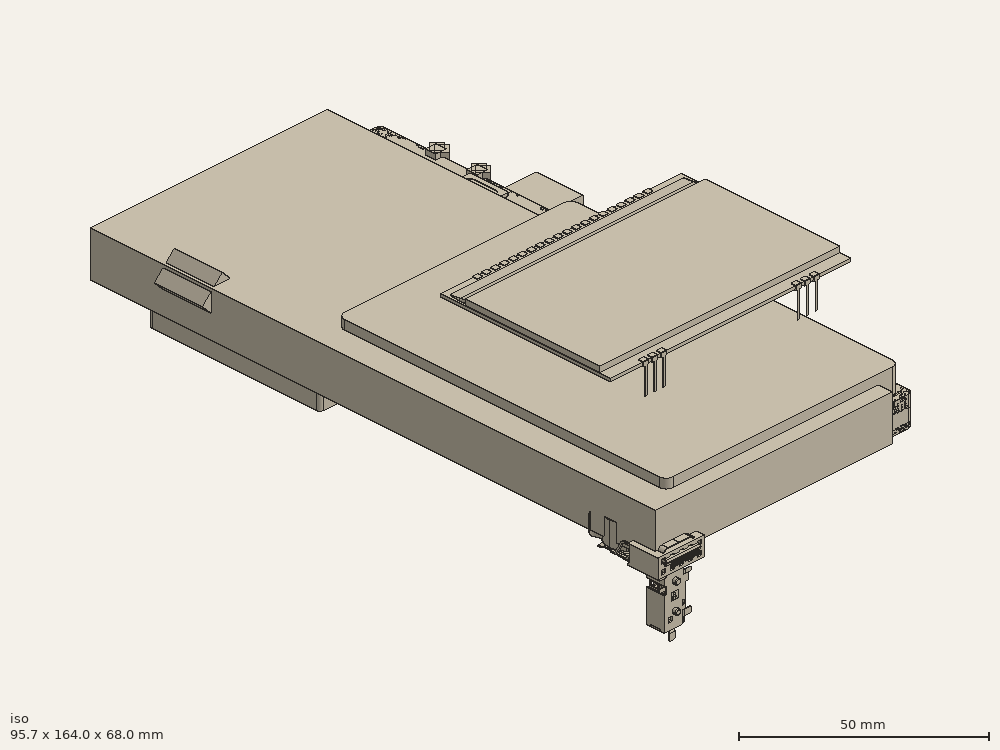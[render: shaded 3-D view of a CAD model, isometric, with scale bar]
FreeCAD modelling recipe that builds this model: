
FCSTD DOCUMENT  (FreeCAD 1.0R39109 (Git))
Label: case
License: All rights reserved
LicenseURL: https://en.wikipedia.org/wiki/All_rights_reserved
objects: Part::Feature×411, PartDesign::FeatureBase×405, PartDesign::Body×405, Part::Box×160, Part::MultiFuse×109, Part::Cylinder×108, Part::Cut×98, App::Part×86, Part::Extrusion×21, Part::Fillet×19, Sketcher::SketchObject×14, Part::Chamfer×13, Part::Compound×7, App::DocumentObjectGroup×3, Part::FeaturePython×1, Part::Sphere×1, Part::Face×1
note: 2192 computed .brp shape members not serialized (recipe doc carries the construction recipe); baked Part::Feature solids carry a one-line shape summary decoded from their .brp

FEATURE [Sketcher::SketchObject] Sketch
  ArcFitTolerance = 0
  FullyConstrained = false
  MakeInternals = false
  sketch-geometry (21):
    g0: ArcOfCircle CenterX=1.5 CenterY=149.5 CenterZ=0 NormalX=0 NormalY=0 NormalZ=1 AngleXU=0 Radius=1.5 StartAngle=1.5708 EndAngle=3.14159
    g1: LineSegment StartX=1.5 StartY=151 StartZ=0 EndX=68.5 EndY=151 EndZ=0
    g2: ArcOfCircle CenterX=68.5 CenterY=149.5 CenterZ=0 NormalX=0 NormalY=0 NormalZ=1 AngleXU=0 Radius=1.5 StartAngle=-8.9e-15 EndAngle=1.5708
    g3: LineSegment StartX=70 StartY=149.5 StartZ=0 EndX=70 EndY=1.5 EndZ=0
    g4: ArcOfCircle CenterX=68.5 CenterY=1.5 CenterZ=0 NormalX=0 NormalY=0 NormalZ=1 AngleXU=0 Radius=1.5 StartAngle=4.71239 EndAngle=6.28319
    g5: LineSegment StartX=68.5 StartY=0 StartZ=0 EndX=1.5 EndY=0 EndZ=0
    g6: ArcOfCircle CenterX=1.5 CenterY=1.5 CenterZ=0 NormalX=0 NormalY=0 NormalZ=1 AngleXU=0 Radius=1.5 StartAngle=3.14159 EndAngle=4.71239
    g7: LineSegment StartX=0 StartY=1.5 StartZ=0 EndX=0 EndY=149.5 EndZ=0
    g8: GeomPoint [constr] X=0 Y=151 Z=0
    g9: GeomPoint [constr] X=70 Y=0 Z=0
    g10: ArcOfCircle CenterX=4 CenterY=139.95 CenterZ=0 NormalX=0 NormalY=0 NormalZ=1 AngleXU=0 Radius=1 StartAngle=1.5708 EndAngle=3.14159
    g11: LineSegment StartX=4 StartY=140.95 StartZ=0 EndX=66 EndY=140.95 EndZ=0
    g12: ArcOfCircle CenterX=66 CenterY=139.95 CenterZ=0 NormalX=0 NormalY=0 NormalZ=1 AngleXU=0 Radius=1 StartAngle=-1.33e-14 EndAngle=1.5708
    g13: LineSegment StartX=67 StartY=139.95 StartZ=0 EndX=67 EndY=105.33 EndZ=0
    g14: ArcOfCircle CenterX=66 CenterY=105.33 CenterZ=0 NormalX=0 NormalY=0 NormalZ=1 AngleXU=0 Radius=1 StartAngle=4.71239 EndAngle=6.28319
    g15: LineSegment StartX=66 StartY=104.33 StartZ=0 EndX=4 EndY=104.33 EndZ=0
    g16: ArcOfCircle CenterX=4 CenterY=105.33 CenterZ=0 NormalX=0 NormalY=0 NormalZ=1 AngleXU=0 Radius=1 StartAngle=3.14159 EndAngle=4.71239
    g17: LineSegment StartX=3 StartY=105.33 StartZ=0 EndX=3 EndY=139.95 EndZ=0
    g18: GeomPoint [constr] X=3 Y=140.95 Z=0
    g19: GeomPoint [constr] X=67 Y=104.33 Z=0
    g20: LineSegment [constr] StartX=35 StartY=150.477 StartZ=0 EndX=35 EndY=137.578 EndZ=0
  constraints (50):
    c: Tangent(g0,g1) = 1.5708
    c: Tangent(g1,g2) = 1.5708
    c: Tangent(g2,g3) = 1.5708
    c: Tangent(g3,g4) = 1.5708
    c: Tangent(g4,g5) = 1.5708
    c: Tangent(g5,g6) = 1.5708
    c: Tangent(g6,g7) = 1.5708
    c: Tangent(g7,g0) = 1.5708
    c: Horizontal(g1)
    c: Horizontal(g5)
    c: Vertical(g3)
    c: Vertical(g7)
    c: Equal(g0,g2)
    c: Equal(g2,g4)
    c: Equal(g4,g6)
    c: PointOnObject(g8,g1)
    c: PointOnObject(g8,g7)
    c: PointOnObject(g9,g3)
    c: PointOnObject(g9,g5)
    c: PointOnObject(g9,g-1)
    c: Radius(g6) = 1.5
    c: DistanceY(g5,g0) = 151
    c: Vertical(g6,g-1)
    c: DistanceX(g0,g2) = 70
    c: Tangent(g10,g11) = 1.5708
    c: Tangent(g11,g12) = 1.5708
    c: Tangent(g12,g13) = 1.5708
    c: Tangent(g13,g14) = 1.5708
    c: Tangent(g14,g15) = 1.5708
    c: Tangent(g15,g16) = 1.5708
    c: Tangent(g16,g17) = 1.5708
    c: Tangent(g17,g10) = 1.5708
    c: Horizontal(g11)
    c: Horizontal(g15)
    c: Vertical(g13)
    c: Vertical(g17)
    c: Equal(g10,g12)
    c: Equal(g12,g14)
    c: Equal(g14,g16)
    c: PointOnObject(g18,g11)
    c: PointOnObject(g18,g17)
    c: PointOnObject(g19,g13)
    c: PointOnObject(g19,g15)
    c: Radius(g10) = 1
    c: DistanceY(g5,g15) = 104.33
    c: DistanceX(g10,g12) = 64
    c: DistanceY(g11,g1) = 10.05
    c: Vertical(g20)
    c: Symmetric(g2,g0,g20)
    c: Symmetric(g10,g11,g20)
FEATURE [Part::Extrusion] Extrude
  Base = -> Sketch
  Dir = (0,0,1)
  DirMode = 2
  FaceMakerClass = Part::FaceMakerBullseye
  FaceMakerMode = 3
  LengthFwd = 8
  LengthRev = 0
  Placement = pos=(0,0,8) rot=(0,0,1;0rad)
  Reversed = true
  Solid = true
  Symmetric = false
FEATURE [Sketcher::SketchObject] Sketch001
  ArcFitTolerance = 0
  AttachmentSupport = -> [Sketch]
  FullyConstrained = false
  MakeInternals = false
  MapMode = 2
  sketch-geometry (8):
    g0: ArcOfCircle CenterX=2 CenterY=149 CenterZ=0 NormalX=0 NormalY=0 NormalZ=1 AngleXU=0 Radius=1 StartAngle=1.5708 EndAngle=3.14159
    g1: LineSegment StartX=2 StartY=150 StartZ=0 EndX=68 EndY=150 EndZ=0
    g2: ArcOfCircle CenterX=68 CenterY=149 CenterZ=0 NormalX=0 NormalY=0 NormalZ=1 AngleXU=0 Radius=1 StartAngle=-9.8e-15 EndAngle=1.5708
    g3: LineSegment StartX=69 StartY=149 StartZ=0 EndX=69 EndY=99 EndZ=0
    g4: LineSegment StartX=69 StartY=99 StartZ=0 EndX=1 EndY=99 EndZ=0
    g5: LineSegment StartX=1 StartY=99 StartZ=0 EndX=1 EndY=149 EndZ=0
    g6: GeomPoint [constr] X=1 Y=150 Z=0
    g7: GeomPoint [constr] X=69 Y=99 Z=0
  constraints (16):
    c: Tangent(g0,g1) = 1.5708
    c: Tangent(g1,g2) = 1.5708
    c: Tangent(g2,g3) = 1.5708
    c: Tangent(g5,g0) = 1.5708
    c: Horizontal(g1)
    c: Horizontal(g4)
    c: Vertical(g3)
    c: Vertical(g5)
    c: Equal(g0,g2)
    c: PointOnObject(g6,g1)
    c: PointOnObject(g6,g5)
    c: PointOnObject(g7,g3)
    c: PointOnObject(g7,g4)
    c: Radius(g0) = 1
    c: Coincident(g5,g4)
    c: Coincident(g3,g4)
FEATURE [Part::Extrusion] Extrude001
  Base = -> Sketch001
  Dir = (0,0,1)
  DirMode = 2
  FaceMakerClass = Part::FaceMakerBullseye
  FaceMakerMode = 3
  LengthFwd = 11
  LengthRev = 0
  Placement = pos=(0,0,0.5) rot=(0,0,1;0rad)
  Solid = true
  Symmetric = false
FEATURE [Sketcher::SketchObject] Sketch002
  ArcFitTolerance = 0
  FullyConstrained = false
  MakeInternals = false
  sketch-geometry (20):
    g0: ArcOfCircle CenterX=3 CenterY=148 CenterZ=0 NormalX=0 NormalY=0 NormalZ=1 AngleXU=0 Radius=1 StartAngle=1.5708 EndAngle=3.14159
    g1: LineSegment StartX=3 StartY=149 StartZ=0 EndX=67 EndY=149 EndZ=0
    g2: ArcOfCircle CenterX=67 CenterY=148 CenterZ=0 NormalX=0 NormalY=0 NormalZ=1 AngleXU=0 Radius=1 StartAngle=5e-16 EndAngle=1.5708
    g3: LineSegment StartX=68 StartY=148 StartZ=0 EndX=68 EndY=101 EndZ=0
    g4: ArcOfCircle CenterX=67 CenterY=101 CenterZ=0 NormalX=0 NormalY=0 NormalZ=1 AngleXU=0 Radius=1 StartAngle=4.71239 EndAngle=6.28319
    g5: LineSegment StartX=67 StartY=100 StartZ=0 EndX=3 EndY=100 EndZ=0
    g6: ArcOfCircle CenterX=3 CenterY=101 CenterZ=0 NormalX=0 NormalY=0 NormalZ=1 AngleXU=0 Radius=1 StartAngle=3.14159 EndAngle=4.71239
    g7: LineSegment StartX=2 StartY=101 StartZ=0 EndX=2 EndY=148 EndZ=0
    g8: GeomPoint [constr] X=2 Y=149 Z=0
    g9: GeomPoint [constr] X=68 Y=100 Z=0
    g10: ArcOfCircle CenterX=3 CenterY=148 CenterZ=0 NormalX=0 NormalY=0 NormalZ=1 AngleXU=0 Radius=0.5 StartAngle=1.5708 EndAngle=3.14159
    g11: LineSegment StartX=3 StartY=148.5 StartZ=0 EndX=67 EndY=148.5 EndZ=0
    g12: ArcOfCircle CenterX=67 CenterY=148 CenterZ=0 NormalX=0 NormalY=0 NormalZ=1 AngleXU=0 Radius=0.5 StartAngle=-2.13e-14 EndAngle=1.5708
    g13: LineSegment StartX=67.5 StartY=148 StartZ=0 EndX=67.5 EndY=101 EndZ=0
    g14: ArcOfCircle CenterX=67 CenterY=101 CenterZ=0 NormalX=0 NormalY=0 NormalZ=1 AngleXU=0 Radius=0.5 StartAngle=4.71239 EndAngle=6.28319
    g15: LineSegment StartX=67 StartY=100.5 StartZ=0 EndX=3 EndY=100.5 EndZ=0
    g16: ArcOfCircle CenterX=3 CenterY=101 CenterZ=0 NormalX=0 NormalY=0 NormalZ=1 AngleXU=0 Radius=0.5 StartAngle=3.14159 EndAngle=4.71239
    g17: LineSegment StartX=2.5 StartY=101 StartZ=0 EndX=2.5 EndY=148 EndZ=0
    g18: GeomPoint [constr] X=2.5 Y=148.5 Z=0
    g19: GeomPoint [constr] X=67.5 Y=100.5 Z=0
  constraints (40):
    c: Tangent(g0,g1) = 1.5708
    c: Tangent(g1,g2) = 1.5708
    c: Tangent(g2,g3) = 1.5708
    c: Tangent(g3,g4) = 1.5708
    c: Tangent(g4,g5) = 1.5708
    c: Tangent(g5,g6) = 1.5708
    c: Tangent(g6,g7) = 1.5708
    c: Tangent(g7,g0) = 1.5708
    c: Horizontal(g1)
    c: Horizontal(g5)
    c: Vertical(g3)
    c: Vertical(g7)
    c: Equal(g0,g2)
    c: Equal(g2,g4)
    c: Equal(g4,g6)
    c: PointOnObject(g8,g1)
    c: PointOnObject(g8,g7)
    c: PointOnObject(g9,g3)
    c: PointOnObject(g9,g5)
    c: Radius(g2) = 1
    c: Tangent(g10,g11) = 1.5708
    c: Tangent(g11,g12) = 1.5708
    c: Tangent(g12,g13) = 1.5708
    c: Tangent(g13,g14) = 1.5708
    c: Tangent(g14,g15) = 1.5708
    c: Tangent(g15,g16) = 1.5708
    c: Tangent(g16,g17) = 1.5708
    c: Tangent(g17,g10) = 1.5708
    c: Horizontal(g11)
    c: Horizontal(g15)
    c: Vertical(g13)
    c: Vertical(g17)
    c: Equal(g10,g12)
    c: Equal(g12,g14)
    c: Equal(g14,g16)
    c: PointOnObject(g18,g11)
    c: PointOnObject(g18,g17)
    c: PointOnObject(g19,g13)
    c: PointOnObject(g19,g15)
    c: Radius(g10) = 0.5
FEATURE [Part::Extrusion] Extrude002
  Base = -> Sketch002
  Dir = (0,0,1)
  DirMode = 2
  FaceMakerClass = Part::FaceMakerBullseye
  FaceMakerMode = 3
  LengthFwd = 3
  LengthRev = 0
  Placement = pos=(0,0,0.2) rot=(0,0,1;0rad)
  Reversed = true
  Solid = true
  Symmetric = false
FEATURE [Sketcher::SketchObject] Sketch003
  ArcFitTolerance = 0
  FullyConstrained = false
  MakeInternals = false
  MapMode = 2
  sketch-geometry (10):
    g0: ArcOfCircle CenterX=3 CenterY=97 CenterZ=0 NormalX=0 NormalY=0 NormalZ=1 AngleXU=0 Radius=1 StartAngle=1.5708 EndAngle=3.14159
    g1: LineSegment StartX=3 StartY=98 StartZ=0 EndX=67 EndY=98 EndZ=0
    g2: ArcOfCircle CenterX=67 CenterY=97 CenterZ=0 NormalX=0 NormalY=0 NormalZ=1 AngleXU=0 Radius=1 StartAngle=-6.2e-15 EndAngle=1.5708
    g3: LineSegment StartX=68 StartY=97 StartZ=0 EndX=68 EndY=3 EndZ=0
    g4: ArcOfCircle CenterX=67 CenterY=3 CenterZ=0 NormalX=0 NormalY=0 NormalZ=1 AngleXU=0 Radius=1 StartAngle=4.71239 EndAngle=6.28319
    g5: LineSegment StartX=67 StartY=2 StartZ=0 EndX=3 EndY=2 EndZ=0
    g6: ArcOfCircle CenterX=3 CenterY=3 CenterZ=0 NormalX=0 NormalY=0 NormalZ=1 AngleXU=0 Radius=1 StartAngle=3.14159 EndAngle=4.71239
    g7: LineSegment StartX=2 StartY=3 StartZ=0 EndX=2 EndY=97 EndZ=0
    g8: GeomPoint [constr] X=2 Y=98 Z=0
    g9: GeomPoint [constr] X=68 Y=2 Z=0
  constraints (20):
    c: Tangent(g0,g1) = 1.5708
    c: Tangent(g1,g2) = 1.5708
    c: Tangent(g2,g3) = 1.5708
    c: Tangent(g3,g4) = 1.5708
    c: Tangent(g4,g5) = 1.5708
    c: Tangent(g5,g6) = 1.5708
    c: Tangent(g6,g7) = 1.5708
    c: Tangent(g7,g0) = 1.5708
    c: Horizontal(g1)
    c: Horizontal(g5)
    c: Vertical(g3)
    c: Vertical(g7)
    c: Equal(g0,g2)
    c: Equal(g2,g4)
    c: Equal(g4,g6)
    c: PointOnObject(g8,g1)
    c: PointOnObject(g8,g7)
    c: PointOnObject(g9,g3)
    c: PointOnObject(g9,g5)
    c: Radius(g2) = 1
FEATURE [Part::Extrusion] Extrude003
  Base = -> Sketch003
  Dir = (0,0,1)
  DirMode = 2
  FaceMakerClass = Part::FaceMakerBullseye
  FaceMakerMode = 3
  LengthFwd = 20
  LengthRev = 0
  Placement = pos=(0,0,15) rot=(0,0,1;0rad)
  Reversed = true
  Solid = true
  Symmetric = false
FEATURE [Sketcher::SketchObject] Sketch005
  ArcFitTolerance = 0
  FullyConstrained = true
  MakeInternals = false
  MapMode = 2
  sketch-geometry (10):
    g0: ArcOfCircle CenterX=-3 CenterY=2 CenterZ=0 NormalX=0 NormalY=0 NormalZ=1 AngleXU=0 Radius=1 StartAngle=1.5708 EndAngle=3.14159
    g1: LineSegment StartX=-3 StartY=3 StartZ=0 EndX=3 EndY=3 EndZ=0
    g2: ArcOfCircle CenterX=3 CenterY=2 CenterZ=0 NormalX=0 NormalY=0 NormalZ=1 AngleXU=0 Radius=1 StartAngle=2e-16 EndAngle=1.5708
    g3: LineSegment StartX=4 StartY=2 StartZ=0 EndX=4 EndY=-2 EndZ=0
    g4: ArcOfCircle CenterX=3 CenterY=-2 CenterZ=0 NormalX=0 NormalY=0 NormalZ=1 AngleXU=0 Radius=1 StartAngle=4.71239 EndAngle=6.28319
    g5: LineSegment StartX=3 StartY=-3 StartZ=0 EndX=-3 EndY=-3 EndZ=0
    g6: ArcOfCircle CenterX=-3 CenterY=-2 CenterZ=0 NormalX=0 NormalY=0 NormalZ=1 AngleXU=0 Radius=1 StartAngle=3.14159 EndAngle=4.71239
    g7: LineSegment StartX=-4 StartY=-2 StartZ=0 EndX=-4 EndY=2 EndZ=0
    g8: GeomPoint [constr] X=-4 Y=3 Z=0
    g9: GeomPoint [constr] X=4 Y=-3 Z=0
  constraints (22):
    c: Tangent(g0,g1) = 1.5708
    c: Tangent(g1,g2) = 1.5708
    c: Tangent(g2,g3) = 1.5708
    c: Tangent(g3,g4) = 1.5708
    c: Tangent(g4,g5) = 1.5708
    c: Tangent(g5,g6) = 1.5708
    c: Tangent(g6,g7) = 1.5708
    c: Tangent(g7,g0) = 1.5708
    c: Horizontal(g1)
    c: Horizontal(g5)
    c: Vertical(g3)
    c: Vertical(g7)
    c: Equal(g2,g4)
    c: PointOnObject(g8,g1)
    c: PointOnObject(g8,g7)
    c: PointOnObject(g9,g3)
    c: PointOnObject(g9,g5)
    c: Radius(g0) = 1
    c: DistanceX(g0,g2) = 8
    c: DistanceY(g5,g0) = 6
    c: Symmetric(g0,g2,g-2)
    c: Symmetric(g0,g5,g-1)
FEATURE [Part::Extrusion] Extrude006
  Base = -> Sketch005
  Dir = (0,0,1)
  DirMode = 2
  FaceMakerClass = Part::FaceMakerBullseye
  FaceMakerMode = 3
  LengthFwd = 2.5
  LengthRev = 1
  Solid = true
  Symmetric = false
FEATURE [Sketcher::SketchObject] Sketch007
  ArcFitTolerance = 0
  FullyConstrained = false
  MakeInternals = false
  Placement = pos=(0,0,0) rot=(0.57735,-0.57735,-0.57735;2.0944rad)
  sketch-geometry (6):
    g0: LineSegment StartX=-132.585 StartY=10 StartZ=0 EndX=-122.925 EndY=10 EndZ=0
    g1: LineSegment StartX=-132.585 StartY=10 StartZ=0 EndX=-132.585 EndY=5.74127 EndZ=0
    g2: LineSegment StartX=-122.925 StartY=10 StartZ=0 EndX=-122.925 EndY=5.74127 EndZ=0
    g3: LineSegment StartX=-131.085 StartY=4.24127 StartZ=0 EndX=-124.425 EndY=4.24127 EndZ=0
    g4: ArcOfCircle CenterX=-131.085 CenterY=5.74127 CenterZ=0 NormalX=0 NormalY=0 NormalZ=1 AngleXU=0 Radius=1.5 StartAngle=3.14159 EndAngle=4.71239
    g5: ArcOfCircle CenterX=-124.425 CenterY=5.74127 CenterZ=0 NormalX=0 NormalY=0 NormalZ=1 AngleXU=0 Radius=1.5 StartAngle=4.71239 EndAngle=6.28319
  constraints (12):
    c: Horizontal(g0)
    c: Coincident(g1,g0)
    c: Vertical(g1)
    c: Vertical(g2)
    c: Horizontal(g3)
    c: Radius(g4) = 1.5
    c: Tangent(g4,g1) = -1.5708
    c: Tangent(g4,g3) = -1.5708
    c: Tangent(g5,g2) = 1.5708
    c: Tangent(g5,g3) = -1.5708
    c: Radius(g5) = 1.5
    c: Coincident(g0,g2)
FEATURE [Part::Extrusion] Extrude008  label="USB"
  Base = -> Sketch007
  Dir = (-1,0,0)
  DirMode = 2
  FaceMakerClass = Part::FaceMakerBullseye
  FaceMakerMode = 3
  LengthFwd = 10
  LengthRev = 0
  Solid = true
  Symmetric = true
FEATURE [Part::Box] Box  label="LCD"
  AttacherType = Attacher::AttachEngine3D
  Height = 2.8
  Length = 67.8
  Placement = pos=(1,101,1.5) rot=(0,0,1;0rad)
  Width = 48
FEATURE [Sketcher::SketchObject] Sketch008
  ArcFitTolerance = 0
  FullyConstrained = false
  MakeInternals = false
  sketch-geometry (10):
    g0: ArcOfCircle CenterX=4 CenterY=93 CenterZ=0 NormalX=0 NormalY=0 NormalZ=1 AngleXU=0 Radius=2 StartAngle=1.5708 EndAngle=3.14159
    g1: LineSegment StartX=4 StartY=95 StartZ=0 EndX=66 EndY=95 EndZ=0
    g2: ArcOfCircle CenterX=66 CenterY=93 CenterZ=0 NormalX=0 NormalY=0 NormalZ=1 AngleXU=0 Radius=2 StartAngle=2.6e-15 EndAngle=1.5708
    g3: LineSegment StartX=68 StartY=93 StartZ=0 EndX=68 EndY=4 EndZ=0
    g4: ArcOfCircle CenterX=66 CenterY=4 CenterZ=0 NormalX=0 NormalY=0 NormalZ=1 AngleXU=0 Radius=2 StartAngle=4.71239 EndAngle=6.28319
    g5: LineSegment StartX=66 StartY=2 StartZ=0 EndX=4 EndY=2 EndZ=0
    g6: ArcOfCircle CenterX=4 CenterY=4 CenterZ=0 NormalX=0 NormalY=0 NormalZ=1 AngleXU=0 Radius=2 StartAngle=3.14159 EndAngle=4.71239
    g7: LineSegment StartX=2 StartY=4 StartZ=0 EndX=2 EndY=93 EndZ=0
    g8: GeomPoint [constr] X=2 Y=95 Z=0
    g9: GeomPoint [constr] X=68 Y=2 Z=0
  constraints (20):
    c: Tangent(g0,g1) = 1.5708
    c: Tangent(g1,g2) = 1.5708
    c: Tangent(g2,g3) = 1.5708
    c: Tangent(g3,g4) = 1.5708
    c: Tangent(g4,g5) = 1.5708
    c: Tangent(g5,g6) = 1.5708
    c: Tangent(g6,g7) = 1.5708
    c: Tangent(g7,g0) = 1.5708
    c: Horizontal(g1)
    c: Horizontal(g5)
    c: Vertical(g3)
    c: Vertical(g7)
    c: Equal(g0,g2)
    c: Equal(g2,g4)
    c: Equal(g4,g6)
    c: PointOnObject(g8,g1)
    c: PointOnObject(g8,g7)
    c: PointOnObject(g9,g3)
    c: PointOnObject(g9,g5)
    c: Radius(g0) = 2
FEATURE [Part::Extrusion] Extrude009
  Base = -> Sketch008
  Dir = (0,0,1)
  DirMode = 2
  FaceMakerClass = Part::FaceMakerBullseye
  FaceMakerMode = 3
  LengthFwd = 11
  LengthRev = 0
  Placement = pos=(0,0,3.5) rot=(0,0,1;0rad)
  Solid = true
  Symmetric = false
FEATURE [Sketcher::SketchObject] Sketch010
  ArcFitTolerance = 0
  FullyConstrained = false
  MakeInternals = false
  MapMode = 4
  Placement = pos=(0,0,0) rot=(0.707107,0,0.707107;3.14159rad)
  sketch-geometry (4):
    g0: LineSegment StartX=-2 StartY=3.98958 StartZ=0 EndX=-0.388491 EndY=3.98958 EndZ=0
    g1: LineSegment StartX=-0.388491 StartY=3.98958 StartZ=0 EndX=-1 EndY=-3 EndZ=0
    g2: LineSegment StartX=-1 StartY=-3 StartZ=0 EndX=-2 EndY=-3 EndZ=0
    g3: LineSegment StartX=-2 StartY=-3 StartZ=0 EndX=-2 EndY=3.98958 EndZ=0
  constraints (10):
    c: Horizontal(g0)
    c: Coincident(g0,g1)
    c: Coincident(g1,g2)
    c: Horizontal(g2)
    c: Coincident(g2,g3)
    c: Coincident(g3,g0)
    c: Vertical(g3)
    c: Angle(g1,g3) = 0.0872665
    c: DistanceX(g1,g-1) = 1
    c: DistanceY(g1,g-1) = 3
FEATURE [Part::Extrusion] Extrude011
  Base = -> Sketch010
  Dir = (1,0,-2e-16)
  DirMode = 2
  FaceMakerClass = Part::FaceMakerBullseye
  FaceMakerMode = 3
  LengthFwd = 10
  LengthRev = 0
  Solid = true
  Symmetric = true
FEATURE [Part::Cut] Cut004
  Base = -> Extrude006
  Tool = -> Extrude011
FEATURE [Part::Fillet] Fillet
  Base = -> Cut004
  EdgeLinks = -> Cut004 [Edge5,Edge7,Edge9,Edge11]
  Edges = 4 edges r=1: [Edge5,Edge7,Edge9,Edge11]
  Placement = pos=(0,0,1) rot=(0,0,1;0rad)
FEATURE [Part::Cylinder] Cylinder
  Angle = 360
  AttacherType = Attacher::AttachEngine3D
  FirstAngle = 0
  Height = 5
  Placement = pos=(0,0,2) rot=(0,0,1;0rad)
  Radius = 1.5
  SecondAngle = 0
FEATURE [Part::Fillet] Fillet002
  Base = -> Cylinder
  EdgeLinks = -> Cylinder [Edge3]
  Edges = 1 edges r=1: [Edge3]
  Placement = pos=(0,0,0.5) rot=(0,0,1;0rad)
FEATURE [Part::Box] Box001  label="Cube"
  AttacherType = Attacher::AttachEngine3D
  Height = 12
  Length = 67
  Placement = pos=(-5,-2,0) rot=(0,0,1;0rad)
  Width = 160
FEATURE [Sketcher::SketchObject] Sketch011
  ArcFitTolerance = 0
  AttachmentSupport = -> [Sketch]
  FullyConstrained = false
  MakeInternals = false
  MapMode = 2
  sketch-geometry (28):
    g0: ArcOfCircle CenterX=-3 CenterY=2 CenterZ=0 NormalX=0 NormalY=0 NormalZ=1 AngleXU=0 Radius=1.5 StartAngle=1.5708 EndAngle=3.14159
    g1: ArcOfCircle CenterX=3 CenterY=2 CenterZ=0 NormalX=0 NormalY=0 NormalZ=1 AngleXU=0 Radius=1.5 StartAngle=1e-16 EndAngle=1.5708
    g2: LineSegment StartX=4.5 StartY=2 StartZ=0 EndX=4.5 EndY=-2 EndZ=0
    g3: ArcOfCircle CenterX=3 CenterY=-2 CenterZ=0 NormalX=0 NormalY=0 NormalZ=1 AngleXU=0 Radius=1.5 StartAngle=4.71239 EndAngle=6.28319
    g4: ArcOfCircle CenterX=-3 CenterY=-2 CenterZ=0 NormalX=0 NormalY=0 NormalZ=1 AngleXU=0 Radius=1.5 StartAngle=3.14159 EndAngle=4.71239
    g5: LineSegment StartX=-4.5 StartY=-2 StartZ=0 EndX=-4.5 EndY=2 EndZ=0
    g6: GeomPoint [constr] X=-4.5 Y=3.5 Z=0
    g7: GeomPoint [constr] X=4.5 Y=-4 Z=0
    g8: LineSegment StartX=-2.8 StartY=-5 StartZ=0 EndX=-2.5 EndY=-5 EndZ=0
    g9: LineSegment StartX=-2.5 StartY=-5 StartZ=0 EndX=-2.5 EndY=-2 EndZ=0
    g10: LineSegment StartX=-2.5 StartY=-2 StartZ=0 EndX=-2.2 EndY=-2 EndZ=0
    g11: LineSegment StartX=-2.2 StartY=-2 StartZ=0 EndX=-2.2 EndY=-5 EndZ=0
    g12: LineSegment StartX=2.2 StartY=-5 StartZ=0 EndX=2.2 EndY=-2 EndZ=0
    g13: LineSegment StartX=2.2 StartY=-2 StartZ=0 EndX=2.5 EndY=-2 EndZ=0
    g14: LineSegment StartX=2.5 StartY=-2 StartZ=0 EndX=2.5 EndY=-5 EndZ=0
    g15: LineSegment StartX=2.5 StartY=-5 StartZ=0 EndX=2.8 EndY=-5 EndZ=0
    g16: LineSegment StartX=-2.2 StartY=-5 StartZ=0 EndX=-1.9 EndY=-5 EndZ=0
    g17: LineSegment StartX=-1.9 StartY=-5 StartZ=0 EndX=-1.9 EndY=-3.5 EndZ=0
    g18: LineSegment StartX=-1.9 StartY=-3.5 StartZ=0 EndX=1.9 EndY=-3.5 EndZ=0
    g19: LineSegment StartX=1.9 StartY=-3.5 StartZ=0 EndX=1.9 EndY=-5 EndZ=0
    g20: LineSegment StartX=1.9 StartY=-5 StartZ=0 EndX=2.2 EndY=-5 EndZ=0
    g21: LineSegment StartX=-2.8 StartY=-3.5 StartZ=0 EndX=-3 EndY=-3.5 EndZ=0
    g22: LineSegment StartX=-2.8 StartY=-3.5 StartZ=0 EndX=-2.8 EndY=-5 EndZ=0
    g23: LineSegment StartX=2.8 StartY=-3.5 StartZ=0 EndX=3 EndY=-3.5 EndZ=0
    g24: LineSegment StartX=2.8 StartY=-3.5 StartZ=0 EndX=2.8 EndY=-5 EndZ=0
    g25: ArcOfCircle CenterX=0 CenterY=2.95502 CenterZ=0 NormalX=0 NormalY=0 NormalZ=1 AngleXU=0 Radius=2.00619 StartAngle=0.275105 EndAngle=2.86649
    g26: LineSegment StartX=-3 StartY=3.5 StartZ=0 EndX=-1.93075 EndY=3.5 EndZ=0
    g27: LineSegment StartX=1.93075 StartY=3.5 StartZ=0 EndX=3 EndY=3.5 EndZ=0
  constraints (68):
    c: Tangent(g1,g2) = 1.5708
    c: Tangent(g2,g3) = 1.5708
    c: Tangent(g4,g5) = 1.5708
    c: Tangent(g5,g0) = 1.5708
    c: Vertical(g2)
    c: Horizontal(g8)
    c: Coincident(g8,g9)
    c: Vertical(g9)
    c: Coincident(g9,g10)
    c: Horizontal(g10)
    c: Coincident(g10,g11)
    c: Vertical(g11)
    c: Vertical(g12)
    c: Coincident(g12,g13)
    c: Horizontal(g13)
    c: Coincident(g13,g14)
    c: Vertical(g14)
    c: Coincident(g14,g15)
    c: Horizontal(g8,g11)
    c: Horizontal(g10,g12)
    c: Symmetric(g11,g12,g-2)
    c: DistanceX(g10,g10) = 0.3
    c: Coincident(g11,g16)
    c: Coincident(g16,g17)
    c: Vertical(g17)
    c: Coincident(g17,g18)
    c: Coincident(g18,g19)
    c: Vertical(g19)
    c: Coincident(g19,g20)
    c: Coincident(g20,g12)
    c: Horizontal(g20)
    c: Coincident(g21,g22)
    c: Coincident(g22,g8)
    c: Vertical(g22)
    c: Coincident(g23,g24)
    c: Coincident(g24,g15)
    c: Vertical(g24)
    c: Tangent(g3,g23) = -1.5708
    c: Tangent(g21,g4) = 1.5708
    c: Radius(g0) = 1.5
    c: Vertical(g5)
    c: Radius(g1) = 1.5
    c: Radius(g4) = 1.5
    c: Horizontal(g3,g23)
    c: Horizontal(g23,g18)
    c: Horizontal(g17,g21)
    c: Horizontal(g21,g4)
    c: Radius(g3) = 1.5
    c: Symmetric(g17,g18,g-2)
    c: Symmetric(g15,g8,g-2)
    c: Symmetric(g14,g8,g-2)
    c: Horizontal(g21)
    c: Horizontal(g18)
    c: Horizontal(g23)
    c: DistanceY(g4,g0) = 7
    c: DistanceX(g0,g1) = 9
    c: Symmetric(g0,g4,g-1)
    c: PointOnObject(g25,g-2)
    c: Horizontal(g0,g25)
    c: Horizontal(g25,g1)
    c: Horizontal(g1,g25)
    c: Coincident(g26,g0)
    c: Coincident(g26,g25)
    c: Horizontal(g26)
    c: Coincident(g27,g25)
    c: Coincident(g27,g1)
    c: Horizontal(g27)
    c: Tangent(g27,g1)
FEATURE [Part::Extrusion] Extrude012  label="CUT (type 01)"
  Base = -> Sketch011
  Dir = (0,0,1)
  DirMode = 2
  FaceMakerClass = Part::FaceMakerBullseye
  FaceMakerMode = 3
  LengthFwd = 10
  LengthRev = 0
  Solid = true
  Symmetric = false
FEATURE [PartDesign::FeatureBase] Clone
  BaseFeature = -> Extrude012
  Suppressed = false
FEATURE [PartDesign::Body] Body  label="C1-1"
  AllowCompound = false
  Group = -> [Clone]
  Origin = -> Origin046
  Placement = pos=(62.8,7,0) rot=(0,0,1;0rad)
  Tip = -> Clone
FEATURE [PartDesign::FeatureBase] Clone001
  BaseFeature = -> Extrude012
  Suppressed = false
FEATURE [PartDesign::Body] Body001  label="C2-1"
  AllowCompound = false
  Group = -> [Clone001]
  Origin = -> Origin047
  Placement = pos=(62.8,17,0) rot=(0,0,1;0rad)
  Tip = -> Clone001
FEATURE [PartDesign::FeatureBase] Clone002
  BaseFeature = -> Extrude012
  Suppressed = false
FEATURE [PartDesign::Body] Body002  label="C3-1"
  AllowCompound = false
  Group = -> [Clone002]
  Origin = -> Origin048
  Placement = pos=(62.8,27,0) rot=(0,0,1;0rad)
  Tip = -> Clone002
FEATURE [PartDesign::FeatureBase] Clone006
  BaseFeature = -> Extrude012
  Suppressed = false
FEATURE [PartDesign::Body] Body006  label="C4-1"
  AllowCompound = false
  Group = -> [Clone006]
  Origin = -> Origin052
  Placement = pos=(62.8,37,0) rot=(0,0,1;0rad)
  Tip = -> Clone006
FEATURE [PartDesign::FeatureBase] Clone007
  BaseFeature = -> Extrude012
  Suppressed = false
FEATURE [PartDesign::Body] Body007  label="C5-1"
  AllowCompound = false
  Group = -> [Clone007]
  Origin = -> Origin053
  Placement = pos=(62.8,49.98,0) rot=(0,0,1;0rad)
  Tip = -> Clone007
FEATURE [PartDesign::FeatureBase] Clone008
  BaseFeature = -> Extrude012
  Suppressed = false
FEATURE [PartDesign::Body] Body008  label="C6-1"
  AllowCompound = false
  Group = -> [Clone008]
  Origin = -> Origin054
  Placement = pos=(62.8,59.98,0) rot=(0,0,1;0rad)
  Tip = -> Clone008
FEATURE [PartDesign::FeatureBase] Clone009
  BaseFeature = -> Extrude012
  Suppressed = false
FEATURE [PartDesign::Body] Body009  label="C7-1"
  AllowCompound = false
  Group = -> [Clone009]
  Origin = -> Origin055
  Placement = pos=(62.8,69.98,0) rot=(0,0,1;0rad)
  Tip = -> Clone009
FEATURE [PartDesign::FeatureBase] Clone010
  BaseFeature = -> Extrude012
  Suppressed = false
FEATURE [PartDesign::Body] Body010  label="C8-1"
  AllowCompound = false
  Group = -> [Clone010]
  Origin = -> Origin056
  Placement = pos=(62.8,79.98,0) rot=(0,0,1;0rad)
  Tip = -> Clone010
FEATURE [PartDesign::FeatureBase] Clone011
  BaseFeature = -> Extrude012
  Suppressed = false
FEATURE [PartDesign::Body] Body011  label="C9-1"
  AllowCompound = false
  Group = -> [Clone011]
  Origin = -> Origin057
  Placement = pos=(62.8,89.98,0) rot=(0,0,1;0rad)
  Tip = -> Clone011
FEATURE [PartDesign::FeatureBase] Clone018
  BaseFeature = -> Extrude012
  Suppressed = false
FEATURE [PartDesign::Body] Body018  label="C5-2"
  AllowCompound = false
  Group = -> [Clone018]
  Origin = -> Origin064
  Placement = pos=(51.8,49.98,0) rot=(0,0,1;0rad)
  Tip = -> Clone018
FEATURE [PartDesign::FeatureBase] Clone020
  BaseFeature = -> Extrude012
  Suppressed = false
FEATURE [PartDesign::Body] Body020  label="C5-3"
  AllowCompound = false
  Group = -> [Clone020]
  Origin = -> Origin066
  Placement = pos=(40.8,49.98,0) rot=(0,0,1;0rad)
  Tip = -> Clone020
FEATURE [PartDesign::FeatureBase] Clone021
  BaseFeature = -> Extrude012
  Suppressed = false
FEATURE [PartDesign::Body] Body021  label="C5-4"
  AllowCompound = false
  Group = -> [Clone021]
  Origin = -> Origin067
  Placement = pos=(29.8,49.98,0) rot=(0,0,1;0rad)
  Tip = -> Clone021
FEATURE [PartDesign::FeatureBase] Clone022
  BaseFeature = -> Extrude012
  Suppressed = false
FEATURE [PartDesign::Body] Body022  label="C5-5"
  AllowCompound = false
  Group = -> [Clone022]
  Origin = -> Origin068
  Placement = pos=(18.8,49.98,0) rot=(0,0,1;0rad)
  Tip = -> Clone022
FEATURE [PartDesign::FeatureBase] Clone023
  BaseFeature = -> Extrude012
  Suppressed = false
FEATURE [PartDesign::Body] Body023  label="C5-6"
  AllowCompound = false
  Group = -> [Clone023]
  Origin = -> Origin069
  Placement = pos=(7.8,49.98,0) rot=(0,0,1;0rad)
  Tip = -> Clone023
FEATURE [PartDesign::FeatureBase] Clone028
  BaseFeature = -> Extrude012
  Suppressed = false
FEATURE [PartDesign::Body] Body028  label="C6-2"
  AllowCompound = false
  Group = -> [Clone028]
  Origin = -> Origin074
  Placement = pos=(51.8,59.98,0) rot=(0,0,1;0rad)
  Tip = -> Clone028
FEATURE [PartDesign::FeatureBase] Clone029
  BaseFeature = -> Extrude012
  Suppressed = false
FEATURE [PartDesign::Body] Body029  label="C6-3"
  AllowCompound = false
  Group = -> [Clone029]
  Origin = -> Origin075
  Placement = pos=(40.8,59.98,0) rot=(0,0,1;0rad)
  Tip = -> Clone029
FEATURE [PartDesign::FeatureBase] Clone030
  BaseFeature = -> Extrude012
  Suppressed = false
FEATURE [PartDesign::Body] Body030  label="C6-4"
  AllowCompound = false
  Group = -> [Clone030]
  Origin = -> Origin076
  Placement = pos=(29.8,59.98,0) rot=(0,0,1;0rad)
  Tip = -> Clone030
FEATURE [PartDesign::FeatureBase] Clone031
  BaseFeature = -> Extrude012
  Suppressed = false
FEATURE [PartDesign::Body] Body031  label="C6-5"
  AllowCompound = false
  Group = -> [Clone031]
  Origin = -> Origin077
  Placement = pos=(18.8,59.98,0) rot=(0,0,1;0rad)
  Tip = -> Clone031
FEATURE [PartDesign::FeatureBase] Clone032
  BaseFeature = -> Extrude012
  Suppressed = false
FEATURE [PartDesign::Body] Body032  label="C6-6"
  AllowCompound = false
  Group = -> [Clone032]
  Origin = -> Origin078
  Placement = pos=(7.8,59.98,0) rot=(0,0,1;0rad)
  Tip = -> Clone032
FEATURE [PartDesign::FeatureBase] Clone033
  BaseFeature = -> Extrude012
  Suppressed = false
FEATURE [PartDesign::Body] Body033  label="C7-2"
  AllowCompound = false
  Group = -> [Clone033]
  Origin = -> Origin079
  Placement = pos=(51.8,69.98,0) rot=(0,0,1;0rad)
  Tip = -> Clone033
FEATURE [PartDesign::FeatureBase] Clone034
  BaseFeature = -> Extrude012
  Suppressed = false
FEATURE [PartDesign::Body] Body034  label="C7-3"
  AllowCompound = false
  Group = -> [Clone034]
  Origin = -> Origin080
  Placement = pos=(40.8,69.98,0) rot=(0,0,1;0rad)
  Tip = -> Clone034
FEATURE [PartDesign::FeatureBase] Clone035
  BaseFeature = -> Extrude012
  Suppressed = false
FEATURE [PartDesign::Body] Body035  label="C7-4"
  AllowCompound = false
  Group = -> [Clone035]
  Origin = -> Origin081
  Placement = pos=(29.8,69.98,0) rot=(0,0,1;0rad)
  Tip = -> Clone035
FEATURE [PartDesign::FeatureBase] Clone036
  BaseFeature = -> Extrude012
  Suppressed = false
FEATURE [PartDesign::Body] Body036  label="C7-5"
  AllowCompound = false
  Group = -> [Clone036]
  Origin = -> Origin082
  Placement = pos=(18.8,69.98,0) rot=(0,0,1;0rad)
  Tip = -> Clone036
FEATURE [PartDesign::FeatureBase] Clone037
  BaseFeature = -> Extrude012
  Suppressed = false
FEATURE [PartDesign::Body] Body037  label="C7-6"
  AllowCompound = false
  Group = -> [Clone037]
  Origin = -> Origin083
  Placement = pos=(7.8,69.98,0) rot=(0,0,1;0rad)
  Tip = -> Clone037
FEATURE [PartDesign::FeatureBase] Clone038
  BaseFeature = -> Extrude012
  Suppressed = false
FEATURE [PartDesign::Body] Body038  label="C8-2"
  AllowCompound = false
  Group = -> [Clone038]
  Origin = -> Origin084
  Placement = pos=(51.8,79.98,0) rot=(0,0,1;0rad)
  Tip = -> Clone038
FEATURE [PartDesign::FeatureBase] Clone039
  BaseFeature = -> Extrude012
  Suppressed = false
FEATURE [PartDesign::Body] Body039  label="C8-3"
  AllowCompound = false
  Group = -> [Clone039]
  Origin = -> Origin085
  Placement = pos=(40.8,79.98,0) rot=(0,0,1;0rad)
  Tip = -> Clone039
FEATURE [PartDesign::FeatureBase] Clone040
  BaseFeature = -> Extrude012
  Suppressed = false
FEATURE [PartDesign::Body] Body040  label="C8-4"
  AllowCompound = false
  Group = -> [Clone040]
  Origin = -> Origin086
  Placement = pos=(29.8,79.98,0) rot=(0,0,1;0rad)
  Tip = -> Clone040
FEATURE [PartDesign::FeatureBase] Clone041
  BaseFeature = -> Extrude012
  Suppressed = false
FEATURE [PartDesign::Body] Body041  label="C8-5"
  AllowCompound = false
  Group = -> [Clone041]
  Origin = -> Origin087
  Placement = pos=(18.8,79.98,0) rot=(0,0,1;0rad)
  Tip = -> Clone041
FEATURE [PartDesign::FeatureBase] Clone042
  BaseFeature = -> Extrude012
  Suppressed = false
FEATURE [PartDesign::Body] Body042  label="C8-6"
  AllowCompound = false
  Group = -> [Clone042]
  Origin = -> Origin088
  Placement = pos=(7.8,79.98,0) rot=(0,0,1;0rad)
  Tip = -> Clone042
FEATURE [PartDesign::FeatureBase] Clone043
  BaseFeature = -> Extrude012
  Suppressed = false
FEATURE [PartDesign::Body] Body043  label="C9-2"
  AllowCompound = false
  Group = -> [Clone043]
  Origin = -> Origin089
  Placement = pos=(51.8,89.98,0) rot=(0,0,1;0rad)
  Tip = -> Clone043
FEATURE [PartDesign::FeatureBase] Clone044
  BaseFeature = -> Extrude012
  Suppressed = false
FEATURE [PartDesign::Body] Body044  label="C9-3"
  AllowCompound = false
  Group = -> [Clone044]
  Origin = -> Origin090
  Placement = pos=(40.8,89.98,0) rot=(0,0,1;0rad)
  Tip = -> Clone044
FEATURE [PartDesign::FeatureBase] Clone045
  BaseFeature = -> Extrude012
  Suppressed = false
FEATURE [PartDesign::Body] Body045  label="C9-4"
  AllowCompound = false
  Group = -> [Clone045]
  Origin = -> Origin091
  Placement = pos=(29.8,89.98,0) rot=(0,0,1;0rad)
  Tip = -> Clone045
FEATURE [PartDesign::FeatureBase] Clone046
  BaseFeature = -> Extrude012
  Suppressed = false
FEATURE [PartDesign::Body] Body046  label="C9-5"
  AllowCompound = false
  Group = -> [Clone046]
  Origin = -> Origin092
  Placement = pos=(18.8,89.98,0) rot=(0,0,1;0rad)
  Tip = -> Clone046
FEATURE [PartDesign::FeatureBase] Clone047
  BaseFeature = -> Extrude012
  Suppressed = false
FEATURE [PartDesign::Body] Body047  label="C9-6"
  AllowCompound = false
  Group = -> [Clone047]
  Origin = -> Origin093
  Placement = pos=(7.8,89.98,0) rot=(0,0,1;0rad)
  Tip = -> Clone047
FEATURE [Part::Cylinder] Cylinder001  label="LED01"
  Angle = 360
  AttacherType = Attacher::AttachEngine3D
  FirstAngle = 0
  Height = 10
  Placement = pos=(18.5,95.75,0) rot=(0,0,1;0rad)
  Radius = 0.5
  SecondAngle = 0
FEATURE [Part::Cylinder] Cylinder002
  Angle = 360
  AttacherType = Attacher::AttachEngine3D
  FirstAngle = 0
  Height = 5
  Placement = pos=(0,0,2) rot=(0,0,1;0rad)
  Radius = 1.5
  SecondAngle = 0
FEATURE [Part::Fillet] Fillet005
  Base = -> Cylinder002
  EdgeLinks = -> Cylinder002 [Edge3]
  Edges = 1 edges r=1: [Edge3]
  Placement = pos=(0,0,0.5) rot=(0,0,1;0rad)
FEATURE [Sketcher::SketchObject] Sketch012
  ArcFitTolerance = 0
  FullyConstrained = true
  MakeInternals = false
  MapMode = 2
  sketch-geometry (10):
    g0: ArcOfCircle CenterX=-4 CenterY=2 CenterZ=0 NormalX=0 NormalY=0 NormalZ=1 AngleXU=0 Radius=1 StartAngle=1.5708 EndAngle=3.14159
    g1: LineSegment StartX=-4 StartY=3 StartZ=0 EndX=4 EndY=3 EndZ=0
    g2: ArcOfCircle CenterX=4 CenterY=2 CenterZ=0 NormalX=0 NormalY=0 NormalZ=1 AngleXU=0 Radius=1 StartAngle=-5.071e-13 EndAngle=1.5708
    g3: LineSegment StartX=5 StartY=2 StartZ=0 EndX=5 EndY=-2 EndZ=0
    g4: ArcOfCircle CenterX=4 CenterY=-2 CenterZ=0 NormalX=0 NormalY=0 NormalZ=1 AngleXU=0 Radius=1 StartAngle=4.71239 EndAngle=6.28319
    g5: LineSegment StartX=4 StartY=-3 StartZ=0 EndX=-4 EndY=-3 EndZ=0
    g6: ArcOfCircle CenterX=-4 CenterY=-2 CenterZ=0 NormalX=0 NormalY=0 NormalZ=1 AngleXU=0 Radius=1 StartAngle=3.14159 EndAngle=4.71239
    g7: LineSegment StartX=-5 StartY=-2 StartZ=0 EndX=-5 EndY=2 EndZ=0
    g8: GeomPoint [constr] X=-5 Y=3 Z=0
    g9: GeomPoint [constr] X=5 Y=-3 Z=0
  constraints (22):
    c: Tangent(g0,g1) = 1.5708
    c: Tangent(g1,g2) = 1.5708
    c: Tangent(g2,g3) = 1.5708
    c: Tangent(g3,g4) = 1.5708
    c: Tangent(g4,g5) = 1.5708
    c: Tangent(g5,g6) = 1.5708
    c: Tangent(g6,g7) = 1.5708
    c: Tangent(g7,g0) = 1.5708
    c: Horizontal(g1)
    c: Horizontal(g5)
    c: Vertical(g3)
    c: Vertical(g7)
    c: Equal(g2,g4)
    c: PointOnObject(g8,g1)
    c: PointOnObject(g8,g7)
    c: PointOnObject(g9,g3)
    c: PointOnObject(g9,g5)
    c: Radius(g0) = 1
    c: DistanceX(g0,g2) = 10
    c: DistanceY(g5,g0) = 6
    c: Symmetric(g0,g2,g-2)
    c: Symmetric(g0,g5,g-1)
FEATURE [Part::Extrusion] Extrude013
  Base = -> Sketch012
  Dir = (0,0,1)
  DirMode = 2
  FaceMakerClass = Part::FaceMakerBullseye
  FaceMakerMode = 3
  LengthFwd = 2.5
  LengthRev = 1
  Solid = true
  Symmetric = false
FEATURE [Sketcher::SketchObject] Sketch013
  ArcFitTolerance = 0
  FullyConstrained = false
  MakeInternals = false
  MapMode = 4
  Placement = pos=(0,0,0) rot=(0.707107,0,0.707107;3.14159rad)
  sketch-geometry (4):
    g0: LineSegment StartX=-2 StartY=4.00488 StartZ=0 EndX=-0.387153 EndY=4.00488 EndZ=0
    g1: LineSegment StartX=-0.387153 StartY=4.00488 StartZ=0 EndX=-1 EndY=-3 EndZ=0
    g2: LineSegment StartX=-1 StartY=-3 StartZ=0 EndX=-2 EndY=-3 EndZ=0
    g3: LineSegment StartX=-2 StartY=-3 StartZ=0 EndX=-2 EndY=4.00488 EndZ=0
  constraints (10):
    c: Horizontal(g0)
    c: Coincident(g0,g1)
    c: Coincident(g1,g2)
    c: Horizontal(g2)
    c: Coincident(g2,g3)
    c: Coincident(g3,g0)
    c: Vertical(g3)
    c: Angle(g1,g3) = 0.0872665
    c: DistanceX(g1,g-1) = 1
    c: DistanceY(g1,g-1) = 3
FEATURE [Part::Extrusion] Extrude014
  Base = -> Sketch013
  Dir = (1,0,-2e-16)
  DirMode = 2
  FaceMakerClass = Part::FaceMakerBullseye
  FaceMakerMode = 3
  LengthFwd = 10
  LengthRev = 0
  Solid = true
  Symmetric = true
FEATURE [Part::Cut] Cut006
  Base = -> Extrude013
  Tool = -> Extrude014
FEATURE [Part::Fillet] Fillet004
  Base = -> Cut006
  EdgeLinks = -> Cut006 [Edge5,Edge7,Edge9,Edge11]
  Edges = 4 edges r=1: [Edge5,Edge7,Edge9,Edge11]
  Placement = pos=(0,0,1) rot=(0,0,1;0rad)
FEATURE [Sketcher::SketchObject] Sketch015
  ArcFitTolerance = 0
  FullyConstrained = false
  MakeInternals = false
  MapMode = 2
  sketch-geometry (28):
    g0: ArcOfCircle CenterX=-4 CenterY=2 CenterZ=0 NormalX=0 NormalY=0 NormalZ=1 AngleXU=0 Radius=1.5 StartAngle=1.5708 EndAngle=3.14159
    g1: ArcOfCircle CenterX=4 CenterY=2 CenterZ=0 NormalX=0 NormalY=0 NormalZ=1 AngleXU=0 Radius=1.5 StartAngle=1e-16 EndAngle=1.5708
    g2: LineSegment StartX=5.5 StartY=2 StartZ=0 EndX=5.5 EndY=-2.00004 EndZ=0
    g3: ArcOfCircle CenterX=4 CenterY=-2.00004 CenterZ=0 NormalX=0 NormalY=0 NormalZ=1 AngleXU=0 Radius=1.5 StartAngle=4.72004 EndAngle=6.28319
    g4: ArcOfCircle CenterX=-4 CenterY=-2 CenterZ=0 NormalX=0 NormalY=0 NormalZ=1 AngleXU=0 Radius=1.5 StartAngle=3.14159 EndAngle=4.71239
    g5: LineSegment StartX=-5.5 StartY=-2 StartZ=0 EndX=-5.5 EndY=2 EndZ=0
    g6: GeomPoint [constr] X=-5.5 Y=3.5 Z=0
    g7: GeomPoint [constr] X=5.5 Y=-4 Z=0
    g8: LineSegment StartX=-3.4 StartY=-5 StartZ=0 EndX=-3.4 EndY=-2.0211 EndZ=0
    g9: LineSegment StartX=-3.4 StartY=-2.0211 StartZ=0 EndX=-3.1 EndY=-2.0211 EndZ=0
    g10: LineSegment StartX=-3.1 StartY=-2.0211 StartZ=0 EndX=-3.1 EndY=-5 EndZ=0
    g11: LineSegment StartX=3.1 StartY=-5 StartZ=0 EndX=3.1 EndY=-2.0211 EndZ=0
    g12: LineSegment StartX=3.1 StartY=-2.0211 StartZ=0 EndX=3.4 EndY=-2.0211 EndZ=0
    g13: LineSegment StartX=3.4 StartY=-2.0211 StartZ=0 EndX=3.4 EndY=-5 EndZ=0
    g14: LineSegment StartX=-3.1 StartY=-5 StartZ=0 EndX=-2.8 EndY=-5 EndZ=0
    g15: LineSegment StartX=-2.8 StartY=-5 StartZ=0 EndX=-2.8 EndY=-3.5 EndZ=0
    g16: LineSegment StartX=-2.8 StartY=-3.5 StartZ=0 EndX=2.8 EndY=-3.5 EndZ=0
    g17: LineSegment StartX=2.8 StartY=-5 StartZ=0 EndX=3.1 EndY=-5 EndZ=0
    g18: LineSegment StartX=-4 StartY=-3.5 StartZ=0 EndX=-3.7 EndY=-3.5 EndZ=0
    g19: LineSegment StartX=-3.7 StartY=-3.5 StartZ=0 EndX=-3.7 EndY=-5 EndZ=0
    g20: LineSegment StartX=-3.7 StartY=-5 StartZ=0 EndX=-3.4 EndY=-5 EndZ=0
    g21: LineSegment StartX=3.4 StartY=-5 StartZ=0 EndX=3.7 EndY=-5 EndZ=0
    g22: LineSegment StartX=3.7 StartY=-5 StartZ=0 EndX=3.7 EndY=-3.5 EndZ=0
    g23: LineSegment StartX=3.7 StartY=-3.5 StartZ=0 EndX=4.01147 EndY=-3.5 EndZ=0
    g24: LineSegment StartX=2.8 StartY=-3.5 StartZ=0 EndX=2.8 EndY=-5 EndZ=0
    g25: ArcOfCircle CenterX=0 CenterY=2.98618 CenterZ=0 NormalX=0 NormalY=0 NormalZ=1 AngleXU=0 Radius=2 StartAngle=0.259822 EndAngle=2.88177
    g26: LineSegment StartX=-4 StartY=3.5 StartZ=0 EndX=-1.93287 EndY=3.5 EndZ=0
    g27: LineSegment StartX=1.93287 StartY=3.5 StartZ=0 EndX=4 EndY=3.5 EndZ=0
  constraints (67):
    c: Tangent(g1,g2) = 1.5708
    c: Tangent(g2,g3) = 1.5708
    c: Tangent(g4,g5) = 1.5708
    c: Tangent(g5,g0) = 1.5708
    c: Vertical(g2)
    c: Vertical(g5)
    c: Equal(g1,g3)
    c: PointOnObject(g6,g5)
    c: PointOnObject(g7,g2)
    c: Symmetric(g0,g1,g-2)
    c: Vertical(g8)
    c: Coincident(g8,g9)
    c: Horizontal(g9)
    c: Coincident(g9,g10)
    c: Vertical(g10)
    c: Vertical(g11)
    c: Coincident(g11,g12)
    c: Horizontal(g12)
    c: Coincident(g12,g13)
    c: Vertical(g13)
    c: Horizontal(g11,g13)
    c: Horizontal(g9,g11)
    c: Symmetric(g10,g11,g-2)
    c: DistanceX(g9,g9) = 0.3
    c: Coincident(g10,g14)
    c: Coincident(g14,g15)
    c: Vertical(g15)
    c: Coincident(g15,g16)
    c: Coincident(g17,g11)
    c: Symmetric(g15,g16,g-2)
    c: Radius(g0) = 1.5
    c: Tangent(g4,g18) = -1.5708
    c: Coincident(g18,g19)
    c: Vertical(g19)
    c: Coincident(g19,g20)
    c: Coincident(g20,g8)
    c: Coincident(g13,g21)
    c: Coincident(g21,g22)
    c: Vertical(g22)
    c: Coincident(g22,g23)
    c: Horizontal(g23)
    c: Coincident(g23,g3)
    c: Symmetric(g0,g4,g-1)
    c: Horizontal(g19,g8)
    c: Horizontal(g10,g14)
    c: Horizontal(g14,g17)
    c: Horizontal(g13,g21)
    c: Symmetric(g8,g13,g-2)
    c: Horizontal(g4,g18)
    c: Horizontal(g18,g15)
    c: Symmetric(g18,g22,g-2)
    c: Coincident(g24,g16)
    c: Coincident(g24,g17)
    c: Vertical(g24)
    c: PointOnObject(g25,g-2)
    c: Radius(g25) = 2
    c: DistanceY(g22,g1) = 7
    c: DistanceY(g4,g0) = 7
    c: DistanceX(g4,g2) = 11
    c: Horizontal(g0,g25)
    c: Horizontal(g25,g1)
    c: Coincident(g26,g0)
    c: Coincident(g26,g25)
    c: Horizontal(g26)
    c: Coincident(g27,g25)
    c: Coincident(g27,g1)
    c: Horizontal(g27)
FEATURE [Part::Extrusion] Extrude015  label="CUT (type 02)"
  Base = -> Sketch015
  Dir = (0,0,1)
  DirMode = 2
  FaceMakerClass = Part::FaceMakerBullseye
  FaceMakerMode = 3
  LengthFwd = 10
  LengthRev = 0
  Solid = true
  Symmetric = false
FEATURE [PartDesign::FeatureBase] Clone068
  BaseFeature = -> Extrude015
  Suppressed = false
FEATURE [PartDesign::Body] Body068  label="C1-2"
  AllowCompound = false
  Group = -> [Clone068]
  Origin = -> Origin114
  Placement = pos=(47.8,7,0) rot=(0,0,1;0rad)
  Tip = -> Clone068
FEATURE [PartDesign::FeatureBase] Clone070
  BaseFeature = -> Extrude015
  Suppressed = false
FEATURE [PartDesign::Body] Body070  label="C1-3"
  AllowCompound = false
  Group = -> [Clone070]
  Origin = -> Origin116
  Placement = pos=(34.8,7,0) rot=(0,0,1;0rad)
  Tip = -> Clone070
FEATURE [PartDesign::FeatureBase] Clone071
  BaseFeature = -> Extrude015
  Suppressed = false
FEATURE [PartDesign::Body] Body071  label="C1-4"
  AllowCompound = false
  Group = -> [Clone071]
  Origin = -> Origin117
  Placement = pos=(21.8,7,0) rot=(0,0,1;0rad)
  Tip = -> Clone071
FEATURE [PartDesign::FeatureBase] Clone072
  BaseFeature = -> Extrude015
  Suppressed = false
FEATURE [PartDesign::Body] Body072  label="C1-5"
  AllowCompound = false
  Group = -> [Clone072]
  Origin = -> Origin118
  Placement = pos=(8.8,7,0) rot=(0,0,1;0rad)
  Tip = -> Clone072
FEATURE [PartDesign::FeatureBase] Clone076
  BaseFeature = -> Extrude015
  Suppressed = false
FEATURE [PartDesign::Body] Body076  label="C2-2"
  AllowCompound = false
  Group = -> [Clone076]
  Origin = -> Origin122
  Placement = pos=(47.8,17,0) rot=(0,0,1;0rad)
  Tip = -> Clone076
FEATURE [PartDesign::FeatureBase] Clone077
  BaseFeature = -> Extrude015
  Suppressed = false
FEATURE [PartDesign::Body] Body077  label="C2-3"
  AllowCompound = false
  Group = -> [Clone077]
  Origin = -> Origin123
  Placement = pos=(34.8,17,0) rot=(0,0,1;0rad)
  Tip = -> Clone077
FEATURE [PartDesign::FeatureBase] Clone078
  BaseFeature = -> Extrude015
  Suppressed = false
FEATURE [PartDesign::Body] Body078  label="C2-4"
  AllowCompound = false
  Group = -> [Clone078]
  Origin = -> Origin124
  Placement = pos=(21.8,17,0) rot=(0,0,1;0rad)
  Tip = -> Clone078
FEATURE [PartDesign::FeatureBase] Clone079
  BaseFeature = -> Extrude015
  Suppressed = false
FEATURE [PartDesign::Body] Body079  label="C2-5"
  AllowCompound = false
  Group = -> [Clone079]
  Origin = -> Origin125
  Placement = pos=(8.8,17,0) rot=(0,0,1;0rad)
  Tip = -> Clone079
FEATURE [PartDesign::FeatureBase] Clone084
  BaseFeature = -> Extrude015
  Suppressed = false
FEATURE [PartDesign::Body] Body084  label="C3-2"
  AllowCompound = false
  Group = -> [Clone084]
  Origin = -> Origin130
  Placement = pos=(47.8,27,0) rot=(0,0,1;0rad)
  Tip = -> Clone084
FEATURE [PartDesign::FeatureBase] Clone085
  BaseFeature = -> Extrude015
  Suppressed = false
FEATURE [PartDesign::Body] Body085  label="C3-3"
  AllowCompound = false
  Group = -> [Clone085]
  Origin = -> Origin131
  Placement = pos=(34.8,27,0) rot=(0,0,1;0rad)
  Tip = -> Clone085
FEATURE [PartDesign::FeatureBase] Clone086
  BaseFeature = -> Extrude015
  Suppressed = false
FEATURE [PartDesign::Body] Body086  label="C3-4"
  AllowCompound = false
  Group = -> [Clone086]
  Origin = -> Origin132
  Placement = pos=(21.8,27,0) rot=(0,0,1;0rad)
  Tip = -> Clone086
FEATURE [PartDesign::FeatureBase] Clone087
  BaseFeature = -> Extrude015
  Suppressed = false
FEATURE [PartDesign::Body] Body087  label="C3-5"
  AllowCompound = false
  Group = -> [Clone087]
  Origin = -> Origin133
  Placement = pos=(8.8,27,0) rot=(0,0,1;0rad)
  Tip = -> Clone087
FEATURE [PartDesign::FeatureBase] Clone092
  BaseFeature = -> Extrude015
  Suppressed = false
FEATURE [PartDesign::Body] Body092  label="C4-2"
  AllowCompound = false
  Group = -> [Clone092]
  Origin = -> Origin138
  Placement = pos=(47.8,37,0) rot=(0,0,1;0rad)
  Tip = -> Clone092
FEATURE [PartDesign::FeatureBase] Clone093
  BaseFeature = -> Extrude015
  Suppressed = false
FEATURE [PartDesign::Body] Body093  label="C4-3"
  AllowCompound = false
  Group = -> [Clone093]
  Origin = -> Origin139
  Placement = pos=(34.8,37,0) rot=(0,0,1;0rad)
  Tip = -> Clone093
FEATURE [PartDesign::FeatureBase] Clone094
  BaseFeature = -> Extrude015
  Suppressed = false
FEATURE [PartDesign::Body] Body094  label="C4-4"
  AllowCompound = false
  Group = -> [Clone094]
  Origin = -> Origin140
  Placement = pos=(21.8,37,0) rot=(0,0,1;0rad)
  Tip = -> Clone094
FEATURE [PartDesign::FeatureBase] Clone095
  BaseFeature = -> Extrude015
  Suppressed = false
FEATURE [PartDesign::Body] Body095  label="C4-5"
  AllowCompound = false
  Group = -> [Clone095]
  Origin = -> Origin141
  Placement = pos=(8.8,37,0) rot=(0,0,1;0rad)
  Tip = -> Clone095
FEATURE [Part::Compound] Compound001  label="KEYS CUT"
  Links = -> [Extrude008,Body,Body001,Body002,Body006,Body007,Body008,Body009,Body010,Body011,Body018,Body020,Body021,Body022,Body023,Body028,Body029,Body030,Body031,Body032,Body033,Body034,Body035,Body036,Body037,Body038,Body039,Body040,Body041,Body042,Body043,Body044,Body045,Body046,Body047,Body070,Body071,Body072,Body076,Body077,Body078,Body079,Body084,Body085,Body086,Body087,Body092,Body093,Body094,Body095,+1 more]
FEATURE [Part::Cylinder] Cylinder003
  Angle = 360
  AttacherType = Attacher::AttachEngine3D
  FirstAngle = 0
  Height = 0.4
  Placement = pos=(0,3,3.1) rot=(0,0,1;0rad)
  Radius = 1.5
  SecondAngle = 0
FEATURE [Part::MultiFuse] Fusion  label="KEY (type 01)"
  Refine = true
  Shapes = -> [Fillet,Fillet002,Cylinder003]
FEATURE [PartDesign::FeatureBase] Clone003
  BaseFeature = -> Fusion
  Suppressed = false
FEATURE [PartDesign::Body] Body003  label="K2-1"
  AllowCompound = false
  Group = -> [Clone003]
  Origin = -> Origin049
  Placement = pos=(62.8,17,0.88) rot=(0,0,1;0rad)
  Tip = -> Clone003
FEATURE [PartDesign::FeatureBase] Clone004
  BaseFeature = -> Fusion
  Suppressed = false
FEATURE [PartDesign::Body] Body004  label="K1-1"
  AllowCompound = false
  Group = -> [Clone004]
  Origin = -> Origin050
  Placement = pos=(62.8,7,1) rot=(0,0,1;0rad)
  Tip = -> Clone004
FEATURE [PartDesign::FeatureBase] Clone005
  BaseFeature = -> Fusion
  Suppressed = false
FEATURE [PartDesign::Body] Body005  label="K3-1"
  AllowCompound = false
  Group = -> [Clone005]
  Origin = -> Origin051
  Placement = pos=(62.8,27,0.75) rot=(0,0,1;0rad)
  Tip = -> Clone005
FEATURE [PartDesign::FeatureBase] Clone012
  BaseFeature = -> Fusion
  Suppressed = false
FEATURE [PartDesign::Body] Body012  label="K4-1"
  AllowCompound = false
  Group = -> [Clone012]
  Origin = -> Origin058
  Placement = pos=(62.8,37,0.63) rot=(0,0,1;0rad)
  Tip = -> Clone012
FEATURE [PartDesign::FeatureBase] Clone013
  BaseFeature = -> Fusion
  Suppressed = false
FEATURE [PartDesign::Body] Body013  label="K5-1"
  AllowCompound = false
  Group = -> [Clone013]
  Origin = -> Origin059
  Placement = pos=(62.8,49.98,0.5) rot=(0,0,1;0rad)
  Tip = -> Clone013
FEATURE [PartDesign::FeatureBase] Clone014
  BaseFeature = -> Fusion
  Suppressed = false
FEATURE [PartDesign::Body] Body014  label="K6-1"
  AllowCompound = false
  Group = -> [Clone014]
  Origin = -> Origin060
  Placement = pos=(62.8,59.98,0.38) rot=(0,0,1;0rad)
  Tip = -> Clone014
FEATURE [PartDesign::FeatureBase] Clone015
  BaseFeature = -> Fusion
  Suppressed = false
FEATURE [PartDesign::Body] Body015  label="K7-1"
  AllowCompound = false
  Group = -> [Clone015]
  Origin = -> Origin061
  Placement = pos=(62.8,69.98,0.25) rot=(0,0,1;0rad)
  Tip = -> Clone015
FEATURE [PartDesign::FeatureBase] Clone016
  BaseFeature = -> Fusion
  Suppressed = false
FEATURE [PartDesign::Body] Body016  label="K8-1"
  AllowCompound = false
  Group = -> [Clone016]
  Origin = -> Origin062
  Placement = pos=(62.8,79.98,0.13) rot=(0,0,1;0rad)
  Tip = -> Clone016
FEATURE [PartDesign::FeatureBase] Clone017
  BaseFeature = -> Fusion
  Suppressed = false
FEATURE [PartDesign::Body] Body017  label="K9-1"
  AllowCompound = false
  Group = -> [Clone017]
  Origin = -> Origin063
  Placement = pos=(62.8,89.98,0) rot=(0,0,1;0rad)
  Tip = -> Clone017
FEATURE [PartDesign::FeatureBase] Clone019
  BaseFeature = -> Fusion
  Suppressed = false
FEATURE [PartDesign::Body] Body019  label="K5-2"
  AllowCompound = false
  Group = -> [Clone019]
  Origin = -> Origin065
  Placement = pos=(51.8,49.98,0) rot=(0,0,1;0rad)
  Tip = -> Clone019
FEATURE [PartDesign::FeatureBase] Clone024
  BaseFeature = -> Fusion
  Suppressed = false
FEATURE [PartDesign::Body] Body024  label="K5-3"
  AllowCompound = false
  Group = -> [Clone024]
  Origin = -> Origin070
  Placement = pos=(40.8,49.98,0) rot=(0,0,1;0rad)
  Tip = -> Clone024
FEATURE [PartDesign::FeatureBase] Clone025
  BaseFeature = -> Fusion
  Suppressed = false
FEATURE [PartDesign::Body] Body025  label="K5-4"
  AllowCompound = false
  Group = -> [Clone025]
  Origin = -> Origin071
  Placement = pos=(29.8,49.98,0) rot=(0,0,1;0rad)
  Tip = -> Clone025
FEATURE [PartDesign::FeatureBase] Clone026
  BaseFeature = -> Fusion
  Suppressed = false
FEATURE [PartDesign::Body] Body026  label="K5-5"
  AllowCompound = false
  Group = -> [Clone026]
  Origin = -> Origin072
  Placement = pos=(18.8,49.98,0) rot=(0,0,1;0rad)
  Tip = -> Clone026
FEATURE [PartDesign::FeatureBase] Clone027
  BaseFeature = -> Fusion
  Suppressed = false
FEATURE [PartDesign::Body] Body027  label="K5-6"
  AllowCompound = false
  Group = -> [Clone027]
  Origin = -> Origin073
  Placement = pos=(7.8,49.98,0) rot=(0,0,1;0rad)
  Tip = -> Clone027
FEATURE [PartDesign::FeatureBase] Clone048
  BaseFeature = -> Fusion
  Suppressed = false
FEATURE [PartDesign::Body] Body048  label="K6-2"
  AllowCompound = false
  Group = -> [Clone048]
  Origin = -> Origin094
  Placement = pos=(51.8,59.98,0) rot=(0,0,1;0rad)
  Tip = -> Clone048
FEATURE [PartDesign::FeatureBase] Clone049
  BaseFeature = -> Fusion
  Suppressed = false
FEATURE [PartDesign::Body] Body049  label="K6-3"
  AllowCompound = false
  Group = -> [Clone049]
  Origin = -> Origin095
  Placement = pos=(40.8,59.98,0) rot=(0,0,1;0rad)
  Tip = -> Clone049
FEATURE [PartDesign::FeatureBase] Clone050
  BaseFeature = -> Fusion
  Suppressed = false
FEATURE [PartDesign::Body] Body050  label="K6-4"
  AllowCompound = false
  Group = -> [Clone050]
  Origin = -> Origin096
  Placement = pos=(29.8,59.98,0) rot=(0,0,1;0rad)
  Tip = -> Clone050
FEATURE [PartDesign::FeatureBase] Clone051
  BaseFeature = -> Fusion
  Suppressed = false
FEATURE [PartDesign::Body] Body051  label="K6-5"
  AllowCompound = false
  Group = -> [Clone051]
  Origin = -> Origin097
  Placement = pos=(18.8,59.98,0) rot=(0,0,1;0rad)
  Tip = -> Clone051
FEATURE [PartDesign::FeatureBase] Clone052
  BaseFeature = -> Fusion
  Suppressed = false
FEATURE [PartDesign::Body] Body052  label="K6-6"
  AllowCompound = false
  Group = -> [Clone052]
  Origin = -> Origin098
  Placement = pos=(7.8,59.98,0) rot=(0,0,1;0rad)
  Tip = -> Clone052
FEATURE [PartDesign::FeatureBase] Clone053
  BaseFeature = -> Fusion
  Suppressed = false
FEATURE [PartDesign::Body] Body053  label="K7-2"
  AllowCompound = false
  Group = -> [Clone053]
  Origin = -> Origin099
  Placement = pos=(51.8,69.98,0) rot=(0,0,1;0rad)
  Tip = -> Clone053
FEATURE [PartDesign::FeatureBase] Clone054
  BaseFeature = -> Fusion
  Suppressed = false
FEATURE [PartDesign::Body] Body054  label="K7-3"
  AllowCompound = false
  Group = -> [Clone054]
  Origin = -> Origin100
  Placement = pos=(40.8,69.98,0) rot=(0,0,1;0rad)
  Tip = -> Clone054
FEATURE [PartDesign::FeatureBase] Clone055
  BaseFeature = -> Fusion
  Suppressed = false
FEATURE [PartDesign::Body] Body055  label="K7-4"
  AllowCompound = false
  Group = -> [Clone055]
  Origin = -> Origin101
  Placement = pos=(29.8,69.98,0) rot=(0,0,1;0rad)
  Tip = -> Clone055
FEATURE [PartDesign::FeatureBase] Clone056
  BaseFeature = -> Fusion
  Suppressed = false
FEATURE [PartDesign::Body] Body056  label="K7-5"
  AllowCompound = false
  Group = -> [Clone056]
  Origin = -> Origin102
  Placement = pos=(18.8,69.98,0) rot=(0,0,1;0rad)
  Tip = -> Clone056
FEATURE [PartDesign::FeatureBase] Clone057
  BaseFeature = -> Fusion
  Suppressed = false
FEATURE [PartDesign::Body] Body057  label="K7-6"
  AllowCompound = false
  Group = -> [Clone057]
  Origin = -> Origin103
  Placement = pos=(7.8,69.98,0) rot=(0,0,1;0rad)
  Tip = -> Clone057
FEATURE [PartDesign::FeatureBase] Clone058
  BaseFeature = -> Fusion
  Suppressed = false
FEATURE [PartDesign::Body] Body058  label="K8-2"
  AllowCompound = false
  Group = -> [Clone058]
  Origin = -> Origin104
  Placement = pos=(51.8,79.98,0) rot=(0,0,1;0rad)
  Tip = -> Clone058
FEATURE [PartDesign::FeatureBase] Clone059
  BaseFeature = -> Fusion
  Suppressed = false
FEATURE [PartDesign::Body] Body059  label="K8-3"
  AllowCompound = false
  Group = -> [Clone059]
  Origin = -> Origin105
  Placement = pos=(40.8,79.98,0) rot=(0,0,1;0rad)
  Tip = -> Clone059
FEATURE [PartDesign::FeatureBase] Clone060
  BaseFeature = -> Fusion
  Suppressed = false
FEATURE [PartDesign::Body] Body060  label="K8-4"
  AllowCompound = false
  Group = -> [Clone060]
  Origin = -> Origin106
  Placement = pos=(29.8,79.98,0) rot=(0,0,1;0rad)
  Tip = -> Clone060
FEATURE [PartDesign::FeatureBase] Clone061
  BaseFeature = -> Fusion
  Suppressed = false
FEATURE [PartDesign::Body] Body061  label="K8-5"
  AllowCompound = false
  Group = -> [Clone061]
  Origin = -> Origin107
  Placement = pos=(18.8,79.98,0) rot=(0,0,1;0rad)
  Tip = -> Clone061
FEATURE [PartDesign::FeatureBase] Clone062
  BaseFeature = -> Fusion
  Suppressed = false
FEATURE [PartDesign::Body] Body062  label="K8-6"
  AllowCompound = false
  Group = -> [Clone062]
  Origin = -> Origin108
  Placement = pos=(7.8,79.98,0) rot=(0,0,1;0rad)
  Tip = -> Clone062
FEATURE [PartDesign::FeatureBase] Clone063
  BaseFeature = -> Fusion
  Suppressed = false
FEATURE [PartDesign::Body] Body063  label="K9-2"
  AllowCompound = false
  Group = -> [Clone063]
  Origin = -> Origin109
  Placement = pos=(51.8,89.98,0) rot=(0,0,1;0rad)
  Tip = -> Clone063
FEATURE [PartDesign::FeatureBase] Clone064
  BaseFeature = -> Fusion
  Suppressed = false
FEATURE [PartDesign::Body] Body064  label="K9-3"
  AllowCompound = false
  Group = -> [Clone064]
  Origin = -> Origin110
  Placement = pos=(40.8,89.98,0) rot=(0,0,1;0rad)
  Tip = -> Clone064
FEATURE [PartDesign::FeatureBase] Clone065
  BaseFeature = -> Fusion
  Suppressed = false
FEATURE [PartDesign::Body] Body065  label="K9-4"
  AllowCompound = false
  Group = -> [Clone065]
  Origin = -> Origin111
  Placement = pos=(29.8,89.98,0) rot=(0,0,1;0rad)
  Tip = -> Clone065
FEATURE [PartDesign::FeatureBase] Clone066
  BaseFeature = -> Fusion
  Suppressed = false
FEATURE [PartDesign::Body] Body066  label="K9-5"
  AllowCompound = false
  Group = -> [Clone066]
  Origin = -> Origin112
  Placement = pos=(18.8,89.98,0) rot=(0,0,1;0rad)
  Tip = -> Clone066
FEATURE [PartDesign::FeatureBase] Clone067
  BaseFeature = -> Fusion
  Suppressed = false
FEATURE [PartDesign::Body] Body067  label="K9-6"
  AllowCompound = false
  Group = -> [Clone067]
  Origin = -> Origin113
  Placement = pos=(7.8,89.98,0) rot=(0,0,1;0rad)
  Tip = -> Clone067
FEATURE [Part::Cylinder] Cylinder004
  Angle = 360
  AttacherType = Attacher::AttachEngine3D
  FirstAngle = 0
  Height = 0.4
  Placement = pos=(0,3,3.1) rot=(0,0,1;0rad)
  Radius = 1.5
  SecondAngle = 0
FEATURE [Part::MultiFuse] Fusion003  label="KEY (type 02)"
  Refine = true
  Shapes = -> [Fillet004,Fillet005,Cylinder004]
FEATURE [PartDesign::FeatureBase] Clone069
  BaseFeature = -> Fusion003
  Suppressed = false
FEATURE [PartDesign::Body] Body069  label="K1-2"
  AllowCompound = false
  Group = -> [Clone069]
  Origin = -> Origin115
  Placement = pos=(47.8,7,0) rot=(0,0,1;0rad)
  Tip = -> Clone069
FEATURE [PartDesign::FeatureBase] Clone073
  BaseFeature = -> Fusion003
  Suppressed = false
FEATURE [PartDesign::Body] Body073  label="K1-3"
  AllowCompound = false
  Group = -> [Clone073]
  Origin = -> Origin119
  Placement = pos=(34.8,7,0) rot=(0,0,1;0rad)
  Tip = -> Clone073
FEATURE [PartDesign::FeatureBase] Clone074
  BaseFeature = -> Fusion003
  Suppressed = false
FEATURE [PartDesign::Body] Body074  label="K1-4"
  AllowCompound = false
  Group = -> [Clone074]
  Origin = -> Origin120
  Placement = pos=(21.8,7,0) rot=(0,0,1;0rad)
  Tip = -> Clone074
FEATURE [PartDesign::FeatureBase] Clone075
  BaseFeature = -> Fusion003
  Suppressed = false
FEATURE [PartDesign::Body] Body075  label="K1-5"
  AllowCompound = false
  Group = -> [Clone075]
  Origin = -> Origin121
  Placement = pos=(8.8,7,0) rot=(0,0,1;0rad)
  Tip = -> Clone075
FEATURE [PartDesign::FeatureBase] Clone080
  BaseFeature = -> Fusion003
  Suppressed = false
FEATURE [PartDesign::Body] Body080  label="K2-2"
  AllowCompound = false
  Group = -> [Clone080]
  Origin = -> Origin126
  Placement = pos=(47.8,17,0) rot=(0,0,1;0rad)
  Tip = -> Clone080
FEATURE [PartDesign::FeatureBase] Clone081
  BaseFeature = -> Fusion003
  Suppressed = false
FEATURE [PartDesign::Body] Body081  label="K2-3"
  AllowCompound = false
  Group = -> [Clone081]
  Origin = -> Origin127
  Placement = pos=(34.8,17,0) rot=(0,0,1;0rad)
  Tip = -> Clone081
FEATURE [PartDesign::FeatureBase] Clone082
  BaseFeature = -> Fusion003
  Suppressed = false
FEATURE [PartDesign::Body] Body082  label="K2-4"
  AllowCompound = false
  Group = -> [Clone082]
  Origin = -> Origin128
  Placement = pos=(21.8,17,0) rot=(0,0,1;0rad)
  Tip = -> Clone082
FEATURE [PartDesign::FeatureBase] Clone083
  BaseFeature = -> Fusion003
  Suppressed = false
FEATURE [PartDesign::Body] Body083  label="K2-5"
  AllowCompound = false
  Group = -> [Clone083]
  Origin = -> Origin129
  Placement = pos=(8.8,17,0) rot=(0,0,1;0rad)
  Tip = -> Clone083
FEATURE [PartDesign::FeatureBase] Clone088
  BaseFeature = -> Fusion003
  Suppressed = false
FEATURE [PartDesign::Body] Body088  label="K3-2"
  AllowCompound = false
  Group = -> [Clone088]
  Origin = -> Origin134
  Placement = pos=(47.8,27,0) rot=(0,0,1;0rad)
  Tip = -> Clone088
FEATURE [PartDesign::FeatureBase] Clone089
  BaseFeature = -> Fusion003
  Suppressed = false
FEATURE [PartDesign::Body] Body089  label="K3-3"
  AllowCompound = false
  Group = -> [Clone089]
  Origin = -> Origin135
  Placement = pos=(34.8,27,0) rot=(0,0,1;0rad)
  Tip = -> Clone089
FEATURE [PartDesign::FeatureBase] Clone090
  BaseFeature = -> Fusion003
  Suppressed = false
FEATURE [PartDesign::Body] Body090  label="K3-4"
  AllowCompound = false
  Group = -> [Clone090]
  Origin = -> Origin136
  Placement = pos=(21.8,27,0) rot=(0,0,1;0rad)
  Tip = -> Clone090
FEATURE [PartDesign::FeatureBase] Clone091
  BaseFeature = -> Fusion003
  Suppressed = false
FEATURE [PartDesign::Body] Body091  label="K3-5"
  AllowCompound = false
  Group = -> [Clone091]
  Origin = -> Origin137
  Placement = pos=(8.8,27,0) rot=(0,0,1;0rad)
  Tip = -> Clone091
FEATURE [PartDesign::FeatureBase] Clone096
  BaseFeature = -> Fusion003
  Suppressed = false
FEATURE [PartDesign::Body] Body096  label="K4-2"
  AllowCompound = false
  Group = -> [Clone096]
  Origin = -> Origin142
  Placement = pos=(47.8,37,0) rot=(0,0,1;0rad)
  Tip = -> Clone096
FEATURE [PartDesign::FeatureBase] Clone097
  BaseFeature = -> Fusion003
  Suppressed = false
FEATURE [PartDesign::Body] Body097  label="K4-3"
  AllowCompound = false
  Group = -> [Clone097]
  Origin = -> Origin143
  Placement = pos=(34.8,37,0) rot=(0,0,1;0rad)
  Tip = -> Clone097
FEATURE [PartDesign::FeatureBase] Clone098
  BaseFeature = -> Fusion003
  Suppressed = false
FEATURE [PartDesign::Body] Body098  label="K4-4"
  AllowCompound = false
  Group = -> [Clone098]
  Origin = -> Origin144
  Placement = pos=(21.8,37,0) rot=(0,0,1;0rad)
  Tip = -> Clone098
FEATURE [PartDesign::FeatureBase] Clone099
  BaseFeature = -> Fusion003
  Suppressed = false
FEATURE [PartDesign::Body] Body099  label="K4-5"
  AllowCompound = false
  Group = -> [Clone099]
  Origin = -> Origin145
  Placement = pos=(8.8,37,0) rot=(0,0,1;0rad)
  Tip = -> Clone099
FEATURE [Part::Compound] Compound002  label="KEYS"
  Links = -> [Body069,Body073,Body074,Body075,Body080,Body081,Body082,Body083,Body088,Body089,Body090,Body091,Body096,Body097,Body098,Body099,Body003,Body004,Body005,Body012,Body013,Body014,Body015,Body016,Body017,Body019,Body024,Body025,Body026,Body027,Body048,Body049,Body050,Body051,Body052,Body053,Body054,Body055,Body056,Body057,Body058,Body059,Body060,Body061,Body062,Body063,Body064,Body065,Body066,Body067]
FEATURE [Sketcher::SketchObject] Sketch016  label="faceplate"
  ArcFitTolerance = 0
  FullyConstrained = false
  MakeInternals = false
  sketch-geometry (33):
    g0: ArcOfCircle CenterX=67 CenterY=97 CenterZ=0 NormalX=0 NormalY=0 NormalZ=1 AngleXU=0 Radius=0.5 StartAngle=-1.33e-14 EndAngle=1.5708
    g1: LineSegment StartX=67.5 StartY=97 StartZ=0 EndX=67.5 EndY=3 EndZ=0
    g2: ArcOfCircle CenterX=67 CenterY=3 CenterZ=0 NormalX=0 NormalY=0 NormalZ=1 AngleXU=0 Radius=0.5 StartAngle=4.71239 EndAngle=6.28319
    g3: LineSegment StartX=67 StartY=2.5 StartZ=0 EndX=3 EndY=2.5 EndZ=0
    g4: ArcOfCircle CenterX=3 CenterY=3 CenterZ=0 NormalX=0 NormalY=0 NormalZ=1 AngleXU=0 Radius=0.5 StartAngle=3.14159 EndAngle=4.71239
    g5: LineSegment StartX=2.5 StartY=3 StartZ=0 EndX=2.5 EndY=97 EndZ=0
    g6: ArcOfCircle CenterX=3 CenterY=97 CenterZ=0 NormalX=0 NormalY=0 NormalZ=1 AngleXU=0 Radius=0.5 StartAngle=1.5708 EndAngle=3.14159
    g7: LineSegment StartX=3 StartY=97.5 StartZ=0 EndX=67 EndY=97.5 EndZ=0
    g8: GeomPoint [constr] X=67.5 Y=97.5 Z=0
    g9: GeomPoint [constr] X=2.5 Y=2.5 Z=0
    g10: ArcOfCircle CenterX=65.8448 CenterY=9.10476 CenterZ=0 NormalX=0 NormalY=0 NormalZ=1 AngleXU=0 Radius=1.2 StartAngle=-9e-16 EndAngle=1.5708
    g11: LineSegment StartX=67.0448 StartY=9.10476 StartZ=0 EndX=67.0448 EndY=5.00476 EndZ=0
    g12: ArcOfCircle CenterX=65.8448 CenterY=5.00476 CenterZ=0 NormalX=0 NormalY=0 NormalZ=1 AngleXU=0 Radius=1.2 StartAngle=4.71239 EndAngle=6.28319
    g13: LineSegment StartX=65.8448 StartY=3.80476 StartZ=0 EndX=59.7448 EndY=3.80476 EndZ=0
    g14: ArcOfCircle CenterX=59.7448 CenterY=5.00476 CenterZ=0 NormalX=0 NormalY=0 NormalZ=1 AngleXU=0 Radius=1.2 StartAngle=3.14159 EndAngle=4.71239
    g15: LineSegment StartX=58.5448 StartY=5.00476 StartZ=0 EndX=58.5448 EndY=9.10476 EndZ=0
    g16: ArcOfCircle CenterX=59.7448 CenterY=9.10476 CenterZ=0 NormalX=0 NormalY=0 NormalZ=1 AngleXU=0 Radius=1.2 StartAngle=1.5708 EndAngle=3.14159
    g17: LineSegment StartX=59.7448 StartY=10.3048 StartZ=0 EndX=65.8448 EndY=10.3048 EndZ=0
    g18: GeomPoint [constr] X=67.0448 Y=10.3048 Z=0
    g19: GeomPoint [constr] X=58.5448 Y=3.80476 Z=0
    g20: LineSegment [constr] StartX=67.1499 StartY=3.80476 StartZ=0 EndX=2.92486 EndY=3.80476 EndZ=0
    g21: LineSegment [constr] StartX=67.0448 StartY=3.37798 StartZ=0 EndX=67.0448 EndY=94.7537 EndZ=0
    g22: LineSegment [constr] StartX=53.0499 StartY=3.37766 StartZ=0 EndX=53.0499 EndY=11.7621 EndZ=0
    g23: ArcOfCircle CenterX=51.8499 CenterY=5.00476 CenterZ=0 NormalX=0 NormalY=0 NormalZ=1 AngleXU=0 Radius=1.2 StartAngle=4.71239 EndAngle=6.28319
    g24: LineSegment StartX=51.8499 StartY=3.80476 StartZ=0 EndX=43.7465 EndY=3.80476 EndZ=0
    g25: ArcOfCircle CenterX=43.7465 CenterY=5.00476 CenterZ=0 NormalX=0 NormalY=0 NormalZ=1 AngleXU=0 Radius=1.2 StartAngle=3.14159 EndAngle=4.71239
    g26: LineSegment StartX=42.5465 StartY=5.00476 StartZ=0 EndX=42.5465 EndY=9 EndZ=0
    g27: ArcOfCircle CenterX=43.7465 CenterY=9 CenterZ=0 NormalX=0 NormalY=0 NormalZ=1 AngleXU=0 Radius=1.2 StartAngle=1.5708 EndAngle=3.14159
    g28: LineSegment StartX=43.7465 StartY=10.2 StartZ=0 EndX=51.8499 EndY=10.2 EndZ=0
    g29: ArcOfCircle CenterX=51.8499 CenterY=9 CenterZ=0 NormalX=0 NormalY=0 NormalZ=1 AngleXU=0 Radius=1.2 StartAngle=-9e-16 EndAngle=1.5708
    g30: LineSegment StartX=53.0499 StartY=9 StartZ=0 EndX=53.0499 EndY=5.00476 EndZ=0
    g31: GeomPoint [constr] X=53.0499 Y=3.80476 Z=0
    g32: GeomPoint [constr] X=42.5465 Y=10.2 Z=0
  constraints (71):
    c: Tangent(g0,g1) = 1.5708
    c: Tangent(g1,g2) = 1.5708
    c: Tangent(g2,g3) = 1.5708
    c: Tangent(g3,g4) = 1.5708
    c: Tangent(g4,g5) = 1.5708
    c: Tangent(g5,g6) = 1.5708
    c: Tangent(g6,g7) = 1.5708
    c: Tangent(g7,g0) = 1.5708
    c: Horizontal(g3)
    c: Horizontal(g7)
    c: Vertical(g1)
    c: Vertical(g5)
    c: Equal(g0,g2)
    c: Equal(g2,g4)
    c: Equal(g4,g6)
    c: PointOnObject(g8,g1)
    c: PointOnObject(g8,g7)
    c: PointOnObject(g9,g3)
    c: PointOnObject(g9,g5)
    c: Radius(g0) = 0.5
    c: Tangent(g10,g11) = 1.5708
    c: Tangent(g11,g12) = 1.5708
    c: Tangent(g12,g13) = 1.5708
    c: Tangent(g13,g14) = 1.5708
    c: Tangent(g14,g15) = 1.5708
    c: Tangent(g15,g16) = 1.5708
    c: Tangent(g16,g17) = 1.5708
    c: Tangent(g17,g10) = 1.5708
    c: Horizontal(g13)
    c: Horizontal(g17)
    c: Vertical(g11)
    c: Vertical(g15)
    c: Equal(g10,g12)
    c: Equal(g12,g14)
    c: Equal(g14,g16)
    c: PointOnObject(g18,g11)
    c: PointOnObject(g18,g17)
    c: PointOnObject(g19,g13)
    c: PointOnObject(g19,g15)
    c: Horizontal(g20)
    c: Tangent(g20,g12)
    c: DistanceY(g12,g10) = 6.5
    c: Vertical(g21)
    c: Tangent(g21,g10)
    c: DistanceX(g15,g10) = 8.5
    c: Radius(g16) = 1.2
    c: Vertical(g22)
    c: Tangent(g23,g24) = 1.5708
    c: Tangent(g24,g25) = 1.5708
    c: Tangent(g25,g26) = 1.5708
    c: Tangent(g26,g27) = 1.5708
    c: Tangent(g27,g28) = 1.5708
    c: Tangent(g28,g29) = 1.5708
    c: Tangent(g29,g30) = 1.5708
    c: Tangent(g30,g23) = 1.5708
    c: Horizontal(g24)
    c: Horizontal(g28)
    c: Vertical(g26)
    c: Equal(g23,g25)
    c: Equal(g25,g27)
    c: Equal(g27,g29)
    c: PointOnObject(g31,g24)
    c: PointOnObject(g31,g30)
    c: PointOnObject(g32,g26)
    c: PointOnObject(g32,g28)
    c: PointOnObject(g23,g20)
    c: Tangent(g30,g22)
    c: Radius(g27) = 1.2
    c: Block(g22)
    c: Block(g21)
    c: Block(g20)
FEATURE [Part::Extrusion] Extrude016
  Base = -> Sketch016
  Dir = (0,0,1)
  DirMode = 2
  FaceMakerClass = Part::FaceMakerBullseye
  FaceMakerMode = 3
  LengthFwd = 0.5
  LengthRev = 0
  Placement = pos=(0,0,2.8) rot=(0,0,1;0rad)
  Solid = true
  Symmetric = false
FEATURE [Part::Cylinder] Cylinder005
  Angle = 360
  AttacherType = Attacher::AttachEngine3D
  FirstAngle = 0
  Height = 1
  Placement = pos=(15.25,2,9.6) rot=(0,0,1;0rad)
  Radius = 2
  SecondAngle = 0
FEATURE [Part::Cylinder] Cylinder006
  Angle = 360
  AttacherType = Attacher::AttachEngine3D
  FirstAngle = 0
  Height = 4
  Placement = pos=(15.25,2,5.6) rot=(0,0,1;0rad)
  Radius = 1
  SecondAngle = 0
FEATURE [Part::Cylinder] Cylinder007
  Angle = 360
  AttacherType = Attacher::AttachEngine3D
  FirstAngle = 0
  Height = 3.2
  Placement = pos=(15.25,2,4.5) rot=(0,0,1;0rad)
  Radius = 1.6
  SecondAngle = 0
FEATURE [Part::Cylinder] Cylinder008
  Angle = 360
  AttacherType = Attacher::AttachEngine3D
  FirstAngle = 0
  Height = 3
  Placement = pos=(15.25,2,4.5) rot=(0,0,1;0rad)
  Radius = 2.1
  SecondAngle = 0
FEATURE [Part::Cut] Cut007  label="NUT"
  Base = -> Cylinder008
  Tool = -> Cylinder007
FEATURE [Part::MultiFuse] Fusion004  label="NUT2_"
  Shapes = -> [Cylinder006,Cylinder005]
FEATURE [PartDesign::FeatureBase] Clone100
  BaseFeature = -> Cut007
  Suppressed = false
FEATURE [PartDesign::Body] Body100
  AllowCompound = false
  Group = -> [Clone100]
  Origin = -> Origin146
  Placement = pos=(0,1,0.5) rot=(0,0,1;0rad)
  Tip = -> Clone100
FEATURE [PartDesign::FeatureBase] Clone101
  BaseFeature = -> Cut007
  Suppressed = false
FEATURE [PartDesign::Body] Body101
  AllowCompound = false
  Group = -> [Clone101]
  Origin = -> Origin147
  Placement = pos=(39.5,1,0.5) rot=(0,0,1;0rad)
  Tip = -> Clone101
FEATURE [PartDesign::FeatureBase] Clone102
  BaseFeature = -> Cut007
  Suppressed = false
FEATURE [PartDesign::Body] Body102
  AllowCompound = false
  Group = -> [Clone102]
  Origin = -> Origin148
  Placement = pos=(40.1,30,0.5) rot=(0,0,1;0rad)
  Tip = -> Clone102
FEATURE [PartDesign::FeatureBase] Clone103
  BaseFeature = -> Cut007
  Suppressed = false
FEATURE [PartDesign::Body] Body103
  AllowCompound = false
  Group = -> [Clone103]
  Origin = -> Origin149
  Placement = pos=(-12.2,41.5,0.5) rot=(0,0,1;0rad)
  Tip = -> Clone103
FEATURE [PartDesign::FeatureBase] Clone104
  BaseFeature = -> Cut007
  Suppressed = false
FEATURE [PartDesign::Body] Body104
  AllowCompound = false
  Group = -> [Clone104]
  Origin = -> Origin150
  Placement = pos=(51.8,41.5,0.5) rot=(0,0,1;0rad)
  Tip = -> Clone104
FEATURE [PartDesign::FeatureBase] Clone105
  BaseFeature = -> Cut007
  Suppressed = false
FEATURE [PartDesign::Body] Body105
  AllowCompound = false
  Group = -> [Clone105]
  Origin = -> Origin151
  Placement = pos=(-12.2,94.5,0.5) rot=(0,0,1;0rad)
  Tip = -> Clone105
FEATURE [PartDesign::FeatureBase] Clone106
  BaseFeature = -> Cut007
  Suppressed = false
FEATURE [PartDesign::Body] Body106
  AllowCompound = false
  Group = -> [Clone106]
  Origin = -> Origin152
  Placement = pos=(9.15,73,0.5) rot=(0,0,1;0rad)
  Tip = -> Clone106
FEATURE [PartDesign::FeatureBase] Clone107
  BaseFeature = -> Cut007
  Suppressed = false
FEATURE [PartDesign::Body] Body107
  AllowCompound = false
  Group = -> [Clone107]
  Origin = -> Origin153
  Placement = pos=(51.8,94.5,0.5) rot=(0,0,1;0rad)
  Tip = -> Clone107
FEATURE [Part::Cylinder] Cylinder009
  Angle = 360
  AttacherType = Attacher::AttachEngine3D
  FirstAngle = 0
  Height = 2.5
  Placement = pos=(7.25,151,5.5) rot=(0,0,1;0rad)
  Radius = 2.1
  SecondAngle = 0
FEATURE [Part::Cylinder] Cylinder010
  Angle = 360
  AttacherType = Attacher::AttachEngine3D
  FirstAngle = 0
  Height = 2.5
  Placement = pos=(7.25,151,5.5) rot=(0,0,1;0rad)
  Radius = 1.7
  SecondAngle = 0
FEATURE [Part::Cut] Cut008
  Base = -> Cylinder009
  Placement = pos=(-3.25,-2,0) rot=(0,0,1;0rad)
  Tool = -> Cylinder010
FEATURE [Part::Box] Box004  label="Cube003"
  AttacherType = Attacher::AttachEngine3D
  Height = 0.5
  Length = 68
  Placement = pos=(1,0.5,4.5) rot=(-1,0,0;0.033161rad)
  Width = 98
FEATURE [Part::Cut] Cut009
  Base = -> Box004
  Tool = -> Compound001
FEATURE [Part::Box] Box005  label="Cube004"
  AttacherType = Attacher::AttachEngine3D
  Height = 10
  Length = 66
  Placement = pos=(2,-2,-6) rot=(0,0,1;0rad)
  Width = 5
FEATURE [Part::Box] Box006  label="Cube005"
  AttacherType = Attacher::AttachEngine3D
  Height = 10
  Length = 72
  Placement = pos=(-1,1,-6) rot=(1,0,0;0.785398rad)
  Width = 7
FEATURE [Part::Box] Box007  label="Cube006"
  AttacherType = Attacher::AttachEngine3D
  Height = 9
  Length = 2
  Width = 0.5
FEATURE [Part::Box] Box008  label="Cube007"
  AttacherType = Attacher::AttachEngine3D
  Height = 9
  Length = 2
  Placement = pos=(0,1,0) rot=(0,0,1;0rad)
  Width = 0.5
FEATURE [Part::Box] Box009  label="Cube008"
  AttacherType = Attacher::AttachEngine3D
  Height = 9
  Length = 2
  Placement = pos=(0,2,0) rot=(0,0,1;0rad)
  Width = 0.5
FEATURE [Part::Box] Box010  label="Cube009"
  AttacherType = Attacher::AttachEngine3D
  Height = 9
  Length = 2
  Placement = pos=(0,3,0) rot=(0,0,1;0rad)
  Width = 0.5
FEATURE [Part::Box] Box011  label="Cube010"
  AttacherType = Attacher::AttachEngine3D
  Height = 9
  Length = 2
  Placement = pos=(0,4,0) rot=(0,0,1;0rad)
  Width = 0.5
FEATURE [Part::Box] Box012  label="Cube011"
  AttacherType = Attacher::AttachEngine3D
  Height = 9
  Length = 2
  Placement = pos=(0,5,0) rot=(0,0,1;0rad)
  Width = 0.5
FEATURE [Part::Box] Box013  label="Cube012"
  AttacherType = Attacher::AttachEngine3D
  Height = 9
  Length = 2
  Placement = pos=(0,6,0) rot=(0,0,1;0rad)
  Width = 0.5
FEATURE [Part::Box] Box014  label="Cube013"
  AttacherType = Attacher::AttachEngine3D
  Height = 9
  Length = 2
  Placement = pos=(0,7,0) rot=(0,0,1;0rad)
  Width = 0.5
FEATURE [Part::Box] Box015  label="Cube014"
  AttacherType = Attacher::AttachEngine3D
  Height = 9
  Length = 2
  Placement = pos=(0,8,0) rot=(0,0,1;0rad)
  Width = 0.5
FEATURE [Part::Box] Box016  label="Cube015"
  AttacherType = Attacher::AttachEngine3D
  Height = 9
  Length = 2
  Placement = pos=(0,9,0) rot=(0,0,1;0rad)
  Width = 0.5
FEATURE [Part::Compound] Compound  label="grip"
  Links = -> [Box007,Box008,Box009,Box010,Box011,Box012,Box013,Box014,Box015,Box016]
FEATURE [PartDesign::FeatureBase] Clone111
  BaseFeature = -> Compound
  Suppressed = false
FEATURE [PartDesign::Body] Body111
  AllowCompound = false
  Group = -> [Clone111]
  Origin = -> Origin225
  Placement = pos=(-1.8,30,0) rot=(0,0,1;0rad)
  Tip = -> Clone111
FEATURE [PartDesign::FeatureBase] Clone112
  BaseFeature = -> Compound
  Suppressed = false
FEATURE [PartDesign::Body] Body112
  AllowCompound = false
  Group = -> [Clone112]
  Origin = -> Origin226
  Placement = pos=(-1.8,50,0) rot=(0,0,1;0rad)
  Tip = -> Clone112
FEATURE [PartDesign::FeatureBase] Clone113
  BaseFeature = -> Compound
  Suppressed = false
FEATURE [PartDesign::Body] Body113
  AllowCompound = false
  Group = -> [Clone113]
  Origin = -> Origin227
  Placement = pos=(-1.8,70,0) rot=(0,0,1;0rad)
  Tip = -> Clone113
FEATURE [PartDesign::FeatureBase] Clone114
  BaseFeature = -> Compound
  Suppressed = false
FEATURE [PartDesign::Body] Body114
  AllowCompound = false
  Group = -> [Clone114]
  Origin = -> Origin228
  Placement = pos=(-1.8,90,0) rot=(0,0,1;0rad)
  Tip = -> Clone114
FEATURE [PartDesign::FeatureBase] Clone117
  BaseFeature = -> Compound
  Suppressed = false
FEATURE [PartDesign::Body] Body117
  AllowCompound = false
  Group = -> [Clone117]
  Origin = -> Origin231
  Placement = pos=(69.8,30,0) rot=(0,0,1;0rad)
  Tip = -> Clone117
FEATURE [PartDesign::FeatureBase] Clone118
  BaseFeature = -> Compound
  Suppressed = false
FEATURE [PartDesign::Body] Body118
  AllowCompound = false
  Group = -> [Clone118]
  Origin = -> Origin232
  Placement = pos=(69.8,50,0) rot=(0,0,1;0rad)
  Tip = -> Clone118
FEATURE [PartDesign::FeatureBase] Clone119
  BaseFeature = -> Compound
  Suppressed = false
FEATURE [PartDesign::Body] Body119
  AllowCompound = false
  Group = -> [Clone119]
  Origin = -> Origin233
  Placement = pos=(69.8,70,0) rot=(0,0,1;0rad)
  Tip = -> Clone119
FEATURE [PartDesign::FeatureBase] Clone120
  BaseFeature = -> Compound
  Suppressed = false
FEATURE [PartDesign::Body] Body120
  AllowCompound = false
  Group = -> [Clone120]
  Origin = -> Origin234
  Placement = pos=(69.8,90,0) rot=(0,0,1;0rad)
  Tip = -> Clone120
FEATURE [Part::Compound] Compound004  label="GRIP01"
  Links = -> [Body111,Body112,Body113,Body114,Body117,Body118,Body119,Body120]
FEATURE [Part::Box] Box017  label="Cube016"
  AttacherType = Attacher::AttachEngine3D
  Height = 10
  Length = 10
  Placement = pos=(-10,-4,-3.5) rot=(0,1,0;0.785398rad)
  Width = 160
FEATURE [Part::Box] Box018  label="Cube017"
  AttacherType = Attacher::AttachEngine3D
  Height = 10
  Length = 10
  Placement = pos=(66,-4,-3.5) rot=(0,1,0;0.785398rad)
  Width = 160
FEATURE [Part::Box] Box019  label="Cube018"
  AttacherType = Attacher::AttachEngine3D
  Height = 10
  Length = 74
  Placement = pos=(-2,154,-10.5) rot=(1,0,0;0.785398rad)
  Width = 10
FEATURE [Part::Box] Box020  label="Cube019"
  AttacherType = Attacher::AttachEngine3D
  Height = 7
  Length = 68
  Placement = pos=(1,93,2) rot=(0,0,1;0rad)
  Width = 8
FEATURE [Part::Box] Box021  label="Cube020"
  AttacherType = Attacher::AttachEngine3D
  Height = 1.2
  Length = 0.5
  Placement = pos=(57,100,-1) rot=(0,0,1;0rad)
  Width = 5
FEATURE [Part::Box] Box022  label="Cube021"
  AttacherType = Attacher::AttachEngine3D
  Height = 1.2
  Length = 0.5
  Placement = pos=(46,100,-1) rot=(0,0,1;0rad)
  Width = 5
FEATURE [Part::Box] Box023  label="Cube022"
  AttacherType = Attacher::AttachEngine3D
  Height = 1.2
  Length = 0.5
  Placement = pos=(13,100,-1) rot=(0,0,1;0rad)
  Width = 5
FEATURE [Part::Box] Box024  label="Cube023"
  AttacherType = Attacher::AttachEngine3D
  Height = 1.2
  Length = 0.5
  Placement = pos=(35,100,-1) rot=(0,0,1;0rad)
  Width = 5
FEATURE [Part::Box] Box025  label="Cube024"
  AttacherType = Attacher::AttachEngine3D
  Height = 1.2
  Length = 0.5
  Placement = pos=(24,100,-1) rot=(0,0,1;0rad)
  Width = 5
FEATURE [Part::Compound] Compound005  label="LCDMARKS"
  Links = -> [Box021,Box022,Box023,Box024,Box025]
FEATURE [Part::Box] Box026  label="Cube025"
  AttacherType = Attacher::AttachEngine3D
  Height = 5
  Length = 10
  Placement = pos=(-3,105.7,4.4) rot=(0,0,1;0rad)
  Width = 9.4
FEATURE [Part::Fillet] Fillet006
  Base = -> Box026
  EdgeLinks = -> Box026 [Edge9,Edge11]
  Edges = 2 edges r=1.5: [Edge9,Edge11]
FEATURE [Part::Box] Box027  label="Cube026"
  AttacherType = Attacher::AttachEngine3D
  Height = 2.3
  Length = 8
  Placement = pos=(-4,-3,0) rot=(0,0,1;0rad)
  Width = 6
FEATURE [Part::Box] Box028  label="Cube027"
  AttacherType = Attacher::AttachEngine3D
  Height = 3
  Length = 8
  Placement = pos=(-4,-6,-0.6) rot=(-1,0,0;0.488692rad)
  Width = 6
FEATURE [Part::Cut] Cut010
  Base = -> Box027
  Tool = -> Box028
FEATURE [Part::Fillet] Fillet007
  Base = -> Cut010
  EdgeLinks = -> Cut010 [Edge1,Edge3,Edge4,Edge5,Edge6,Edge8,Edge11,Edge12,Edge13,Edge14,Edge15]
  Edges = 11 edges: [Edge1 r=0.3,Edge3 r=0.3,Edge4 r=0.3,Edge5 r=0.3,Edge6 r=0.3,Edge8 r=0.3,Edge11 r=0.3,Edge12 r=0.3,Edge13 r=0.3,Edge14 r=1,Edge15 r=0.3]
FEATURE [Part::Cylinder] Cylinder011
  Angle = 360
  AttacherType = Attacher::AttachEngine3D
  FirstAngle = 0
  Height = 0.4
  Placement = pos=(0,3,1.9) rot=(0,0,1;0rad)
  Radius = 1.5
  SecondAngle = 0
FEATURE [Part::MultiFuse] Fusion006  label="KEY A"
  Refine = true
  Shapes = -> [Cylinder011,Fillet007]
FEATURE [PartDesign::FeatureBase] Clone122
  BaseFeature = -> Fusion006
  Suppressed = false
FEATURE [PartDesign::Body] Body122  label="KA1-1"
  AllowCompound = false
  Group = -> [Clone122]
  Origin = -> Origin236
  Placement = pos=(62.5,7,2.58) rot=(0,0,1;0rad)
  Tip = -> Clone122
FEATURE [Part::Box] Box029  label="Cube028"
  AttacherType = Attacher::AttachEngine3D
  Height = 10
  Length = 9
  Placement = pos=(-4.5,-3.5,0) rot=(0,0,1;0rad)
  Width = 7
FEATURE [Part::Box] Box030  label="Cube029"
  AttacherType = Attacher::AttachEngine3D
  Height = 10
  Length = 2
  Placement = pos=(1,-4.9,0) rot=(0,0,1;0rad)
  Width = 3
FEATURE [Part::Box] Box031  label="Cube030"
  AttacherType = Attacher::AttachEngine3D
  Height = 10
  Length = 2
  Placement = pos=(-3,-4.9,0) rot=(0,0,1;0rad)
  Width = 3
FEATURE [Part::Box] Box032  label="Cube031"
  AttacherType = Attacher::AttachEngine3D
  Height = 10
  Length = 1
  Placement = pos=(1.5,-6,0) rot=(0,0,1;0rad)
  Width = 4
FEATURE [Part::Box] Box033  label="Cube032"
  AttacherType = Attacher::AttachEngine3D
  Height = 10
  Length = 1
  Placement = pos=(-2.5,-6,0) rot=(0,0,1;0rad)
  Width = 4
FEATURE [Part::MultiFuse] Fusion008
  Shapes = -> [Box032,Box033]
FEATURE [Part::Cylinder] Cylinder012
  Angle = 360
  AttacherType = Attacher::AttachEngine3D
  FirstAngle = 0
  Height = 10
  Placement = pos=(0,3,0) rot=(0,0,1;0rad)
  Radius = 1.8
  SecondAngle = 0
FEATURE [Part::MultiFuse] Fusion007
  Refine = true
  Shapes = -> [Box029,Box030,Box031,Cylinder012]
FEATURE [Part::Cut] Cut011  label="Cut A"
  Base = -> Fusion007
  Tool = -> Fusion008
FEATURE [Part::Fillet] Fillet008  label="CUT A"
  Base = -> Cut011
  EdgeLinks = -> Cut011 [Edge49,Edge50,Edge63,Edge64]
  Edges = 4 edges r=0.5: [Edge49,Edge50,Edge63,Edge64]
FEATURE [Part::Box] Box034  label="Cube033"
  AttacherType = Attacher::AttachEngine3D
  Height = 1.2
  Length = 68
  Placement = pos=(1,0.5,4.6) rot=(-1,0,0;0.033161rad)
  Width = 98
FEATURE [PartDesign::FeatureBase] Clone123
  BaseFeature = -> Fillet008
  Suppressed = false
FEATURE [PartDesign::Body] Body123  label="CA1-1"
  AllowCompound = false
  Group = -> [Clone123]
  Origin = -> Origin237
  Placement = pos=(62.5,7,0) rot=(0,0,1;0rad)
  Tip = -> Clone123
FEATURE [PartDesign::FeatureBase] Clone124
  BaseFeature = -> Fusion006
  Suppressed = false
FEATURE [PartDesign::Body] Body124  label="KA2-1"
  AllowCompound = false
  Group = -> [Clone124]
  Origin = -> Origin238
  Placement = pos=(62.5,17,2.25) rot=(0,0,1;0rad)
  Tip = -> Clone124
FEATURE [Part::Cylinder] Cylinder013
  Angle = 360
  AttacherType = Attacher::AttachEngine3D
  FirstAngle = 0
  Height = 2
  Placement = pos=(54.75,0.4,6.5) rot=(1,0,0;1.5708rad)
  Radius = 1
  SecondAngle = 0
FEATURE [Part::Cylinder] Cylinder014
  Angle = 360
  AttacherType = Attacher::AttachEngine3D
  FirstAngle = 0
  Height = 2
  Placement = pos=(15.4,0.4,6.5) rot=(1,0,0;1.5708rad)
  Radius = 1
  SecondAngle = 0
FEATURE [Part::Box] Box035  label="Cube034"
  AttacherType = Attacher::AttachEngine3D
  Height = 0.5
  Length = 1
  Placement = pos=(69.8,12,5) rot=(0,0,1;0rad)
  Width = 10
FEATURE [Part::Box] Box041  label="Cube040"
  AttacherType = Attacher::AttachEngine3D
  Height = 0.5
  Length = 1
  Placement = pos=(-0.8,12,5) rot=(0,0,1;0rad)
  Width = 10
FEATURE [Part::Compound] Compound006
  Links = -> [Box035,Box041]
FEATURE [Part::Box] Box043  label="Cube042"
  AttacherType = Attacher::AttachEngine3D
  Height = 0.5
  Length = 10
  Placement = pos=(30,-0.8,6) rot=(0,0,1;0rad)
  Width = 1
FEATURE [Part::Feature] path1334
  Placement = pos=(0,0,0) rot=(0.57735,0.57735,0.57735;2.0944rad)
  shape: bbox 2e-07 x 119.2 x 52.97 mm, 0 faces, 0 solids (baked)
FEATURE [Part::FeaturePython] Clone125  label="path1335"  # Draft clone (typed FeaturePython)
  AttacherType = Attacher::AttachEngine3D
  Fuse = false
  Objects = -> [path1334]
  Placement = pos=(-3.98221,108.2,3.59072) rot=(0.57735,0.57735,0.57735;2.0944rad)
  Scale = (0.03,0.03,0.03)
FEATURE [Part::Extrusion] Extrude017  label="USBC"
  Base = -> Clone125
  Dir = (1,0,0)
  DirMode = 2
  FaceMakerClass = Part::FaceMakerBullseye
  FaceMakerMode = 3
  LengthFwd = 2
  LengthRev = 0
  Placement = pos=(2.1,0,0) rot=(0,0,1;0rad)
  Solid = true
  Symmetric = false
FEATURE [PartDesign::FeatureBase] Clone126
  BaseFeature = -> Fillet008
  Suppressed = false
FEATURE [PartDesign::Body] Body125  label="CA2-1"
  AllowCompound = false
  Group = -> [Clone126]
  Origin = -> Origin239
  Placement = pos=(62.5,17,0) rot=(0,0,1;0rad)
  Tip = -> Clone126
FEATURE [Part::Box] Box046  label="Cube045"
  AttacherType = Attacher::AttachEngine3D
  Height = 0.5
  Length = 10
  Placement = pos=(30,150.8,4) rot=(0,0,1;0rad)
  Width = 1
FEATURE [PartDesign::FeatureBase] Clone127
  BaseFeature = -> Fillet008
  Suppressed = false
FEATURE [PartDesign::Body] Body126  label="CA3-1"
  AllowCompound = false
  Group = -> [Clone127]
  Origin = -> Origin240
  Placement = pos=(62.5,27,0) rot=(0,0,1;0rad)
  Tip = -> Clone127
FEATURE [PartDesign::FeatureBase] Clone128
  BaseFeature = -> Fillet008
  Suppressed = false
FEATURE [PartDesign::Body] Body127  label="CA4-1"
  AllowCompound = false
  Group = -> [Clone128]
  Origin = -> Origin241
  Placement = pos=(62.5,37,0) rot=(0,0,1;0rad)
  Tip = -> Clone128
FEATURE [PartDesign::FeatureBase] Clone129
  BaseFeature = -> Fusion006
  Suppressed = false
FEATURE [PartDesign::Body] Body128  label="KA3-1"
  AllowCompound = false
  Group = -> [Clone129]
  Origin = -> Origin242
  Placement = pos=(62.5,27,1.92) rot=(0,0,1;0rad)
  Tip = -> Clone129
FEATURE [PartDesign::FeatureBase] Clone130
  BaseFeature = -> Fusion006
  Suppressed = false
FEATURE [PartDesign::Body] Body129  label="KA4-1"
  AllowCompound = false
  Group = -> [Clone130]
  Origin = -> Origin243
  Placement = pos=(62.5,37,1.59) rot=(0,0,1;0rad)
  Tip = -> Clone130
FEATURE [PartDesign::FeatureBase] Clone131
  BaseFeature = -> Fusion006
  Suppressed = false
FEATURE [PartDesign::Body] Body130  label="KA5-1"
  AllowCompound = false
  Group = -> [Clone131]
  Origin = -> Origin244
  Placement = pos=(62.5,50,1.16) rot=(0,0,1;0rad)
  Tip = -> Clone131
FEATURE [PartDesign::FeatureBase] Clone132
  BaseFeature = -> Fusion006
  Suppressed = false
FEATURE [PartDesign::Body] Body131  label="KA6-1"
  AllowCompound = false
  Group = -> [Clone132]
  Origin = -> Origin245
  Placement = pos=(62.5,60,0.83) rot=(0,0,1;0rad)
  Tip = -> Clone132
FEATURE [PartDesign::FeatureBase] Clone133
  BaseFeature = -> Fusion006
  Suppressed = false
FEATURE [PartDesign::Body] Body132  label="KA7-1"
  AllowCompound = false
  Group = -> [Clone133]
  Origin = -> Origin246
  Placement = pos=(62.5,70,0.49) rot=(0,0,1;0rad)
  Tip = -> Clone133
FEATURE [PartDesign::FeatureBase] Clone134
  BaseFeature = -> Fusion006
  Suppressed = false
FEATURE [PartDesign::Body] Body133  label="KA8-1"
  AllowCompound = false
  Group = -> [Clone134]
  Origin = -> Origin247
  Placement = pos=(62.5,80,0.16) rot=(0,0,1;0rad)
  Tip = -> Clone134
FEATURE [PartDesign::FeatureBase] Clone135
  BaseFeature = -> Fusion006
  Suppressed = false
FEATURE [PartDesign::Body] Body134  label="KA9-1"
  AllowCompound = false
  Group = -> [Clone135]
  Origin = -> Origin248
  Placement = pos=(62.5,90,-0.17) rot=(0,0,1;0rad)
  Tip = -> Clone135
FEATURE [PartDesign::FeatureBase] Clone136
  BaseFeature = -> Fillet008
  Suppressed = false
FEATURE [PartDesign::Body] Body135  label="CA5-1"
  AllowCompound = false
  Group = -> [Clone136]
  Origin = -> Origin249
  Placement = pos=(62.5,50,0) rot=(0,0,1;0rad)
  Tip = -> Clone136
FEATURE [PartDesign::FeatureBase] Clone137
  BaseFeature = -> Fillet008
  Suppressed = false
FEATURE [PartDesign::Body] Body136  label="CA6-1"
  AllowCompound = false
  Group = -> [Clone137]
  Origin = -> Origin250
  Placement = pos=(62.5,60,0) rot=(0,0,1;0rad)
  Tip = -> Clone137
FEATURE [PartDesign::FeatureBase] Clone138
  BaseFeature = -> Fillet008
  Suppressed = false
FEATURE [PartDesign::Body] Body137  label="CA7-1"
  AllowCompound = false
  Group = -> [Clone138]
  Origin = -> Origin251
  Placement = pos=(62.5,70,0) rot=(0,0,1;0rad)
  Tip = -> Clone138
FEATURE [PartDesign::FeatureBase] Clone139
  BaseFeature = -> Fillet008
  Suppressed = false
FEATURE [PartDesign::Body] Body138  label="CA8-1"
  AllowCompound = false
  Group = -> [Clone139]
  Origin = -> Origin252
  Placement = pos=(62.5,80,0) rot=(0,0,1;0rad)
  Tip = -> Clone139
FEATURE [PartDesign::FeatureBase] Clone140
  BaseFeature = -> Fillet008
  Suppressed = false
FEATURE [PartDesign::Body] Body139  label="CA9-1"
  AllowCompound = false
  Group = -> [Clone140]
  Origin = -> Origin253
  Placement = pos=(62.5,90,0) rot=(0,0,1;0rad)
  Tip = -> Clone140
FEATURE [PartDesign::FeatureBase] Clone141
  BaseFeature = -> Fusion006
  Suppressed = false
FEATURE [PartDesign::Body] Body140  label="KA5-2"
  AllowCompound = false
  Group = -> [Clone141]
  Origin = -> Origin254
  Placement = pos=(51.5,50,1.16) rot=(0,0,1;0rad)
  Tip = -> Clone141
FEATURE [PartDesign::FeatureBase] Clone142
  BaseFeature = -> Fusion006
  Suppressed = false
FEATURE [PartDesign::Body] Body141  label="KA6-2"
  AllowCompound = false
  Group = -> [Clone142]
  Origin = -> Origin255
  Placement = pos=(51.5,60,0.83) rot=(0,0,1;0rad)
  Tip = -> Clone142
FEATURE [PartDesign::FeatureBase] Clone143
  BaseFeature = -> Fusion006
  Suppressed = false
FEATURE [PartDesign::Body] Body142  label="KA7-2"
  AllowCompound = false
  Group = -> [Clone143]
  Origin = -> Origin256
  Placement = pos=(51.5,70,0.49) rot=(0,0,1;0rad)
  Tip = -> Clone143
FEATURE [PartDesign::FeatureBase] Clone144
  BaseFeature = -> Fusion006
  Suppressed = false
FEATURE [PartDesign::Body] Body143  label="KA8-2"
  AllowCompound = false
  Group = -> [Clone144]
  Origin = -> Origin257
  Placement = pos=(51.5,80,0.16) rot=(0,0,1;0rad)
  Tip = -> Clone144
FEATURE [PartDesign::FeatureBase] Clone145
  BaseFeature = -> Fusion006
  Suppressed = false
FEATURE [PartDesign::Body] Body144  label="KA9-2"
  AllowCompound = false
  Group = -> [Clone145]
  Origin = -> Origin258
  Placement = pos=(51.5,90,-0.17) rot=(0,0,1;0rad)
  Tip = -> Clone145
FEATURE [PartDesign::FeatureBase] Clone146
  BaseFeature = -> Fillet008
  Suppressed = false
FEATURE [PartDesign::Body] Body145  label="CA5-2"
  AllowCompound = false
  Group = -> [Clone146]
  Origin = -> Origin259
  Placement = pos=(51.5,50,0) rot=(0,0,1;0rad)
  Tip = -> Clone146
FEATURE [PartDesign::FeatureBase] Clone147
  BaseFeature = -> Fillet008
  Suppressed = false
FEATURE [PartDesign::Body] Body146  label="CA6-2"
  AllowCompound = false
  Group = -> [Clone147]
  Origin = -> Origin260
  Placement = pos=(51.5,60,0) rot=(0,0,1;0rad)
  Tip = -> Clone147
FEATURE [PartDesign::FeatureBase] Clone148
  BaseFeature = -> Fillet008
  Suppressed = false
FEATURE [PartDesign::Body] Body147  label="CA7-2"
  AllowCompound = false
  Group = -> [Clone148]
  Origin = -> Origin261
  Placement = pos=(51.5,70,0) rot=(0,0,1;0rad)
  Tip = -> Clone148
FEATURE [PartDesign::FeatureBase] Clone149
  BaseFeature = -> Fillet008
  Suppressed = false
FEATURE [PartDesign::Body] Body148  label="CA8-2"
  AllowCompound = false
  Group = -> [Clone149]
  Origin = -> Origin262
  Placement = pos=(51.5,80,0) rot=(0,0,1;0rad)
  Tip = -> Clone149
FEATURE [PartDesign::FeatureBase] Clone150
  BaseFeature = -> Fillet008
  Suppressed = false
FEATURE [PartDesign::Body] Body149  label="CA9-2"
  AllowCompound = false
  Group = -> [Clone150]
  Origin = -> Origin263
  Placement = pos=(51.5,90,0) rot=(0,0,1;0rad)
  Tip = -> Clone150
FEATURE [PartDesign::FeatureBase] Clone151
  BaseFeature = -> Fusion006
  Suppressed = false
FEATURE [PartDesign::Body] Body150  label="KA5-3"
  AllowCompound = false
  Group = -> [Clone151]
  Origin = -> Origin264
  Placement = pos=(40.5,50,1.16) rot=(0,0,1;0rad)
  Tip = -> Clone151
FEATURE [PartDesign::FeatureBase] Clone152
  BaseFeature = -> Fusion006
  Suppressed = false
FEATURE [PartDesign::Body] Body151  label="KA6-3"
  AllowCompound = false
  Group = -> [Clone152]
  Origin = -> Origin265
  Placement = pos=(40.5,60,0.83) rot=(0,0,1;0rad)
  Tip = -> Clone152
FEATURE [PartDesign::FeatureBase] Clone153
  BaseFeature = -> Fusion006
  Suppressed = false
FEATURE [PartDesign::Body] Body152  label="KA7-3"
  AllowCompound = false
  Group = -> [Clone153]
  Origin = -> Origin266
  Placement = pos=(40.5,70,0.49) rot=(0,0,1;0rad)
  Tip = -> Clone153
FEATURE [PartDesign::FeatureBase] Clone154
  BaseFeature = -> Fusion006
  Suppressed = false
FEATURE [PartDesign::Body] Body153  label="KA8-3"
  AllowCompound = false
  Group = -> [Clone154]
  Origin = -> Origin267
  Placement = pos=(40.5,80,0.16) rot=(0,0,1;0rad)
  Tip = -> Clone154
FEATURE [PartDesign::FeatureBase] Clone155
  BaseFeature = -> Fusion006
  Suppressed = false
FEATURE [PartDesign::Body] Body154  label="KA9-3"
  AllowCompound = false
  Group = -> [Clone155]
  Origin = -> Origin268
  Placement = pos=(40.5,90,-0.17) rot=(0,0,1;0rad)
  Tip = -> Clone155
FEATURE [PartDesign::FeatureBase] Clone156
  BaseFeature = -> Fillet008
  Suppressed = false
FEATURE [PartDesign::Body] Body155  label="CA5-3"
  AllowCompound = false
  Group = -> [Clone156]
  Origin = -> Origin269
  Placement = pos=(40.5,50,0) rot=(0,0,1;0rad)
  Tip = -> Clone156
FEATURE [PartDesign::FeatureBase] Clone157
  BaseFeature = -> Fillet008
  Suppressed = false
FEATURE [PartDesign::Body] Body156  label="CA6-3"
  AllowCompound = false
  Group = -> [Clone157]
  Origin = -> Origin270
  Placement = pos=(40.5,60,0) rot=(0,0,1;0rad)
  Tip = -> Clone157
FEATURE [PartDesign::FeatureBase] Clone158
  BaseFeature = -> Fillet008
  Suppressed = false
FEATURE [PartDesign::Body] Body157  label="CA7-3"
  AllowCompound = false
  Group = -> [Clone158]
  Origin = -> Origin271
  Placement = pos=(40.5,70,0) rot=(0,0,1;0rad)
  Tip = -> Clone158
FEATURE [PartDesign::FeatureBase] Clone159
  BaseFeature = -> Fillet008
  Suppressed = false
FEATURE [PartDesign::Body] Body158  label="CA8-3"
  AllowCompound = false
  Group = -> [Clone159]
  Origin = -> Origin272
  Placement = pos=(40.5,80,0) rot=(0,0,1;0rad)
  Tip = -> Clone159
FEATURE [PartDesign::FeatureBase] Clone160
  BaseFeature = -> Fillet008
  Suppressed = false
FEATURE [PartDesign::Body] Body159  label="CA9-3"
  AllowCompound = false
  Group = -> [Clone160]
  Origin = -> Origin273
  Placement = pos=(40.5,90,0) rot=(0,0,1;0rad)
  Tip = -> Clone160
FEATURE [PartDesign::FeatureBase] Clone161
  BaseFeature = -> Fusion006
  Suppressed = false
FEATURE [PartDesign::Body] Body160  label="KA5-4"
  AllowCompound = false
  Group = -> [Clone161]
  Origin = -> Origin274
  Placement = pos=(29.5,50,1.16) rot=(0,0,1;0rad)
  Tip = -> Clone161
FEATURE [PartDesign::FeatureBase] Clone162
  BaseFeature = -> Fusion006
  Suppressed = false
FEATURE [PartDesign::Body] Body161  label="KA6-4"
  AllowCompound = false
  Group = -> [Clone162]
  Origin = -> Origin275
  Placement = pos=(29.5,60,0.83) rot=(0,0,1;0rad)
  Tip = -> Clone162
FEATURE [PartDesign::FeatureBase] Clone163
  BaseFeature = -> Fusion006
  Suppressed = false
FEATURE [PartDesign::Body] Body162  label="KA7-4"
  AllowCompound = false
  Group = -> [Clone163]
  Origin = -> Origin276
  Placement = pos=(29.5,70,0.49) rot=(0,0,1;0rad)
  Tip = -> Clone163
FEATURE [PartDesign::FeatureBase] Clone164
  BaseFeature = -> Fusion006
  Suppressed = false
FEATURE [PartDesign::Body] Body163  label="KA8-4"
  AllowCompound = false
  Group = -> [Clone164]
  Origin = -> Origin277
  Placement = pos=(29.5,80,0.16) rot=(0,0,1;0rad)
  Tip = -> Clone164
FEATURE [PartDesign::FeatureBase] Clone165
  BaseFeature = -> Fusion006
  Suppressed = false
FEATURE [PartDesign::Body] Body164  label="KA9-4"
  AllowCompound = false
  Group = -> [Clone165]
  Origin = -> Origin278
  Placement = pos=(29.5,90,-0.17) rot=(0,0,1;0rad)
  Tip = -> Clone165
FEATURE [PartDesign::FeatureBase] Clone166
  BaseFeature = -> Fillet008
  Suppressed = false
FEATURE [PartDesign::Body] Body165  label="CA5-4"
  AllowCompound = false
  Group = -> [Clone166]
  Origin = -> Origin279
  Placement = pos=(29.5,50,0) rot=(0,0,1;0rad)
  Tip = -> Clone166
FEATURE [PartDesign::FeatureBase] Clone167
  BaseFeature = -> Fillet008
  Suppressed = false
FEATURE [PartDesign::Body] Body166  label="CA6-4"
  AllowCompound = false
  Group = -> [Clone167]
  Origin = -> Origin280
  Placement = pos=(29.5,60,0) rot=(0,0,1;0rad)
  Tip = -> Clone167
FEATURE [PartDesign::FeatureBase] Clone168
  BaseFeature = -> Fillet008
  Suppressed = false
FEATURE [PartDesign::Body] Body167  label="CA7-4"
  AllowCompound = false
  Group = -> [Clone168]
  Origin = -> Origin281
  Placement = pos=(29.5,70,0) rot=(0,0,1;0rad)
  Tip = -> Clone168
FEATURE [PartDesign::FeatureBase] Clone169
  BaseFeature = -> Fillet008
  Suppressed = false
FEATURE [PartDesign::Body] Body168  label="CA8-4"
  AllowCompound = false
  Group = -> [Clone169]
  Origin = -> Origin282
  Placement = pos=(29.5,80,0) rot=(0,0,1;0rad)
  Tip = -> Clone169
FEATURE [PartDesign::FeatureBase] Clone170
  BaseFeature = -> Fillet008
  Suppressed = false
FEATURE [PartDesign::Body] Body169  label="CA9-4"
  AllowCompound = false
  Group = -> [Clone170]
  Origin = -> Origin283
  Placement = pos=(29.5,90,0) rot=(0,0,1;0rad)
  Tip = -> Clone170
FEATURE [PartDesign::FeatureBase] Clone171
  BaseFeature = -> Fusion006
  Suppressed = false
FEATURE [PartDesign::Body] Body170  label="KA5-5"
  AllowCompound = false
  Group = -> [Clone171]
  Origin = -> Origin284
  Placement = pos=(18.5,50,1.16) rot=(0,0,1;0rad)
  Tip = -> Clone171
FEATURE [PartDesign::FeatureBase] Clone172
  BaseFeature = -> Fusion006
  Suppressed = false
FEATURE [PartDesign::Body] Body171  label="KA6-5"
  AllowCompound = false
  Group = -> [Clone172]
  Origin = -> Origin285
  Placement = pos=(18.5,60,0.83) rot=(0,0,1;0rad)
  Tip = -> Clone172
FEATURE [PartDesign::FeatureBase] Clone173
  BaseFeature = -> Fusion006
  Suppressed = false
FEATURE [PartDesign::Body] Body172  label="KA7-5"
  AllowCompound = false
  Group = -> [Clone173]
  Origin = -> Origin286
  Placement = pos=(18.5,70,0.49) rot=(0,0,1;0rad)
  Tip = -> Clone173
FEATURE [PartDesign::FeatureBase] Clone174
  BaseFeature = -> Fusion006
  Suppressed = false
FEATURE [PartDesign::Body] Body173  label="KA8-5"
  AllowCompound = false
  Group = -> [Clone174]
  Origin = -> Origin287
  Placement = pos=(18.5,80,0.16) rot=(0,0,1;0rad)
  Tip = -> Clone174
FEATURE [PartDesign::FeatureBase] Clone175
  BaseFeature = -> Fusion006
  Suppressed = false
FEATURE [PartDesign::Body] Body174  label="KA9-5"
  AllowCompound = false
  Group = -> [Clone175]
  Origin = -> Origin288
  Placement = pos=(18.5,90,-0.17) rot=(0,0,1;0rad)
  Tip = -> Clone175
FEATURE [PartDesign::FeatureBase] Clone176
  BaseFeature = -> Fusion006
  Suppressed = false
FEATURE [PartDesign::Body] Body175  label="KA5-6"
  AllowCompound = false
  Group = -> [Clone176]
  Origin = -> Origin289
  Placement = pos=(7.5,50,1.16) rot=(0,0,1;0rad)
  Tip = -> Clone176
FEATURE [PartDesign::FeatureBase] Clone177
  BaseFeature = -> Fusion006
  Suppressed = false
FEATURE [PartDesign::Body] Body176  label="KA6-6"
  AllowCompound = false
  Group = -> [Clone177]
  Origin = -> Origin290
  Placement = pos=(7.5,60,0.83) rot=(0,0,1;0rad)
  Tip = -> Clone177
FEATURE [PartDesign::FeatureBase] Clone178
  BaseFeature = -> Fusion006
  Suppressed = false
FEATURE [PartDesign::Body] Body177  label="KA7-6"
  AllowCompound = false
  Group = -> [Clone178]
  Origin = -> Origin291
  Placement = pos=(7.5,70,0.49) rot=(0,0,1;0rad)
  Tip = -> Clone178
FEATURE [PartDesign::FeatureBase] Clone179
  BaseFeature = -> Fusion006
  Suppressed = false
FEATURE [PartDesign::Body] Body178  label="KA8-6"
  AllowCompound = false
  Group = -> [Clone179]
  Origin = -> Origin292
  Placement = pos=(7.5,80,0.16) rot=(0,0,1;0rad)
  Tip = -> Clone179
FEATURE [PartDesign::FeatureBase] Clone180
  BaseFeature = -> Fusion006
  Suppressed = false
FEATURE [PartDesign::Body] Body179  label="KA9-6"
  AllowCompound = false
  Group = -> [Clone180]
  Origin = -> Origin293
  Placement = pos=(7.5,90,-0.17) rot=(0,0,1;0rad)
  Tip = -> Clone180
FEATURE [Part::MultiFuse] Fusion010  label="KEYS A"
  Shapes = -> [Body122,Body124,Body128,Body129,Body130,Body131,Body132,Body133,Body134,Body140,Body141,Body142,Body143,Body144,Body150,Body151,Body152,Body153,Body154,Body160,Body161,Body162,Body163,Body164,Body170,Body171,Body172,Body173,Body174,Body175,Body176,Body177,Body178,Body179]
FEATURE [PartDesign::FeatureBase] Clone181
  BaseFeature = -> Fillet008
  Suppressed = false
FEATURE [PartDesign::Body] Body180  label="CA5-5"
  AllowCompound = false
  Group = -> [Clone181]
  Origin = -> Origin294
  Placement = pos=(18.5,50,0) rot=(0,0,1;0rad)
  Tip = -> Clone181
FEATURE [PartDesign::FeatureBase] Clone182
  BaseFeature = -> Fillet008
  Suppressed = false
FEATURE [PartDesign::Body] Body181  label="CA6-5"
  AllowCompound = false
  Group = -> [Clone182]
  Origin = -> Origin295
  Placement = pos=(18.5,60,0) rot=(0,0,1;0rad)
  Tip = -> Clone182
FEATURE [PartDesign::FeatureBase] Clone183
  BaseFeature = -> Fillet008
  Suppressed = false
FEATURE [PartDesign::Body] Body182  label="CA7-5"
  AllowCompound = false
  Group = -> [Clone183]
  Origin = -> Origin296
  Placement = pos=(18.5,70,0) rot=(0,0,1;0rad)
  Tip = -> Clone183
FEATURE [PartDesign::FeatureBase] Clone184
  BaseFeature = -> Fillet008
  Suppressed = false
FEATURE [PartDesign::Body] Body183  label="CA8-5"
  AllowCompound = false
  Group = -> [Clone184]
  Origin = -> Origin297
  Placement = pos=(18.5,80,0) rot=(0,0,1;0rad)
  Tip = -> Clone184
FEATURE [PartDesign::FeatureBase] Clone185
  BaseFeature = -> Fillet008
  Suppressed = false
FEATURE [PartDesign::Body] Body184  label="CA9-5"
  AllowCompound = false
  Group = -> [Clone185]
  Origin = -> Origin298
  Placement = pos=(18.5,90,0) rot=(0,0,1;0rad)
  Tip = -> Clone185
FEATURE [PartDesign::FeatureBase] Clone186
  BaseFeature = -> Fillet008
  Suppressed = false
FEATURE [PartDesign::Body] Body185  label="CA5-6"
  AllowCompound = false
  Group = -> [Clone186]
  Origin = -> Origin299
  Placement = pos=(7.5,50,0) rot=(0,0,1;0rad)
  Tip = -> Clone186
FEATURE [PartDesign::FeatureBase] Clone187
  BaseFeature = -> Fillet008
  Suppressed = false
FEATURE [PartDesign::Body] Body186  label="CA6-6"
  AllowCompound = false
  Group = -> [Clone187]
  Origin = -> Origin300
  Placement = pos=(7.5,60,0) rot=(0,0,1;0rad)
  Tip = -> Clone187
FEATURE [PartDesign::FeatureBase] Clone188
  BaseFeature = -> Fillet008
  Suppressed = false
FEATURE [PartDesign::Body] Body187  label="CA7-6"
  AllowCompound = false
  Group = -> [Clone188]
  Origin = -> Origin301
  Placement = pos=(7.5,70,0) rot=(0,0,1;0rad)
  Tip = -> Clone188
FEATURE [PartDesign::FeatureBase] Clone189
  BaseFeature = -> Fillet008
  Suppressed = false
FEATURE [PartDesign::Body] Body188  label="CA8-6"
  AllowCompound = false
  Group = -> [Clone189]
  Origin = -> Origin302
  Placement = pos=(7.5,80,0) rot=(0,0,1;0rad)
  Tip = -> Clone189
FEATURE [PartDesign::FeatureBase] Clone190
  BaseFeature = -> Fillet008
  Suppressed = false
FEATURE [PartDesign::Body] Body189  label="CA9-6"
  AllowCompound = false
  Group = -> [Clone190]
  Origin = -> Origin303
  Placement = pos=(7.5,90,0) rot=(0,0,1;0rad)
  Tip = -> Clone190
FEATURE [Part::Box] Box049  label="Cube048"
  AttacherType = Attacher::AttachEngine3D
  Height = 8
  Length = 3.3
  Placement = pos=(11.8,95.1,1) rot=(0,0,1;0rad)
  Width = 2.5
FEATURE [Part::Box] Box050  label="Cube049"
  AttacherType = Attacher::AttachEngine3D
  Height = 7
  Length = 4
  Placement = pos=(11.4,94.9,1) rot=(0,0,1;0rad)
  Width = 3
FEATURE [Part::Box] Box051  label="Cube050"
  AttacherType = Attacher::AttachEngine3D
  Height = 3
  Length = 9
  Placement = pos=(9.2,93.4,-1.3) rot=(-1,0,0;0.034907rad)
  Width = 6
FEATURE [Part::Cut] Cut015
  Base = -> Box050
  Tool = -> Box049
FEATURE [Part::Cut] Cut016  label="LED_02"
  Base = -> Cut015
  Placement = pos=(-5.7,0,0) rot=(0,0,1;0rad)
  Tool = -> Box051
FEATURE [Part::Cylinder] Cylinder015  label="LED02"
  Angle = 360
  AttacherType = Attacher::AttachEngine3D
  FirstAngle = 0
  Height = 10
  Placement = pos=(7.5,95.75,0) rot=(0,0,1;0rad)
  Radius = 0.5
  SecondAngle = 0
FEATURE [Part::Box] Box052  label="Cube051"
  AttacherType = Attacher::AttachEngine3D
  Height = 2.3
  Length = 10
  Placement = pos=(-5,-3,0) rot=(0,0,1;0rad)
  Width = 6
FEATURE [Part::Box] Box053  label="Cube052"
  AttacherType = Attacher::AttachEngine3D
  Height = 3
  Length = 10
  Placement = pos=(-5,-6,-0.6) rot=(-1,0,0;0.488692rad)
  Width = 6
FEATURE [Part::Cut] Cut017
  Base = -> Box052
  Tool = -> Box053
FEATURE [Part::Cylinder] Cylinder016
  Angle = 360
  AttacherType = Attacher::AttachEngine3D
  FirstAngle = 0
  Height = 0.4
  Placement = pos=(0,3,1.9) rot=(0,0,1;0rad)
  Radius = 1.5
  SecondAngle = 0
FEATURE [Part::Fillet] Fillet009
  Base = -> Cut017
  EdgeLinks = -> Cut017 [Edge1,Edge3,Edge4,Edge5,Edge6,Edge8,Edge11,Edge12,Edge13,Edge14,Edge15]
  Edges = 11 edges: [Edge1 r=0.3,Edge3 r=0.3,Edge4 r=0.3,Edge5 r=0.3,Edge6 r=0.3,Edge8 r=0.3,Edge11 r=0.3,Edge12 r=0.3,Edge13 r=0.3,Edge14 r=1,Edge15 r=0.3]
FEATURE [Part::MultiFuse] Fusion011  label="KEY B"
  Refine = true
  Shapes = -> [Cylinder016,Fillet009]
FEATURE [PartDesign::FeatureBase] Clone191
  BaseFeature = -> Fusion011
  Suppressed = false
FEATURE [PartDesign::Body] Body190  label="KB1-2"
  AllowCompound = false
  Group = -> [Clone191]
  Origin = -> Origin304
  Placement = pos=(47.5,7,2.58) rot=(0,0,1;0rad)
  Tip = -> Clone191
FEATURE [PartDesign::FeatureBase] Clone192
  BaseFeature = -> Fusion011
  Suppressed = false
FEATURE [PartDesign::Body] Body191  label="KB2-2"
  AllowCompound = false
  Group = -> [Clone192]
  Origin = -> Origin305
  Placement = pos=(47.5,17,2.25) rot=(0,0,1;0rad)
  Tip = -> Clone192
FEATURE [PartDesign::FeatureBase] Clone193
  BaseFeature = -> Fusion011
  Suppressed = false
FEATURE [PartDesign::Body] Body192  label="KB3-2"
  AllowCompound = false
  Group = -> [Clone193]
  Origin = -> Origin306
  Placement = pos=(47.5,27,1.92) rot=(0,0,1;0rad)
  Tip = -> Clone193
FEATURE [PartDesign::FeatureBase] Clone194
  BaseFeature = -> Fusion011
  Suppressed = false
FEATURE [PartDesign::Body] Body193  label="KB4-2"
  AllowCompound = false
  Group = -> [Clone194]
  Origin = -> Origin307
  Placement = pos=(47.5,37,1.59) rot=(0,0,1;0rad)
  Tip = -> Clone194
FEATURE [Part::Box] Box054  label="Cube053"
  AttacherType = Attacher::AttachEngine3D
  Height = 10
  Length = 11
  Placement = pos=(-5.5,-3.5,0) rot=(0,0,1;0rad)
  Width = 7
FEATURE [Part::Box] Box055  label="Cube054"
  AttacherType = Attacher::AttachEngine3D
  Height = 10
  Length = 2
  Placement = pos=(2,-4.9,0) rot=(0,0,1;0rad)
  Width = 3
FEATURE [Part::Box] Box056  label="Cube055"
  AttacherType = Attacher::AttachEngine3D
  Height = 10
  Length = 2
  Placement = pos=(-4,-4.9,0) rot=(0,0,1;0rad)
  Width = 3
FEATURE [Part::Box] Box057  label="Cube056"
  AttacherType = Attacher::AttachEngine3D
  Height = 10
  Length = 1
  Placement = pos=(2.5,-6,0) rot=(0,0,1;0rad)
  Width = 4
FEATURE [Part::Box] Box058  label="Cube057"
  AttacherType = Attacher::AttachEngine3D
  Height = 10
  Length = 1
  Placement = pos=(-3.5,-6,0) rot=(0,0,1;0rad)
  Width = 4
FEATURE [Part::Cylinder] Cylinder017
  Angle = 360
  AttacherType = Attacher::AttachEngine3D
  FirstAngle = 0
  Height = 10
  Placement = pos=(0,3,0) rot=(0,0,1;0rad)
  Radius = 1.8
  SecondAngle = 0
FEATURE [Part::MultiFuse] Fusion012
  Refine = true
  Shapes = -> [Box054,Box055,Box056,Cylinder017]
FEATURE [Part::MultiFuse] Fusion013
  Shapes = -> [Box057,Box058]
FEATURE [Part::Cut] Cut018  label="Cut A001"
  Base = -> Fusion012
  Tool = -> Fusion013
FEATURE [Part::Fillet] Fillet010  label="CUT B"
  Base = -> Cut018
  EdgeLinks = -> Cut018 [Edge49,Edge50,Edge63,Edge64]
  Edges = 4 edges r=0.5: [Edge49,Edge50,Edge63,Edge64]
FEATURE [PartDesign::FeatureBase] Clone195
  BaseFeature = -> Fillet010
  Suppressed = false
FEATURE [PartDesign::Body] Body194  label="CB1-2"
  AllowCompound = false
  Group = -> [Clone195]
  Origin = -> Origin308
  Placement = pos=(47.5,7,0) rot=(0,0,1;0rad)
  Tip = -> Clone195
FEATURE [PartDesign::FeatureBase] Clone196
  BaseFeature = -> Fillet010
  Suppressed = false
FEATURE [PartDesign::Body] Body195  label="CB2-2"
  AllowCompound = false
  Group = -> [Clone196]
  Origin = -> Origin309
  Placement = pos=(47.5,17,0) rot=(0,0,1;0rad)
  Tip = -> Clone196
FEATURE [PartDesign::FeatureBase] Clone197
  BaseFeature = -> Fillet010
  Suppressed = false
FEATURE [PartDesign::Body] Body196  label="CB3-2"
  AllowCompound = false
  Group = -> [Clone197]
  Origin = -> Origin310
  Placement = pos=(47.5,27,0) rot=(0,0,1;0rad)
  Tip = -> Clone197
FEATURE [PartDesign::FeatureBase] Clone198
  BaseFeature = -> Fillet010
  Suppressed = false
FEATURE [PartDesign::Body] Body197  label="CB4-2"
  AllowCompound = false
  Group = -> [Clone198]
  Origin = -> Origin311
  Placement = pos=(47.5,37,0) rot=(0,0,1;0rad)
  Tip = -> Clone198
FEATURE [PartDesign::FeatureBase] Clone199
  BaseFeature = -> Fillet010
  Suppressed = false
FEATURE [PartDesign::Body] Body198  label="CB1-3"
  AllowCompound = false
  Group = -> [Clone199]
  Origin = -> Origin312
  Placement = pos=(34.5,7,0) rot=(0,0,1;0rad)
  Tip = -> Clone199
FEATURE [PartDesign::FeatureBase] Clone200
  BaseFeature = -> Fusion011
  Suppressed = false
FEATURE [PartDesign::Body] Body199  label="KB1-3"
  AllowCompound = false
  Group = -> [Clone200]
  Origin = -> Origin313
  Placement = pos=(34.5,7,2.58) rot=(0,0,1;0rad)
  Tip = -> Clone200
FEATURE [PartDesign::FeatureBase] Clone201
  BaseFeature = -> Fusion011
  Suppressed = false
FEATURE [PartDesign::Body] Body200  label="KB2-3"
  AllowCompound = false
  Group = -> [Clone201]
  Origin = -> Origin314
  Placement = pos=(34.5,17,2.25) rot=(0,0,1;0rad)
  Tip = -> Clone201
FEATURE [PartDesign::FeatureBase] Clone202
  BaseFeature = -> Fusion011
  Suppressed = false
FEATURE [PartDesign::Body] Body201  label="KB3-3"
  AllowCompound = false
  Group = -> [Clone202]
  Origin = -> Origin315
  Placement = pos=(34.5,27,1.92) rot=(0,0,1;0rad)
  Tip = -> Clone202
FEATURE [PartDesign::FeatureBase] Clone203
  BaseFeature = -> Fusion011
  Suppressed = false
FEATURE [PartDesign::Body] Body202  label="KB4-3"
  AllowCompound = false
  Group = -> [Clone203]
  Origin = -> Origin316
  Placement = pos=(34.5,37,1.59) rot=(0,0,1;0rad)
  Tip = -> Clone203
FEATURE [PartDesign::FeatureBase] Clone204
  BaseFeature = -> Fusion011
  Suppressed = false
FEATURE [PartDesign::Body] Body203  label="KB1-4"
  AllowCompound = false
  Group = -> [Clone204]
  Origin = -> Origin317
  Placement = pos=(21.5,7,2.58) rot=(0,0,1;0rad)
  Tip = -> Clone204
FEATURE [PartDesign::FeatureBase] Clone205
  BaseFeature = -> Fusion011
  Suppressed = false
FEATURE [PartDesign::Body] Body204  label="KB2-4"
  AllowCompound = false
  Group = -> [Clone205]
  Origin = -> Origin318
  Placement = pos=(21.5,17,2.25) rot=(0,0,1;0rad)
  Tip = -> Clone205
FEATURE [PartDesign::FeatureBase] Clone206
  BaseFeature = -> Fusion011
  Suppressed = false
FEATURE [PartDesign::Body] Body205  label="KB3-4"
  AllowCompound = false
  Group = -> [Clone206]
  Origin = -> Origin319
  Placement = pos=(21.5,27,1.92) rot=(0,0,1;0rad)
  Tip = -> Clone206
FEATURE [PartDesign::FeatureBase] Clone207
  BaseFeature = -> Fusion011
  Suppressed = false
FEATURE [PartDesign::Body] Body206  label="KB4-4"
  AllowCompound = false
  Group = -> [Clone207]
  Origin = -> Origin320
  Placement = pos=(21.5,37,1.59) rot=(0,0,1;0rad)
  Tip = -> Clone207
FEATURE [PartDesign::FeatureBase] Clone208
  BaseFeature = -> Fusion011
  Suppressed = false
FEATURE [PartDesign::Body] Body207  label="KB1-5"
  AllowCompound = false
  Group = -> [Clone208]
  Origin = -> Origin321
  Placement = pos=(8.5,7,2.58) rot=(0,0,1;0rad)
  Tip = -> Clone208
FEATURE [PartDesign::FeatureBase] Clone209
  BaseFeature = -> Fusion011
  Suppressed = false
FEATURE [PartDesign::Body] Body208  label="KB2-5"
  AllowCompound = false
  Group = -> [Clone209]
  Origin = -> Origin322
  Placement = pos=(8.5,17,2.25) rot=(0,0,1;0rad)
  Tip = -> Clone209
FEATURE [PartDesign::FeatureBase] Clone210
  BaseFeature = -> Fusion011
  Suppressed = false
FEATURE [PartDesign::Body] Body209  label="KB3-5"
  AllowCompound = false
  Group = -> [Clone210]
  Origin = -> Origin323
  Placement = pos=(8.5,27,1.92) rot=(0,0,1;0rad)
  Tip = -> Clone210
FEATURE [PartDesign::FeatureBase] Clone211
  BaseFeature = -> Fusion011
  Suppressed = false
FEATURE [PartDesign::Body] Body210  label="KB4-5"
  AllowCompound = false
  Group = -> [Clone211]
  Origin = -> Origin324
  Placement = pos=(8.5,37,1.59) rot=(0,0,1;0rad)
  Tip = -> Clone211
FEATURE [Part::MultiFuse] Fusion014  label="KEYS B"
  Shapes = -> [Body190,Body191,Body192,Body193,Body199,Body200,Body201,Body202,Body203,Body204,Body205,Body206,Body207,Body208,Body209,Body210]
FEATURE [PartDesign::FeatureBase] Clone212
  BaseFeature = -> Fillet010
  Suppressed = false
FEATURE [PartDesign::Body] Body211  label="CB2-3"
  AllowCompound = false
  Group = -> [Clone212]
  Origin = -> Origin325
  Placement = pos=(34.5,17,0) rot=(0,0,1;0rad)
  Tip = -> Clone212
FEATURE [PartDesign::FeatureBase] Clone213
  BaseFeature = -> Fillet010
  Suppressed = false
FEATURE [PartDesign::Body] Body212  label="CB3-3"
  AllowCompound = false
  Group = -> [Clone213]
  Origin = -> Origin326
  Placement = pos=(34.5,27,0) rot=(0,0,1;0rad)
  Tip = -> Clone213
FEATURE [PartDesign::FeatureBase] Clone214
  BaseFeature = -> Fillet010
  Suppressed = false
FEATURE [PartDesign::Body] Body213  label="CB4-3"
  AllowCompound = false
  Group = -> [Clone214]
  Origin = -> Origin327
  Placement = pos=(34.5,37,0) rot=(0,0,1;0rad)
  Tip = -> Clone214
FEATURE [PartDesign::FeatureBase] Clone215
  BaseFeature = -> Fillet010
  Suppressed = false
FEATURE [PartDesign::Body] Body214  label="CB1-4"
  AllowCompound = false
  Group = -> [Clone215]
  Origin = -> Origin328
  Placement = pos=(21.5,7,0) rot=(0,0,1;0rad)
  Tip = -> Clone215
FEATURE [PartDesign::FeatureBase] Clone216
  BaseFeature = -> Fillet010
  Suppressed = false
FEATURE [PartDesign::Body] Body215  label="CB2-4"
  AllowCompound = false
  Group = -> [Clone216]
  Origin = -> Origin329
  Placement = pos=(21.5,17,0) rot=(0,0,1;0rad)
  Tip = -> Clone216
FEATURE [PartDesign::FeatureBase] Clone217
  BaseFeature = -> Fillet010
  Suppressed = false
FEATURE [PartDesign::Body] Body216  label="CB3-4"
  AllowCompound = false
  Group = -> [Clone217]
  Origin = -> Origin330
  Placement = pos=(21.5,27,0) rot=(0,0,1;0rad)
  Tip = -> Clone217
FEATURE [PartDesign::FeatureBase] Clone218
  BaseFeature = -> Fillet010
  Suppressed = false
FEATURE [PartDesign::Body] Body217  label="CB4-4"
  AllowCompound = false
  Group = -> [Clone218]
  Origin = -> Origin331
  Placement = pos=(21.5,37,0) rot=(0,0,1;0rad)
  Tip = -> Clone218
FEATURE [PartDesign::FeatureBase] Clone219
  BaseFeature = -> Fillet010
  Suppressed = false
FEATURE [PartDesign::Body] Body218  label="CB1-5"
  AllowCompound = false
  Group = -> [Clone219]
  Origin = -> Origin332
  Placement = pos=(8.5,7,0) rot=(0,0,1;0rad)
  Tip = -> Clone219
FEATURE [PartDesign::FeatureBase] Clone220
  BaseFeature = -> Fillet010
  Suppressed = false
FEATURE [PartDesign::Body] Body219  label="CB2-5"
  AllowCompound = false
  Group = -> [Clone220]
  Origin = -> Origin333
  Placement = pos=(8.5,17,0) rot=(0,0,1;0rad)
  Tip = -> Clone220
FEATURE [PartDesign::FeatureBase] Clone221
  BaseFeature = -> Fillet010
  Suppressed = false
FEATURE [PartDesign::Body] Body220  label="CB3-5"
  AllowCompound = false
  Group = -> [Clone221]
  Origin = -> Origin334
  Placement = pos=(8.5,27,0) rot=(0,0,1;0rad)
  Tip = -> Clone221
FEATURE [PartDesign::FeatureBase] Clone222
  BaseFeature = -> Fillet010
  Suppressed = false
FEATURE [PartDesign::Body] Body221  label="CB4-5"
  AllowCompound = false
  Group = -> [Clone222]
  Origin = -> Origin335
  Placement = pos=(8.5,37,0) rot=(0,0,1;0rad)
  Tip = -> Clone222
FEATURE [Part::Box] Box059  label="Cube058"
  AttacherType = Attacher::AttachEngine3D
  Height = 0.2
  Length = 66
  Placement = pos=(2,2,4.3) rot=(-1,0,0;0.033161rad)
  Width = 96
FEATURE [Part::Fillet] Fillet011
  Base = -> Box059
  EdgeLinks = -> Box059 [Edge1,Edge3,Edge5,Edge7]
  Edges = 4 edges r=1: [Edge1,Edge3,Edge5,Edge7]
FEATURE [Part::Box] Box060  label="Cube059"
  AttacherType = Attacher::AttachEngine3D
  Height = 10
  Length = 10.5
  Placement = pos=(-5.25,-3.25,0) rot=(0,0,1;0rad)
  Width = 6.5
FEATURE [Part::Fillet] Fillet012  label="C2B"
  Base = -> Box060
  EdgeLinks = -> Box060 [Edge1,Edge3,Edge5,Edge7]
  Edges = 4 edges r=0.2: [Edge1,Edge3,Edge5,Edge7]
FEATURE [PartDesign::FeatureBase] Clone223
  BaseFeature = -> Fillet012
  Suppressed = false
FEATURE [PartDesign::Body] Body222
  AllowCompound = false
  Group = -> [Clone223]
  Origin = -> Origin336
  Placement = pos=(47.5,7,0) rot=(0,0,1;0rad)
  Tip = -> Clone223
FEATURE [PartDesign::FeatureBase] Clone224
  BaseFeature = -> Fillet012
  Suppressed = false
FEATURE [PartDesign::Body] Body223
  AllowCompound = false
  Group = -> [Clone224]
  Origin = -> Origin337
  Placement = pos=(47.5,17,0) rot=(0,0,1;0rad)
  Tip = -> Clone224
FEATURE [PartDesign::FeatureBase] Clone225
  BaseFeature = -> Fillet012
  Suppressed = false
FEATURE [PartDesign::Body] Body224
  AllowCompound = false
  Group = -> [Clone225]
  Origin = -> Origin338
  Placement = pos=(47.5,27,0) rot=(0,0,1;0rad)
  Tip = -> Clone225
FEATURE [PartDesign::FeatureBase] Clone226
  BaseFeature = -> Fillet012
  Suppressed = false
FEATURE [PartDesign::Body] Body225
  AllowCompound = false
  Group = -> [Clone226]
  Origin = -> Origin339
  Placement = pos=(47.5,37,0) rot=(0,0,1;0rad)
  Tip = -> Clone226
FEATURE [PartDesign::FeatureBase] Clone227
  BaseFeature = -> Fillet012
  Suppressed = false
FEATURE [PartDesign::Body] Body226
  AllowCompound = false
  Group = -> [Clone227]
  Origin = -> Origin340
  Placement = pos=(34.5,7,0) rot=(0,0,1;0rad)
  Tip = -> Clone227
FEATURE [PartDesign::FeatureBase] Clone228
  BaseFeature = -> Fillet012
  Suppressed = false
FEATURE [PartDesign::Body] Body227
  AllowCompound = false
  Group = -> [Clone228]
  Origin = -> Origin341
  Placement = pos=(34.5,17,0) rot=(0,0,1;0rad)
  Tip = -> Clone228
FEATURE [PartDesign::FeatureBase] Clone229
  BaseFeature = -> Fillet012
  Suppressed = false
FEATURE [PartDesign::Body] Body228
  AllowCompound = false
  Group = -> [Clone229]
  Origin = -> Origin342
  Placement = pos=(34.5,27,0) rot=(0,0,1;0rad)
  Tip = -> Clone229
FEATURE [PartDesign::FeatureBase] Clone230
  BaseFeature = -> Fillet012
  Suppressed = false
FEATURE [PartDesign::Body] Body229
  AllowCompound = false
  Group = -> [Clone230]
  Origin = -> Origin343
  Placement = pos=(34.5,37,0) rot=(0,0,1;0rad)
  Tip = -> Clone230
FEATURE [PartDesign::FeatureBase] Clone231
  BaseFeature = -> Fillet012
  Suppressed = false
FEATURE [PartDesign::Body] Body230
  AllowCompound = false
  Group = -> [Clone231]
  Origin = -> Origin344
  Placement = pos=(21.5,7,0) rot=(0,0,1;0rad)
  Tip = -> Clone231
FEATURE [PartDesign::FeatureBase] Clone232
  BaseFeature = -> Fillet012
  Suppressed = false
FEATURE [PartDesign::Body] Body231
  AllowCompound = false
  Group = -> [Clone232]
  Origin = -> Origin345
  Placement = pos=(21.5,17,0) rot=(0,0,1;0rad)
  Tip = -> Clone232
FEATURE [PartDesign::FeatureBase] Clone233
  BaseFeature = -> Fillet012
  Suppressed = false
FEATURE [PartDesign::Body] Body232
  AllowCompound = false
  Group = -> [Clone233]
  Origin = -> Origin346
  Placement = pos=(21.5,27,0) rot=(0,0,1;0rad)
  Tip = -> Clone233
FEATURE [PartDesign::FeatureBase] Clone234
  BaseFeature = -> Fillet012
  Suppressed = false
FEATURE [PartDesign::Body] Body233
  AllowCompound = false
  Group = -> [Clone234]
  Origin = -> Origin347
  Placement = pos=(21.5,37,0) rot=(0,0,1;0rad)
  Tip = -> Clone234
FEATURE [PartDesign::FeatureBase] Clone235
  BaseFeature = -> Fillet012
  Suppressed = false
FEATURE [PartDesign::Body] Body234
  AllowCompound = false
  Group = -> [Clone235]
  Origin = -> Origin348
  Placement = pos=(8.5,7,0) rot=(0,0,1;0rad)
  Tip = -> Clone235
FEATURE [PartDesign::FeatureBase] Clone236
  BaseFeature = -> Fillet012
  Suppressed = false
FEATURE [PartDesign::Body] Body235
  AllowCompound = false
  Group = -> [Clone236]
  Origin = -> Origin349
  Placement = pos=(8.5,17,0) rot=(0,0,1;0rad)
  Tip = -> Clone236
FEATURE [PartDesign::FeatureBase] Clone237
  BaseFeature = -> Fillet012
  Suppressed = false
FEATURE [PartDesign::Body] Body236
  AllowCompound = false
  Group = -> [Clone237]
  Origin = -> Origin350
  Placement = pos=(8.5,27,0) rot=(0,0,1;0rad)
  Tip = -> Clone237
FEATURE [PartDesign::FeatureBase] Clone238
  BaseFeature = -> Fillet012
  Suppressed = false
FEATURE [PartDesign::Body] Body237
  AllowCompound = false
  Group = -> [Clone238]
  Origin = -> Origin351
  Placement = pos=(8.5,37,0) rot=(0,0,1;0rad)
  Tip = -> Clone238
FEATURE [Part::Box] Box061  label="Cube060"
  AttacherType = Attacher::AttachEngine3D
  Height = 3
  Length = 3
  Placement = pos=(68,133.2,6.3) rot=(0,0,1;0rad)
  Width = 3
FEATURE [Part::Box] Box062  label="Cube061"
  AttacherType = Attacher::AttachEngine3D
  Height = 3
  Length = 3
  Placement = pos=(70.5,133.2,6.3) rot=(0,0,1;0.785398rad)
  Width = 3
FEATURE [Part::Box] Box063  label="Cube062"
  AttacherType = Attacher::AttachEngine3D
  Height = 3
  Length = 3
  Placement = pos=(70.5,132,6.3) rot=(0,0,1;0.785398rad)
  Width = 3
FEATURE [Part::MultiFuse] Fusion017  label="SW01"
  Shapes = -> [Box061,Box062,Box063]
FEATURE [Part::Box] Box067  label="Cube066"
  AttacherType = Attacher::AttachEngine3D
  Height = 3
  Length = 3
  Placement = pos=(68,133.2,6.3) rot=(0,0,1;0rad)
  Width = 3
FEATURE [Part::Box] Box068  label="Cube067"
  AttacherType = Attacher::AttachEngine3D
  Height = 3
  Length = 3
  Placement = pos=(70.5,133.2,6.3) rot=(0,0,1;0.785398rad)
  Width = 3
FEATURE [Part::Box] Box069  label="Cube068"
  AttacherType = Attacher::AttachEngine3D
  Height = 3
  Length = 3
  Placement = pos=(70.5,132,6.3) rot=(0,0,1;0.785398rad)
  Width = 3
FEATURE [Part::MultiFuse] Fusion019  label="SW02"
  Placement = pos=(0,-11.75,0) rot=(0,0,1;0rad)
  Shapes = -> [Box067,Box068,Box069]
FEATURE [Part::Feature] text1_5
  shape: bbox 1.27 x 1.539 x 2e-07 mm, 1 faces, 0 solids (baked)
FEATURE [Part::Feature] text1_006
  shape: bbox 0.463 x 0.461 x 2e-07 mm, 1 faces, 0 solids (baked)
FEATURE [Part::Feature] text1_007
  shape: bbox 0.4682 x 0.4144 x 2e-07 mm, 1 faces, 0 solids (baked)
FEATURE [Part::Feature] text1_008
  shape: bbox 1.482 x 1.539 x 2e-07 mm, 1 faces, 0 solids (baked)
FEATURE [Part::Feature] text1_009
  shape: bbox 1.451 x 1.601 x 2e-07 mm, 1 faces, 0 solids (baked)
FEATURE [Part::Extrusion] Extrude019
  Base = -> text1_009
  Dir = (0,0,1)
  DirMode = 0
  FaceMakerClass = Part::FaceMakerBullseye
  FaceMakerMode = 3
  LengthFwd = 3
  LengthRev = 0
  Solid = true
  Symmetric = false
FEATURE [Part::Extrusion] Extrude020
  Base = -> text1_008
  Dir = (0,0,1)
  DirMode = 0
  FaceMakerClass = Part::FaceMakerBullseye
  FaceMakerMode = 3
  LengthFwd = 3
  LengthRev = 0
  Solid = true
  Symmetric = false
FEATURE [Part::Extrusion] Extrude021
  Base = -> text1_5
  Dir = (0,0,1)
  DirMode = 0
  FaceMakerClass = Part::FaceMakerBullseye
  FaceMakerMode = 3
  LengthFwd = 3
  LengthRev = 0
  Solid = true
  Symmetric = false
FEATURE [Part::Extrusion] Extrude022
  Base = -> text1_007
  Dir = (0,0,1)
  DirMode = 0
  FaceMakerClass = Part::FaceMakerBullseye
  FaceMakerMode = 3
  LengthFwd = 5
  LengthRev = 0
  Placement = pos=(0,0,-1) rot=(0,0,1;0rad)
  Solid = true
  Symmetric = false
FEATURE [Part::Extrusion] Extrude023
  Base = -> text1_006
  Dir = (0,0,1)
  DirMode = 0
  FaceMakerClass = Part::FaceMakerBullseye
  FaceMakerMode = 3
  LengthFwd = 5
  LengthRev = 0
  Placement = pos=(0,0,-1) rot=(0,0,1;0rad)
  Solid = true
  Symmetric = false
FEATURE [Part::Cut] Cut020
  Base = -> Extrude021
  Tool = -> Extrude023
FEATURE [Part::Cut] Cut021
  Base = -> Extrude020
  Tool = -> Extrude022
FEATURE [Part::MultiFuse] Fusion020  label="PRG"
  Placement = pos=(69.8,137,3.8) rot=(0.57735,-0.57735,0.57735;4.18879rad)
  Shapes = -> [Cut020,Cut021,Extrude019]
FEATURE [Part::Box] Box070  label="Cube069"
  AttacherType = Attacher::AttachEngine3D
  Height = 2.45
  Length = 9
  Placement = pos=(69.5,102.4,5.55) rot=(0,0,1;0rad)
  Width = 13.2
FEATURE [Part::Box] Box071  label="Cube070"
  AttacherType = Attacher::AttachEngine3D
  Height = 2.05
  Length = 10
  Placement = pos=(69.5,102.6,5.75) rot=(0,0,1;0rad)
  Width = 12.8
FEATURE [Part::Cut] Cut022  label="Cut024"
  Base = -> Box070
  Placement = pos=(0.4,0,0) rot=(0,0,1;0rad)
  Tool = -> Box071
FEATURE [Part::Box] Box072  label="Cube071"
  AttacherType = Attacher::AttachEngine3D
  Height = 0.85
  Length = 5
  Placement = pos=(67.5,113.42,6.05) rot=(0,0,1;0rad)
  Width = 0.85
FEATURE [Part::Box] Box073  label="Cube072"
  AttacherType = Attacher::AttachEngine3D
  Height = 2
  Length = 3
  Placement = pos=(69.5,112.84,5.48) rot=(0,0,1;0rad)
  Width = 2
FEATURE [Part::Chamfer] Chamfer
  Base = -> Box073
  EdgeLinks = -> Box073 [Edge1,Edge2,Edge3,Edge4]
  Edges = 4 edges r=0.8: [Edge1,Edge2,Edge3,Edge4]
FEATURE [Part::MultiFuse] Fusion021
  Placement = pos=(0,0.23,0.28) rot=(0,0,1;0rad)
  Shapes = -> [Chamfer,Box072]
FEATURE [Part::Box] Box074  label="Cube073"
  AttacherType = Attacher::AttachEngine3D
  Height = 0.85
  Length = 5
  Placement = pos=(67.5,113.42,6.05) rot=(0,0,1;0rad)
  Width = 0.85
FEATURE [Part::Box] Box075  label="Cube074"
  AttacherType = Attacher::AttachEngine3D
  Height = 2
  Length = 3
  Placement = pos=(69.5,112.84,5.48) rot=(0,0,1;0rad)
  Width = 2
FEATURE [Part::Chamfer] Chamfer001
  Base = -> Box075
  EdgeLinks = -> Box075 [Edge1,Edge2,Edge3,Edge4]
  Edges = 4 edges r=0.8: [Edge1,Edge2,Edge3,Edge4]
FEATURE [Part::MultiFuse] Fusion022
  Placement = pos=(0,-2.3,0.28) rot=(0,0,1;0rad)
  Shapes = -> [Chamfer001,Box074]
FEATURE [Part::Box] Box076  label="Cube075"
  AttacherType = Attacher::AttachEngine3D
  Height = 0.85
  Length = 5
  Placement = pos=(67.5,113.42,6.05) rot=(0,0,1;0rad)
  Width = 0.85
FEATURE [Part::Box] Box077  label="Cube076"
  AttacherType = Attacher::AttachEngine3D
  Height = 2
  Length = 3
  Placement = pos=(69.5,112.84,5.48) rot=(0,0,1;0rad)
  Width = 2
FEATURE [Part::Chamfer] Chamfer002
  Base = -> Box077
  EdgeLinks = -> Box077 [Edge1,Edge2,Edge3,Edge4]
  Edges = 4 edges r=0.8: [Edge1,Edge2,Edge3,Edge4]
FEATURE [Part::MultiFuse] Fusion023
  Placement = pos=(0,-4.85,0.28) rot=(0,0,1;0rad)
  Shapes = -> [Chamfer002,Box076]
FEATURE [Part::Box] Box078  label="Cube077"
  AttacherType = Attacher::AttachEngine3D
  Height = 0.85
  Length = 5
  Placement = pos=(67.5,113.42,6.05) rot=(0,0,1;0rad)
  Width = 0.85
FEATURE [Part::Box] Box079  label="Cube078"
  AttacherType = Attacher::AttachEngine3D
  Height = 2
  Length = 3
  Placement = pos=(69.5,112.84,5.48) rot=(0,0,1;0rad)
  Width = 2
FEATURE [Part::Chamfer] Chamfer003
  Base = -> Box079
  EdgeLinks = -> Box079 [Edge1,Edge2,Edge3,Edge4]
  Edges = 4 edges r=0.8: [Edge1,Edge2,Edge3,Edge4]
FEATURE [Part::MultiFuse] Fusion024
  Placement = pos=(0,-7.38,0.28) rot=(0,0,1;0rad)
  Shapes = -> [Chamfer003,Box078]
FEATURE [Part::Box] Box080  label="Cube079"
  AttacherType = Attacher::AttachEngine3D
  Height = 0.85
  Length = 5
  Placement = pos=(67.5,113.42,6.05) rot=(0,0,1;0rad)
  Width = 0.85
FEATURE [Part::Box] Box081  label="Cube080"
  AttacherType = Attacher::AttachEngine3D
  Height = 2
  Length = 3
  Placement = pos=(69.5,112.84,5.48) rot=(0,0,1;0rad)
  Width = 2
FEATURE [Part::Chamfer] Chamfer004
  Base = -> Box081
  EdgeLinks = -> Box081 [Edge1,Edge2,Edge3,Edge4]
  Edges = 4 edges r=0.8: [Edge1,Edge2,Edge3,Edge4]
FEATURE [Part::MultiFuse] Fusion025
  Placement = pos=(0,-9.925,0.28) rot=(0,0,1;0rad)
  Shapes = -> [Chamfer004,Box080]
FEATURE [Part::MultiFuse] Fusion026  label="JTAG"
  Shapes = -> [Fusion021,Fusion022,Fusion023,Fusion024,Fusion025]
FEATURE [Part::Box] Box082  label="Cube081"
  AttacherType = Attacher::AttachEngine3D
  Height = 10
  Length = 8.5
  Placement = pos=(-4.25,-3.25,0) rot=(0,0,1;0rad)
  Width = 6.5
FEATURE [Part::Fillet] Fillet013  label="C2A"
  Base = -> Box082
  EdgeLinks = -> Box082 [Edge1,Edge3,Edge5,Edge7]
  Edges = 4 edges r=0.2: [Edge1,Edge3,Edge5,Edge7]
FEATURE [PartDesign::FeatureBase] Clone239
  BaseFeature = -> Fillet013
  Suppressed = false
FEATURE [PartDesign::Body] Body238
  AllowCompound = false
  Group = -> [Clone239]
  Origin = -> Origin
  Placement = pos=(62.5,7,0) rot=(0,0,1;0rad)
  Tip = -> Clone239
FEATURE [PartDesign::FeatureBase] Clone240
  BaseFeature = -> Fillet013
  Suppressed = false
FEATURE [PartDesign::Body] Body239
  AllowCompound = false
  Group = -> [Clone240]
  Origin = -> Origin426
  Placement = pos=(62.5,17,0) rot=(0,0,1;0rad)
  Tip = -> Clone240
FEATURE [PartDesign::FeatureBase] Clone241
  BaseFeature = -> Fillet013
  Suppressed = false
FEATURE [PartDesign::Body] Body240
  AllowCompound = false
  Group = -> [Clone241]
  Origin = -> Origin427
  Placement = pos=(62.5,27,0) rot=(0,0,1;0rad)
  Tip = -> Clone241
FEATURE [PartDesign::FeatureBase] Clone242
  BaseFeature = -> Fillet013
  Suppressed = false
FEATURE [PartDesign::Body] Body241
  AllowCompound = false
  Group = -> [Clone242]
  Origin = -> Origin428
  Placement = pos=(62.5,37,0) rot=(0,0,1;0rad)
  Tip = -> Clone242
FEATURE [PartDesign::FeatureBase] Clone243
  BaseFeature = -> Fillet013
  Suppressed = false
FEATURE [PartDesign::Body] Body242
  AllowCompound = false
  Group = -> [Clone243]
  Origin = -> Origin429
  Placement = pos=(62.5,50,0) rot=(0,0,1;0rad)
  Tip = -> Clone243
FEATURE [PartDesign::FeatureBase] Clone244
  BaseFeature = -> Fillet013
  Suppressed = false
FEATURE [PartDesign::Body] Body243
  AllowCompound = false
  Group = -> [Clone244]
  Origin = -> Origin430
  Placement = pos=(62.5,60,0) rot=(0,0,1;0rad)
  Tip = -> Clone244
FEATURE [PartDesign::FeatureBase] Clone245
  BaseFeature = -> Fillet013
  Suppressed = false
FEATURE [PartDesign::Body] Body244
  AllowCompound = false
  Group = -> [Clone245]
  Origin = -> Origin431
  Placement = pos=(62.5,70,0) rot=(0,0,1;0rad)
  Tip = -> Clone245
FEATURE [PartDesign::FeatureBase] Clone246
  BaseFeature = -> Fillet013
  Suppressed = false
FEATURE [PartDesign::Body] Body245
  AllowCompound = false
  Group = -> [Clone246]
  Origin = -> Origin432
  Placement = pos=(62.5,80,0) rot=(0,0,1;0rad)
  Tip = -> Clone246
FEATURE [PartDesign::FeatureBase] Clone247
  BaseFeature = -> Fillet013
  Suppressed = false
FEATURE [PartDesign::Body] Body246
  AllowCompound = false
  Group = -> [Clone247]
  Origin = -> Origin433
  Placement = pos=(62.5,90,0) rot=(0,0,1;0rad)
  Tip = -> Clone247
FEATURE [PartDesign::FeatureBase] Clone248
  BaseFeature = -> Fillet013
  Suppressed = false
FEATURE [PartDesign::Body] Body247
  AllowCompound = false
  Group = -> [Clone248]
  Origin = -> Origin434
  Placement = pos=(51.5,50,0) rot=(0,0,1;0rad)
  Tip = -> Clone248
FEATURE [PartDesign::FeatureBase] Clone249
  BaseFeature = -> Fillet013
  Suppressed = false
FEATURE [PartDesign::Body] Body248
  AllowCompound = false
  Group = -> [Clone249]
  Origin = -> Origin435
  Placement = pos=(51.5,60,0) rot=(0,0,1;0rad)
  Tip = -> Clone249
FEATURE [PartDesign::FeatureBase] Clone250
  BaseFeature = -> Fillet013
  Suppressed = false
FEATURE [PartDesign::Body] Body249
  AllowCompound = false
  Group = -> [Clone250]
  Origin = -> Origin436
  Placement = pos=(51.5,70,0) rot=(0,0,1;0rad)
  Tip = -> Clone250
FEATURE [PartDesign::FeatureBase] Clone251
  BaseFeature = -> Fillet013
  Suppressed = false
FEATURE [PartDesign::Body] Body250
  AllowCompound = false
  Group = -> [Clone251]
  Origin = -> Origin437
  Placement = pos=(51.5,80,0) rot=(0,0,1;0rad)
  Tip = -> Clone251
FEATURE [PartDesign::FeatureBase] Clone252
  BaseFeature = -> Fillet013
  Suppressed = false
FEATURE [PartDesign::Body] Body251
  AllowCompound = false
  Group = -> [Clone252]
  Origin = -> Origin438
  Placement = pos=(51.5,90,0) rot=(0,0,1;0rad)
  Tip = -> Clone252
FEATURE [PartDesign::FeatureBase] Clone253
  BaseFeature = -> Fillet013
  Suppressed = false
FEATURE [PartDesign::Body] Body252
  AllowCompound = false
  Group = -> [Clone253]
  Origin = -> Origin439
  Placement = pos=(40.5,50,0) rot=(0,0,1;0rad)
  Tip = -> Clone253
FEATURE [PartDesign::FeatureBase] Clone254
  BaseFeature = -> Fillet013
  Suppressed = false
FEATURE [PartDesign::Body] Body253
  AllowCompound = false
  Group = -> [Clone254]
  Origin = -> Origin440
  Placement = pos=(40.5,60,0) rot=(0,0,1;0rad)
  Tip = -> Clone254
FEATURE [PartDesign::FeatureBase] Clone255
  BaseFeature = -> Fillet013
  Suppressed = false
FEATURE [PartDesign::Body] Body254
  AllowCompound = false
  Group = -> [Clone255]
  Origin = -> Origin441
  Placement = pos=(40.5,70,0) rot=(0,0,1;0rad)
  Tip = -> Clone255
FEATURE [PartDesign::FeatureBase] Clone256
  BaseFeature = -> Fillet013
  Suppressed = false
FEATURE [PartDesign::Body] Body255
  AllowCompound = false
  Group = -> [Clone256]
  Origin = -> Origin442
  Placement = pos=(40.5,80,0) rot=(0,0,1;0rad)
  Tip = -> Clone256
FEATURE [PartDesign::FeatureBase] Clone257
  BaseFeature = -> Fillet013
  Suppressed = false
FEATURE [PartDesign::Body] Body256
  AllowCompound = false
  Group = -> [Clone257]
  Origin = -> Origin443
  Placement = pos=(40.5,90,0) rot=(0,0,1;0rad)
  Tip = -> Clone257
FEATURE [PartDesign::FeatureBase] Clone258
  BaseFeature = -> Fillet013
  Suppressed = false
FEATURE [PartDesign::Body] Body257
  AllowCompound = false
  Group = -> [Clone258]
  Origin = -> Origin444
  Placement = pos=(29.5,50,0) rot=(0,0,1;0rad)
  Tip = -> Clone258
FEATURE [PartDesign::FeatureBase] Clone259
  BaseFeature = -> Fillet013
  Suppressed = false
FEATURE [PartDesign::Body] Body258
  AllowCompound = false
  Group = -> [Clone259]
  Origin = -> Origin445
  Placement = pos=(29.5,60,0) rot=(0,0,1;0rad)
  Tip = -> Clone259
FEATURE [PartDesign::FeatureBase] Clone260
  BaseFeature = -> Fillet013
  Suppressed = false
FEATURE [PartDesign::Body] Body259
  AllowCompound = false
  Group = -> [Clone260]
  Origin = -> Origin446
  Placement = pos=(29.5,70,0) rot=(0,0,1;0rad)
  Tip = -> Clone260
FEATURE [PartDesign::FeatureBase] Clone261
  BaseFeature = -> Fillet013
  Suppressed = false
FEATURE [PartDesign::Body] Body260
  AllowCompound = false
  Group = -> [Clone261]
  Origin = -> Origin447
  Placement = pos=(29.5,80,0) rot=(0,0,1;0rad)
  Tip = -> Clone261
FEATURE [PartDesign::FeatureBase] Clone262
  BaseFeature = -> Fillet013
  Suppressed = false
FEATURE [PartDesign::Body] Body261
  AllowCompound = false
  Group = -> [Clone262]
  Origin = -> Origin448
  Placement = pos=(29.5,90,0) rot=(0,0,1;0rad)
  Tip = -> Clone262
FEATURE [PartDesign::FeatureBase] Clone263
  BaseFeature = -> Fillet013
  Suppressed = false
FEATURE [PartDesign::Body] Body262
  AllowCompound = false
  Group = -> [Clone263]
  Origin = -> Origin449
  Placement = pos=(18.5,50,0) rot=(0,0,1;0rad)
  Tip = -> Clone263
FEATURE [PartDesign::FeatureBase] Clone264
  BaseFeature = -> Fillet013
  Suppressed = false
FEATURE [PartDesign::Body] Body263
  AllowCompound = false
  Group = -> [Clone264]
  Origin = -> Origin450
  Placement = pos=(18.5,60,0) rot=(0,0,1;0rad)
  Tip = -> Clone264
FEATURE [PartDesign::FeatureBase] Clone265
  BaseFeature = -> Fillet013
  Suppressed = false
FEATURE [PartDesign::Body] Body264
  AllowCompound = false
  Group = -> [Clone265]
  Origin = -> Origin451
  Placement = pos=(18.5,70,0) rot=(0,0,1;0rad)
  Tip = -> Clone265
FEATURE [PartDesign::FeatureBase] Clone266
  BaseFeature = -> Fillet013
  Suppressed = false
FEATURE [PartDesign::Body] Body265
  AllowCompound = false
  Group = -> [Clone266]
  Origin = -> Origin452
  Placement = pos=(18.5,80,0) rot=(0,0,1;0rad)
  Tip = -> Clone266
FEATURE [PartDesign::FeatureBase] Clone267
  BaseFeature = -> Fillet013
  Suppressed = false
FEATURE [PartDesign::Body] Body266
  AllowCompound = false
  Group = -> [Clone267]
  Origin = -> Origin453
  Placement = pos=(18.5,90,0) rot=(0,0,1;0rad)
  Tip = -> Clone267
FEATURE [PartDesign::FeatureBase] Clone268
  BaseFeature = -> Fillet013
  Suppressed = false
FEATURE [PartDesign::Body] Body267
  AllowCompound = false
  Group = -> [Clone268]
  Origin = -> Origin454
  Placement = pos=(7.5,50,0) rot=(0,0,1;0rad)
  Tip = -> Clone268
FEATURE [PartDesign::FeatureBase] Clone269
  BaseFeature = -> Fillet013
  Suppressed = false
FEATURE [PartDesign::Body] Body268
  AllowCompound = false
  Group = -> [Clone269]
  Origin = -> Origin455
  Placement = pos=(7.5,60,0) rot=(0,0,1;0rad)
  Tip = -> Clone269
FEATURE [PartDesign::FeatureBase] Clone270
  BaseFeature = -> Fillet013
  Suppressed = false
FEATURE [PartDesign::Body] Body269
  AllowCompound = false
  Group = -> [Clone270]
  Origin = -> Origin456
  Placement = pos=(7.5,70,0) rot=(0,0,1;0rad)
  Tip = -> Clone270
FEATURE [PartDesign::FeatureBase] Clone271
  BaseFeature = -> Fillet013
  Suppressed = false
FEATURE [PartDesign::Body] Body270
  AllowCompound = false
  Group = -> [Clone271]
  Origin = -> Origin457
  Placement = pos=(7.5,80,0) rot=(0,0,1;0rad)
  Tip = -> Clone271
FEATURE [PartDesign::FeatureBase] Clone272
  BaseFeature = -> Fillet013
  Suppressed = false
FEATURE [PartDesign::Body] Body271
  AllowCompound = false
  Group = -> [Clone272]
  Origin = -> Origin458
  Placement = pos=(7.5,90,0) rot=(0,0,1;0rad)
  Tip = -> Clone272
FEATURE [Part::MultiFuse] Fusion016
  Shapes = -> [Body222,Body223,Body224,Body225,Body226,Body227,Body228,Body229,Body230,Body231,Body232,Body233,Body234,Body235,Body236,Body237,Body238,Body239,Body240,Body241,Body242,Body243,Body244,Body245,Body246,Body247,Body248,Body249,Body250,Body251,Body252,Body253,Body254,Body255,Body256,Body257,Body258,Body259,Body260,Body261,Body262,Body263,Body264,Body265,Body266,Body267,Body268,Body269,Body270,Body271]
FEATURE [Part::Cut] Cut019  label="BEZEL"
  Base = -> Fillet011
  Placement = pos=(0,0,-0.1) rot=(0,0,1;0rad)
  Tool = -> Fusion016
FEATURE [Part::Cylinder] Cylinder018
  Angle = 360
  AttacherType = Attacher::AttachEngine3D
  FirstAngle = 0
  Height = 0.4
  Placement = pos=(54.75,3,4.7) rot=(0,0,1;0rad)
  Radius = 2.1
  SecondAngle = 0
FEATURE [Part::Cylinder] Cylinder019
  Angle = 360
  AttacherType = Attacher::AttachEngine3D
  FirstAngle = 0
  Height = 0.4
  Placement = pos=(15.25,3,4.7) rot=(0,0,1;0rad)
  Radius = 2.1
  SecondAngle = 0
FEATURE [Part::Cylinder] Cylinder020
  Angle = 360
  AttacherType = Attacher::AttachEngine3D
  FirstAngle = 0
  Height = 1.4
  Placement = pos=(55.35,32,3.7) rot=(0,0,1;0rad)
  Radius = 2.1
  SecondAngle = 0
FEATURE [Part::Cylinder] Cylinder021
  Angle = 360
  AttacherType = Attacher::AttachEngine3D
  FirstAngle = 0
  Height = 1.7
  Placement = pos=(67.05,43.5,3.4) rot=(0,0,1;0rad)
  Radius = 2.1
  SecondAngle = 0
FEATURE [Part::Cylinder] Cylinder022
  Angle = 360
  AttacherType = Attacher::AttachEngine3D
  FirstAngle = 0
  Height = 3.5
  Placement = pos=(3.05,96.5,1.6) rot=(0,0,1;0rad)
  Radius = 2.1
  SecondAngle = 0
FEATURE [Part::Cylinder] Cylinder023
  Angle = 360
  AttacherType = Attacher::AttachEngine3D
  FirstAngle = 0
  Height = 1.7
  Placement = pos=(3.05,43.5,3.4) rot=(0,0,1;0rad)
  Radius = 2.1
  SecondAngle = 0
FEATURE [Part::Cylinder] Cylinder024
  Angle = 360
  AttacherType = Attacher::AttachEngine3D
  FirstAngle = 0
  Height = 3.5
  Placement = pos=(67.05,96.5,1.6) rot=(0,0,1;0rad)
  Radius = 2.1
  SecondAngle = 0
FEATURE [Part::Box] Box083  label="Cube082"
  AttacherType = Attacher::AttachEngine3D
  Height = 4
  Length = 8
  Placement = pos=(0,146,4) rot=(0,0,1;0rad)
  Width = 5
FEATURE [Part::Cylinder] Cylinder025
  Angle = 360
  AttacherType = Attacher::AttachEngine3D
  FirstAngle = 0
  Height = 3.2
  Placement = pos=(5.25,148,4.8) rot=(0,0,1;0rad)
  Radius = 1.6
  SecondAngle = 0
FEATURE [Part::Cut] Cut023  label="Cut025"
  Base = -> Box083
  Tool = -> Cylinder025
FEATURE [Part::Fillet] Fillet014
  Base = -> Cut023
  EdgeLinks = -> Cut023 [Edge3]
  Edges = 1 edges r=1.5: [Edge3]
FEATURE [Part::Chamfer] Chamfer005
  Base = -> Fillet014
  EdgeLinks = -> Fillet014 [Edge12]
  Edges = 1 edges r=1: [Edge12]
FEATURE [Part::Box] Box084  label="Cube083"
  AttacherType = Attacher::AttachEngine3D
  Height = 4
  Length = 8
  Placement = pos=(62,146,4) rot=(0,0,1;0rad)
  Width = 5
FEATURE [Part::Cylinder] Cylinder026
  Angle = 360
  AttacherType = Attacher::AttachEngine3D
  FirstAngle = 0
  Height = 3.2
  Placement = pos=(64.8,148,4.8) rot=(0,0,1;0rad)
  Radius = 1.6
  SecondAngle = 0
FEATURE [Part::Cut] Cut024  label="Cut026"
  Base = -> Box084
  Tool = -> Cylinder026
FEATURE [Part::Fillet] Fillet015
  Base = -> Cut024
  EdgeLinks = -> Cut024 [Edge12]
  Edges = 1 edges r=1.5: [Edge12]
FEATURE [Part::Chamfer] Chamfer006
  Base = -> Fillet015
  EdgeLinks = -> Fillet015 [Edge16]
  Edges = 1 edges r=1: [Edge16]
FEATURE [Part::Cylinder] Cylinder027
  Angle = 360
  AttacherType = Attacher::AttachEngine3D
  FirstAngle = 0
  Height = 2.8
  Placement = pos=(24.4,75,2.3) rot=(0,0,1;0rad)
  Radius = 2.1
  SecondAngle = 0
FEATURE [Part::MultiFuse] Fusion027
  Placement = pos=(-0.3,-0.5,0) rot=(0,0,1;0rad)
  Refine = true
  Shapes = -> [Body100,Cylinder019]
FEATURE [Part::MultiFuse] Fusion028
  Placement = pos=(0.25,-0.5,0) rot=(0,0,1;0rad)
  Refine = true
  Shapes = -> [Cylinder018,Body101]
FEATURE [Part::MultiFuse] Fusion029
  Placement = pos=(-14.4,0,0) rot=(0,0,1;0rad)
  Refine = true
  Shapes = -> [Body102,Cylinder020]
FEATURE [Part::MultiFuse] Fusion030
  Placement = pos=(-0.05,0,0) rot=(0,0,1;0rad)
  Refine = true
  Shapes = -> [Cylinder021,Body104]
FEATURE [Part::MultiFuse] Fusion031
  Placement = pos=(-0.05,0,0) rot=(0,0,1;0rad)
  Refine = true
  Shapes = -> [Body103,Cylinder023]
FEATURE [Part::MultiFuse] Fusion032
  Placement = pos=(10.8,0,0) rot=(0,0,1;0rad)
  Refine = true
  Shapes = -> [Body106,Cylinder027]
FEATURE [Part::MultiFuse] Fusion033
  Refine = true
  Shapes = -> [Body105,Cylinder022]
FEATURE [Part::MultiFuse] Fusion034
  Refine = true
  Shapes = -> [Body107,Cylinder024]
FEATURE [Part::MultiFuse] Fusion035  label="SUPPORTS_01"
  Shapes = -> [Fusion027,Fusion028,Fusion029,Fusion030,Fusion031,Fusion032,Fusion033,Fusion034]
FEATURE [Part::Box] Box085  label="Cube084"
  AttacherType = Attacher::AttachEngine3D
  Height = 6.5
  Length = 2
  Placement = pos=(-1,-3,-1) rot=(0,0,1;0rad)
  Width = 6
FEATURE [Part::Box] Box086  label="Cube085"
  AttacherType = Attacher::AttachEngine3D
  Height = 6.5
  Length = 6
  Placement = pos=(-3,-1,-1) rot=(0,0,1;0rad)
  Width = 2
FEATURE [Part::MultiFuse] Fusion037
  Refine = true
  Shapes = -> [Box085,Box086]
FEATURE [Part::Chamfer] Chamfer007
  Base = -> Fusion037
  EdgeLinks = -> Fusion037 [Edge10,Edge14,Edge28,Edge35]
  Edges = 4 edges r=1: [Edge10,Edge14,Edge28,Edge35]
FEATURE [Part::Sphere] Sphere
  Angle1 = -90
  Angle2 = 90
  Angle3 = 360
  AttacherType = Attacher::AttachEngine3D
  Radius = 1.3
FEATURE [Part::Box] Box087  label="Cube086"
  AttacherType = Attacher::AttachEngine3D
  Height = 10
  Length = 10
  Placement = pos=(-5,-5,-10) rot=(0,0,1;0rad)
  Width = 10
FEATURE [Part::Cut] Cut025  label="SPHERE01"
  Base = -> Sphere
  Placement = pos=(0,0,5.5) rot=(0,0,1;0rad)
  Tool = -> Box087
FEATURE [Part::MultiFuse] Fusion038  label="PUSH01"
  Shapes = -> [Chamfer007,Cut025]
FEATURE [PartDesign::FeatureBase] Clone273
  BaseFeature = -> Fusion038
  Suppressed = false
FEATURE [PartDesign::Body] Body272  label="P1-1"
  AllowCompound = false
  Group = -> [Clone273]
  Origin = -> Origin459
  Placement = pos=(62.5,7,0.5) rot=(0,0,1;0rad)
  Tip = -> Clone273
FEATURE [PartDesign::FeatureBase] Clone274
  BaseFeature = -> Fusion038
  Suppressed = false
FEATURE [PartDesign::Body] Body273  label="P2-1"
  AllowCompound = false
  Group = -> [Clone274]
  Origin = -> Origin460
  Placement = pos=(62.5,17,0.5) rot=(0,0,1;0rad)
  Tip = -> Clone274
FEATURE [Part::Box] Box088  label="Cube087"
  AttacherType = Attacher::AttachEngine3D
  Height = 13.2
  Length = 66
  Placement = pos=(2,2,-8.8) rot=(-1,0,0;0.033161rad)
  Width = 96
FEATURE [Part::Cylinder] Cylinder028
  Angle = 360
  AttacherType = Attacher::AttachEngine3D
  FirstAngle = 0
  Height = 0.7
  Radius = 3.5
  SecondAngle = 0
FEATURE [Part::Fillet] Fillet016  label="DOME07"
  Base = -> Cylinder028
  EdgeLinks = -> Cylinder028 [Edge2]
  Edges = 1 edges r=0.6: [Edge2]
FEATURE [PartDesign::FeatureBase] Clone275
  BaseFeature = -> Fillet016
  Suppressed = false
FEATURE [PartDesign::Body] Body274  label="D4-1"
  AllowCompound = false
  Group = -> [Clone275]
  Origin = -> Origin461
  Placement = pos=(62.8,37,7.3) rot=(0,0,1;0rad)
  Tip = -> Clone275
FEATURE [PartDesign::FeatureBase] Clone276
  BaseFeature = -> Fillet016
  Suppressed = false
FEATURE [PartDesign::Body] Body275  label="D3-1"
  AllowCompound = false
  Group = -> [Clone276]
  Origin = -> Origin462
  Placement = pos=(62.8,27,7.3) rot=(0,0,1;0rad)
  Tip = -> Clone276
FEATURE [PartDesign::FeatureBase] Clone277
  BaseFeature = -> Fillet016
  Suppressed = false
FEATURE [PartDesign::Body] Body276  label="D5-1"
  AllowCompound = false
  Group = -> [Clone277]
  Origin = -> Origin463
  Placement = pos=(62.8,50,7.3) rot=(0,0,1;0rad)
  Tip = -> Clone277
FEATURE [PartDesign::FeatureBase] Clone278
  BaseFeature = -> Fillet016
  Suppressed = false
FEATURE [PartDesign::Body] Body277  label="D6-1"
  AllowCompound = false
  Group = -> [Clone278]
  Origin = -> Origin464
  Placement = pos=(62.8,60,7.3) rot=(0,0,1;0rad)
  Tip = -> Clone278
FEATURE [PartDesign::FeatureBase] Clone279
  BaseFeature = -> Fillet016
  Suppressed = false
FEATURE [PartDesign::Body] Body278  label="D7-1"
  AllowCompound = false
  Group = -> [Clone279]
  Origin = -> Origin465
  Placement = pos=(62.8,70,7.3) rot=(0,0,1;0rad)
  Tip = -> Clone279
FEATURE [PartDesign::FeatureBase] Clone280
  BaseFeature = -> Fillet016
  Suppressed = false
FEATURE [PartDesign::Body] Body279  label="D8-1"
  AllowCompound = false
  Group = -> [Clone280]
  Origin = -> Origin466
  Placement = pos=(62.8,80,7.3) rot=(0,0,1;0rad)
  Tip = -> Clone280
FEATURE [PartDesign::FeatureBase] Clone281
  BaseFeature = -> Fillet016
  Suppressed = false
FEATURE [PartDesign::Body] Body280  label="D9-1"
  AllowCompound = false
  Group = -> [Clone281]
  Origin = -> Origin467
  Placement = pos=(62.8,90,7.3) rot=(0,0,1;0rad)
  Tip = -> Clone281
FEATURE [PartDesign::FeatureBase] Clone282
  BaseFeature = -> Fillet016
  Suppressed = false
FEATURE [PartDesign::Body] Body281  label="D1-2"
  AllowCompound = false
  Group = -> [Clone282]
  Origin = -> Origin468
  Placement = pos=(47.8,7,7.3) rot=(0,0,1;0rad)
  Tip = -> Clone282
FEATURE [PartDesign::FeatureBase] Clone283
  BaseFeature = -> Fillet016
  Suppressed = false
FEATURE [PartDesign::Body] Body282  label="D2-2"
  AllowCompound = false
  Group = -> [Clone283]
  Origin = -> Origin469
  Placement = pos=(47.8,17,7.3) rot=(0,0,1;0rad)
  Tip = -> Clone283
FEATURE [PartDesign::FeatureBase] Clone284
  BaseFeature = -> Fillet016
  Suppressed = false
FEATURE [PartDesign::Body] Body283  label="D3-2"
  AllowCompound = false
  Group = -> [Clone284]
  Origin = -> Origin470
  Placement = pos=(47.8,27,7.3) rot=(0,0,1;0rad)
  Tip = -> Clone284
FEATURE [PartDesign::FeatureBase] Clone285
  BaseFeature = -> Fillet016
  Suppressed = false
FEATURE [PartDesign::Body] Body284  label="D4-2"
  AllowCompound = false
  Group = -> [Clone285]
  Origin = -> Origin471
  Placement = pos=(47.8,37,7.3) rot=(0,0,1;0rad)
  Tip = -> Clone285
FEATURE [PartDesign::FeatureBase] Clone286
  BaseFeature = -> Fillet016
  Suppressed = false
FEATURE [PartDesign::Body] Body285  label="D5-2"
  AllowCompound = false
  Group = -> [Clone286]
  Origin = -> Origin472
  Placement = pos=(51.8,50,7.3) rot=(0,0,1;0rad)
  Tip = -> Clone286
FEATURE [PartDesign::FeatureBase] Clone287
  BaseFeature = -> Fillet016
  Suppressed = false
FEATURE [PartDesign::Body] Body286  label="D6-2"
  AllowCompound = false
  Group = -> [Clone287]
  Origin = -> Origin473
  Placement = pos=(51.8,60,7.3) rot=(0,0,1;0rad)
  Tip = -> Clone287
FEATURE [PartDesign::FeatureBase] Clone288
  BaseFeature = -> Fillet016
  Suppressed = false
FEATURE [PartDesign::Body] Body287  label="D7-2"
  AllowCompound = false
  Group = -> [Clone288]
  Origin = -> Origin474
  Placement = pos=(51.8,70,7.3) rot=(0,0,1;0rad)
  Tip = -> Clone288
FEATURE [PartDesign::FeatureBase] Clone289
  BaseFeature = -> Fillet016
  Suppressed = false
FEATURE [PartDesign::Body] Body288  label="D8-2"
  AllowCompound = false
  Group = -> [Clone289]
  Origin = -> Origin475
  Placement = pos=(51.8,80,7.3) rot=(0,0,1;0rad)
  Tip = -> Clone289
FEATURE [PartDesign::FeatureBase] Clone290
  BaseFeature = -> Fillet016
  Suppressed = false
FEATURE [PartDesign::Body] Body289  label="D9-2"
  AllowCompound = false
  Group = -> [Clone290]
  Origin = -> Origin476
  Placement = pos=(51.8,90,7.3) rot=(0,0,1;0rad)
  Tip = -> Clone290
FEATURE [PartDesign::FeatureBase] Clone291
  BaseFeature = -> Fillet016
  Suppressed = false
FEATURE [PartDesign::Body] Body290  label="D5-3"
  AllowCompound = false
  Group = -> [Clone291]
  Origin = -> Origin477
  Placement = pos=(40.8,50,7.3) rot=(0,0,1;0rad)
  Tip = -> Clone291
FEATURE [PartDesign::FeatureBase] Clone292
  BaseFeature = -> Fillet016
  Suppressed = false
FEATURE [PartDesign::Body] Body291  label="D2-1"
  AllowCompound = false
  Group = -> [Clone292]
  Origin = -> Origin478
  Placement = pos=(62.8,17,7.3) rot=(0,0,1;0rad)
  Tip = -> Clone292
FEATURE [PartDesign::FeatureBase] Clone293
  BaseFeature = -> Fillet016
  Suppressed = false
FEATURE [PartDesign::Body] Body292  label="D1-1"
  AllowCompound = false
  Group = -> [Clone293]
  Origin = -> Origin479
  Placement = pos=(62.8,7,7.3) rot=(0,0,1;0rad)
  Tip = -> Clone293
FEATURE [PartDesign::FeatureBase] Clone294
  BaseFeature = -> Fillet016
  Suppressed = false
FEATURE [PartDesign::Body] Body293  label="D5-4"
  AllowCompound = false
  Group = -> [Clone294]
  Origin = -> Origin480
  Placement = pos=(29.8,50,7.3) rot=(0,0,1;0rad)
  Tip = -> Clone294
FEATURE [PartDesign::FeatureBase] Clone295
  BaseFeature = -> Fillet016
  Suppressed = false
FEATURE [PartDesign::Body] Body294  label="D6-4"
  AllowCompound = false
  Group = -> [Clone295]
  Origin = -> Origin481
  Placement = pos=(29.8,60,7.3) rot=(0,0,1;0rad)
  Tip = -> Clone295
FEATURE [PartDesign::FeatureBase] Clone296
  BaseFeature = -> Fillet016
  Suppressed = false
FEATURE [PartDesign::Body] Body295  label="D6-3"
  AllowCompound = false
  Group = -> [Clone296]
  Origin = -> Origin482
  Placement = pos=(40.8,60,7.3) rot=(0,0,1;0rad)
  Tip = -> Clone296
FEATURE [PartDesign::FeatureBase] Clone297
  BaseFeature = -> Fillet016
  Suppressed = false
FEATURE [PartDesign::Body] Body296  label="D7-3"
  AllowCompound = false
  Group = -> [Clone297]
  Origin = -> Origin483
  Placement = pos=(40.8,70,7.3) rot=(0,0,1;0rad)
  Tip = -> Clone297
FEATURE [PartDesign::FeatureBase] Clone298
  BaseFeature = -> Fillet016
  Suppressed = false
FEATURE [PartDesign::Body] Body297  label="D8-3"
  AllowCompound = false
  Group = -> [Clone298]
  Origin = -> Origin484
  Placement = pos=(40.8,80,7.3) rot=(0,0,1;0rad)
  Tip = -> Clone298
FEATURE [PartDesign::FeatureBase] Clone299
  BaseFeature = -> Fillet016
  Suppressed = false
FEATURE [PartDesign::Body] Body298  label="D9-3"
  AllowCompound = false
  Group = -> [Clone299]
  Origin = -> Origin485
  Placement = pos=(40.8,90,7.3) rot=(0,0,1;0rad)
  Tip = -> Clone299
FEATURE [PartDesign::FeatureBase] Clone300
  BaseFeature = -> Fillet016
  Suppressed = false
FEATURE [PartDesign::Body] Body299  label="D7-4"
  AllowCompound = false
  Group = -> [Clone300]
  Origin = -> Origin486
  Placement = pos=(29.8,70,7.3) rot=(0,0,1;0rad)
  Tip = -> Clone300
FEATURE [PartDesign::FeatureBase] Clone301
  BaseFeature = -> Fillet016
  Suppressed = false
FEATURE [PartDesign::Body] Body300  label="D8-4"
  AllowCompound = false
  Group = -> [Clone301]
  Origin = -> Origin487
  Placement = pos=(29.8,80,7.3) rot=(0,0,1;0rad)
  Tip = -> Clone301
FEATURE [PartDesign::FeatureBase] Clone302
  BaseFeature = -> Fillet016
  Suppressed = false
FEATURE [PartDesign::Body] Body301  label="D9-4"
  AllowCompound = false
  Group = -> [Clone302]
  Origin = -> Origin488
  Placement = pos=(29.8,90,7.3) rot=(0,0,1;0rad)
  Tip = -> Clone302
FEATURE [PartDesign::FeatureBase] Clone303
  BaseFeature = -> Fillet016
  Suppressed = false
FEATURE [PartDesign::Body] Body302  label="D5-5"
  AllowCompound = false
  Group = -> [Clone303]
  Origin = -> Origin489
  Placement = pos=(18.8,50,7.3) rot=(0,0,1;0rad)
  Tip = -> Clone303
FEATURE [PartDesign::FeatureBase] Clone304
  BaseFeature = -> Fillet016
  Suppressed = false
FEATURE [PartDesign::Body] Body303  label="D6-5"
  AllowCompound = false
  Group = -> [Clone304]
  Origin = -> Origin490
  Placement = pos=(18.8,60,7.3) rot=(0,0,1;0rad)
  Tip = -> Clone304
FEATURE [PartDesign::FeatureBase] Clone305
  BaseFeature = -> Fillet016
  Suppressed = false
FEATURE [PartDesign::Body] Body304  label="D7-5"
  AllowCompound = false
  Group = -> [Clone305]
  Origin = -> Origin491
  Placement = pos=(18.8,70,7.3) rot=(0,0,1;0rad)
  Tip = -> Clone305
FEATURE [PartDesign::FeatureBase] Clone306
  BaseFeature = -> Fillet016
  Suppressed = false
FEATURE [PartDesign::Body] Body305  label="D8-5"
  AllowCompound = false
  Group = -> [Clone306]
  Origin = -> Origin492
  Placement = pos=(18.8,80,7.3) rot=(0,0,1;0rad)
  Tip = -> Clone306
FEATURE [PartDesign::FeatureBase] Clone307
  BaseFeature = -> Fillet016
  Suppressed = false
FEATURE [PartDesign::Body] Body306  label="D9-5"
  AllowCompound = false
  Group = -> [Clone307]
  Origin = -> Origin493
  Placement = pos=(18.8,90,7.3) rot=(0,0,1;0rad)
  Tip = -> Clone307
FEATURE [PartDesign::FeatureBase] Clone308
  BaseFeature = -> Fillet016
  Suppressed = false
FEATURE [PartDesign::Body] Body307  label="D1-3"
  AllowCompound = false
  Group = -> [Clone308]
  Origin = -> Origin494
  Placement = pos=(34.8,7,7.3) rot=(0,0,1;0rad)
  Tip = -> Clone308
FEATURE [PartDesign::FeatureBase] Clone309
  BaseFeature = -> Fillet016
  Suppressed = false
FEATURE [PartDesign::Body] Body308  label="D5-6"
  AllowCompound = false
  Group = -> [Clone309]
  Origin = -> Origin495
  Placement = pos=(7.8,50,7.3) rot=(0,0,1;0rad)
  Tip = -> Clone309
FEATURE [PartDesign::FeatureBase] Clone310
  BaseFeature = -> Fillet016
  Suppressed = false
FEATURE [PartDesign::Body] Body309  label="D6-6"
  AllowCompound = false
  Group = -> [Clone310]
  Origin = -> Origin496
  Placement = pos=(7.8,60,7.3) rot=(0,0,1;0rad)
  Tip = -> Clone310
FEATURE [PartDesign::FeatureBase] Clone311
  BaseFeature = -> Fillet016
  Suppressed = false
FEATURE [PartDesign::Body] Body310  label="D7-6"
  AllowCompound = false
  Group = -> [Clone311]
  Origin = -> Origin497
  Placement = pos=(7.8,70,7.3) rot=(0,0,1;0rad)
  Tip = -> Clone311
FEATURE [PartDesign::FeatureBase] Clone312
  BaseFeature = -> Fillet016
  Suppressed = false
FEATURE [PartDesign::Body] Body311  label="D8-6"
  AllowCompound = false
  Group = -> [Clone312]
  Origin = -> Origin498
  Placement = pos=(7.8,80,7.3) rot=(0,0,1;0rad)
  Tip = -> Clone312
FEATURE [PartDesign::FeatureBase] Clone313
  BaseFeature = -> Fillet016
  Suppressed = false
FEATURE [PartDesign::Body] Body312  label="D9-6"
  AllowCompound = false
  Group = -> [Clone313]
  Origin = -> Origin499
  Placement = pos=(7.8,90,7.3) rot=(0,0,1;0rad)
  Tip = -> Clone313
FEATURE [PartDesign::FeatureBase] Clone314
  BaseFeature = -> Fillet016
  Suppressed = false
FEATURE [PartDesign::Body] Body313  label="D2-3"
  AllowCompound = false
  Group = -> [Clone314]
  Origin = -> Origin500
  Placement = pos=(34.8,17,7.3) rot=(0,0,1;0rad)
  Tip = -> Clone314
FEATURE [PartDesign::FeatureBase] Clone315
  BaseFeature = -> Fillet016
  Suppressed = false
FEATURE [PartDesign::Body] Body314  label="D3-3"
  AllowCompound = false
  Group = -> [Clone315]
  Origin = -> Origin501
  Placement = pos=(34.8,27,7.3) rot=(0,0,1;0rad)
  Tip = -> Clone315
FEATURE [PartDesign::FeatureBase] Clone316
  BaseFeature = -> Fillet016
  Suppressed = false
FEATURE [PartDesign::Body] Body315  label="D4-3"
  AllowCompound = false
  Group = -> [Clone316]
  Origin = -> Origin502
  Placement = pos=(34.8,37,7.3) rot=(0,0,1;0rad)
  Tip = -> Clone316
FEATURE [PartDesign::FeatureBase] Clone317
  BaseFeature = -> Fillet016
  Suppressed = false
FEATURE [PartDesign::Body] Body316  label="D1-4"
  AllowCompound = false
  Group = -> [Clone317]
  Origin = -> Origin503
  Placement = pos=(21.8,7,7.3) rot=(0,0,1;0rad)
  Tip = -> Clone317
FEATURE [PartDesign::FeatureBase] Clone318
  BaseFeature = -> Fillet016
  Suppressed = false
FEATURE [PartDesign::Body] Body317  label="D2-4"
  AllowCompound = false
  Group = -> [Clone318]
  Origin = -> Origin504
  Placement = pos=(21.8,17,7.3) rot=(0,0,1;0rad)
  Tip = -> Clone318
FEATURE [PartDesign::FeatureBase] Clone319
  BaseFeature = -> Fillet016
  Suppressed = false
FEATURE [PartDesign::Body] Body318  label="D3-4"
  AllowCompound = false
  Group = -> [Clone319]
  Origin = -> Origin505
  Placement = pos=(21.8,27,7.3) rot=(0,0,1;0rad)
  Tip = -> Clone319
FEATURE [PartDesign::FeatureBase] Clone320
  BaseFeature = -> Fillet016
  Suppressed = false
FEATURE [PartDesign::Body] Body319  label="D4-4"
  AllowCompound = false
  Group = -> [Clone320]
  Origin = -> Origin506
  Placement = pos=(21.8,37,7.3) rot=(0,0,1;0rad)
  Tip = -> Clone320
FEATURE [PartDesign::FeatureBase] Clone321
  BaseFeature = -> Fillet016
  Suppressed = false
FEATURE [PartDesign::Body] Body320  label="D1-5"
  AllowCompound = false
  Group = -> [Clone321]
  Origin = -> Origin507
  Placement = pos=(8.8,7,7.3) rot=(0,0,1;0rad)
  Tip = -> Clone321
FEATURE [PartDesign::FeatureBase] Clone322
  BaseFeature = -> Fillet016
  Suppressed = false
FEATURE [PartDesign::Body] Body321  label="D2-5"
  AllowCompound = false
  Group = -> [Clone322]
  Origin = -> Origin508
  Placement = pos=(8.8,17,7.3) rot=(0,0,1;0rad)
  Tip = -> Clone322
FEATURE [PartDesign::FeatureBase] Clone323
  BaseFeature = -> Fillet016
  Suppressed = false
FEATURE [PartDesign::Body] Body322  label="D3-5"
  AllowCompound = false
  Group = -> [Clone323]
  Origin = -> Origin509
  Placement = pos=(8.8,27,7.3) rot=(0,0,1;0rad)
  Tip = -> Clone323
FEATURE [PartDesign::FeatureBase] Clone324
  BaseFeature = -> Fillet016
  Suppressed = false
FEATURE [PartDesign::Body] Body323  label="D4-5"
  AllowCompound = false
  Group = -> [Clone324]
  Origin = -> Origin510
  Placement = pos=(8.8,37,7.3) rot=(0,0,1;0rad)
  Tip = -> Clone324
FEATURE [Part::Compound] Compound007  label="DOMES"
  Links = -> [Body274,Body275,Body276,Body277,Body278,Body279,Body280,Body281,Body282,Body283,Body284,Body285,Body286,Body287,Body288,Body289,Body290,Body291,Body292,Body293,Body294,Body295,Body296,Body297,Body298,Body299,Body300,Body301,Body302,Body303,Body304,Body305,Body306,Body307,Body308,Body309,Body310,Body311,Body312,Body313,Body314,Body315,Body316,Body317,Body318,Body319,Body320,Body321,Body322,Body323]
FEATURE [PartDesign::FeatureBase] Clone325
  BaseFeature = -> Fusion038
  Suppressed = false
FEATURE [PartDesign::Body] Body324  label="P3-1"
  AllowCompound = false
  Group = -> [Clone325]
  Origin = -> Origin511
  Placement = pos=(62.5,27,0.5) rot=(0,0,1;0rad)
  Tip = -> Clone325
FEATURE [PartDesign::FeatureBase] Clone326
  BaseFeature = -> Fusion038
  Suppressed = false
FEATURE [PartDesign::Body] Body325  label="P4-1"
  AllowCompound = false
  Group = -> [Clone326]
  Origin = -> Origin512
  Placement = pos=(62.5,37,0.5) rot=(0,0,1;0rad)
  Tip = -> Clone326
FEATURE [PartDesign::FeatureBase] Clone327
  BaseFeature = -> Fusion038
  Suppressed = false
FEATURE [PartDesign::Body] Body326  label="P1-2"
  AllowCompound = false
  Group = -> [Clone327]
  Origin = -> Origin513
  Placement = pos=(47.5,7,0.5) rot=(0,0,1;0rad)
  Tip = -> Clone327
FEATURE [PartDesign::FeatureBase] Clone328
  BaseFeature = -> Fusion038
  Suppressed = false
FEATURE [PartDesign::Body] Body327  label="P2-2"
  AllowCompound = false
  Group = -> [Clone328]
  Origin = -> Origin514
  Placement = pos=(47.5,17,0.5) rot=(0,0,1;0rad)
  Tip = -> Clone328
FEATURE [PartDesign::FeatureBase] Clone329
  BaseFeature = -> Fusion038
  Suppressed = false
FEATURE [PartDesign::Body] Body328  label="P5-1"
  AllowCompound = false
  Group = -> [Clone329]
  Origin = -> Origin515
  Placement = pos=(62.5,50,0.5) rot=(0,0,1;0rad)
  Tip = -> Clone329
FEATURE [PartDesign::FeatureBase] Clone330
  BaseFeature = -> Fusion038
  Suppressed = false
FEATURE [PartDesign::Body] Body329  label="P6-1"
  AllowCompound = false
  Group = -> [Clone330]
  Origin = -> Origin516
  Placement = pos=(62.5,60,0.5) rot=(0,0,1;0rad)
  Tip = -> Clone330
FEATURE [PartDesign::FeatureBase] Clone331
  BaseFeature = -> Fusion038
  Suppressed = false
FEATURE [PartDesign::Body] Body330  label="P7-1"
  AllowCompound = false
  Group = -> [Clone331]
  Origin = -> Origin517
  Placement = pos=(62.5,70,0.5) rot=(0,0,1;0rad)
  Tip = -> Clone331
FEATURE [PartDesign::FeatureBase] Clone332
  BaseFeature = -> Fusion038
  Suppressed = false
FEATURE [PartDesign::Body] Body331  label="P8-1"
  AllowCompound = false
  Group = -> [Clone332]
  Origin = -> Origin518
  Placement = pos=(62.5,80,0.5) rot=(0,0,1;0rad)
  Tip = -> Clone332
FEATURE [PartDesign::FeatureBase] Clone333
  BaseFeature = -> Fusion038
  Suppressed = false
FEATURE [PartDesign::Body] Body332  label="P9-1"
  AllowCompound = false
  Group = -> [Clone333]
  Origin = -> Origin519
  Placement = pos=(62.5,90,0.5) rot=(0,0,1;0rad)
  Tip = -> Clone333
FEATURE [PartDesign::FeatureBase] Clone334
  BaseFeature = -> Fusion038
  Suppressed = false
FEATURE [PartDesign::Body] Body333  label="P1-3"
  AllowCompound = false
  Group = -> [Clone334]
  Origin = -> Origin520
  Placement = pos=(34.5,7,0.5) rot=(0,0,1;0rad)
  Tip = -> Clone334
FEATURE [PartDesign::FeatureBase] Clone335
  BaseFeature = -> Fusion038
  Suppressed = false
FEATURE [PartDesign::Body] Body334  label="P3-2"
  AllowCompound = false
  Group = -> [Clone335]
  Origin = -> Origin521
  Placement = pos=(47.5,27,0.5) rot=(0,0,1;0rad)
  Tip = -> Clone335
FEATURE [PartDesign::FeatureBase] Clone336
  BaseFeature = -> Fusion038
  Suppressed = false
FEATURE [PartDesign::Body] Body335  label="P4-2"
  AllowCompound = false
  Group = -> [Clone336]
  Origin = -> Origin522
  Placement = pos=(47.5,37,0.5) rot=(0,0,1;0rad)
  Tip = -> Clone336
FEATURE [PartDesign::FeatureBase] Clone337
  BaseFeature = -> Fusion038
  Suppressed = false
FEATURE [PartDesign::Body] Body336  label="P2-3"
  AllowCompound = false
  Group = -> [Clone337]
  Origin = -> Origin523
  Placement = pos=(34.5,17,0.5) rot=(0,0,1;0rad)
  Tip = -> Clone337
FEATURE [PartDesign::FeatureBase] Clone338
  BaseFeature = -> Fusion038
  Suppressed = false
FEATURE [PartDesign::Body] Body337  label="P3-3"
  AllowCompound = false
  Group = -> [Clone338]
  Origin = -> Origin524
  Placement = pos=(34.5,27,0.5) rot=(0,0,1;0rad)
  Tip = -> Clone338
FEATURE [PartDesign::FeatureBase] Clone339
  BaseFeature = -> Fusion038
  Suppressed = false
FEATURE [PartDesign::Body] Body338  label="P4-3"
  AllowCompound = false
  Group = -> [Clone339]
  Origin = -> Origin525
  Placement = pos=(34.5,37,0.5) rot=(0,0,1;0rad)
  Tip = -> Clone339
FEATURE [PartDesign::FeatureBase] Clone340
  BaseFeature = -> Fusion038
  Suppressed = false
FEATURE [PartDesign::Body] Body339  label="P1-4"
  AllowCompound = false
  Group = -> [Clone340]
  Origin = -> Origin526
  Placement = pos=(21.5,7,0.5) rot=(0,0,1;0rad)
  Tip = -> Clone340
FEATURE [PartDesign::FeatureBase] Clone341
  BaseFeature = -> Fusion038
  Suppressed = false
FEATURE [PartDesign::Body] Body340  label="P2-4"
  AllowCompound = false
  Group = -> [Clone341]
  Origin = -> Origin527
  Placement = pos=(21.5,17,0.5) rot=(0,0,1;0rad)
  Tip = -> Clone341
FEATURE [PartDesign::FeatureBase] Clone342
  BaseFeature = -> Fusion038
  Suppressed = false
FEATURE [PartDesign::Body] Body341  label="P3-4"
  AllowCompound = false
  Group = -> [Clone342]
  Origin = -> Origin528
  Placement = pos=(21.5,27,0.5) rot=(0,0,1;0rad)
  Tip = -> Clone342
FEATURE [PartDesign::FeatureBase] Clone343
  BaseFeature = -> Fusion038
  Suppressed = false
FEATURE [PartDesign::Body] Body342  label="P4-4"
  AllowCompound = false
  Group = -> [Clone343]
  Origin = -> Origin529
  Placement = pos=(21.5,37,0.5) rot=(0,0,1;0rad)
  Tip = -> Clone343
FEATURE [PartDesign::FeatureBase] Clone344
  BaseFeature = -> Fusion038
  Suppressed = false
FEATURE [PartDesign::Body] Body343  label="P1-5"
  AllowCompound = false
  Group = -> [Clone344]
  Origin = -> Origin530
  Placement = pos=(8.5,7,0.5) rot=(0,0,1;0rad)
  Tip = -> Clone344
FEATURE [PartDesign::FeatureBase] Clone345
  BaseFeature = -> Fusion038
  Suppressed = false
FEATURE [PartDesign::Body] Body344  label="P2-5"
  AllowCompound = false
  Group = -> [Clone345]
  Origin = -> Origin531
  Placement = pos=(8.5,17,0.5) rot=(0,0,1;0rad)
  Tip = -> Clone345
FEATURE [PartDesign::FeatureBase] Clone346
  BaseFeature = -> Fusion038
  Suppressed = false
FEATURE [PartDesign::Body] Body345  label="P3-5"
  AllowCompound = false
  Group = -> [Clone346]
  Origin = -> Origin532
  Placement = pos=(8.5,27,0.5) rot=(0,0,1;0rad)
  Tip = -> Clone346
FEATURE [PartDesign::FeatureBase] Clone347
  BaseFeature = -> Fusion038
  Suppressed = false
FEATURE [PartDesign::Body] Body346  label="P4-5"
  AllowCompound = false
  Group = -> [Clone347]
  Origin = -> Origin533
  Placement = pos=(8.5,37,0.5) rot=(0,0,1;0rad)
  Tip = -> Clone347
FEATURE [PartDesign::FeatureBase] Clone348
  BaseFeature = -> Fusion038
  Suppressed = false
FEATURE [PartDesign::Body] Body347  label="P5-2"
  AllowCompound = false
  Group = -> [Clone348]
  Origin = -> Origin534
  Placement = pos=(51.5,50,0.5) rot=(0,0,1;0rad)
  Tip = -> Clone348
FEATURE [PartDesign::FeatureBase] Clone349
  BaseFeature = -> Fusion038
  Suppressed = false
FEATURE [PartDesign::Body] Body348  label="P6-2"
  AllowCompound = false
  Group = -> [Clone349]
  Origin = -> Origin535
  Placement = pos=(51.5,60,0.5) rot=(0,0,1;0rad)
  Tip = -> Clone349
FEATURE [PartDesign::FeatureBase] Clone350
  BaseFeature = -> Fusion038
  Suppressed = false
FEATURE [PartDesign::Body] Body349  label="P7-2"
  AllowCompound = false
  Group = -> [Clone350]
  Origin = -> Origin536
  Placement = pos=(51.5,70,0.5) rot=(0,0,1;0rad)
  Tip = -> Clone350
FEATURE [PartDesign::FeatureBase] Clone351
  BaseFeature = -> Fusion038
  Suppressed = false
FEATURE [PartDesign::Body] Body350  label="P8-2"
  AllowCompound = false
  Group = -> [Clone351]
  Origin = -> Origin537
  Placement = pos=(51.5,80,0.5) rot=(0,0,1;0rad)
  Tip = -> Clone351
FEATURE [PartDesign::FeatureBase] Clone352
  BaseFeature = -> Fusion038
  Suppressed = false
FEATURE [PartDesign::Body] Body351  label="P9-2"
  AllowCompound = false
  Group = -> [Clone352]
  Origin = -> Origin538
  Placement = pos=(51.5,90,0.5) rot=(0,0,1;0rad)
  Tip = -> Clone352
FEATURE [PartDesign::FeatureBase] Clone353
  BaseFeature = -> Fusion038
  Suppressed = false
FEATURE [PartDesign::Body] Body352  label="P5-3"
  AllowCompound = false
  Group = -> [Clone353]
  Origin = -> Origin539
  Placement = pos=(40.5,50,0.5) rot=(0,0,1;0rad)
  Tip = -> Clone353
FEATURE [PartDesign::FeatureBase] Clone354
  BaseFeature = -> Fusion038
  Suppressed = false
FEATURE [PartDesign::Body] Body353  label="P6-3"
  AllowCompound = false
  Group = -> [Clone354]
  Origin = -> Origin540
  Placement = pos=(40.5,60,0.5) rot=(0,0,1;0rad)
  Tip = -> Clone354
FEATURE [PartDesign::FeatureBase] Clone355
  BaseFeature = -> Fusion038
  Suppressed = false
FEATURE [PartDesign::Body] Body354  label="P7-3"
  AllowCompound = false
  Group = -> [Clone355]
  Origin = -> Origin541
  Placement = pos=(40.5,70,0.5) rot=(0,0,1;0rad)
  Tip = -> Clone355
FEATURE [PartDesign::FeatureBase] Clone356
  BaseFeature = -> Fusion038
  Suppressed = false
FEATURE [PartDesign::Body] Body355  label="P8-3"
  AllowCompound = false
  Group = -> [Clone356]
  Origin = -> Origin542
  Placement = pos=(40.5,80,0.5) rot=(0,0,1;0rad)
  Tip = -> Clone356
FEATURE [PartDesign::FeatureBase] Clone357
  BaseFeature = -> Fusion038
  Suppressed = false
FEATURE [PartDesign::Body] Body356  label="P9-3"
  AllowCompound = false
  Group = -> [Clone357]
  Origin = -> Origin543
  Placement = pos=(40.5,90,0.5) rot=(0,0,1;0rad)
  Tip = -> Clone357
FEATURE [PartDesign::FeatureBase] Clone358
  BaseFeature = -> Fusion038
  Suppressed = false
FEATURE [PartDesign::Body] Body357  label="P5-4"
  AllowCompound = false
  Group = -> [Clone358]
  Origin = -> Origin544
  Placement = pos=(29.5,50,0.5) rot=(0,0,1;0rad)
  Tip = -> Clone358
FEATURE [PartDesign::FeatureBase] Clone359
  BaseFeature = -> Fusion038
  Suppressed = false
FEATURE [PartDesign::Body] Body358  label="P6-4"
  AllowCompound = false
  Group = -> [Clone359]
  Origin = -> Origin545
  Placement = pos=(29.5,60,0.5) rot=(0,0,1;0rad)
  Tip = -> Clone359
FEATURE [PartDesign::FeatureBase] Clone360
  BaseFeature = -> Fusion038
  Suppressed = false
FEATURE [PartDesign::Body] Body359  label="P7-4"
  AllowCompound = false
  Group = -> [Clone360]
  Origin = -> Origin546
  Placement = pos=(29.5,70,0.5) rot=(0,0,1;0rad)
  Tip = -> Clone360
FEATURE [PartDesign::FeatureBase] Clone361
  BaseFeature = -> Fusion038
  Suppressed = false
FEATURE [PartDesign::Body] Body360  label="P8-4"
  AllowCompound = false
  Group = -> [Clone361]
  Origin = -> Origin547
  Placement = pos=(29.5,80,0.5) rot=(0,0,1;0rad)
  Tip = -> Clone361
FEATURE [PartDesign::FeatureBase] Clone362
  BaseFeature = -> Fusion038
  Suppressed = false
FEATURE [PartDesign::Body] Body361  label="P9-4"
  AllowCompound = false
  Group = -> [Clone362]
  Origin = -> Origin548
  Placement = pos=(29.5,90,0.5) rot=(0,0,1;0rad)
  Tip = -> Clone362
FEATURE [PartDesign::FeatureBase] Clone363
  BaseFeature = -> Fusion038
  Suppressed = false
FEATURE [PartDesign::Body] Body362  label="P5-5"
  AllowCompound = false
  Group = -> [Clone363]
  Origin = -> Origin549
  Placement = pos=(18.5,50,0.5) rot=(0,0,1;0rad)
  Tip = -> Clone363
FEATURE [PartDesign::FeatureBase] Clone364
  BaseFeature = -> Fusion038
  Suppressed = false
FEATURE [PartDesign::Body] Body363  label="P6-5"
  AllowCompound = false
  Group = -> [Clone364]
  Origin = -> Origin550
  Placement = pos=(18.5,60,0.5) rot=(0,0,1;0rad)
  Tip = -> Clone364
FEATURE [PartDesign::FeatureBase] Clone365
  BaseFeature = -> Fusion038
  Suppressed = false
FEATURE [PartDesign::Body] Body364  label="P7-5"
  AllowCompound = false
  Group = -> [Clone365]
  Origin = -> Origin551
  Placement = pos=(18.5,70,0.5) rot=(0,0,1;0rad)
  Tip = -> Clone365
FEATURE [PartDesign::FeatureBase] Clone366
  BaseFeature = -> Fusion038
  Suppressed = false
FEATURE [PartDesign::Body] Body365  label="P8-5"
  AllowCompound = false
  Group = -> [Clone366]
  Origin = -> Origin552
  Placement = pos=(18.5,80,0.5) rot=(0,0,1;0rad)
  Tip = -> Clone366
FEATURE [PartDesign::FeatureBase] Clone367
  BaseFeature = -> Fusion038
  Suppressed = false
FEATURE [PartDesign::Body] Body366  label="P9-5"
  AllowCompound = false
  Group = -> [Clone367]
  Origin = -> Origin553
  Placement = pos=(18.5,90,0.5) rot=(0,0,1;0rad)
  Tip = -> Clone367
FEATURE [PartDesign::FeatureBase] Clone368
  BaseFeature = -> Fusion038
  Suppressed = false
FEATURE [PartDesign::Body] Body367  label="P5-6"
  AllowCompound = false
  Group = -> [Clone368]
  Origin = -> Origin554
  Placement = pos=(7.5,50,0.5) rot=(0,0,1;0rad)
  Tip = -> Clone368
FEATURE [PartDesign::FeatureBase] Clone369
  BaseFeature = -> Fusion038
  Suppressed = false
FEATURE [PartDesign::Body] Body368  label="P6-6"
  AllowCompound = false
  Group = -> [Clone369]
  Origin = -> Origin555
  Placement = pos=(7.5,60,0.5) rot=(0,0,1;0rad)
  Tip = -> Clone369
FEATURE [PartDesign::FeatureBase] Clone370
  BaseFeature = -> Fusion038
  Suppressed = false
FEATURE [PartDesign::Body] Body369  label="P7-6"
  AllowCompound = false
  Group = -> [Clone370]
  Origin = -> Origin556
  Placement = pos=(7.5,70,0.5) rot=(0,0,1;0rad)
  Tip = -> Clone370
FEATURE [PartDesign::FeatureBase] Clone371
  BaseFeature = -> Fusion038
  Suppressed = false
FEATURE [PartDesign::Body] Body370  label="P8-6"
  AllowCompound = false
  Group = -> [Clone371]
  Origin = -> Origin557
  Placement = pos=(7.5,80,0.5) rot=(0,0,1;0rad)
  Tip = -> Clone371
FEATURE [PartDesign::FeatureBase] Clone372
  BaseFeature = -> Fusion038
  Suppressed = false
FEATURE [PartDesign::Body] Body371  label="P9-6"
  AllowCompound = false
  Group = -> [Clone372]
  Origin = -> Origin558
  Placement = pos=(7.5,90,0.5) rot=(0,0,1;0rad)
  Tip = -> Clone372
FEATURE [Part::MultiFuse] Fusion039
  Shapes = -> [Body371,Body324,Body325,Body326,Body327,Body328,Body329,Body330,Body331,Body332,Body333,Body334,Body335,Body336,Body337,Body338,Body339,Body340,Body341,Body342,Body343,Body344,Body345,Body346,Body347,Body348,Body349,Body350,Body351,Body352,Body353,Body354,Body355,Body356,Body357,Body358,Body359,Body360,Body361,Body362,Body363,Body364,Body365,Body366,Body367,Body368,Body369,Body370,Body273,Body272]
FEATURE [Part::Cut] Cut026  label="PUSHES"
  Base = -> Fusion039
  Refine = true
  Tool = -> Box088
FEATURE [Part::Cylinder] Cylinder029
  Angle = 360
  AttacherType = Attacher::AttachEngine3D
  FirstAngle = 0
  Height = 4.2
  Placement = pos=(14.95,2.5,4.8) rot=(0,0,1;0rad)
  Radius = 1.6
  SecondAngle = 0
FEATURE [Part::Cylinder] Cylinder030
  Angle = 360
  AttacherType = Attacher::AttachEngine3D
  FirstAngle = 0
  Height = 4.2
  Placement = pos=(55,2.5,4.8) rot=(0,0,1;0rad)
  Radius = 1.6
  SecondAngle = 0
FEATURE [Part::Cylinder] Cylinder031
  Angle = 360
  AttacherType = Attacher::AttachEngine3D
  FirstAngle = 0
  Height = 4.2
  Placement = pos=(67,43.5,4.8) rot=(0,0,1;0rad)
  Radius = 1.6
  SecondAngle = 0
FEATURE [Part::Cylinder] Cylinder032
  Angle = 360
  AttacherType = Attacher::AttachEngine3D
  FirstAngle = 0
  Height = 4.2
  Placement = pos=(3,43.5,4.8) rot=(0,0,1;0rad)
  Radius = 1.6
  SecondAngle = 0
FEATURE [Part::Box] Box089  label="Cube088"
  AttacherType = Attacher::AttachEngine3D
  Height = 2.3
  Length = 8
  Placement = pos=(-4,-3,0) rot=(0,0,1;0rad)
  Width = 6
FEATURE [Part::Box] Box090  label="Cube089"
  AttacherType = Attacher::AttachEngine3D
  Height = 3
  Length = 8
  Placement = pos=(-4,-6,-0.6) rot=(-1,0,0;0.488692rad)
  Width = 6
FEATURE [Part::Cut] Cut028
  Base = -> Box089
  Tool = -> Box090
FEATURE [Part::Fillet] Fillet017  label="ENTER_KEY"
  Base = -> Cut028
  EdgeLinks = -> Cut028 [Edge1,Edge3,Edge4,Edge5,Edge6,Edge8,Edge11,Edge12,Edge13,Edge14,Edge15]
  Edges = 11 edges: [Edge1 r=0.3,Edge3 r=0.3,Edge4 r=0.3,Edge5 r=0.3,Edge6 r=0.3,Edge8 r=0.3,Edge11 r=0.3,Edge12 r=0.3,Edge13 r=0.3,Edge14 r=1,Edge15 r=0.3]
  Placement = pos=(57.5,50,1.16) rot=(0,0,1;0rad)
FEATURE [Part::Box] Box091  label="ENTER_CUT"
  AttacherType = Attacher::AttachEngine3D
  Height = 9
  Length = 4.5
  Placement = pos=(55,46.5,2) rot=(0,0,1;0rad)
  Width = 7
FEATURE [Part::Box] Box092  label="Cube090"
  AttacherType = Attacher::AttachEngine3D
  Height = 8
  Length = 10
  Placement = pos=(-4,123.8,2.7) rot=(0,0,1;0rad)
  Width = 13.6
FEATURE [Part::Box] Box093  label="Cube091"
  AttacherType = Attacher::AttachEngine3D
  Height = 8
  Length = 10
  Placement = pos=(-7.5,123.8,8.7) rot=(0,1,0;0.785398rad)
  Width = 13.6
FEATURE [Part::MultiFuse] Fusion041
  Shapes = -> [Box092,Box093]
FEATURE [Part::Box] Box094  label="Cube092"
  AttacherType = Attacher::AttachEngine3D
  Height = 4
  Length = 3
  Placement = pos=(-2,139.75,5.5) rot=(0,0,1;0rad)
  Width = 4.4
FEATURE [Part::Chamfer] Chamfer008
  Base = -> Box094
  EdgeLinks = -> Box094 [Edge5,Edge6,Edge7,Edge8]
  Edges = 4 edges r=1: [Edge5,Edge6,Edge7,Edge8]
FEATURE [Part::Box] Box095  label="Cube093"
  AttacherType = Attacher::AttachEngine3D
  Height = 3
  Length = 3
  Placement = pos=(-2,140.6,6.4) rot=(0,0,1;0rad)
  Width = 2.7
FEATURE [Part::Box] Box096  label="Cube094"
  AttacherType = Attacher::AttachEngine3D
  Height = 6
  Length = 3
  Placement = pos=(-4,139,5) rot=(0,0,1;0rad)
  Width = 5.7
FEATURE [Part::MultiFuse] Fusion042
  Shapes = -> [Box095,Box096]
FEATURE [Part::Chamfer] Chamfer009
  Base = -> Fusion042
  EdgeLinks = -> Fusion042 [Edge4,Edge7,Edge11,Edge16]
  Edges = 4 edges r=1: [Edge4,Edge7,Edge11,Edge16]
  Placement = pos=(0.5,0,0) rot=(0,0,1;0rad)
FEATURE [Part::Box] Box097  label="Cube095"
  AttacherType = Attacher::AttachEngine3D
  Height = 0.8
  Length = 2.5
  Placement = pos=(-1.25,125.17,3.78) rot=(0,0,1;0rad)
  Width = 0.8
FEATURE [Part::Box] Box098  label="Cube096"
  AttacherType = Attacher::AttachEngine3D
  Height = 2.8
  Length = 1
  Placement = pos=(-1.25,124.17,2.78) rot=(0,0,1;0rad)
  Width = 2.8
FEATURE [Part::MultiFuse] Fusion043
  Shapes = -> [Box097,Box098]
FEATURE [Part::Chamfer] Chamfer010  label="PIN"
  Base = -> Fusion043
  EdgeLinks = -> Fusion043 [Edge17,Edge18,Edge19,Edge20]
  Edges = 4 edges r=0.5: [Edge17,Edge18,Edge19,Edge20]
FEATURE [PartDesign::FeatureBase] Clone373
  BaseFeature = -> Chamfer010
  Suppressed = false
FEATURE [PartDesign::Body] Body372
  AllowCompound = false
  Group = -> [Clone373]
  Origin = -> Origin714
  Placement = pos=(0,2.54,0) rot=(0,0,1;0rad)
  Tip = -> Clone373
FEATURE [PartDesign::FeatureBase] Clone374
  BaseFeature = -> Chamfer010
  Suppressed = false
FEATURE [PartDesign::Body] Body373
  AllowCompound = false
  Group = -> [Clone374]
  Origin = -> Origin715
  Tip = -> Clone374
FEATURE [PartDesign::FeatureBase] Clone375
  BaseFeature = -> Chamfer010
  Suppressed = false
FEATURE [PartDesign::Body] Body374
  AllowCompound = false
  Group = -> [Clone375]
  Origin = -> Origin716
  Placement = pos=(0,5.08,0) rot=(0,0,1;0rad)
  Tip = -> Clone375
FEATURE [PartDesign::FeatureBase] Clone376
  BaseFeature = -> Chamfer010
  Suppressed = false
FEATURE [PartDesign::Body] Body375
  AllowCompound = false
  Group = -> [Clone376]
  Origin = -> Origin717
  Placement = pos=(0,7.62,0) rot=(0,0,1;0rad)
  Tip = -> Clone376
FEATURE [PartDesign::FeatureBase] Clone377
  BaseFeature = -> Chamfer010
  Suppressed = false
FEATURE [PartDesign::Body] Body376
  AllowCompound = false
  Group = -> [Clone377]
  Origin = -> Origin718
  Placement = pos=(0,10.16,0) rot=(0,0,1;0rad)
  Tip = -> Clone377
FEATURE [PartDesign::FeatureBase] Clone378
  BaseFeature = -> Chamfer010
  Suppressed = false
FEATURE [PartDesign::Body] Body377
  AllowCompound = false
  Group = -> [Clone378]
  Origin = -> Origin719
  Placement = pos=(0,0,2.54) rot=(0,0,1;0rad)
  Tip = -> Clone378
FEATURE [PartDesign::FeatureBase] Clone379
  BaseFeature = -> Chamfer010
  Suppressed = false
FEATURE [PartDesign::Body] Body378
  AllowCompound = false
  Group = -> [Clone379]
  Origin = -> Origin720
  Placement = pos=(0,2.54,2.54) rot=(0,0,1;0rad)
  Tip = -> Clone379
FEATURE [PartDesign::FeatureBase] Clone380
  BaseFeature = -> Chamfer010
  Suppressed = false
FEATURE [PartDesign::Body] Body379
  AllowCompound = false
  Group = -> [Clone380]
  Origin = -> Origin721
  Placement = pos=(0,5.08,2.54) rot=(0,0,1;0rad)
  Tip = -> Clone380
FEATURE [PartDesign::FeatureBase] Clone381
  BaseFeature = -> Chamfer010
  Suppressed = false
FEATURE [PartDesign::Body] Body380
  AllowCompound = false
  Group = -> [Clone381]
  Origin = -> Origin722
  Placement = pos=(0,7.62,2.54) rot=(0,0,1;0rad)
  Tip = -> Clone381
FEATURE [PartDesign::FeatureBase] Clone382
  BaseFeature = -> Chamfer010
  Suppressed = false
FEATURE [PartDesign::Body] Body381
  AllowCompound = false
  Group = -> [Clone382]
  Origin = -> Origin723
  Placement = pos=(0,10.16,2.54) rot=(0,0,1;0rad)
  Tip = -> Clone382
FEATURE [Part::MultiFuse] Fusion044
  Refine = true
  Shapes = -> [Body372,Body373,Body374,Body375,Body376,Body377,Body378,Body379,Body380,Body381]
FEATURE [Part::Box] Box099  label="Cube097"
  AttacherType = Attacher::AttachEngine3D
  Height = 3
  Length = 3
  Placement = pos=(68,140.6,6.4) rot=(0,0,1;0rad)
  Width = 2.7
FEATURE [Part::Box] Box100  label="Cube098"
  AttacherType = Attacher::AttachEngine3D
  Height = 6
  Length = 3
  Placement = pos=(71,139,5) rot=(0,0,1;0rad)
  Width = 5.7
FEATURE [Part::MultiFuse] Fusion045
  Refine = true
  Shapes = -> [Box099,Box100]
FEATURE [Part::Chamfer] Chamfer011
  Base = -> Fusion045
  EdgeLinks = -> Fusion045 [Edge6,Edge9,Edge11,Edge12]
  Edges = 4 edges r=1: [Edge6,Edge9,Edge11,Edge12]
  Placement = pos=(-0.3,0,0) rot=(0,0,1;0rad)
FEATURE [Part::Box] Box101  label="Cube099"
  AttacherType = Attacher::AttachEngine3D
  Height = 3
  Length = 12
  Placement = pos=(61,125.685,6.2) rot=(0,0,1;0rad)
  Width = 11.13
FEATURE [Part::Box] Box102  label="Cube100"
  AttacherType = Attacher::AttachEngine3D
  Height = 7
  Length = 3
  Placement = pos=(71,123,4) rot=(0,0,1;0rad)
  Width = 16.7
FEATURE [Part::MultiFuse] Fusion046
  Shapes = -> [Box101,Box102]
FEATURE [Part::Chamfer] Chamfer012
  Base = -> Fusion046
  EdgeLinks = -> Fusion046 [Edge6,Edge9,Edge11,Edge12]
  Edges = 4 edges r=1: [Edge6,Edge9,Edge11,Edge12]
  Placement = pos=(-0.5,0,0) rot=(0,0,1;0rad)
FEATURE [Part::Cylinder] Cylinder033
  Angle = 360
  AttacherType = Attacher::AttachEngine3D
  FirstAngle = 0
  Height = 10
  Placement = pos=(64.5,107.5,5.45) rot=(0,1,0;1.5708rad)
  Radius = 2.7
  SecondAngle = 0
FEATURE [Part::Box] Box103  label="Cube101"
  AttacherType = Attacher::AttachEngine3D
  Height = 10
  Length = 10
  Placement = pos=(65.5,104.8,5.45) rot=(0,0,1;0rad)
  Width = 5.4
FEATURE [Part::MultiFuse] Fusion047
  Refine = true
  Shapes = -> [Cylinder033,Box103]
FEATURE [Part::Box] Box104  label="LCD001"
  AttacherType = Attacher::AttachEngine3D
  Height = 0.1
  Length = 65
  Placement = pos=(2,104,2) rot=(0,0,1;0rad)
  Width = 38
FEATURE [Part::Feature] Part__Feature7310  label="CUI_DEVICES_CMS-15113-078L100"
  shape: bbox 11 x 3.001 x 59.05 mm, 240 faces (baked)
FEATURE [Part::Box] Box105  label="Cube102"
  AttacherType = Attacher::AttachEngine3D
  Height = 47
  Length = 13
  Placement = pos=(-1,-12.4,-0.4) rot=(0,0,1;0rad)
  Width = 10
FEATURE [Part::Cut] Cut029  label="speaker"
  Base = -> Part__Feature7310
  Placement = pos=(53,123.5,9) rot=(-0.57735,0.57735,0.57735;4.18879rad)
  Tool = -> Box105
FEATURE [Part::Box] Box106  label="Cube103"
  AttacherType = Attacher::AttachEngine3D
  Height = 8.5
  Length = 3.6
  Placement = pos=(66,123.5,5.6) rot=(0,0,1;0rad)
  Width = 14.5
FEATURE [Part::Box] Box107  label="Cube104"
  AttacherType = Attacher::AttachEngine3D
  Height = 8.5
  Length = 3.35
  Placement = pos=(66,139.7,6.3) rot=(0,0,1;0rad)
  Width = 4.5
FEATURE [Part::Box] Box108  label="Cube105"
  AttacherType = Attacher::AttachEngine3D
  Height = 8.5
  Length = 3.35
  Placement = pos=(0.7,139.7,6.3) rot=(0,0,1;0rad)
  Width = 4.5
FEATURE [Part::Box] Box109  label="Cube106"
  AttacherType = Attacher::AttachEngine3D
  Height = 8.3
  Length = 3.35
  Placement = pos=(0.7,123.7,2.6) rot=(0,0,1;0rad)
  Width = 13.8
FEATURE [Part::Feature] path3
  shape: bbox 3.072 x 2.854 x 2e-07 mm, 1 faces, 0 solids (baked)
FEATURE [Part::Feature] path1335  label="path1336"
  shape: bbox 2.487 x 0.8031 x 2e-07 mm, 1 faces, 0 solids (baked)
FEATURE [Part::Feature] path1336  label="path1337"
  shape: bbox 2.492 x 2.492 x 2e-07 mm, 1 faces, 0 solids (baked)
FEATURE [Part::Feature] path1337  label="path1338"
  shape: bbox 0.4196 x 0.4217 x 2e-07 mm, 1 faces, 0 solids (baked)
FEATURE [Part::Feature] path1338  label="path1339"
  shape: bbox 2.751 x 2.359 x 2e-07 mm, 1 faces, 0 solids (baked)
FEATURE [Part::Feature] path1339  label="path1340"
  shape: bbox 2.738 x 2.221 x 2e-07 mm, 1 faces, 0 solids (baked)
FEATURE [Part::Feature] path1340  label="path1341"
  shape: bbox 1.179 x 0.2951 x 2e-07 mm, 1 faces, 0 solids (baked)
FEATURE [Part::Feature] path1341  label="path1342"
  shape: bbox 1.595 x 1.313 x 2e-07 mm, 1 faces, 0 solids (baked)
FEATURE [Part::Feature] path1342  label="path1343"
  shape: bbox 1.137 x 1.124 x 2e-07 mm, 1 faces, 0 solids (baked)
FEATURE [Part::Feature] path1343  label="path1344"
  shape: bbox 2.488 x 0.8031 x 2e-07 mm, 1 faces, 0 solids (baked)
FEATURE [Part::Feature] path1344  label="path1345"
  shape: bbox 2.358 x 0.3933 x 2e-07 mm, 1 faces, 0 solids (baked)
FEATURE [Part::Feature] path1345  label="path1346"
  shape: bbox 0.4201 x 0.4196 x 2e-07 mm, 1 faces, 0 solids (baked)
FEATURE [Part::Feature] path1346  label="path1347"
  shape: bbox 2.358 x 0.8842 x 2e-07 mm, 1 faces, 0 solids (baked)
FEATURE [Part::Feature] path1347  label="path1348"
  shape: bbox 0.3933 x 0.2946 x 2e-07 mm, 1 faces, 0 solids (baked)
FEATURE [Part::Feature] path1348  label="path1349"
  shape: bbox 2.487 x 0.803 x 2e-07 mm, 1 faces, 0 solids (baked)
FEATURE [Part::Feature] path1349  label="path1350"
  shape: bbox 0.4196 x 0.4196 x 2e-07 mm, 1 faces, 0 solids (baked)
FEATURE [Part::Feature] path1350  label="path1351"
  shape: bbox 0.7922 x 1.309 x 2e-07 mm, 1 faces, 0 solids (baked)
FEATURE [Part::Feature] path1351  label="path1352"
  shape: bbox 0.9436 x 1.3 x 2e-07 mm, 1 faces, 0 solids (baked)
FEATURE [Part::Feature] path1352  label="path1353"
  shape: bbox 0.8129 x 1.289 x 2e-07 mm, 1 faces, 0 solids (baked)
FEATURE [Part::Feature] path1353  label="path1354"
  shape: bbox 0.7922 x 1.3 x 2e-07 mm, 1 faces, 0 solids (baked)
FEATURE [Part::Feature] path1354  label="path1355"
  shape: bbox 0.9787 x 1.289 x 2e-07 mm, 1 faces, 0 solids (baked)
FEATURE [Part::Feature] path1355  label="path1356"
  shape: bbox 0.7726 x 1.289 x 2e-07 mm, 1 faces, 0 solids (baked)
FEATURE [Part::Feature] path1356  label="path1357"
  shape: bbox 0.8537 x 1.289 x 2e-07 mm, 1 faces, 0 solids (baked)
FEATURE [Part::Feature] path1357  label="path1358"
  shape: bbox 0.7922 x 1.3 x 2e-07 mm, 1 faces, 0 solids (baked)
FEATURE [Part::Feature] path1358  label="path1359"
  shape: bbox 0.7922 x 1.3 x 2e-07 mm, 1 faces, 0 solids (baked)
FEATURE [Part::Feature] path1359  label="path1360"
  shape: bbox 0.7023 x 1.289 x 2e-07 mm, 1 faces, 0 solids (baked)
FEATURE [Part::Feature] path1360  label="path1361"
  shape: bbox 0.7922 x 1.3 x 2e-07 mm, 1 faces, 0 solids (baked)
FEATURE [Part::Feature] path1361  label="path1362"
  shape: bbox 0.7922 x 1.3 x 2e-07 mm, 1 faces, 0 solids (baked)
FEATURE [Part::Feature] path1362  label="path1363"
  shape: bbox 0.8129 x 1.289 x 2e-07 mm, 1 faces, 0 solids (baked)
FEATURE [Part::Feature] path1363  label="path1364"
  shape: bbox 0.7622 x 1.289 x 2e-07 mm, 1 faces, 0 solids (baked)
FEATURE [Part::Feature] path1364  label="path1365"
  shape: bbox 0.1871 x 1.289 x 2e-07 mm, 1 faces, 0 solids (baked)
FEATURE [Part::Feature] path1365  label="path1366"
  shape: bbox 0.7917 x 1.3 x 2e-07 mm, 1 faces, 0 solids (baked)
FEATURE [Part::Feature] path1366  label="path1367"
  shape: bbox 0.7922 x 1.29 x 2e-07 mm, 1 faces, 0 solids (baked)
FEATURE [Part::Feature] path1367  label="path1368"
  shape: bbox 0.7726 x 1.29 x 2e-07 mm, 1 faces, 0 solids (baked)
FEATURE [Part::Feature] path1368  label="path1369"
  shape: bbox 0.7018 x 1.29 x 2e-07 mm, 1 faces, 0 solids (baked)
FEATURE [Part::Feature] path1369  label="path1370"
  shape: bbox 0.7726 x 1.29 x 2e-07 mm, 1 faces, 0 solids (baked)
FEATURE [Part::Feature] path1370  label="path1371"
  shape: bbox 0.8537 x 1.29 x 2e-07 mm, 1 faces, 0 solids (baked)
FEATURE [Part::Feature] path1371  label="path1372"
  shape: bbox 0.7726 x 1.29 x 2e-07 mm, 1 faces, 0 solids (baked)
FEATURE [Part::Feature] path1372  label="path1373"
  shape: bbox 0.7917 x 1.29 x 2e-07 mm, 1 faces, 0 solids (baked)
FEATURE [Part::Feature] path1373  label="path1374"
  shape: bbox 0.7922 x 1.3 x 2e-07 mm, 1 faces, 0 solids (baked)
FEATURE [Part::Feature] path1374  label="path1375"
  shape: bbox 0.8377 x 1.295 x 2e-07 mm, 1 faces, 0 solids (baked)
FEATURE [Part::Feature] path1375  label="path1376"
  shape: bbox 0.4196 x 0.9684 x 2e-07 mm, 1 faces, 0 solids (baked)
FEATURE [Part::Feature] path1376  label="path1377"
  shape: bbox 0.4196 x 0.9684 x 2e-07 mm, 1 faces, 0 solids (baked)
FEATURE [Part::Feature] path1377  label="path1378"
  shape: bbox 0.4196 x 0.9684 x 2e-07 mm, 1 faces, 0 solids (baked)
FEATURE [Part::Feature] path1378  label="path1379"
  shape: bbox 0.4196 x 0.9684 x 2e-07 mm, 1 faces, 0 solids (baked)
FEATURE [Part::Feature] path1379  label="path1380"
  shape: bbox 0.4181 x 0.9581 x 2e-07 mm, 1 faces, 0 solids (baked)
FEATURE [Part::Feature] path1380  label="path1381"
  shape: bbox 0.3881 x 0.3514 x 2e-07 mm, 1 faces, 0 solids (baked)
FEATURE [Part::Feature] path1381  label="path1382"
  shape: bbox 0.353 x 0.6051 x 2e-07 mm, 1 faces, 0 solids (baked)
FEATURE [Part::Feature] path1382  label="path1383"
  shape: bbox 0.4196 x 0.4589 x 2e-07 mm, 1 faces, 0 solids (baked)
FEATURE [Part::Feature] path1383  label="path1384"
  shape: bbox 1.732 x 2.6 x 2e-07 mm, 1 faces, 0 solids (baked)
FEATURE [Part::Feature] path1384  label="path1385"
  shape: bbox 1.824 x 2.6 x 2e-07 mm, 1 faces, 0 solids (baked)
FEATURE [Part::Feature] path1385  label="path1386"
  shape: bbox 0.9607 x 1.547 x 2e-07 mm, 1 faces, 0 solids (baked)
FEATURE [Part::Feature] path1386  label="path1387"
  shape: bbox 1.513 x 2.579 x 2e-07 mm, 1 faces, 0 solids (baked)
FEATURE [Part::Feature] path1387  label="path1388"
  shape: bbox 1.732 x 2.6 x 2e-07 mm, 1 faces, 0 solids (baked)
FEATURE [Part::Feature] path1388  label="path1389"
  shape: bbox 1.732 x 2.6 x 2e-07 mm, 1 faces, 0 solids (baked)
FEATURE [Part::Feature] path1389  label="path1390"
  shape: bbox 3.618 x 2.545 x 2e-07 mm, 1 faces, 0 solids (baked)
FEATURE [Part::Feature] path1390  label="path1391"
  shape: bbox 0.6315 x 1.641 x 2e-07 mm, 1 faces, 0 solids (baked)
FEATURE [Part::Feature] path1391  label="path1392"
  shape: bbox 1.313 x 1.594 x 2e-07 mm, 1 faces, 0 solids (baked)
FEATURE [Part::Feature] path1392  label="path1393"
  shape: bbox 0.6315 x 1.64 x 2e-07 mm, 1 faces, 0 solids (baked)
FEATURE [Part::Feature] path1393  label="path1394"
  shape: bbox 1.313 x 1.595 x 2e-07 mm, 1 faces, 0 solids (baked)
FEATURE [Part::Feature] path1394  label="path1395"
  shape: bbox 2.002 x 2.001 x 2e-07 mm, 1 faces, 0 solids (baked)
FEATURE [Part::Feature] path1395  label="path1396"
  shape: bbox 1.501 x 1.501 x 2e-07 mm, 1 faces, 0 solids (baked)
FEATURE [Part::Feature] path1396  label="path1397"
  shape: bbox 0.6346 x 0.6346 x 2e-07 mm, 1 faces, 0 solids (baked)
FEATURE [Part::Feature] path1397  label="path1398"
  shape: bbox 0.6739 x 0.6755 x 2e-07 mm, 1 faces, 0 solids (baked)
FEATURE [Part::Feature] path1398  label="path1399"
  shape: bbox 2.531 x 1.614 x 2e-07 mm, 1 faces, 0 solids (baked)
FEATURE [Part::Feature] path1399  label="path1400"
  shape: bbox 0.7023 x 1.289 x 2e-07 mm, 1 faces, 0 solids (baked)
FEATURE [Part::Feature] path1400  label="path1401"
  shape: bbox 0.8134 x 1.289 x 2e-07 mm, 1 faces, 0 solids (baked)
FEATURE [Part::Feature] path1401  label="path1402"
  shape: bbox 1.012 x 1.011 x 2e-07 mm, 1 faces, 0 solids (baked)
FEATURE [Part::Feature] path1402  label="path1403"
  shape: bbox 1.027 x 1.025 x 2e-07 mm, 1 faces, 0 solids (baked)
FEATURE [Part::Feature] path1403  label="path1404"
  shape: bbox 1.732 x 2.635 x 2e-07 mm, 1 faces, 0 solids (baked)
FEATURE [Part::Feature] path1404  label="path1405"
  shape: bbox 1.732 x 2.6 x 2e-07 mm, 1 faces, 0 solids (baked)
FEATURE [Part::Feature] path1405  label="path1406"
  shape: bbox 1.732 x 2.6 x 2e-07 mm, 1 faces, 0 solids (baked)
FEATURE [Part::Feature] path1406  label="path1407"
  shape: bbox 1.732 x 2.635 x 2e-07 mm, 1 faces, 0 solids (baked)
FEATURE [Part::Feature] path1407  label="path1408"
  shape: bbox 2.049 x 2.6 x 2e-07 mm, 1 faces, 0 solids (baked)
FEATURE [Part::Feature] path1408  label="path1409"
  shape: bbox 0.5504 x 2.579 x 2e-07 mm, 1 faces, 0 solids (baked)
FEATURE [Part::Feature] path1409  label="path1410"
  shape: bbox 1.802 x 2.579 x 2e-07 mm, 1 faces, 0 solids (baked)
FEATURE [Part::Feature] path1410  label="path1411"
  shape: bbox 1.856 x 2.579 x 2e-07 mm, 1 faces, 0 solids (baked)
FEATURE [Part::Feature] path1411  label="path1412"
  shape: bbox 1.802 x 2.579 x 2e-07 mm, 1 faces, 0 solids (baked)
FEATURE [Part::Feature] path1412  label="path1413"
  shape: bbox 2.132 x 0.6968 x 2e-07 mm, 1 faces, 0 solids (baked)
FEATURE [Part::Feature] path1413  label="path1414"
  shape: bbox 2.073 x 2.262 x 2e-07 mm, 1 faces, 0 solids (baked)
FEATURE [Part::Feature] path1414  label="path1415"
  shape: bbox 0.6315 x 1.641 x 2e-07 mm, 1 faces, 0 solids (baked)
FEATURE [Part::Feature] path1415  label="path1416"
  shape: bbox 1.595 x 1.313 x 2e-07 mm, 1 faces, 0 solids (baked)
FEATURE [Part::Feature] path1416  label="path1417"
  shape: bbox 2.114 x 1.384 x 2e-07 mm, 1 faces, 0 solids (baked)
FEATURE [Part::Feature] path1417  label="path1418"
  shape: bbox 0.5152 x 0.9452 x 2e-07 mm, 1 faces, 0 solids (baked)
FEATURE [Part::Feature] path1418  label="path1419"
  shape: bbox 3.238 x 0.4018 x 2e-07 mm, 1 faces, 0 solids (baked)
FEATURE [Part::Feature] path1419  label="path1420"
  shape: bbox 2.132 x 1.052 x 2e-07 mm, 1 faces, 0 solids (baked)
FEATURE [Part::Feature] path1420  label="path1421"
  shape: bbox 1.416 x 0.3359 x 2e-07 mm, 1 faces, 0 solids (baked)
FEATURE [Part::Feature] path1421  label="path1422"
  shape: bbox 1.504 x 1.64 x 2e-07 mm, 1 faces, 0 solids (baked)
FEATURE [Part::Feature] path1422  label="path1423"
  shape: bbox 0.9436 x 1.3 x 2e-07 mm, 1 faces, 0 solids (baked)
FEATURE [Part::Feature] path1423  label="path1424"
  shape: bbox 0.9436 x 1.3 x 2e-07 mm, 1 faces, 0 solids (baked)
FEATURE [Part::Feature] path1424  label="path1425"
  shape: bbox 0.7922 x 1.309 x 2e-07 mm, 1 faces, 0 solids (baked)
FEATURE [Part::Feature] path1425  label="path1426"
  shape: bbox 0.7922 x 1.309 x 2e-07 mm, 1 faces, 0 solids (baked)
FEATURE [Part::Feature] path1426  label="path1427"
  shape: bbox 0.9436 x 1.3 x 2e-07 mm, 1 faces, 0 solids (baked)
FEATURE [Part::Feature] path1427  label="path1428"
  shape: bbox 0.9436 x 1.3 x 2e-07 mm, 1 faces, 0 solids (baked)
FEATURE [Part::Feature] path1428  label="path1429"
  shape: bbox 0.1871 x 1.29 x 2e-07 mm, 1 faces, 0 solids (baked)
FEATURE [Part::Feature] path1429  label="path1430"
  shape: bbox 0.8134 x 1.29 x 2e-07 mm, 1 faces, 0 solids (baked)
FEATURE [Part::Feature] path1430  label="path1431"
  shape: bbox 0.7917 x 1.3 x 2e-07 mm, 1 faces, 0 solids (baked)
FEATURE [Part::Feature] path1431  label="path1432"
  shape: bbox 0.7922 x 1.3 x 2e-07 mm, 1 faces, 0 solids (baked)
FEATURE [Part::Feature] path1432  label="path1433"
  shape: bbox 0.8537 x 1.289 x 2e-07 mm, 1 faces, 0 solids (baked)
FEATURE [Part::Feature] path1433  label="path1434"
  shape: bbox 0.8134 x 1.289 x 2e-07 mm, 1 faces, 0 solids (baked)
FEATURE [Part::Feature] path1434  label="path1435"
  shape: bbox 0.4196 x 0.9684 x 2e-07 mm, 1 faces, 0 solids (baked)
FEATURE [Part::Feature] path1435  label="path1436"
  shape: bbox 1.533 x 1.013 x 2e-07 mm, 1 faces, 0 solids (baked)
FEATURE [Part::Feature] path1436  label="path1437"
  shape: bbox 0.353 x 0.6051 x 2e-07 mm, 1 faces, 0 solids (baked)
FEATURE [Part::Feature] path1437  label="path1438"
  shape: bbox 0.353 x 0.6051 x 2e-07 mm, 1 faces, 0 solids (baked)
FEATURE [Part::Feature] path1438  label="path1439"
  shape: bbox 0.3524 x 0.6046 x 2e-07 mm, 1 faces, 0 solids (baked)
FEATURE [Part::Feature] path1439  label="path1440"
  shape: bbox 0.353 x 0.6046 x 2e-07 mm, 1 faces, 0 solids (baked)
FEATURE [Part::Feature] path1440  label="path1441"
  shape: bbox 1.062 x 2.78 x 2e-07 mm, 1 faces, 0 solids (baked)
FEATURE [Part::Feature] path1441  label="path1442"
  shape: bbox 1.062 x 2.78 x 2e-07 mm, 1 faces, 0 solids (baked)
FEATURE [Part::Feature] path1442  label="path1443"
  shape: bbox 1.001 x 1.001 x 2e-07 mm, 1 faces, 0 solids (baked)
FEATURE [Part::Feature] path1443  label="path1444"
  shape: bbox 3.176 x 2.63 x 2e-07 mm, 1 faces, 0 solids (baked)
FEATURE [Part::Feature] path1444  label="path1445"
  shape: bbox 1.29 x 2.309 x 2e-07 mm, 1 faces, 0 solids (baked)
FEATURE [Part::Feature] path1445  label="path1446"
  shape: bbox 1.001 x 2.033 x 2e-07 mm, 1 faces, 0 solids (baked)
FEATURE [Part::Feature] path1446  label="path1447"
  shape: bbox 1.001 x 2.049 x 2e-07 mm, 1 faces, 0 solids (baked)
FEATURE [Part::Feature] path1447  label="path1448"
  shape: bbox 0.8222 x 2.328 x 2e-07 mm, 1 faces, 0 solids (baked)
FEATURE [Part::Feature] path1448  label="path1449"
  shape: bbox 1.559 x 2.34 x 2e-07 mm, 1 faces, 0 solids (baked)
FEATURE [Part::Feature] path1449  label="path1450"
  shape: bbox 2.226 x 1.768 x 2e-07 mm, 1 faces, 0 solids (baked)
FEATURE [Part::Feature] path1450  label="path1451"
  shape: bbox 1.464 x 1.464 x 2e-07 mm, 1 faces, 0 solids (baked)
FEATURE [Part::Feature] path1451  label="path1452"
  shape: bbox 1.281 x 1.809 x 2e-07 mm, 1 faces, 0 solids (baked)
FEATURE [Part::Feature] path1452  label="path1453"
  shape: bbox 1.241 x 1.806 x 2e-07 mm, 1 faces, 0 solids (baked)
FEATURE [Part::Feature] path1453  label="path1454"
  shape: bbox 0.5684 x 1.476 x 2e-07 mm, 1 faces, 0 solids (baked)
FEATURE [Part::Feature] path1454  label="path1455"
  shape: bbox 1.252 x 0.448 x 2e-07 mm, 1 faces, 0 solids (baked)
FEATURE [Part::Feature] path1455  label="path1456"
  shape: bbox 1.083 x 1.076 x 2e-07 mm, 1 faces, 0 solids (baked)
FEATURE [Part::Feature] path1456  label="path1457"
  shape: bbox 0.3209 x 0.3209 x 2e-07 mm, 1 faces, 0 solids (baked)
FEATURE [Part::Feature] path1457  label="path1458"
  shape: bbox 0.3116 x 1.006 x 2e-07 mm, 1 faces, 0 solids (baked)
FEATURE [Part::Feature] path1458  label="path1459"
  shape: bbox 0.9436 x 1.3 x 2e-07 mm, 1 faces, 0 solids (baked)
FEATURE [Part::Feature] path1459  label="path1460"
  shape: bbox 0.7018 x 1.289 x 2e-07 mm, 1 faces, 0 solids (baked)
FEATURE [Part::Feature] path1460  label="path1461"
  shape: bbox 0.1871 x 1.289 x 2e-07 mm, 1 faces, 0 solids (baked)
FEATURE [Part::Feature] path1461  label="path1462"
  shape: bbox 0.7922 x 1.289 x 2e-07 mm, 1 faces, 0 solids (baked)
FEATURE [Part::Feature] path1462  label="path1463"
  shape: bbox 0.8098 x 1.294 x 2e-07 mm, 1 faces, 0 solids (baked)
FEATURE [Part::Feature] path1463  label="path1464"
  shape: bbox 0.8098 x 1.294 x 2e-07 mm, 1 faces, 0 solids (baked)
FEATURE [Part::Feature] path1464  label="path1465"
  shape: bbox 0.9386 x 1.289 x 2e-07 mm, 1 faces, 0 solids (baked)
FEATURE [Part::Feature] path1465  label="path1466"
  shape: bbox 1.408 x 1.296 x 2e-07 mm, 1 faces, 0 solids (baked)
FEATURE [Part::Feature] path1466  label="path1467"
  shape: bbox 0.7452 x 0.4682 x 2e-07 mm, 1 faces, 0 solids (baked)
FEATURE [Part::Feature] path1467  label="path1468"
  shape: bbox 0.3881 x 0.3509 x 2e-07 mm, 1 faces, 0 solids (baked)
FEATURE [Part::Feature] path1468  label="path1469"
  shape: bbox 0.4284 x 0.4196 x 2e-07 mm, 1 faces, 0 solids (baked)
FEATURE [Part::Feature] path1469  label="path1470"
  shape: bbox 0.4289 x 0.4196 x 2e-07 mm, 1 faces, 0 solids (baked)
FEATURE [Part::Feature] path1470  label="path1471"
  shape: bbox 0.3524 x 0.6051 x 2e-07 mm, 1 faces, 0 solids (baked)
FEATURE [Part::Feature] path1471  label="path1472"
  shape: bbox 0.4692 x 0.1473 x 2e-07 mm, 1 faces, 0 solids (baked)
FEATURE [Part::Feature] path1472  label="path1473"
  shape: bbox 0.9731 x 0.9744 x 2e-07 mm, 1 faces, 0 solids (baked)
FEATURE [Part::Feature] path1473  label="path1474"
  shape: bbox 0.4196 x 0.4584 x 2e-07 mm, 1 faces, 0 solids (baked)
FEATURE [Part::Feature] path1476  label="path1477"
  shape: bbox 1.732 x 2.6 x 2e-07 mm, 1 faces, 0 solids (baked)
FEATURE [Part::Feature] path1477  label="path1478"
  shape: bbox 1.732 x 2.6 x 2e-07 mm, 1 faces, 0 solids (baked)
FEATURE [Part::Feature] path1478  label="path1479"
  shape: bbox 1.732 x 2.6 x 2e-07 mm, 1 faces, 0 solids (baked)
FEATURE [Part::Feature] path1479  label="path1480"
  shape: bbox 0.6568 x 0.6273 x 2e-07 mm, 1 faces, 0 solids (baked)
FEATURE [Part::Feature] path1480  label="path1481"
  shape: bbox 0.6315 x 0.7369 x 2e-07 mm, 1 faces, 0 solids (baked)
FEATURE [Part::Feature] path1481  label="path1482"
  shape: bbox 0.5007 x 0.5116 x 2e-07 mm, 1 faces, 0 solids (baked)
FEATURE [Part::Feature] path1482  label="path1483"
  shape: bbox 2.962 x 1.068 x 2e-07 mm, 1 faces, 0 solids (baked)
FEATURE [Part::Feature] path1483  label="path1484"
  shape: bbox 2.049 x 0.5876 x 2e-07 mm, 1 faces, 0 solids (baked)
FEATURE [Part::Feature] path1484  label="path1485"
  shape: bbox 0.6315 x 0.7658 x 2e-07 mm, 1 faces, 0 solids (baked)
FEATURE [Part::Feature] path1485  label="path1486"
  shape: bbox 0.6568 x 0.6273 x 2e-07 mm, 1 faces, 0 solids (baked)
FEATURE [Part::Feature] path1486  label="path1487"
  shape: bbox 0.9436 x 1.3 x 2e-07 mm, 1 faces, 0 solids (baked)
FEATURE [Part::Feature] path1487  label="path1488"
  shape: bbox 0.7917 x 1.3 x 2e-07 mm, 1 faces, 0 solids (baked)
FEATURE [Part::Feature] path1488  label="path1489"
  shape: bbox 0.7922 x 1.289 x 2e-07 mm, 1 faces, 0 solids (baked)
FEATURE [Part::Feature] path1489  label="path1490"
  shape: bbox 0.3881 x 0.3509 x 2e-07 mm, 1 faces, 0 solids (baked)
FEATURE [Part::Feature] path1490  label="path1491"
  shape: bbox 0.353 x 0.6051 x 2e-07 mm, 1 faces, 0 solids (baked)
FEATURE [Part::Feature] path1491  label="path1492"
  shape: bbox 0.4196 x 0.4584 x 2e-07 mm, 1 faces, 0 solids (baked)
FEATURE [Part::Feature] path1492  label="path1493"
  shape: bbox 1.881 x 2.579 x 2e-07 mm, 1 faces, 0 solids (baked)
FEATURE [Part::Feature] path1493  label="path1494"
  shape: bbox 1.729 x 2.6 x 2e-07 mm, 1 faces, 0 solids (baked)
FEATURE [Part::Feature] path1494  label="path1495"
  shape: bbox 1.732 x 2.6 x 2e-07 mm, 1 faces, 0 solids (baked)
FEATURE [Part::Feature] path1495  label="path1496"
  shape: bbox 1.684 x 1.674 x 2e-07 mm, 1 faces, 0 solids (baked)
FEATURE [Part::Feature] path1496  label="path1497"
  shape: bbox 2.963 x 1.066 x 2e-07 mm, 1 faces, 0 solids (baked)
FEATURE [Part::Feature] path1497  label="path1498"
  shape: bbox 0.6315 x 0.7374 x 2e-07 mm, 1 faces, 0 solids (baked)
FEATURE [Part::Feature] path1498  label="path1499"
  shape: bbox 4.955 x 1.4 x 2e-07 mm, 1 faces, 0 solids (baked)
FEATURE [Part::Feature] path1499  label="path1500"
  shape: bbox 0.7617 x 1.289 x 2e-07 mm, 1 faces, 0 solids (baked)
FEATURE [Part::Feature] path1500  label="path1501"
  shape: bbox 0.7922 x 1.289 x 2e-07 mm, 1 faces, 0 solids (baked)
FEATURE [Part::Feature] path1501  label="path1502"
  shape: bbox 0.7726 x 1.289 x 2e-07 mm, 1 faces, 0 solids (baked)
FEATURE [Part::Feature] path1502  label="path1503"
  shape: bbox 0.4181 x 0.9576 x 2e-07 mm, 1 faces, 0 solids (baked)
FEATURE [Part::Feature] path1503  label="path1504"
  shape: bbox 4.397 x 0.8439 x 2e-07 mm, 1 faces, 0 solids (baked)
FEATURE [Part::Feature] path1504  label="path1505"
  shape: bbox 1.732 x 2.6 x 2e-07 mm, 1 faces, 0 solids (baked)
FEATURE [Part::Feature] path1505  label="path1506"
  shape: bbox 0.9136 x 2.586 x 2e-07 mm, 1 faces, 0 solids (baked)
FEATURE [Part::Feature] path1506  label="path1507"
  shape: bbox 1.661 x 2.579 x 2e-07 mm, 1 faces, 0 solids (baked)
FEATURE [Part::Feature] path1507  label="path1508"
  shape: bbox 2.963 x 1.067 x 2e-07 mm, 1 faces, 0 solids (baked)
FEATURE [Part::Feature] path1508  label="path1509"
  shape: bbox 1.753 x 0.6273 x 2e-07 mm, 1 faces, 0 solids (baked)
FEATURE [Part::Feature] path1509  label="path1510"
  shape: bbox 1.664 x 1.4 x 2e-07 mm, 1 faces, 0 solids (baked)
FEATURE [Part::Feature] path1510  label="path1511"
  shape: bbox 0.7694 x 1.245 x 2e-07 mm, 1 faces, 0 solids (baked)
FEATURE [Part::Feature] path1511  label="path1512"
  shape: bbox 1.105 x 0.8439 x 2e-07 mm, 1 faces, 0 solids (baked)
FEATURE [Part::Feature] path1512  label="path1513"
  shape: bbox 0.7111 x 0.8621 x 2e-07 mm, 1 faces, 0 solids (baked)
FEATURE [Part::Feature] path1522  label="path1523"
  shape: bbox 2.049 x 2.6 x 2e-07 mm, 1 faces, 0 solids (baked)
FEATURE [Part::Feature] path1523  label="path1524"
  shape: bbox 1.732 x 2.6 x 2e-07 mm, 1 faces, 0 solids (baked)
FEATURE [Part::Feature] path1524  label="path1525"
  shape: bbox 1.732 x 2.6 x 2e-07 mm, 1 faces, 0 solids (baked)
FEATURE [Part::Feature] path1525  label="path1526"
  shape: bbox 2.049 x 2.049 x 2e-07 mm, 1 faces, 0 solids (baked)
FEATURE [Part::Feature] path1526  label="path1527"
  shape: bbox 0.6315 x 1.64 x 2e-07 mm, 1 faces, 0 solids (baked)
FEATURE [Part::Feature] path1527  label="path1528"
  shape: bbox 1.753 x 0.6268 x 2e-07 mm, 1 faces, 0 solids (baked)
FEATURE [Part::Feature] path1528  label="path1529"
  shape: bbox 0.5152 x 0.9462 x 2e-07 mm, 1 faces, 0 solids (baked)
FEATURE [Part::Feature] path1529  label="path1530"
  shape: bbox 0.356 x 0.3561 x 2e-07 mm, 1 faces, 0 solids (baked)
FEATURE [Part::Feature] path1530  label="path1531"
  shape: bbox 1.753 x 0.6279 x 2e-07 mm, 1 faces, 0 solids (baked)
FEATURE [Part::Feature] path1531  label="path1532"
  shape: bbox 0.648 x 0.6516 x 2e-07 mm, 1 faces, 0 solids (baked)
FEATURE [Part::Feature] path1532  label="path1533"
  shape: bbox 0.9442 x 1.3 x 2e-07 mm, 1 faces, 0 solids (baked)
FEATURE [Part::Feature] path1533  label="path1534"
  shape: bbox 0.9436 x 1.3 x 2e-07 mm, 1 faces, 0 solids (baked)
FEATURE [Part::Feature] path1534  label="path1535"
  shape: bbox 0.9436 x 1.3 x 2e-07 mm, 1 faces, 0 solids (baked)
FEATURE [Part::Feature] path1535  label="path1536"
  shape: bbox 0.7922 x 1.3 x 2e-07 mm, 1 faces, 0 solids (baked)
FEATURE [Part::Feature] path1536  label="path1537"
  shape: bbox 0.8134 x 1.29 x 2e-07 mm, 1 faces, 0 solids (baked)
FEATURE [Part::Feature] path1537  label="path1538"
  shape: bbox 0.7922 x 1.309 x 2e-07 mm, 1 faces, 0 solids (baked)
FEATURE [Part::Feature] path1538  label="path1539"
  shape: bbox 0.8537 x 1.29 x 2e-07 mm, 1 faces, 0 solids (baked)
FEATURE [Part::Feature] path1539  label="path1540"
  shape: bbox 0.7617 x 1.289 x 2e-07 mm, 1 faces, 0 solids (baked)
FEATURE [Part::Feature] path1540  label="path1541"
  shape: bbox 0.7922 x 1.3 x 2e-07 mm, 1 faces, 0 solids (baked)
FEATURE [Part::Feature] path1541  label="path1542"
  shape: bbox 0.8098 x 1.295 x 2e-07 mm, 1 faces, 0 solids (baked)
FEATURE [Part::Feature] path1542  label="path1543"
  shape: bbox 0.9793 x 1.289 x 2e-07 mm, 1 faces, 0 solids (baked)
FEATURE [Part::Feature] path1543  label="path1544"
  shape: bbox 0.8098 x 1.294 x 2e-07 mm, 1 faces, 0 solids (baked)
FEATURE [Part::Feature] path1544  label="path1545"
  shape: bbox 0.7922 x 1.29 x 2e-07 mm, 1 faces, 0 solids (baked)
FEATURE [Part::Feature] path1545  label="path1546"
  shape: bbox 0.7726 x 1.29 x 2e-07 mm, 1 faces, 0 solids (baked)
FEATURE [Part::Feature] path1546  label="path1547"
  shape: bbox 0.8134 x 1.289 x 2e-07 mm, 1 faces, 0 solids (baked)
FEATURE [Part::Feature] path1547  label="path1548"
  shape: bbox 0.7922 x 1.289 x 2e-07 mm, 1 faces, 0 solids (baked)
FEATURE [Part::Feature] path1548  label="path1549"
  shape: bbox 0.4196 x 0.9684 x 2e-07 mm, 1 faces, 0 solids (baked)
FEATURE [Part::Feature] path1549  label="path1550"
  shape: bbox 0.4201 x 0.9684 x 2e-07 mm, 1 faces, 0 solids (baked)
FEATURE [Part::Feature] path1550  label="path1551"
  shape: bbox 0.4284 x 0.4207 x 2e-07 mm, 1 faces, 0 solids (baked)
FEATURE [Part::Feature] path1551  label="path1552"
  shape: bbox 0.3876 x 0.3509 x 2e-07 mm, 1 faces, 0 solids (baked)
FEATURE [Part::Feature] path1552  label="path1553"
  shape: bbox 0.4289 x 0.4195 x 2e-07 mm, 1 faces, 0 solids (baked)
FEATURE [Part::Feature] path1553  label="path1554"
  shape: bbox 0.4181 x 0.9576 x 2e-07 mm, 1 faces, 0 solids (baked)
FEATURE [Part::Feature] path1554  label="path1555"
  shape: bbox 0.3524 x 0.6051 x 2e-07 mm, 1 faces, 0 solids (baked)
FEATURE [Part::Feature] path1555  label="path1556"
  shape: bbox 0.353 x 0.6051 x 2e-07 mm, 1 faces, 0 solids (baked)
FEATURE [Part::Feature] path1556  label="path1557"
  shape: bbox 0.3524 x 0.6051 x 2e-07 mm, 1 faces, 0 solids (baked)
FEATURE [Part::Feature] path1557  label="path1558"
  shape: bbox 0.4196 x 0.4589 x 2e-07 mm, 1 faces, 0 solids (baked)
FEATURE [Part::Cut] Cut030
  Base = -> path1540
  Refine = true
  Tool = -> path1549
FEATURE [Part::Cut] Cut031
  Base = -> path1541
  Refine = true
  Tool = -> path1550
FEATURE [Part::Cut] Cut033  label="Cut035"
  Base = -> path1448
  Refine = true
  Tool = -> path1453
FEATURE [Part::Cut] Cut034  label="Cut036"
  Base = -> path1465
  Refine = true
  Tool = -> path1466
FEATURE [Part::Cut] Cut035  label="Cut037"
  Base = -> path1524
  Refine = true
  Tool = -> path1526
FEATURE [Part::Cut] Cut036  label="Cut038"
  Base = -> path1544
  Tool = -> path1551
FEATURE [Part::Cut] Cut037  label="Cut039"
  Base = -> Cut036
  Refine = true
  Tool = -> path1557
FEATURE [Part::Cut] Cut038  label="Cut040"
  Base = -> path1534
  Refine = true
  Tool = -> path1556
FEATURE [Part::Cut] Cut039  label="Cut041"
  Base = -> path1543
  Refine = true
  Tool = -> path1552
FEATURE [Part::Cut] Cut040  label="Cut042"
  Base = -> path1533
  Refine = true
  Tool = -> path1555
FEATURE [Part::Cut] Cut041  label="Cut043"
  Base = -> path1547
  Refine = true
  Tool = -> path1553
FEATURE [Part::Cut] Cut042  label="Cut044"
  Base = -> path1532
  Refine = true
  Tool = -> path1554
FEATURE [Part::Cut] Cut044  label="Cut046"
  Base = -> path1494
  Refine = true
  Tool = -> path1497
FEATURE [Part::Cut] Cut045  label="Cut047"
  Base = -> path1443
  Tool = -> path1451
FEATURE [Part::Cut] Cut046  label="Cut048"
  Base = -> Cut045
  Tool = -> path1445
FEATURE [Part::Cut] Cut047  label="Cut049"
  Base = -> Cut046
  Tool = -> path1452
FEATURE [Part::Cut] Cut048  label="Cut050"
  Base = -> Cut047
  Refine = true
  Tool = -> path1446
FEATURE [Part::Cut] Cut049  label="Cut051"
  Base = -> path1509
  Refine = true
  Tool = -> path1511
FEATURE [Part::Cut] Cut051  label="Cut053"
  Base = -> path1522
  Refine = true
  Tool = -> path1528
FEATURE [Part::Cut] Cut052  label="Cut054"
  Base = -> path1535
  Refine = true
  Tool = -> path1548
FEATURE [Part::Cut] Cut053  label="Cut055"
  Base = -> path1498
  Refine = true
  Tool = -> path1503
FEATURE [Part::Cut] Cut054  label="Cut056"
  Base = -> path1422
  Refine = true
  Tool = -> path1436
FEATURE [Part::Cut] Cut055  label="Cut057"
  Base = -> path1405
  Refine = true
  Tool = -> path1414
FEATURE [Part::Cut] Cut056  label="Cut058"
  Base = -> path1423
  Refine = true
  Tool = -> path1437
FEATURE [Part::Cut] Cut057  label="Cut059"
  Base = -> path1431
  Refine = true
  Tool = -> path1434
FEATURE [Part::Cut] Cut058  label="Cut060"
  Base = -> path1387
  Refine = true
  Tool = -> path1392
FEATURE [Part::Cut] Cut059  label="Cut061"
  Base = -> path1419
  Refine = true
  Tool = -> path1420
FEATURE [Part::Cut] Cut060  label="Cut062"
  Base = -> path1407
  Refine = true
  Tool = -> path1417
FEATURE [Part::Cut] Cut061  label="Cut063"
  Base = -> path1426
  Refine = true
  Tool = -> path1438
FEATURE [Part::Cut] Cut062  label="Cut064"
  Base = -> path1427
  Refine = true
  Tool = -> path1439
FEATURE [Part::Cut] Cut063  label="Cut065"
  Base = -> path1478
  Tool = -> path1484
FEATURE [Part::Cut] Cut064  label="Cut066"
  Base = -> Cut063
  Refine = true
  Tool = -> path1481
FEATURE [Part::Cut] Cut065  label="Cut067"
  Base = -> path1488
  Tool = -> path1489
FEATURE [Part::Cut] Cut066  label="Cut068"
  Base = -> Cut065
  Refine = true
  Tool = -> path1491
FEATURE [Part::Cut] Cut067  label="Cut069"
  Base = -> path1500
  Refine = true
  Tool = -> path1502
FEATURE [Part::Cut] Cut068  label="Cut070"
  Base = -> path1486
  Refine = true
  Tool = -> path1490
FEATURE [Part::Cut] Cut069  label="Cut071"
  Base = -> path1339
  Refine = true
  Tool = -> path1342
FEATURE [Part::Cut] Cut070  label="Cut072"
  Base = -> path1366
  Refine = true
  Tool = -> path1379
FEATURE [Part::Cut] Cut071  label="Cut073"
  Base = -> path1338
  Tool = -> path1346
FEATURE [Part::Cut] Cut072  label="Cut074"
  Base = -> Cut071
  Tool = -> path1344
FEATURE [Part::Cut] Cut073  label="Cut075"
  Base = -> Cut072
  Tool = -> path1347
FEATURE [Part::Cut] Cut074  label="Cut076"
  Base = -> Cut073
  Refine = true
  Tool = -> path1340
FEATURE [Part::Cut] Cut075  label="Cut077"
  Base = -> path1357
  Refine = true
  Tool = -> path1376
FEATURE [Part::Cut] Cut076  label="Cut078"
  Base = -> path1358
  Refine = true
  Tool = -> path1377
FEATURE [Part::Cut] Cut077  label="Cut079"
  Base = -> path1353
  Refine = true
  Tool = -> path1375
FEATURE [Part::Cut] Cut078  label="Cut080"
  Base = -> path1361
  Refine = true
  Tool = -> path1378
FEATURE [Part::Cut] Cut079  label="Cut081"
  Base = -> path1348
  Refine = true
  Tool = -> path1349
FEATURE [Part::Cut] Cut080  label="Cut082"
  Base = -> path1343
  Refine = true
  Tool = -> path1345
FEATURE [Part::Cut] Cut081  label="Cut083"
  Base = -> path1335
  Refine = true
  Tool = -> path1337
FEATURE [Part::Cut] Cut082  label="Cut084"
  Base = -> path1383
  Refine = true
  Tool = -> path1390
FEATURE [Part::Cut] Cut083  label="Cut085"
  Base = -> path1372
  Tool = -> path1382
FEATURE [Part::Cut] Cut084  label="Cut086"
  Base = -> Cut083
  Refine = true
  Tool = -> path1380
FEATURE [Part::Cut] Cut085  label="Cut087"
  Base = -> path1351
  Refine = true
  Tool = -> path1381
FEATURE [Part::Cut] Cut086  label="Cut088"
  Base = -> path1461
  Tool = -> path1473
FEATURE [Part::Cut] Cut087  label="Cut089"
  Base = -> Cut086
  Refine = true
  Tool = -> path1467
FEATURE [Part::Cut] Cut088  label="Cut090"
  Base = -> path1462
  Refine = true
  Tool = -> path1468
FEATURE [Part::Cut] Cut089  label="Cut091"
  Base = -> path1458
  Refine = true
  Tool = -> path1470
FEATURE [Part::Cut] Cut090  label="Cut092"
  Base = -> path1463
  Refine = true
  Tool = -> path1469
FEATURE [Part::Cut] Cut091  label="Cut093"
  Base = -> path1476
  Refine = true
  Tool = -> path1480
FEATURE [Part::Box] Box110  label="Cube107"
  AttacherType = Attacher::AttachEngine3D
  Height = 10
  Length = 10
  Placement = pos=(58.5,0,7.5) rot=(0,0,1;0rad)
  Width = 10
FEATURE [Part::Box] Box111  label="Cube108"
  AttacherType = Attacher::AttachEngine3D
  Height = 10
  Length = 10
  Placement = pos=(57,0,10.5) rot=(0,0,1;0rad)
  Width = 10
FEATURE [Part::MultiFuse] Fusion049
  Shapes = -> [Box110,Box111]
FEATURE [Part::Box] Box112  label="Cube109"
  AttacherType = Attacher::AttachEngine3D
  Height = 6
  Length = 70
  Placement = pos=(0,6.3,2.8) rot=(0,0,1;0rad)
  Width = 4
FEATURE [Part::Box] Box113  label="Cube110"
  AttacherType = Attacher::AttachEngine3D
  Height = 5
  Length = 70
  Placement = pos=(0,3.9,4.1) rot=(-1,0,0;0.488692rad)
  Width = 2.8
FEATURE [Part::MultiFuse] Fusion050
  Placement = pos=(0,-0.08,-0.15) rot=(0,0,1;0rad)
  Shapes = -> [Box112,Box113]
FEATURE [Part::Box] Box114  label="Cube111"
  AttacherType = Attacher::AttachEngine3D
  Height = 6
  Length = 70
  Placement = pos=(0,6.3,2.8) rot=(0,0,1;0rad)
  Width = 4
FEATURE [Part::Box] Box115  label="Cube112"
  AttacherType = Attacher::AttachEngine3D
  Height = 5
  Length = 70
  Placement = pos=(0,3.9,4.1) rot=(-1,0,0;0.488692rad)
  Width = 2.8
FEATURE [Part::Box] Box116  label="Cube113"
  AttacherType = Attacher::AttachEngine3D
  Height = 6
  Length = 70
  Placement = pos=(0,6.3,2.8) rot=(0,0,1;0rad)
  Width = 4
FEATURE [Part::Box] Box117  label="Cube114"
  AttacherType = Attacher::AttachEngine3D
  Height = 5
  Length = 70
  Placement = pos=(0,3.9,4.1) rot=(-1,0,0;0.488692rad)
  Width = 2.8
FEATURE [Part::Box] Box118  label="Cube115"
  AttacherType = Attacher::AttachEngine3D
  Height = 6
  Length = 70
  Placement = pos=(0,6.3,2.8) rot=(0,0,1;0rad)
  Width = 4
FEATURE [Part::Box] Box119  label="Cube116"
  AttacherType = Attacher::AttachEngine3D
  Height = 5
  Length = 70
  Placement = pos=(0,3.9,4.1) rot=(-1,0,0;0.488692rad)
  Width = 2.8
FEATURE [Part::Box] Box120  label="Cube117"
  AttacherType = Attacher::AttachEngine3D
  Height = 7
  Length = 70
  Placement = pos=(0,6.3,2.8) rot=(0,0,1;0rad)
  Width = 4
FEATURE [Part::Box] Box121  label="Cube118"
  AttacherType = Attacher::AttachEngine3D
  Height = 5
  Length = 70
  Placement = pos=(0,3.9,4.1) rot=(-1,0,0;0.488692rad)
  Width = 2.8
FEATURE [Part::Box] Box122  label="Cube119"
  AttacherType = Attacher::AttachEngine3D
  Height = 7
  Length = 70
  Placement = pos=(0,6.3,2.8) rot=(0,0,1;0rad)
  Width = 4
FEATURE [Part::Box] Box123  label="Cube120"
  AttacherType = Attacher::AttachEngine3D
  Height = 5
  Length = 70
  Placement = pos=(0,3.9,4.1) rot=(-1,0,0;0.488692rad)
  Width = 2.8
FEATURE [Part::Box] Box124  label="Cube121"
  AttacherType = Attacher::AttachEngine3D
  Height = 7
  Length = 70
  Placement = pos=(0,6.3,2.8) rot=(0,0,1;0rad)
  Width = 4
FEATURE [Part::Box] Box125  label="Cube122"
  AttacherType = Attacher::AttachEngine3D
  Height = 5
  Length = 70
  Placement = pos=(0,3.9,4.1) rot=(-1,0,0;0.488692rad)
  Width = 2.8
FEATURE [Part::Box] Box126  label="Cube123"
  AttacherType = Attacher::AttachEngine3D
  Height = 7
  Length = 70
  Placement = pos=(0,6.3,2.8) rot=(0,0,1;0rad)
  Width = 4
FEATURE [Part::Box] Box127  label="Cube124"
  AttacherType = Attacher::AttachEngine3D
  Height = 5
  Length = 70
  Placement = pos=(0,3.9,4.1) rot=(-1,0,0;0.488692rad)
  Width = 3.8
FEATURE [Part::MultiFuse] Fusion059
  Shapes = -> [Fusion010,Fusion014]
FEATURE [Part::Box] Box128  label="Cube125"
  AttacherType = Attacher::AttachEngine3D
  Height = 8
  Length = 4
  Placement = pos=(11.2,95.4,1) rot=(0,0,1;0rad)
  Width = 2
FEATURE [Part::Box] Box129  label="Cube126"
  AttacherType = Attacher::AttachEngine3D
  Height = 7
  Length = 5
  Placement = pos=(10.7,94.9,1) rot=(0,0,1;0rad)
  Width = 3
FEATURE [Part::Box] Box130  label="Cube127"
  AttacherType = Attacher::AttachEngine3D
  Height = 3
  Length = 9
  Placement = pos=(9.2,93.4,-1.3) rot=(-1,0,0;0.034907rad)
  Width = 6
FEATURE [Part::Cut] Cut095  label="Cut099"
  Base = -> Box129
  Tool = -> Box128
FEATURE [Part::Cut] Cut096  label="LED_03"
  Base = -> Cut095
  Placement = pos=(16.3,0,0) rot=(0,0,1;0rad)
  Tool = -> Box130
FEATURE [Part::Box] Box131  label="Cube128"
  AttacherType = Attacher::AttachEngine3D
  Height = 8
  Length = 4
  Placement = pos=(11.2,95.4,1) rot=(0,0,1;0rad)
  Width = 2
FEATURE [Part::Box] Box132  label="Cube129"
  AttacherType = Attacher::AttachEngine3D
  Height = 7
  Length = 5
  Placement = pos=(10.7,94.9,1) rot=(0,0,1;0rad)
  Width = 3
FEATURE [Part::Box] Box133  label="Cube130"
  AttacherType = Attacher::AttachEngine3D
  Height = 3
  Length = 9
  Placement = pos=(9.2,93.4,-1.3) rot=(-1,0,0;0.034907rad)
  Width = 6
FEATURE [Part::Cut] Cut097  label="Cut100"
  Base = -> Box132
  Tool = -> Box131
FEATURE [Part::Cut] Cut098  label="LED_04"
  Base = -> Cut097
  Placement = pos=(27.3,0,0) rot=(0,0,1;0rad)
  Tool = -> Box133
FEATURE [Part::Cylinder] Cylinder036
  Angle = 360
  AttacherType = Attacher::AttachEngine3D
  FirstAngle = 0
  Height = 8
  Placement = pos=(15.2,12,0) rot=(0,0,1;0rad)
  Radius = 1.7
  SecondAngle = 0
FEATURE [Part::Cylinder] Cylinder037
  Angle = 360
  AttacherType = Attacher::AttachEngine3D
  FirstAngle = 0
  Height = 5
  Placement = pos=(15.2,12,4) rot=(0,0,1;0rad)
  Radius = 0.9
  SecondAngle = 0
FEATURE [Part::MultiFuse] Fusion061
  Placement = pos=(12.7,0,0) rot=(0,0,1;0rad)
  Shapes = -> [Cylinder036,Cylinder037]
FEATURE [App::DocumentObjectGroup] Group002  label="SHOW_HIDE"
  Group = -> [Box104,Cut029]
FEATURE [Part::Cylinder] Cylinder038
  Angle = 360
  AttacherType = Attacher::AttachEngine3D
  FirstAngle = 0
  Height = 8
  Placement = pos=(15.2,12,0) rot=(0,0,1;0rad)
  Radius = 1.7
  SecondAngle = 0
FEATURE [Part::Cylinder] Cylinder039
  Angle = 360
  AttacherType = Attacher::AttachEngine3D
  FirstAngle = 0
  Height = 5
  Placement = pos=(15.2,12,4) rot=(0,0,1;0rad)
  Radius = 0.9
  SecondAngle = 0
FEATURE [Part::MultiFuse] Fusion062
  Placement = pos=(25.75,0,0) rot=(0,0,1;0rad)
  Shapes = -> [Cylinder038,Cylinder039]
FEATURE [Part::Cylinder] Cylinder040
  Angle = 360
  AttacherType = Attacher::AttachEngine3D
  FirstAngle = 0
  Height = 8
  Placement = pos=(15.2,12,0) rot=(0,0,1;0rad)
  Radius = 1.7
  SecondAngle = 0
FEATURE [Part::Cylinder] Cylinder041
  Angle = 360
  AttacherType = Attacher::AttachEngine3D
  FirstAngle = 0
  Height = 5
  Placement = pos=(15.2,12,4) rot=(0,0,1;0rad)
  Radius = 0.9
  SecondAngle = 0
FEATURE [Part::MultiFuse] Fusion063
  Placement = pos=(40,0,0) rot=(0,0,1;0rad)
  Shapes = -> [Cylinder040,Cylinder041]
FEATURE [Part::Cylinder] Cylinder042
  Angle = 360
  AttacherType = Attacher::AttachEngine3D
  FirstAngle = 0
  Height = 8
  Placement = pos=(15.2,12,0) rot=(0,0,1;0rad)
  Radius = 1.7
  SecondAngle = 0
FEATURE [Part::Cylinder] Cylinder043
  Angle = 360
  AttacherType = Attacher::AttachEngine3D
  FirstAngle = 0
  Height = 5
  Placement = pos=(15.2,12,4) rot=(0,0,1;0rad)
  Radius = 0.9
  SecondAngle = 0
FEATURE [Part::MultiFuse] Fusion064
  Placement = pos=(40,10,0) rot=(0,0,1;0rad)
  Shapes = -> [Cylinder042,Cylinder043]
FEATURE [Part::Cylinder] Cylinder044
  Angle = 360
  AttacherType = Attacher::AttachEngine3D
  FirstAngle = 0
  Height = 8
  Placement = pos=(15.2,12,0) rot=(0,0,1;0rad)
  Radius = 1.7
  SecondAngle = 0
FEATURE [Part::Cylinder] Cylinder045
  Angle = 360
  AttacherType = Attacher::AttachEngine3D
  FirstAngle = 0
  Height = 5
  Placement = pos=(15.2,12,4) rot=(0,0,1;0rad)
  Radius = 0.9
  SecondAngle = 0
FEATURE [Part::MultiFuse] Fusion065
  Placement = pos=(25.75,10,0) rot=(0,0,1;0rad)
  Shapes = -> [Cylinder044,Cylinder045]
FEATURE [Part::Cylinder] Cylinder046
  Angle = 360
  AttacherType = Attacher::AttachEngine3D
  FirstAngle = 0
  Height = 8
  Placement = pos=(15.2,12,0) rot=(0,0,1;0rad)
  Radius = 1.7
  SecondAngle = 0
FEATURE [Part::Cylinder] Cylinder047
  Angle = 360
  AttacherType = Attacher::AttachEngine3D
  FirstAngle = 0
  Height = 5
  Placement = pos=(15.2,12,4) rot=(0,0,1;0rad)
  Radius = 0.9
  SecondAngle = 0
FEATURE [Part::MultiFuse] Fusion066
  Placement = pos=(12.7,10,0) rot=(0,0,1;0rad)
  Shapes = -> [Cylinder046,Cylinder047]
FEATURE [Part::Cylinder] Cylinder048
  Angle = 360
  AttacherType = Attacher::AttachEngine3D
  FirstAngle = 0
  Height = 8
  Placement = pos=(15.2,12,0) rot=(0,0,1;0rad)
  Radius = 1.7
  SecondAngle = 0
FEATURE [Part::Cylinder] Cylinder049
  Angle = 360
  AttacherType = Attacher::AttachEngine3D
  FirstAngle = 0
  Height = 5
  Placement = pos=(15.2,12,4) rot=(0,0,1;0rad)
  Radius = 0.9
  SecondAngle = 0
FEATURE [Part::MultiFuse] Fusion067
  Placement = pos=(-0.3,10,0) rot=(0,0,1;0rad)
  Shapes = -> [Cylinder048,Cylinder049]
FEATURE [Part::Cylinder] Cylinder050
  Angle = 360
  AttacherType = Attacher::AttachEngine3D
  FirstAngle = 0
  Height = 8
  Placement = pos=(15.2,12,0) rot=(0,0,1;0rad)
  Radius = 1.7
  SecondAngle = 0
FEATURE [Part::Cylinder] Cylinder051
  Angle = 360
  AttacherType = Attacher::AttachEngine3D
  FirstAngle = 0
  Height = 5
  Placement = pos=(15.2,12,4) rot=(0,0,1;0rad)
  Radius = 0.9
  SecondAngle = 0
FEATURE [Part::MultiFuse] Fusion068
  Placement = pos=(-0.3,20,0) rot=(0,0,1;0rad)
  Shapes = -> [Cylinder050,Cylinder051]
FEATURE [Part::Cylinder] Cylinder052
  Angle = 360
  AttacherType = Attacher::AttachEngine3D
  FirstAngle = 0
  Height = 8
  Placement = pos=(15.2,12,0) rot=(0,0,1;0rad)
  Radius = 1.7
  SecondAngle = 0
FEATURE [Part::Cylinder] Cylinder053
  Angle = 360
  AttacherType = Attacher::AttachEngine3D
  FirstAngle = 0
  Height = 5
  Placement = pos=(15.2,12,4) rot=(0,0,1;0rad)
  Radius = 0.9
  SecondAngle = 0
FEATURE [Part::MultiFuse] Fusion069
  Placement = pos=(12.7,20,0) rot=(0,0,1;0rad)
  Shapes = -> [Cylinder052,Cylinder053]
FEATURE [Part::Cylinder] Cylinder054
  Angle = 360
  AttacherType = Attacher::AttachEngine3D
  FirstAngle = 0
  Height = 8
  Placement = pos=(15.2,12,0) rot=(0,0,1;0rad)
  Radius = 1.7
  SecondAngle = 0
FEATURE [Part::Cylinder] Cylinder055
  Angle = 360
  AttacherType = Attacher::AttachEngine3D
  FirstAngle = 0
  Height = 5
  Placement = pos=(15.2,12,4) rot=(0,0,1;0rad)
  Radius = 0.9
  SecondAngle = 0
FEATURE [Part::MultiFuse] Fusion070
  Placement = pos=(25.75,31.25,0) rot=(0,0,1;0rad)
  Shapes = -> [Cylinder054,Cylinder055]
FEATURE [Part::Cylinder] Cylinder056
  Angle = 360
  AttacherType = Attacher::AttachEngine3D
  FirstAngle = 0
  Height = 8
  Placement = pos=(15.2,12,0) rot=(0,0,1;0rad)
  Radius = 1.7
  SecondAngle = 0
FEATURE [Part::Cylinder] Cylinder057
  Angle = 360
  AttacherType = Attacher::AttachEngine3D
  FirstAngle = 0
  Height = 5
  Placement = pos=(15.2,12,4) rot=(0,0,1;0rad)
  Radius = 0.9
  SecondAngle = 0
FEATURE [Part::MultiFuse] Fusion071
  Placement = pos=(40,20,0) rot=(0,0,1;0rad)
  Shapes = -> [Cylinder056,Cylinder057]
FEATURE [Part::Box] Box134  label="Cube131"
  AttacherType = Attacher::AttachEngine3D
  Height = 8
  Length = 3.3
  Placement = pos=(11.8,95.1,1) rot=(0,0,1;0rad)
  Width = 2.5
FEATURE [Part::Box] Box135  label="Cube132"
  AttacherType = Attacher::AttachEngine3D
  Height = 7
  Length = 4
  Placement = pos=(11.4,94.9,1) rot=(0,0,1;0rad)
  Width = 3
FEATURE [Part::Box] Box136  label="Cube133"
  AttacherType = Attacher::AttachEngine3D
  Height = 3
  Length = 9
  Placement = pos=(9.2,93.4,-1.3) rot=(-1,0,0;0.034907rad)
  Width = 6
FEATURE [Part::Cut] Cut099  label="Cut105"
  Base = -> Box135
  Tool = -> Box134
FEATURE [Part::Cut] Cut100  label="LED_005"
  Base = -> Cut099
  Placement = pos=(5.2,0,0) rot=(0,0,1;0rad)
  Tool = -> Box136
FEATURE [Part::Box] Box137  label="Cube134"
  AttacherType = Attacher::AttachEngine3D
  Height = 8
  Length = 3.3
  Placement = pos=(11.8,95.1,1) rot=(0,0,1;0rad)
  Width = 2.5
FEATURE [Part::Box] Box138  label="Cube135"
  AttacherType = Attacher::AttachEngine3D
  Height = 7
  Length = 4
  Placement = pos=(11.4,94.9,1) rot=(0,0,1;0rad)
  Width = 3
FEATURE [Part::Box] Box139  label="Cube136"
  AttacherType = Attacher::AttachEngine3D
  Height = 3
  Length = 9
  Placement = pos=(9.2,93.4,-1.3) rot=(-1,0,0;0.034907rad)
  Width = 6
FEATURE [Part::Cut] Cut101
  Base = -> Box138
  Tool = -> Box137
FEATURE [Part::Cut] Cut102  label="LED_006"
  Base = -> Cut101
  Placement = pos=(16.2,0,0) rot=(0,0,1;0rad)
  Tool = -> Box139
FEATURE [Part::Box] Box140  label="Cube137"
  AttacherType = Attacher::AttachEngine3D
  Height = 8
  Length = 3.3
  Placement = pos=(11.8,95.1,1) rot=(0,0,1;0rad)
  Width = 2.5
FEATURE [Part::Box] Box141  label="Cube138"
  AttacherType = Attacher::AttachEngine3D
  Height = 7
  Length = 4
  Placement = pos=(11.4,94.9,1) rot=(0,0,1;0rad)
  Width = 3
FEATURE [Part::Box] Box142  label="Cube139"
  AttacherType = Attacher::AttachEngine3D
  Height = 3
  Length = 9
  Placement = pos=(9.2,93.4,-1.3) rot=(-1,0,0;0.034907rad)
  Width = 6
FEATURE [Part::Cut] Cut103  label="Cut106"
  Base = -> Box141
  Tool = -> Box140
FEATURE [Part::Cut] Cut104  label="LED_007"
  Base = -> Cut103
  Placement = pos=(27.2,0,0) rot=(0,0,1;0rad)
  Tool = -> Box142
FEATURE [Part::MultiFuse] Fusion015  label="LEDS"
  Shapes = -> [Cut016,Cut100,Cut102,Cut104]
FEATURE [Part::Cylinder] Cylinder058  label="LED003"
  Angle = 360
  AttacherType = Attacher::AttachEngine3D
  FirstAngle = 0
  Height = 10
  Placement = pos=(29.5,95.75,0) rot=(0,0,1;0rad)
  Radius = 0.5
  SecondAngle = 0
FEATURE [Part::Cylinder] Cylinder059  label="LED004"
  Angle = 360
  AttacherType = Attacher::AttachEngine3D
  FirstAngle = 0
  Height = 10
  Placement = pos=(40.5,95.75,0) rot=(0,0,1;0rad)
  Radius = 0.5
  SecondAngle = 0
FEATURE [Part::MultiFuse] Fusion009
  Shapes = -> [Body123,Body125,Body126,Body127,Body135,Body136,Body137,Body138,Body139,Body145,Body146,Body147,Body148,Body149,Body155,Body156,Body157,Body158,Body159,Body165,Body166,Body167,Body168,Body169,Body180,Body181,Body182,Body183,Body184,Body185,Body186,Body187,Body188,Body189,Cylinder001,Cylinder015,Body194,Body195,Body196,Body197,Body198,Body211,Body212,Body213,Body214,Body215,Body216,Body217,Body218,+5 more]
FEATURE [Part::Cut] Cut012
  Base = -> Box034
  Tool = -> Fusion009
FEATURE [Part::Feature] path10
  shape: bbox 1.555 x 2.639 x 2e-07 mm, 0 faces, 0 solids (baked)
FEATURE [Part::Feature] path1558  label="path1559"
  shape: bbox 0.5467 x 2.639 x 2e-07 mm, 0 faces, 0 solids (baked)
FEATURE [Part::Feature] path1559  label="path1560"
  shape: bbox 0.5467 x 2.639 x 2e-07 mm, 0 faces, 0 solids (baked)
FEATURE [Part::Feature] path1560  label="path1561"
  shape: bbox 1.732 x 2.635 x 2e-07 mm, 0 faces, 0 solids (baked)
FEATURE [Part::Feature] path1561  label="path1562"
  shape: bbox 1.732 x 2.579 x 2e-07 mm, 0 faces, 0 solids (baked)
FEATURE [Part::Feature] path1562  label="path1563"
  shape: bbox 2.131 x 2.579 x 2e-07 mm, 0 faces, 0 solids (baked)
FEATURE [Part::Feature] path1563  label="path1564"
  shape: bbox 1.729 x 2.6 x 2e-07 mm, 0 faces, 0 solids (baked)
FEATURE [Part::Feature] path1564  label="path1565"
  shape: bbox 1.732 x 2.6 x 2e-07 mm, 0 faces, 0 solids (baked)
FEATURE [Part::Feature] path1565  label="path1566"
  shape: bbox 0.5752 x 0.5044 x 2e-07 mm, 0 faces, 0 solids (baked)
FEATURE [Part::Feature] path1566  label="path1567"
  shape: bbox 0.5752 x 0.5044 x 2e-07 mm, 0 faces, 0 solids (baked)
FEATURE [Part::Feature] path1567  label="path1568"
  shape: bbox 1.08 x 2.41 x 2e-07 mm, 0 faces, 0 solids (baked)
FEATURE [Part::Feature] path1568  label="path1569"
  shape: bbox 1.08 x 2.41 x 2e-07 mm, 0 faces, 0 solids (baked)
FEATURE [Part::Feature] path1569  label="path1570"
  shape: bbox 0.6315 x 1.619 x 2e-07 mm, 0 faces, 0 solids (baked)
FEATURE [Part::Feature] path1570  label="path1571"
  shape: bbox 0.6315 x 1.64 x 2e-07 mm, 0 faces, 0 solids (baked)
FEATURE [Part::Feature] path1571  label="path1572"
  shape: bbox 1.411 x 1.736 x 2e-07 mm, 0 faces, 0 solids (baked)
FEATURE [Part::Feature] path1572  label="path1573"
  shape: bbox 1.57 x 1.736 x 2e-07 mm, 0 faces, 0 solids (baked)
FEATURE [Part::Feature] path1573  label="path1574"
  shape: bbox 1.584 x 1.701 x 2e-07 mm, 0 faces, 0 solids (baked)
FEATURE [Part::Feature] path1574  label="path1575"
  shape: bbox 1.411 x 1.736 x 2e-07 mm, 0 faces, 0 solids (baked)
FEATURE [Part::Feature] path1575  label="path1576"
  shape: bbox 1.411 x 1.736 x 2e-07 mm, 0 faces, 0 solids (baked)
FEATURE [Part::Feature] path1576  label="path1577"
  shape: bbox 1.499 x 1.736 x 2e-07 mm, 0 faces, 0 solids (baked)
FEATURE [Part::Feature] path1577  label="path1578"
  shape: bbox 1.411 x 1.736 x 2e-07 mm, 0 faces, 0 solids (baked)
FEATURE [Part::Feature] path1578  label="path1579"
  shape: bbox 1.5 x 1.736 x 2e-07 mm, 0 faces, 0 solids (baked)
FEATURE [Part::Feature] path1579  label="path1580"
  shape: bbox 1.605 x 1.736 x 2e-07 mm, 0 faces, 0 solids (baked)
FEATURE [Part::Feature] path1580  label="path1581"
  shape: bbox 1.228 x 1.701 x 2e-07 mm, 0 faces, 0 solids (baked)
FEATURE [Part::Feature] path1581  label="path1582"
  shape: bbox 0.5473 x 1.679 x 2e-07 mm, 0 faces, 0 solids (baked)
FEATURE [Part::Feature] path1582  label="path1583"
  shape: bbox 0.5467 x 1.679 x 2e-07 mm, 0 faces, 0 solids (baked)
FEATURE [Part::Feature] path1583  label="path1584"
  shape: bbox 0.5467 x 1.679 x 2e-07 mm, 0 faces, 0 solids (baked)
FEATURE [Part::Feature] path1584  label="path1585"
  shape: bbox 1.605 x 1.715 x 2e-07 mm, 0 faces, 0 solids (baked)
FEATURE [Part::Feature] path1585  label="path1586"
  shape: bbox 0.3561 x 0.3566 x 2e-07 mm, 0 faces, 0 solids (baked)
FEATURE [Part::Feature] path1586  label="path1587"
  shape: bbox 0.5116 x 0.2961 x 2e-07 mm, 0 faces, 0 solids (baked)
FEATURE [Part::Feature] path1587  label="path1588"
  shape: bbox 0.5116 x 0.7829 x 2e-07 mm, 0 faces, 0 solids (baked)
FEATURE [Part::Feature] path1588  label="path1589"
  shape: bbox 0.402 x 0.339 x 2e-07 mm, 0 faces, 0 solids (baked)
FEATURE [Part::Feature] path1589  label="path1590"
  shape: bbox 0.402 x 0.339 x 2e-07 mm, 0 faces, 0 solids (baked)
FEATURE [Part::MultiFuse] Fusion072
  Shapes = -> [path10,path1558,path1559,path1560,path1561,path1562,path1563,path1564,path1565,path1566,path1567,path1568,path1569,path1570,path1571,path1572,path1573,path1574,path1575,path1576,path1577,path1578,path1579,path1580,path1581,path1582,path1583,path1584,path1585,path1586,path1587,path1588,path1589]
FEATURE [Part::Extrusion] Extrude025  label="Text"
  Base = -> Fusion072
  Dir = (0,0,1)
  DirMode = 0
  FaceMakerClass = Part::FaceMakerBullseye
  FaceMakerMode = 3
  LengthFwd = 3
  LengthRev = 0
  Placement = pos=(66,146,0.2) rot=(0,1,0;3.14159rad)
  Solid = true
  Symmetric = false
FEATURE [Part::Cylinder] Cylinder060
  Angle = 360
  AttacherType = Attacher::AttachEngine3D
  FirstAngle = 0
  Height = 8
  Placement = pos=(15.2,12,0) rot=(0,0,1;0rad)
  Radius = 1.7
  SecondAngle = 0
FEATURE [Part::Cylinder] Cylinder061
  Angle = 360
  AttacherType = Attacher::AttachEngine3D
  FirstAngle = 0
  Height = 5
  Placement = pos=(15.2,12,4) rot=(0,0,1;0rad)
  Radius = 0.9
  SecondAngle = 0
FEATURE [Part::MultiFuse] Fusion073
  Placement = pos=(40,31.25,0) rot=(0,0,1;0rad)
  Shapes = -> [Cylinder060,Cylinder061]
FEATURE [Part::Cylinder] Cylinder062
  Angle = 360
  AttacherType = Attacher::AttachEngine3D
  FirstAngle = 0
  Height = 8
  Placement = pos=(15.2,12,0) rot=(0,0,1;0rad)
  Radius = 1.7
  SecondAngle = 0
FEATURE [Part::Cylinder] Cylinder063
  Angle = 360
  AttacherType = Attacher::AttachEngine3D
  FirstAngle = 0
  Height = 5
  Placement = pos=(15.2,12,4) rot=(0,0,1;0rad)
  Radius = 0.9
  SecondAngle = 0
FEATURE [Part::MultiFuse] Fusion074
  Placement = pos=(12.7,31.25,0) rot=(0,0,1;0rad)
  Shapes = -> [Cylinder062,Cylinder063]
FEATURE [Part::Cylinder] Cylinder064
  Angle = 360
  AttacherType = Attacher::AttachEngine3D
  FirstAngle = 0
  Height = 8
  Placement = pos=(15.2,12,0) rot=(0,0,1;0rad)
  Radius = 1.7
  SecondAngle = 0
FEATURE [Part::Cylinder] Cylinder065
  Angle = 360
  AttacherType = Attacher::AttachEngine3D
  FirstAngle = 0
  Height = 5
  Placement = pos=(15.2,12,4) rot=(0,0,1;0rad)
  Radius = 0.9
  SecondAngle = 0
FEATURE [Part::MultiFuse] Fusion075
  Placement = pos=(-0.3,31.25,0) rot=(0,0,1;0rad)
  Shapes = -> [Cylinder064,Cylinder065]
FEATURE [Part::Cylinder] Cylinder066
  Angle = 360
  AttacherType = Attacher::AttachEngine3D
  FirstAngle = 0
  Height = 8
  Placement = pos=(15.2,12,0) rot=(0,0,1;0rad)
  Radius = 1.7
  SecondAngle = 0
FEATURE [Part::Cylinder] Cylinder067
  Angle = 360
  AttacherType = Attacher::AttachEngine3D
  FirstAngle = 0
  Height = 5
  Placement = pos=(15.2,12,4) rot=(0,0,1;0rad)
  Radius = 0.9
  SecondAngle = 0
FEATURE [Part::MultiFuse] Fusion076
  Placement = pos=(-2.25,43,0) rot=(0,0,1;0rad)
  Shapes = -> [Cylinder066,Cylinder067]
FEATURE [Part::Cylinder] Cylinder068
  Angle = 360
  AttacherType = Attacher::AttachEngine3D
  FirstAngle = 0
  Height = 8
  Placement = pos=(15.2,12,0) rot=(0,0,1;0rad)
  Radius = 1.7
  SecondAngle = 0
FEATURE [Part::Cylinder] Cylinder069
  Angle = 360
  AttacherType = Attacher::AttachEngine3D
  FirstAngle = 0
  Height = 5
  Placement = pos=(15.2,12,4) rot=(0,0,1;0rad)
  Radius = 0.9
  SecondAngle = 0
FEATURE [Part::MultiFuse] Fusion077
  Placement = pos=(8.75,43,0) rot=(0,0,1;0rad)
  Shapes = -> [Cylinder068,Cylinder069]
FEATURE [Part::Cylinder] Cylinder070
  Angle = 360
  AttacherType = Attacher::AttachEngine3D
  FirstAngle = 0
  Height = 8
  Placement = pos=(15.2,12,0) rot=(0,0,1;0rad)
  Radius = 1.7
  SecondAngle = 0
FEATURE [Part::Cylinder] Cylinder071
  Angle = 360
  AttacherType = Attacher::AttachEngine3D
  FirstAngle = 0
  Height = 5
  Placement = pos=(15.2,12,4) rot=(0,0,1;0rad)
  Radius = 0.9
  SecondAngle = 0
FEATURE [Part::MultiFuse] Fusion078
  Placement = pos=(19.75,43,0) rot=(0,0,1;0rad)
  Shapes = -> [Cylinder070,Cylinder071]
FEATURE [Part::Cylinder] Cylinder072
  Angle = 360
  AttacherType = Attacher::AttachEngine3D
  FirstAngle = 0
  Height = 8
  Placement = pos=(15.2,12,0) rot=(0,0,1;0rad)
  Radius = 1.7
  SecondAngle = 0
FEATURE [Part::Cylinder] Cylinder073
  Angle = 360
  AttacherType = Attacher::AttachEngine3D
  FirstAngle = 0
  Height = 5
  Placement = pos=(15.2,12,4) rot=(0,0,1;0rad)
  Radius = 0.9
  SecondAngle = 0
FEATURE [Part::MultiFuse] Fusion079
  Placement = pos=(30.75,43,0) rot=(0,0,1;0rad)
  Shapes = -> [Cylinder072,Cylinder073]
FEATURE [Part::Cylinder] Cylinder074
  Angle = 360
  AttacherType = Attacher::AttachEngine3D
  FirstAngle = 0
  Height = 8
  Placement = pos=(15.2,12,0) rot=(0,0,1;0rad)
  Radius = 1.7
  SecondAngle = 0
FEATURE [Part::Cylinder] Cylinder075
  Angle = 360
  AttacherType = Attacher::AttachEngine3D
  FirstAngle = 0
  Height = 5
  Placement = pos=(15.2,12,4) rot=(0,0,1;0rad)
  Radius = 0.9
  SecondAngle = 0
FEATURE [Part::MultiFuse] Fusion080
  Placement = pos=(41.75,43,0) rot=(0,0,1;0rad)
  Shapes = -> [Cylinder074,Cylinder075]
FEATURE [Part::Cylinder] Cylinder076
  Angle = 360
  AttacherType = Attacher::AttachEngine3D
  FirstAngle = 0
  Height = 8
  Placement = pos=(15.2,12,0) rot=(0,0,1;0rad)
  Radius = 1.7
  SecondAngle = 0
FEATURE [Part::Cylinder] Cylinder077
  Angle = 360
  AttacherType = Attacher::AttachEngine3D
  FirstAngle = 0
  Height = 5
  Placement = pos=(15.2,12,4) rot=(0,0,1;0rad)
  Radius = 0.9
  SecondAngle = 0
FEATURE [Part::MultiFuse] Fusion081
  Placement = pos=(41.75,53,0) rot=(0,0,1;0rad)
  Shapes = -> [Cylinder076,Cylinder077]
FEATURE [Part::Cylinder] Cylinder078
  Angle = 360
  AttacherType = Attacher::AttachEngine3D
  FirstAngle = 0
  Height = 8
  Placement = pos=(15.2,12,0) rot=(0,0,1;0rad)
  Radius = 1.7
  SecondAngle = 0
FEATURE [Part::Cylinder] Cylinder079
  Angle = 360
  AttacherType = Attacher::AttachEngine3D
  FirstAngle = 0
  Height = 5
  Placement = pos=(15.2,12,4) rot=(0,0,1;0rad)
  Radius = 0.9
  SecondAngle = 0
FEATURE [Part::MultiFuse] Fusion082
  Placement = pos=(30.75,53,0) rot=(0,0,1;0rad)
  Shapes = -> [Cylinder078,Cylinder079]
FEATURE [Part::Cylinder] Cylinder080
  Angle = 360
  AttacherType = Attacher::AttachEngine3D
  FirstAngle = 0
  Height = 8
  Placement = pos=(15.2,12,0) rot=(0,0,1;0rad)
  Radius = 1.7
  SecondAngle = 0
FEATURE [Part::Cylinder] Cylinder081
  Angle = 360
  AttacherType = Attacher::AttachEngine3D
  FirstAngle = 0
  Height = 5
  Placement = pos=(15.2,12,4) rot=(0,0,1;0rad)
  Radius = 0.9
  SecondAngle = 0
FEATURE [Part::MultiFuse] Fusion083
  Placement = pos=(19.75,53,0) rot=(0,0,1;0rad)
  Shapes = -> [Cylinder080,Cylinder081]
FEATURE [Part::Cylinder] Cylinder082
  Angle = 360
  AttacherType = Attacher::AttachEngine3D
  FirstAngle = 0
  Height = 8
  Placement = pos=(15.2,12,0) rot=(0,0,1;0rad)
  Radius = 1.7
  SecondAngle = 0
FEATURE [Part::Cylinder] Cylinder083
  Angle = 360
  AttacherType = Attacher::AttachEngine3D
  FirstAngle = 0
  Height = 5
  Placement = pos=(15.2,12,4) rot=(0,0,1;0rad)
  Radius = 0.9
  SecondAngle = 0
FEATURE [Part::MultiFuse] Fusion084
  Placement = pos=(8.75,53,0) rot=(0,0,1;0rad)
  Shapes = -> [Cylinder082,Cylinder083]
FEATURE [Part::Cylinder] Cylinder084
  Angle = 360
  AttacherType = Attacher::AttachEngine3D
  FirstAngle = 0
  Height = 8
  Placement = pos=(15.2,12,0) rot=(0,0,1;0rad)
  Radius = 1.7
  SecondAngle = 0
FEATURE [Part::Cylinder] Cylinder085
  Angle = 360
  AttacherType = Attacher::AttachEngine3D
  FirstAngle = 0
  Height = 5
  Placement = pos=(15.2,12,4) rot=(0,0,1;0rad)
  Radius = 0.9
  SecondAngle = 0
FEATURE [Part::MultiFuse] Fusion085
  Placement = pos=(-2.25,53,0) rot=(0,0,1;0rad)
  Shapes = -> [Cylinder084,Cylinder085]
FEATURE [Part::Cylinder] Cylinder086
  Angle = 360
  AttacherType = Attacher::AttachEngine3D
  FirstAngle = 0
  Height = 8
  Placement = pos=(15.2,12,0) rot=(0,0,1;0rad)
  Radius = 1.7
  SecondAngle = 0
FEATURE [Part::Cylinder] Cylinder087
  Angle = 360
  AttacherType = Attacher::AttachEngine3D
  FirstAngle = 0
  Height = 5
  Placement = pos=(15.2,12,4) rot=(0,0,1;0rad)
  Radius = 0.9
  SecondAngle = 0
FEATURE [Part::MultiFuse] Fusion086
  Placement = pos=(-2.25,63,0) rot=(0,0,1;0rad)
  Shapes = -> [Cylinder086,Cylinder087]
FEATURE [Part::Cylinder] Cylinder088
  Angle = 360
  AttacherType = Attacher::AttachEngine3D
  FirstAngle = 0
  Height = 8
  Placement = pos=(15.2,12,0) rot=(0,0,1;0rad)
  Radius = 1.7
  SecondAngle = 0
FEATURE [Part::Cylinder] Cylinder089
  Angle = 360
  AttacherType = Attacher::AttachEngine3D
  FirstAngle = 0
  Height = 5
  Placement = pos=(15.2,12,4) rot=(0,0,1;0rad)
  Radius = 0.9
  SecondAngle = 0
FEATURE [Part::MultiFuse] Fusion087
  Placement = pos=(-2.25,73,0) rot=(0,0,1;0rad)
  Shapes = -> [Cylinder088,Cylinder089]
FEATURE [Part::Cylinder] Cylinder090
  Angle = 360
  AttacherType = Attacher::AttachEngine3D
  FirstAngle = 0
  Height = 8
  Placement = pos=(15.2,12,0) rot=(0,0,1;0rad)
  Radius = 1.7
  SecondAngle = 0
FEATURE [Part::Cylinder] Cylinder091
  Angle = 360
  AttacherType = Attacher::AttachEngine3D
  FirstAngle = 0
  Height = 5
  Placement = pos=(15.2,12,4) rot=(0,0,1;0rad)
  Radius = 0.9
  SecondAngle = 0
FEATURE [Part::MultiFuse] Fusion088
  Placement = pos=(8.75,63,0) rot=(0,0,1;0rad)
  Shapes = -> [Cylinder090,Cylinder091]
FEATURE [Part::Cylinder] Cylinder092
  Angle = 360
  AttacherType = Attacher::AttachEngine3D
  FirstAngle = 0
  Height = 8
  Placement = pos=(15.2,12,0) rot=(0,0,1;0rad)
  Radius = 1.7
  SecondAngle = 0
FEATURE [Part::Cylinder] Cylinder093
  Angle = 360
  AttacherType = Attacher::AttachEngine3D
  FirstAngle = 0
  Height = 5
  Placement = pos=(15.2,12,4) rot=(0,0,1;0rad)
  Radius = 0.9
  SecondAngle = 0
FEATURE [Part::MultiFuse] Fusion089
  Placement = pos=(8.75,73,0) rot=(0,0,1;0rad)
  Shapes = -> [Cylinder092,Cylinder093]
FEATURE [Part::Cylinder] Cylinder094
  Angle = 360
  AttacherType = Attacher::AttachEngine3D
  FirstAngle = 0
  Height = 8
  Placement = pos=(15.2,12,0) rot=(0,0,1;0rad)
  Radius = 1.7
  SecondAngle = 0
FEATURE [Part::Cylinder] Cylinder095
  Angle = 360
  AttacherType = Attacher::AttachEngine3D
  FirstAngle = 0
  Height = 5
  Placement = pos=(15.2,12,4) rot=(0,0,1;0rad)
  Radius = 0.9
  SecondAngle = 0
FEATURE [Part::MultiFuse] Fusion090
  Placement = pos=(19.75,73,0) rot=(0,0,1;0rad)
  Shapes = -> [Cylinder094,Cylinder095]
FEATURE [Part::Cylinder] Cylinder096
  Angle = 360
  AttacherType = Attacher::AttachEngine3D
  FirstAngle = 0
  Height = 8
  Placement = pos=(15.2,12,0) rot=(0,0,1;0rad)
  Radius = 1.7
  SecondAngle = 0
FEATURE [Part::Cylinder] Cylinder097
  Angle = 360
  AttacherType = Attacher::AttachEngine3D
  FirstAngle = 0
  Height = 5
  Placement = pos=(15.2,12,4) rot=(0,0,1;0rad)
  Radius = 0.9
  SecondAngle = 0
FEATURE [Part::MultiFuse] Fusion091
  Placement = pos=(19.75,63,0) rot=(0,0,1;0rad)
  Shapes = -> [Cylinder096,Cylinder097]
FEATURE [Part::Cylinder] Cylinder098
  Angle = 360
  AttacherType = Attacher::AttachEngine3D
  FirstAngle = 0
  Height = 8
  Placement = pos=(15.2,12,0) rot=(0,0,1;0rad)
  Radius = 1.7
  SecondAngle = 0
FEATURE [Part::Cylinder] Cylinder099
  Angle = 360
  AttacherType = Attacher::AttachEngine3D
  FirstAngle = 0
  Height = 5
  Placement = pos=(15.2,12,4) rot=(0,0,1;0rad)
  Radius = 0.9
  SecondAngle = 0
FEATURE [Part::MultiFuse] Fusion092
  Placement = pos=(30.75,63,0) rot=(0,0,1;0rad)
  Shapes = -> [Cylinder098,Cylinder099]
FEATURE [Part::Cylinder] Cylinder100
  Angle = 360
  AttacherType = Attacher::AttachEngine3D
  FirstAngle = 0
  Height = 8
  Placement = pos=(15.2,12,0) rot=(0,0,1;0rad)
  Radius = 1.7
  SecondAngle = 0
FEATURE [Part::Cylinder] Cylinder101
  Angle = 360
  AttacherType = Attacher::AttachEngine3D
  FirstAngle = 0
  Height = 5
  Placement = pos=(15.2,12,4) rot=(0,0,1;0rad)
  Radius = 0.9
  SecondAngle = 0
FEATURE [Part::MultiFuse] Fusion093
  Placement = pos=(30.75,73,0) rot=(0,0,1;0rad)
  Shapes = -> [Cylinder100,Cylinder101]
FEATURE [Part::Cylinder] Cylinder102
  Angle = 360
  AttacherType = Attacher::AttachEngine3D
  FirstAngle = 0
  Height = 8
  Placement = pos=(15.2,12,0) rot=(0,0,1;0rad)
  Radius = 1.7
  SecondAngle = 0
FEATURE [Part::Cylinder] Cylinder103
  Angle = 360
  AttacherType = Attacher::AttachEngine3D
  FirstAngle = 0
  Height = 5
  Placement = pos=(15.2,12,4) rot=(0,0,1;0rad)
  Radius = 0.9
  SecondAngle = 0
FEATURE [Part::MultiFuse] Fusion094
  Placement = pos=(41.75,63,0) rot=(0,0,1;0rad)
  Shapes = -> [Cylinder102,Cylinder103]
FEATURE [Part::Cylinder] Cylinder104
  Angle = 360
  AttacherType = Attacher::AttachEngine3D
  FirstAngle = 0
  Height = 8
  Placement = pos=(15.2,12,0) rot=(0,0,1;0rad)
  Radius = 1.7
  SecondAngle = 0
FEATURE [Part::Cylinder] Cylinder105
  Angle = 360
  AttacherType = Attacher::AttachEngine3D
  FirstAngle = 0
  Height = 5
  Placement = pos=(15.2,12,4) rot=(0,0,1;0rad)
  Radius = 0.9
  SecondAngle = 0
FEATURE [Part::MultiFuse] Fusion095
  Placement = pos=(41.75,73,0) rot=(0,0,1;0rad)
  Shapes = -> [Cylinder104,Cylinder105]
FEATURE [Part::Box] Box143  label="Cube140"
  AttacherType = Attacher::AttachEngine3D
  Height = 10
  Length = 70
  Placement = pos=(0,0,-5.1) rot=(-1,0,0;0.034907rad)
  Width = 100
FEATURE [Part::Cylinder] Cylinder106
  Angle = 360
  AttacherType = Attacher::AttachEngine3D
  FirstAngle = 0
  Height = 8
  Placement = pos=(15.2,12,0) rot=(0,0,1;0rad)
  Radius = 1.7
  SecondAngle = 0
FEATURE [Part::Cylinder] Cylinder107
  Angle = 360
  AttacherType = Attacher::AttachEngine3D
  FirstAngle = 0
  Height = 5
  Placement = pos=(15.2,12,4) rot=(0,0,1;0rad)
  Radius = 0.9
  SecondAngle = 0
FEATURE [Part::MultiFuse] Fusion096
  Placement = pos=(25.75,20,0) rot=(0,0,1;0rad)
  Shapes = -> [Cylinder106,Cylinder107]
FEATURE [Part::Cylinder] Cylinder108
  Angle = 360
  AttacherType = Attacher::AttachEngine3D
  FirstAngle = 0
  Height = 8
  Placement = pos=(15.2,12,0) rot=(0,0,1;0rad)
  Radius = 1.7
  SecondAngle = 0
FEATURE [Part::Cylinder] Cylinder109
  Angle = 360
  AttacherType = Attacher::AttachEngine3D
  FirstAngle = 0
  Height = 5
  Placement = pos=(15.2,12,4) rot=(0,0,1;0rad)
  Radius = 0.9
  SecondAngle = 0
FEATURE [Part::MultiFuse] Fusion097
  Placement = pos=(-0.3,0,0) rot=(0,0,1;0rad)
  Shapes = -> [Cylinder108,Cylinder109]
FEATURE [Part::MultiFuse] Fusion098
  Shapes = -> [Fusion062,Fusion063,Fusion064,Fusion065,Fusion066,Fusion067,Fusion068,Fusion069,Fusion070,Fusion071,Fusion073,Fusion074,Fusion075,Fusion076,Fusion077,Fusion078,Fusion079,Fusion080,Fusion081,Fusion082,Fusion083,Fusion084,Fusion085,Fusion086,Fusion087,Fusion088,Fusion089,Fusion090,Fusion092,Fusion093,Fusion094,Fusion095,Fusion097,Fusion061]
FEATURE [Part::Cut] Cut105  label="SUPPORTS_02"
  Base = -> Fusion098
  Tool = -> Box143
FEATURE [Part::Feature] Part__Feature7933  label="R_0603_1608Metric233"
  shape: bbox 1.6 x 0.8 x 0.45 mm, 26 faces (baked)
FEATURE [App::Part] R_0603_1608Metric179
  Group = -> [Part__Feature7933]
  Origin = -> Origin1150
  Placement = pos=(36.975,119.85,1.65) rot=(0,0,1;1.5708rad)
FEATURE [Part::Feature] Part__Feature7934  label="C_0603_1608Metric299"
  shape: bbox 1.6 x 0.8 x 0.8 mm, 28 faces (baked)
FEATURE [App::Part] C_0603_1608Metric223
  Group = -> [Part__Feature7934]
  Origin = -> Origin1151
  Placement = pos=(34.175,140.5,1.65) rot=(0,0,1;2.35619rad)
FEATURE [Part::Feature] Part__Feature7935  label="C_0603_1608Metric300"
  shape: bbox 1.6 x 0.8 x 0.8 mm, 28 faces (baked)
FEATURE [App::Part] C_0603_1608Metric224
  Group = -> [Part__Feature7935]
  Origin = -> Origin1152
  Placement = pos=(40.2,121.2,1.65) rot=(0,0,1;3.14159rad)
FEATURE [Part::Feature] Part__Feature7936  label="R_0603_1608Metric234"
  shape: bbox 1.6 x 0.8 x 0.45 mm, 26 faces (baked)
FEATURE [App::Part] R_0603_1608Metric180
  Group = -> [Part__Feature7936]
  Origin = -> Origin1153
  Placement = pos=(60.5,108,1.65) rot=(0,0,-1;1.5708rad)
FEATURE [Part::Feature] Part__Feature7937  label="R_0603_1608Metric235"
  shape: bbox 1.6 x 0.8 x 0.45 mm, 26 faces (baked)
FEATURE [App::Part] R_0603_1608Metric181
  Group = -> [Part__Feature7937]
  Origin = -> Origin1154
  Placement = pos=(18.5,128.5,1.65) rot=(0,0,1;0rad)
FEATURE [Part::Feature] Part__Feature7938  label="C_0603_1608Metric301"
  shape: bbox 1.6 x 0.8 x 0.8 mm, 28 faces (baked)
FEATURE [App::Part] C_0603_1608Metric225
  Group = -> [Part__Feature7938]
  Origin = -> Origin1155
  Placement = pos=(38,112.25,1.65) rot=(0,0,-1;1.5708rad)
FEATURE [Part::Feature] Part__Feature7939  label="R_0603_1608Metric236"
  shape: bbox 1.6 x 0.8 x 0.45 mm, 26 faces (baked)
FEATURE [App::Part] R_0603_1608Metric182
  Group = -> [Part__Feature7939]
  Origin = -> Origin1156
  Placement = pos=(50.4,113.8,1.65) rot=(0,0,1;3.14159rad)
FEATURE [Part::Feature] Part__Feature7940  label="R_0603_1608Metric237"
  shape: bbox 1.6 x 0.8 x 0.45 mm, 26 faces (baked)
FEATURE [App::Part] R_0603_1608Metric183
  Group = -> [Part__Feature7940]
  Origin = -> Origin1157
  Placement = pos=(63.25,102.25,1.65) rot=(0,0,1;1.5708rad)
FEATURE [Part::Feature] Part__Feature7941  label="C_0603_1608Metric302"
  shape: bbox 1.6 x 0.8 x 0.8 mm, 28 faces (baked)
FEATURE [App::Part] C_0603_1608Metric226
  Group = -> [Part__Feature7941]
  Origin = -> Origin1158
  Placement = pos=(35.75,112.25,1.65) rot=(0,0,-1;1.5708rad)
FEATURE [Part::Feature] Part__Feature7942  label="Cut110"
  shape: bbox 4.6 x 1.438 x 3.55 mm, 350 faces (baked)
FEATURE [App::Part] KMS223GPLFG
  Group = -> [Part__Feature7942]
  Origin = -> Origin1159
  Placement = pos=(67.8,141.95,1.65) rot=(0.57735,0.57735,0.57735;2.0944rad)
FEATURE [Part::Feature] Part__Feature7943  label="CUI_DEVICES_SJ-43516-SMT-TR"
  shape: bbox 9.003 x 6.209 x 19.5 mm, 534 faces (baked)
FEATURE [Part::Feature] Part__Feature7944  label="CUI_DEVICES_SJ-43516-SMT-TR022"
  shape: bbox 3.23 x 4.75 x 8.258 mm, 70 faces (baked)
FEATURE [App::Part] CUI_DEVICES_SJ_43516_SMT_TR  label="CUI_DEVICES_SJ-43516-SMT-TR023"
  Group = -> [Part__Feature7943,Part__Feature7944]
  Origin = -> Origin1160
FEATURE [App::Part] CUI_DEVICES_SJ_43516_SMT_TR010  label="CUI_DEVICES_SJ-43516-SMT-TR024"
  Group = -> [CUI_DEVICES_SJ_43516_SMT_TR]
  Origin = -> Origin1161
  Placement = pos=(0.5539,107.5,4.15) rot=(0.57735,-0.57735,-0.57735;2.0944rad)
FEATURE [Part::Feature] Part__Feature7945  label="R_0603_1608Metric238"
  shape: bbox 1.6 x 0.8 x 0.45 mm, 26 faces (baked)
FEATURE [App::Part] R_0603_1608Metric184
  Group = -> [Part__Feature7945]
  Origin = -> Origin1162
  Placement = pos=(24.5,135,1.65) rot=(0,0,1;0rad)
FEATURE [Part::Feature] Part__Feature7946  label="C_0603_1608Metric303"
  shape: bbox 1.6 x 0.8 x 0.8 mm, 28 faces (baked)
FEATURE [App::Part] C_0603_1608Metric227
  Group = -> [Part__Feature7946]
  Origin = -> Origin1163
  Placement = pos=(46.7,108.9,1.65) rot=(0,0,1;1.5708rad)
FEATURE [Part::Feature] Part__Feature7947  label="C_0603_1608Metric304"
  shape: bbox 1.6 x 0.8 x 0.8 mm, 28 faces (baked)
FEATURE [App::Part] C_0603_1608Metric228
  Group = -> [Part__Feature7947]
  Origin = -> Origin1164
  Placement = pos=(30.4,145.6,1.65) rot=(0,0,1;0rad)
FEATURE [Part::Feature] Part__Feature7948  label="D_SOD_324"
  shape: bbox 2.5 x 1.25 x 1.1 mm, 67 faces (baked)
FEATURE [App::Part] D_SOD_324  label="D_SOD-324"
  Group = -> [Part__Feature7948]
  Origin = -> Origin1165
  Placement = pos=(50.5,110.65,1.65) rot=(0,0,-1;1.5708rad)
FEATURE [Part::Feature] Part__Feature7949  label="C_0603_1608Metric305"
  shape: bbox 1.6 x 0.8 x 0.8 mm, 28 faces (baked)
FEATURE [App::Part] C_0603_1608Metric229
  Group = -> [Part__Feature7949]
  Origin = -> Origin1166
  Placement = pos=(38.2,145.6,1.65) rot=(0,0,1;3.14159rad)
FEATURE [Part::Feature] Part__Feature7950  label="C_0603_1608Metric306"
  shape: bbox 1.6 x 0.8 x 0.8 mm, 28 faces (baked)
FEATURE [App::Part] C_0603_1608Metric230
  Group = -> [Part__Feature7950]
  Origin = -> Origin1167
  Placement = pos=(33.075,139.4,1.65) rot=(0,0,1;2.35619rad)
FEATURE [Part::Feature] Part__Feature7951  label="SOIC-8-1EP_3.9x4.9mm_P1.27mm_EP2.41x3.81mm"
  shape: bbox 6 x 4.9 x 1.55 mm, 152 faces (baked)
FEATURE [App::Part] SOIC_8_1EP_3_9x4_9mm_P1_27mm_EP2_41x3_81mm  label="SOIC-8-1EP_3.9x4.9mm_P1.27mm_EP2.41x3.81mm010"
  Group = -> [Part__Feature7951]
  Origin = -> Origin1168
  Placement = pos=(24.2,109.1,1.65) rot=(0,0,-1;1.5708rad)
FEATURE [Part::Feature] Part__Feature7952  label="R_0603_1608Metric239"
  shape: bbox 1.6 x 0.8 x 0.45 mm, 26 faces (baked)
FEATURE [App::Part] R_0603_1608Metric185
  Group = -> [Part__Feature7952]
  Origin = -> Origin1169
  Placement = pos=(24.2,104.2,1.65) rot=(0,0,1;3.14159rad)
FEATURE [Part::Feature] Part__Feature7953  label="C_1210_3225Metric"
  shape: bbox 3.2 x 2.5 x 2.5 mm, 28 faces (baked)
FEATURE [App::Part] C_1210_3225Metric  label="C_1210_3225Metric026"
  Group = -> [Part__Feature7953]
  Origin = -> Origin1170
  Placement = pos=(29.2,104.25,1.65) rot=(0,0,1;3.14159rad)
FEATURE [Part::Feature] Part__Feature7954  label="R_0603_1608Metric240"
  shape: bbox 1.6 x 0.8 x 0.45 mm, 26 faces (baked)
FEATURE [App::Part] R_0603_1608Metric186
  Group = -> [Part__Feature7954]
  Origin = -> Origin1171
  Placement = pos=(54,109.5,1.65) rot=(0,0,1;0rad)
FEATURE [Part::Feature] Part__Feature7955  label="R_0603_1608Metric241"
  shape: bbox 1.6 x 0.8 x 0.45 mm, 26 faces (baked)
FEATURE [App::Part] R_0603_1608Metric187
  Group = -> [Part__Feature7955]
  Origin = -> Origin1172
  Placement = pos=(26.4,115.6,1.65) rot=(0,0,1;3.14159rad)
FEATURE [Part::Feature] Part__Feature7956  label="C_0603_1608Metric307"
  shape: bbox 1.6 x 0.8 x 0.8 mm, 28 faces (baked)
FEATURE [App::Part] C_0603_1608Metric231
  Group = -> [Part__Feature7956]
  Origin = -> Origin1173
  Placement = pos=(64,143.9,1.65) rot=(0,0,1;3.14159rad)
FEATURE [Part::Feature] Part__Feature7957  label="R_0603_1608Metric242"
  shape: bbox 1.6 x 0.8 x 0.45 mm, 26 faces (baked)
FEATURE [App::Part] R_0603_1608Metric188
  Group = -> [Part__Feature7957]
  Origin = -> Origin1174
  Placement = pos=(40.75,109.5,1.65) rot=(0,0,1;1.5708rad)
FEATURE [Part::Feature] Part__Feature7958  label="R_0603_1608Metric243"
  shape: bbox 1.6 x 0.8 x 0.45 mm, 26 faces (baked)
FEATURE [App::Part] R_0603_1608Metric189
  Group = -> [Part__Feature7958]
  Origin = -> Origin1175
  Placement = pos=(54,111.25,1.65) rot=(0,0,1;0rad)
FEATURE [Part::Feature] Part__Feature7959  label="R_0603_1608Metric244"
  shape: bbox 1.6 x 0.8 x 0.45 mm, 26 faces (baked)
FEATURE [App::Part] R_0603_1608Metric190
  Group = -> [Part__Feature7959]
  Origin = -> Origin1176
  Placement = pos=(26.4,114,1.65) rot=(0,0,1;0rad)
FEATURE [Part::Feature] Part__Feature7960  label="C_0603_1608Metric308"
  shape: bbox 1.6 x 0.8 x 0.8 mm, 28 faces (baked)
FEATURE [App::Part] C_0603_1608Metric232
  Group = -> [Part__Feature7960]
  Origin = -> Origin1177
  Placement = pos=(59.75,105.75,1.65) rot=(0,0,1;3.14159rad)
FEATURE [Part::Feature] Part__Feature7961  label="C_0603_1608Metric309"
  shape: bbox 1.6 x 0.8 x 0.8 mm, 28 faces (baked)
FEATURE [App::Part] C_0603_1608Metric233
  Group = -> [Part__Feature7961]
  Origin = -> Origin1178
  Placement = pos=(48.2,145.6,1.65) rot=(0,0,1;3.14159rad)
FEATURE [Part::Feature] Part__Feature7962  label="C_0603_1608Metric310"
  shape: bbox 1.6 x 0.8 x 0.8 mm, 28 faces (baked)
FEATURE [App::Part] C_0603_1608Metric234
  Group = -> [Part__Feature7962]
  Origin = -> Origin1179
  Placement = pos=(42.8,145.6,1.65) rot=(0,0,1;3.14159rad)
FEATURE [Part::Feature] Part__Feature7963  label="C_0603_1608Metric311"
  shape: bbox 1.6 x 0.8 x 0.8 mm, 28 faces (baked)
FEATURE [App::Part] C_0603_1608Metric235
  Group = -> [Part__Feature7963]
  Origin = -> Origin1180
  Placement = pos=(60.2,145.6,1.65) rot=(0,0,1;0rad)
FEATURE [Part::Feature] Part__Feature7964  label="R_0603_1608Metric245"
  shape: bbox 1.6 x 0.8 x 0.45 mm, 26 faces (baked)
FEATURE [App::Part] R_0603_1608Metric191
  Group = -> [Part__Feature7964]
  Origin = -> Origin1181
  Placement = pos=(60.5,112.75,1.65) rot=(0,0,1;1.5708rad)
FEATURE [Part::Feature] Part__Feature7965  label="LED_0603_1608Metric031"
  shape: bbox 1.6 x 0.8 x 1.1 mm, 50 faces (baked)
FEATURE [App::Part] LED_0603_1608Metric022
  Group = -> [Part__Feature7965]
  Origin = -> Origin1182
  Placement = pos=(40.5,95.75,1.65) rot=(0,0,1;3.14159rad)
FEATURE [Part::Feature] Part__Feature7966  label="R_0603_1608Metric246"
  shape: bbox 1.6 x 0.8 x 0.45 mm, 26 faces (baked)
FEATURE [App::Part] R_0603_1608Metric192
  Group = -> [Part__Feature7966]
  Origin = -> Origin1183
  Placement = pos=(63.975,139.9,1.65) rot=(0,0,1;0rad)
FEATURE [Part::Feature] Part__Feature7967  label="TSOT_23_006"
  shape: bbox 2.8 x 2.9 x 0.95 mm, 109 faces (baked)
FEATURE [App::Part] TSOT_23_006  label="TSOT-23-006"
  Group = -> [Part__Feature7967]
  Origin = -> Origin1184
  Placement = pos=(46.8,112.6,1.65) rot=(0,0,1;3.14159rad)
FEATURE [Part::Feature] Part__Feature7968  label="C_0603_1608Metric312"
  shape: bbox 1.6 x 0.8 x 0.8 mm, 28 faces (baked)
FEATURE [App::Part] C_0603_1608Metric236
  Group = -> [Part__Feature7968]
  Origin = -> Origin1185
  Placement = pos=(57.2,145.6,1.65) rot=(0,0,1;0rad)
FEATURE [Part::Feature] Part__Feature7969  label="C_0603_1608Metric313"
  shape: bbox 1.6 x 0.8 x 0.8 mm, 28 faces (baked)
FEATURE [App::Part] C_0603_1608Metric237
  Group = -> [Part__Feature7969]
  Origin = -> Origin1186
  Placement = pos=(54.2,145.6,1.65) rot=(0,0,1;0rad)
FEATURE [Part::Feature] Part__Feature7970  label="C_0603_1608Metric314"
  shape: bbox 1.6 x 0.8 x 0.8 mm, 28 faces (baked)
FEATURE [App::Part] C_0603_1608Metric238
  Group = -> [Part__Feature7970]
  Origin = -> Origin1187
  Placement = pos=(34.7,145.6,1.65) rot=(0,0,1;0rad)
FEATURE [Part::Feature] Part__Feature7971  label="R_0603_1608Metric247"
  shape: bbox 1.6 x 0.8 x 0.45 mm, 26 faces (baked)
FEATURE [App::Part] R_0603_1608Metric193
  Group = -> [Part__Feature7971]
  Origin = -> Origin1188
  Placement = pos=(18.5,126.5,1.65) rot=(0,0,1;0rad)
FEATURE [Part::Feature] Part__Feature7972  label="C_1210_3225Metric027"
  shape: bbox 3.2 x 2.5 x 2.5 mm, 28 faces (baked)
FEATURE [App::Part] C_1210_3225Metric016
  Group = -> [Part__Feature7972]
  Origin = -> Origin1189
  Placement = pos=(38.2,116.6,1.65) rot=(0,0,1;3.14159rad)
FEATURE [Part::Feature] Part__Feature7973  label="C_0603_1608Metric315"
  shape: bbox 1.6 x 0.8 x 0.8 mm, 28 faces (baked)
FEATURE [App::Part] C_0603_1608Metric239
  Group = -> [Part__Feature7973]
  Origin = -> Origin1190
  Placement = pos=(34,112.25,1.65) rot=(0,0,-1;1.5708rad)
FEATURE [Part::Feature] Part__Feature7974  label="R_0603_1608Metric248"
  shape: bbox 1.6 x 0.8 x 0.45 mm, 26 faces (baked)
FEATURE [App::Part] R_0603_1608Metric194
  Group = -> [Part__Feature7974]
  Origin = -> Origin1191
  Placement = pos=(61.5,102.25,1.65) rot=(0,0,1;1.5708rad)
FEATURE [Part::Feature] Part__Feature7975  label="C_0603_1608Metric316"
  shape: bbox 1.6 x 0.8 x 0.8 mm, 28 faces (baked)
FEATURE [App::Part] C_0603_1608Metric240
  Group = -> [Part__Feature7975]
  Origin = -> Origin1192
  Placement = pos=(51.2,145.6,1.65) rot=(0,0,1;3.14159rad)
FEATURE [Part::Feature] Part__Feature7976  label="C_0603_1608Metric317"
  shape: bbox 1.6 x 0.8 x 0.8 mm, 28 faces (baked)
FEATURE [App::Part] C_0603_1608Metric241
  Group = -> [Part__Feature7976]
  Origin = -> Origin1193
  Placement = pos=(39.225,139.35,1.65) rot=(0,0,1;0rad)
FEATURE [Part::Feature] Part__Feature7977  label="C_0603_1608Metric318"
  shape: bbox 1.6 x 0.8 x 0.8 mm, 28 faces (baked)
FEATURE [App::Part] C_0603_1608Metric242
  Group = -> [Part__Feature7977]
  Origin = -> Origin1194
  Placement = pos=(22.4,114.8,1.65) rot=(0,0,1;3.14159rad)
FEATURE [Part::Feature] Part__Feature7978  label="C_0603_1608Metric319"
  shape: bbox 1.6 x 0.8 x 0.8 mm, 28 faces (baked)
FEATURE [App::Part] C_0603_1608Metric243
  Group = -> [Part__Feature7978]
  Origin = -> Origin1195
  Placement = pos=(52.3625,104.28,1.65) rot=(0,0,1;0rad)
FEATURE [Part::Feature] Part__Feature7979  label="5025700893"
  shape: bbox 13.8 x 15.5 x 1.802 mm, 959 faces (baked)
FEATURE [App::Part] _025700893  label="5025700893016"
  Group = -> [Part__Feature7979]
  Origin = -> Origin1196
FEATURE [App::Part] _025700903  label="5025700893017"
  Group = -> [_025700893]
  Origin = -> Origin1197
  Placement = pos=(70.3986,86.625,2.65) rot=(0,0,1;1.5708rad)
FEATURE [Part::Feature] Part__Feature7980  label="R_0603_1608Metric249"
  shape: bbox 1.6 x 0.8 x 0.45 mm, 26 faces (baked)
FEATURE [App::Part] R_0603_1608Metric195
  Group = -> [Part__Feature7980]
  Origin = -> Origin1198
  Placement = pos=(34.75,108.5,1.65) rot=(0,0,-1;1.5708rad)
FEATURE [Part::Feature] Part__Feature7981  label="R_0603_1608Metric250"
  shape: bbox 1.6 x 0.8 x 0.45 mm, 26 faces (baked)
FEATURE [App::Part] R_0603_1608Metric196
  Group = -> [Part__Feature7981]
  Origin = -> Origin1199
  Placement = pos=(24.2,102.6,1.65) rot=(0,0,1;0rad)
FEATURE [Part::Feature] Part__Feature7982  label="R_0603_1608Metric251"
  shape: bbox 1.6 x 0.8 x 0.45 mm, 26 faces (baked)
FEATURE [App::Part] R_0603_1608Metric197
  Group = -> [Part__Feature7982]
  Origin = -> Origin1200
  Placement = pos=(45.1,108.9,1.65) rot=(0,0,-1;1.5708rad)
FEATURE [Part::Feature] Part__Feature7983  label="LED_0603_1608Metric032"
  shape: bbox 1.6 x 0.8 x 1.1 mm, 50 faces (baked)
FEATURE [App::Part] LED_0603_1608Metric023
  Group = -> [Part__Feature7983]
  Origin = -> Origin1201
  Placement = pos=(51.5,95.75,1.65) rot=(0,0,1;0rad)
FEATURE [Part::Feature] Part__Feature7984  label="6101xx249221"
  shape: bbox 13.2 x 8.5 x 6.3 mm, 266 faces (baked)
FEATURE [Part::Feature] Part__Feature7985  label="6101xx249291"
  shape: bbox 2 x 10.26 x 1.43 mm, 36 faces (baked)
FEATURE [Part::Feature] Part__Feature7986  label="6101xx249292"
  shape: bbox 2 x 13.19 x 3.97 mm, 36 faces (baked)
FEATURE [Part::Feature] Part__Feature7987  label="6101xx249293"
  shape: bbox 2 x 10.26 x 1.43 mm, 36 faces (baked)
FEATURE [Part::Feature] Part__Feature7988  label="6101xx249294"
  shape: bbox 2 x 13.19 x 3.97 mm, 36 faces (baked)
FEATURE [Part::Feature] Part__Feature7989  label="6101xx249295"
  shape: bbox 2 x 10.26 x 1.43 mm, 36 faces (baked)
FEATURE [Part::Feature] Part__Feature7990  label="6101xx249296"
  shape: bbox 2 x 13.19 x 3.97 mm, 36 faces (baked)
FEATURE [Part::Feature] Part__Feature7991  label="6101xx249297"
  shape: bbox 2 x 10.26 x 1.43 mm, 36 faces (baked)
FEATURE [Part::Feature] Part__Feature7992  label="6101xx249298"
  shape: bbox 2 x 13.19 x 3.97 mm, 36 faces (baked)
FEATURE [Part::Feature] Part__Feature7993  label="6101xx249299"
  shape: bbox 2 x 10.26 x 1.43 mm, 36 faces (baked)
FEATURE [Part::Feature] Part__Feature7994  label="6101xx249300"
  shape: bbox 2 x 13.19 x 3.97 mm, 36 faces (baked)
FEATURE [App::Part] _101xx249221  label="6101xx249301"
  Group = -> [Part__Feature7984,Part__Feature7985,Part__Feature7986,Part__Feature7987,Part__Feature7988,Part__Feature7989,Part__Feature7990,Part__Feature7991,Part__Feature7992,Part__Feature7993,Part__Feature7994]
  Origin = -> Origin1202
FEATURE [App::Part] _10110249221_Download_STP_610110249221_rev1  label="610110249221_Download_STP_610110249221_rev1"
  Group = -> [_101xx249221]
  Origin = -> Origin1203
  Placement = pos=(65,130.6,4.15) rot=(0,0,1;1.5708rad)
FEATURE [Part::Feature] Part__Feature7995  label="C_0603_1608Metric320"
  shape: bbox 1.6 x 0.8 x 0.8 mm, 28 faces (baked)
FEATURE [App::Part] C_0603_1608Metric244
  Group = -> [Part__Feature7995]
  Origin = -> Origin1204
  Placement = pos=(30.725,125.1,1.65) rot=(0,0,1;3.14159rad)
FEATURE [Part::Feature] Part__Feature7996  label="C_0603_1608Metric321"
  shape: bbox 1.6 x 0.8 x 0.8 mm, 28 faces (baked)
FEATURE [App::Part] C_0603_1608Metric245
  Group = -> [Part__Feature7996]
  Origin = -> Origin1205
  Placement = pos=(21,131,1.65) rot=(0,0,1;3.14159rad)
FEATURE [Part::Feature] Part__Feature7997  label="EA DOGM394"
  shape: bbox 68 x 48.06 x 0.8 mm, 6 faces (baked)
FEATURE [Part::Feature] Part__Feature7998  label="EA DOGM395"
  shape: bbox 68 x 38.06 x 1.5 mm, 6 faces (baked)
FEATURE [Part::Feature] Part__Feature7999  label="EA DOGM396"
  shape: bbox 67 x 5.953 x 1.801 mm, 13 faces (baked)
FEATURE [Part::Feature] Part__Feature8000  label="EA DOGM397"
  shape: bbox 1.5 x 1.4 x 8.2 mm, 29 faces (baked)
FEATURE [Part::Feature] Part__Feature8001  label="EA DOGM398"
  shape: bbox 1.5 x 1.4 x 8.2 mm, 29 faces (baked)
FEATURE [Part::Feature] Part__Feature8002  label="EA DOGM399"
  shape: bbox 1.5 x 1.4 x 8.2 mm, 29 faces (baked)
FEATURE [Part::Feature] Part__Feature8003  label="EA DOGM400"
  shape: bbox 1.5 x 1.4 x 8.2 mm, 29 faces (baked)
FEATURE [Part::Feature] Part__Feature8004  label="EA DOGM401"
  shape: bbox 1.5 x 1.4 x 8.2 mm, 29 faces (baked)
FEATURE [Part::Feature] Part__Feature8005  label="EA DOGM402"
  shape: bbox 1.5 x 1.4 x 8.2 mm, 29 faces (baked)
FEATURE [Part::Feature] Part__Feature8006  label="EA DOGM403"
  shape: bbox 1.5 x 1.4 x 8.2 mm, 29 faces (baked)
FEATURE [Part::Feature] Part__Feature8007  label="EA DOGM404"
  shape: bbox 1.5 x 1.4 x 8.2 mm, 29 faces (baked)
FEATURE [Part::Feature] Part__Feature8008  label="EA DOGM405"
  shape: bbox 1.5 x 1.4 x 8.2 mm, 29 faces (baked)
FEATURE [Part::Feature] Part__Feature8009  label="EA DOGM406"
  shape: bbox 1.5 x 1.4 x 8.2 mm, 29 faces (baked)
FEATURE [Part::Feature] Part__Feature8010  label="EA DOGM407"
  shape: bbox 1.5 x 1.4 x 8.2 mm, 29 faces (baked)
FEATURE [Part::Feature] Part__Feature8011  label="EA DOGM408"
  shape: bbox 1.5 x 1.4 x 8.2 mm, 29 faces (baked)
FEATURE [Part::Feature] Part__Feature8012  label="EA DOGM409"
  shape: bbox 1.5 x 1.4 x 8.2 mm, 29 faces (baked)
FEATURE [Part::Feature] Part__Feature8013  label="EA DOGM410"
  shape: bbox 1.5 x 1.4 x 8.2 mm, 29 faces (baked)
FEATURE [Part::Feature] Part__Feature8014  label="EA DOGM411"
  shape: bbox 1.5 x 1.4 x 8.2 mm, 29 faces (baked)
FEATURE [Part::Feature] Part__Feature8015  label="EA DOGM412"
  shape: bbox 1.5 x 1.4 x 8.2 mm, 29 faces (baked)
FEATURE [Part::Feature] Part__Feature8016  label="EA DOGM413"
  shape: bbox 1.5 x 1.4 x 8.2 mm, 29 faces (baked)
FEATURE [Part::Feature] Part__Feature8017  label="EA DOGM414"
  shape: bbox 1.5 x 1.4 x 8.2 mm, 29 faces (baked)
FEATURE [Part::Feature] Part__Feature8018  label="EA DOGM415"
  shape: bbox 1.5 x 1.4 x 8.2 mm, 29 faces (baked)
FEATURE [Part::Feature] Part__Feature8019  label="EA DOGM416"
  shape: bbox 1.5 x 1.4 x 8.2 mm, 29 faces (baked)
FEATURE [Part::Feature] Part__Feature8020  label="EA DOGM417"
  shape: bbox 1.5 x 1.4 x 8.2 mm, 29 faces (baked)
FEATURE [Part::Feature] Part__Feature8021  label="EA DOGM418"
  shape: bbox 1.5 x 1.4 x 8.2 mm, 29 faces (baked)
FEATURE [Part::Feature] Part__Feature8022  label="EA DOGM419"
  shape: bbox 1.5 x 1.4 x 8.2 mm, 29 faces (baked)
FEATURE [Part::Feature] Part__Feature8023  label="EA DOGM420"
  shape: bbox 1.5 x 1.4 x 8.2 mm, 29 faces (baked)
FEATURE [Part::Feature] Part__Feature8024  label="EA DOGM421"
  shape: bbox 1.5 x 1.4 x 8.2 mm, 29 faces (baked)
FEATURE [Part::Feature] Part__Feature8025  label="EA DOGM422"
  shape: bbox 1.5 x 1.4 x 8.2 mm, 29 faces (baked)
FEATURE [App::Part] EA_DOGM129  label="EA DOGM423"
  Group = -> [Part__Feature7997,Part__Feature7998,Part__Feature7999,Part__Feature8000,Part__Feature8001,Part__Feature8002,Part__Feature8003,Part__Feature8004,Part__Feature8005,Part__Feature8006,Part__Feature8007,Part__Feature8008,Part__Feature8009,Part__Feature8010,Part__Feature8011,Part__Feature8012,Part__Feature8013,Part__Feature8014,Part__Feature8015,Part__Feature8016,Part__Feature8017,Part__Feature8018,+7 more]
  Origin = -> Origin1206
FEATURE [App::Part] EA_DOGL129  label="EA DOGL129"
  Group = -> [EA_DOGM129]
  Origin = -> Origin1207
  Placement = pos=(17.8675,101.54,-39.35) rot=(0,0,1;0rad)
FEATURE [Part::Feature] Part__Feature8026  label="USB_C_Receptacle_16P_TopMnt_Horizontal_GCT_USB4105-xx-A329"
  shape: bbox 0.25 x 2.4 x 0.1 mm, 6 faces (baked)
FEATURE [Part::Feature] Part__Feature8027  label="USB_C_Receptacle_16P_TopMnt_Horizontal_GCT_USB4105-xx-A330"
  shape: bbox 0.25 x 2.4 x 0.1 mm, 6 faces (baked)
FEATURE [Part::Feature] Part__Feature8028  label="USB_C_Receptacle_16P_TopMnt_Horizontal_GCT_USB4105-xx-A331"
  shape: bbox 0.25 x 1.9 x 0.1 mm, 6 faces (baked)
FEATURE [Part::Feature] Part__Feature8029  label="USB_C_Receptacle_16P_TopMnt_Horizontal_GCT_USB4105-xx-A332"
  shape: bbox 0.25 x 1.9 x 0.1 mm, 6 faces (baked)
FEATURE [Part::Feature] Part__Feature8030  label="USB_C_Receptacle_16P_TopMnt_Horizontal_GCT_USB4105-xx-A333"
  shape: bbox 0.25 x 2.4 x 0.1 mm, 6 faces (baked)
FEATURE [Part::Feature] Part__Feature8031  label="USB_C_Receptacle_16P_TopMnt_Horizontal_GCT_USB4105-xx-A334"
  shape: bbox 0.25 x 2.4 x 0.1 mm, 6 faces (baked)
FEATURE [Part::Feature] Part__Feature8032  label="USB_C_Receptacle_16P_TopMnt_Horizontal_GCT_USB4105-xx-A335"
  shape: bbox 0.25 x 1.9 x 0.1 mm, 6 faces (baked)
FEATURE [Part::Feature] Part__Feature8033  label="USB_C_Receptacle_16P_TopMnt_Horizontal_GCT_USB4105-xx-A336"
  shape: bbox 0.25 x 1.9 x 0.1 mm, 6 faces (baked)
FEATURE [Part::Feature] Part__Feature8034  label="USB_C_Receptacle_16P_TopMnt_Horizontal_GCT_USB4105-xx-A337"
  shape: bbox 4.45 x 7.05 x 3.59 mm, 66 faces (baked)
FEATURE [Part::Feature] Part__Feature8035  label="USB_C_Receptacle_16P_TopMnt_Horizontal_GCT_USB4105-xx-A338"
  shape: bbox 0.2 x 0.8 x 0.12 mm, 6 faces (baked)
FEATURE [Part::Feature] Part__Feature8036  label="USB_C_Receptacle_16P_TopMnt_Horizontal_GCT_USB4105-xx-A339"
  shape: bbox 0.2 x 0.8 x 0.12 mm, 6 faces (baked)
FEATURE [Part::Feature] Part__Feature8037  label="USB_C_Receptacle_16P_TopMnt_Horizontal_GCT_USB4105-xx-A340"
  shape: bbox 0.2 x 0.8 x 0.12 mm, 6 faces (baked)
FEATURE [Part::Feature] Part__Feature8038  label="USB_C_Receptacle_16P_TopMnt_Horizontal_GCT_USB4105-xx-A341"
  shape: bbox 0.2 x 0.8 x 0.12 mm, 6 faces (baked)
FEATURE [Part::Feature] Part__Feature8039  label="USB_C_Receptacle_16P_TopMnt_Horizontal_GCT_USB4105-xx-A342"
  shape: bbox 0.2 x 0.8 x 0.12 mm, 6 faces (baked)
FEATURE [Part::Feature] Part__Feature8040  label="USB_C_Receptacle_16P_TopMnt_Horizontal_GCT_USB4105-xx-A343"
  shape: bbox 0.2 x 0.8 x 0.12 mm, 6 faces (baked)
FEATURE [Part::Feature] Part__Feature8041  label="USB_C_Receptacle_16P_TopMnt_Horizontal_GCT_USB4105-xx-A344"
  shape: bbox 0.2 x 0.8 x 0.12 mm, 6 faces (baked)
FEATURE [Part::Feature] Part__Feature8042  label="USB_C_Receptacle_16P_TopMnt_Horizontal_GCT_USB4105-xx-A345"
  shape: bbox 0.2 x 0.8 x 0.12 mm, 6 faces (baked)
FEATURE [Part::Feature] Part__Feature8043  label="USB_C_Receptacle_16P_TopMnt_Horizontal_GCT_USB4105-xx-A346"
  shape: bbox 4.47 x 7.33 x 4.26 mm, 161 faces (baked)
FEATURE [Part::Feature] Part__Feature8044  label="USB_C_Receptacle_16P_TopMnt_Horizontal_GCT_USB4105-xx-A347"
  shape: bbox 0.25 x 2.4 x 0.1 mm, 6 faces (baked)
FEATURE [Part::Feature] Part__Feature8045  label="USB_C_Receptacle_16P_TopMnt_Horizontal_GCT_USB4105-xx-A348"
  shape: bbox 0.25 x 2.4 x 0.1 mm, 6 faces (baked)
FEATURE [Part::Feature] Part__Feature8046  label="USB_C_Receptacle_16P_TopMnt_Horizontal_GCT_USB4105-xx-A349"
  shape: bbox 0.25 x 1.9 x 0.1 mm, 6 faces (baked)
FEATURE [Part::Feature] Part__Feature8047  label="USB_C_Receptacle_16P_TopMnt_Horizontal_GCT_USB4105-xx-A350"
  shape: bbox 0.25 x 1.9 x 0.1 mm, 6 faces (baked)
FEATURE [Part::Feature] Part__Feature8048  label="USB_C_Receptacle_16P_TopMnt_Horizontal_GCT_USB4105-xx-A351"
  shape: bbox 0.25 x 2.4 x 0.1 mm, 6 faces (baked)
FEATURE [Part::Feature] Part__Feature8049  label="USB_C_Receptacle_16P_TopMnt_Horizontal_GCT_USB4105-xx-A352"
  shape: bbox 0.25 x 2.4 x 0.1 mm, 6 faces (baked)
FEATURE [Part::Feature] Part__Feature8050  label="USB_C_Receptacle_16P_TopMnt_Horizontal_GCT_USB4105-xx-A353"
  shape: bbox 0.25 x 1.9 x 0.1 mm, 6 faces (baked)
FEATURE [Part::Feature] Part__Feature8051  label="USB_C_Receptacle_16P_TopMnt_Horizontal_GCT_USB4105-xx-A354"
  shape: bbox 0.25 x 1.9 x 0.1 mm, 6 faces (baked)
FEATURE [Part::Feature] Part__Feature8052  label="USB_C_Receptacle_16P_TopMnt_Horizontal_GCT_USB4105-xx-A355"
  shape: bbox 4.45 x 7.05 x 3.59 mm, 66 faces (baked)
FEATURE [Part::Feature] Part__Feature8053  label="USB_C_Receptacle_16P_TopMnt_Horizontal_GCT_USB4105-xx-A356"
  shape: bbox 0.2 x 0.8 x 0.12 mm, 6 faces (baked)
FEATURE [Part::Feature] Part__Feature8054  label="USB_C_Receptacle_16P_TopMnt_Horizontal_GCT_USB4105-xx-A357"
  shape: bbox 0.2 x 0.8 x 0.12 mm, 6 faces (baked)
FEATURE [Part::Feature] Part__Feature8055  label="USB_C_Receptacle_16P_TopMnt_Horizontal_GCT_USB4105-xx-A358"
  shape: bbox 0.2 x 0.8 x 0.12 mm, 6 faces (baked)
FEATURE [Part::Feature] Part__Feature8056  label="USB_C_Receptacle_16P_TopMnt_Horizontal_GCT_USB4105-xx-A359"
  shape: bbox 0.2 x 0.8 x 0.12 mm, 6 faces (baked)
FEATURE [Part::Feature] Part__Feature8057  label="USB_C_Receptacle_16P_TopMnt_Horizontal_GCT_USB4105-xx-A360"
  shape: bbox 0.2 x 0.8 x 0.12 mm, 6 faces (baked)
FEATURE [Part::Feature] Part__Feature8058  label="USB_C_Receptacle_16P_TopMnt_Horizontal_GCT_USB4105-xx-A361"
  shape: bbox 0.2 x 0.8 x 0.12 mm, 6 faces (baked)
FEATURE [Part::Feature] Part__Feature8059  label="USB_C_Receptacle_16P_TopMnt_Horizontal_GCT_USB4105-xx-A362"
  shape: bbox 0.2 x 0.8 x 0.12 mm, 6 faces (baked)
FEATURE [Part::Feature] Part__Feature8060  label="USB_C_Receptacle_16P_TopMnt_Horizontal_GCT_USB4105-xx-A363"
  shape: bbox 0.2 x 0.8 x 0.12 mm, 6 faces (baked)
FEATURE [Part::Feature] Part__Feature8061  label="USB_C_Receptacle_16P_TopMnt_Horizontal_GCT_USB4105-xx-A364"
  shape: bbox 4.47 x 7.33 x 4.26 mm, 161 faces (baked)
FEATURE [App::Part] USB_C_Receptacle_16P_TopMnt_Horizontal_GCT_USB4105_xx_A001  label="USB_C_Receptacle_16P_TopMnt_Horizontal_GCT_USB4105-xx-A365"
  Group = -> [Part__Feature8026,Part__Feature8027,Part__Feature8028,Part__Feature8029,Part__Feature8030,Part__Feature8031,Part__Feature8032,Part__Feature8033,Part__Feature8034,Part__Feature8035,Part__Feature8036,Part__Feature8037,Part__Feature8038,Part__Feature8039,Part__Feature8040,Part__Feature8041,Part__Feature8042,Part__Feature8043,Part__Feature8044,Part__Feature8045,Part__Feature8046,Part__Feature8047,+14 more]
  Origin = -> Origin1208
FEATURE [App::Part] USB_C_Receptacle_GCT_USB4105_xx_A_16P_TopMnt_Horizontal001  label="USB_C_Receptacle_GCT_USB4105-xx-A_16P_TopMnt_Horizontal001"
  Group = -> [USB_C_Receptacle_16P_TopMnt_Horizontal_GCT_USB4105_xx_A001]
  Origin = -> Origin1209
  Placement = pos=(66.05,110.4,1.65) rot=(0,0,1;1.5708rad)
FEATURE [Part::Feature] Part__Feature8062  label="C_0603_1608Metric322"
  shape: bbox 1.6 x 0.8 x 0.8 mm, 28 faces (baked)
FEATURE [App::Part] C_0603_1608Metric246
  Group = -> [Part__Feature8062]
  Origin = -> Origin1210
  Placement = pos=(48.225,129.35,1.65) rot=(0,0,-1;1.5708rad)
FEATURE [Part::Feature] Part__Feature8063  label="R_0603_1608Metric252"
  shape: bbox 1.6 x 0.8 x 0.45 mm, 26 faces (baked)
FEATURE [App::Part] R_0603_1608Metric198
  Group = -> [Part__Feature8063]
  Origin = -> Origin1211
  Placement = pos=(24.5,133.5,1.65) rot=(0,0,1;0rad)
FEATURE [Part::Feature] Part__Feature8064  label="SOT_23_007"
  shape: bbox 2.8 x 2.9 x 1.55 mm, 109 faces (baked)
FEATURE [App::Part] SOT_23_007  label="SOT-23-007"
  Group = -> [Part__Feature8064]
  Origin = -> Origin1212
  Placement = pos=(54.1125,106.95,1.65) rot=(0,0,1;0rad)
FEATURE [Part::Feature] Part__Feature8065  label="R_0603_1608Metric253"
  shape: bbox 1.6 x 0.8 x 0.45 mm, 26 faces (baked)
FEATURE [App::Part] R_0603_1608Metric199
  Group = -> [Part__Feature8065]
  Origin = -> Origin1213
  Placement = pos=(6,140,1.65) rot=(0,0,1;0rad)
FEATURE [Part::Feature] Part__Feature8066  label="SOIC_8_39x49mm_P127mm001"
  shape: bbox 6 x 4.9 x 1.75 mm, 156 faces (baked)
FEATURE [App::Part] SOIC_8_3_9x4_9mm_P1_27mm001  label="SOIC-8_3.9x4.9mm_P1.27mm001"
  Group = -> [Part__Feature8066]
  Origin = -> Origin1214
  Placement = pos=(31.975,118.9,1.65) rot=(0,0,-1;1.5708rad)
FEATURE [Part::Feature] Part__Feature8067  label="L_0805_2012Metric011"
  shape: bbox 2 x 1.25 x 1.25 mm, 28 faces (baked)
FEATURE [App::Part] L_0805_2012Metric001
  Group = -> [Part__Feature8067]
  Origin = -> Origin1215
  Placement = pos=(43.25,112.75,1.65) rot=(0,0,1;1.5708rad)
FEATURE [Part::Feature] Part__Feature8068  label="ABS006"
  shape: bbox 1.6 x 0.5025 x 1 mm, 109 faces (baked)
FEATURE [App::Part] ABS05_32_768KHZ_9_T001  label="ABS05-32.768KHZ-9-T001"
  Group = -> [Part__Feature8068]
  Origin = -> Origin1216
  Placement = pos=(35.225,138.35,1.65) rot=(0.862856,0.357407,0.357407;1.71777rad)
FEATURE [Part::Feature] Part__Feature8069  label="R_0603_1608Metric254"
  shape: bbox 1.6 x 0.8 x 0.45 mm, 26 faces (baked)
FEATURE [App::Part] R_0603_1608Metric200
  Group = -> [Part__Feature8069]
  Origin = -> Origin1217
  Placement = pos=(33,108.5,1.65) rot=(0,0,-1;1.5708rad)
FEATURE [Part::Feature] Part__Feature8070  label="R_0603_1608Metric255"
  shape: bbox 1.6 x 0.8 x 0.45 mm, 26 faces (baked)
FEATURE [App::Part] R_0603_1608Metric201
  Group = -> [Part__Feature8070]
  Origin = -> Origin1218
  Placement = pos=(30.725,123.6,1.65) rot=(0,0,1;0rad)
FEATURE [Part::Feature] Part__Feature8071  label="C_0603_1608Metric323"
  shape: bbox 1.6 x 0.8 x 0.8 mm, 28 faces (baked)
FEATURE [App::Part] C_0603_1608Metric247
  Group = -> [Part__Feature8071]
  Origin = -> Origin1219
  Placement = pos=(39.2,141,1.65) rot=(0,0,1;0rad)
FEATURE [Part::Feature] Part__Feature8072  label="S2B-PH-K-S041"
  shape: bbox 5.9 x 4.8 x 7.6 mm, 53 faces (baked)
FEATURE [Part::Feature] Part__Feature8073  label="S2B-PH-K-S042"
  shape: bbox 0.5 x 6.733 x 5.55 mm, 23 faces (baked)
FEATURE [Part::Feature] Part__Feature8074  label="S2B-PH-K-S043"
  shape: bbox 0.5 x 6.733 x 5.55 mm, 23 faces (baked)
FEATURE [App::Part] S2B_PH_K_S014  label="S2B-PH-K-S044"
  Group = -> [Part__Feature8072,Part__Feature8073,Part__Feature8074]
  Origin = -> Origin1220
FEATURE [App::Part] S2B_PH_K_S015  label="S2B-PH-K-S045"
  Group = -> [S2B_PH_K_S014]
  Origin = -> Origin1221
  Placement = pos=(48.8473,103.75,1.65) rot=(0.57735,-0.57735,-0.57735;2.0944rad)
FEATURE [Part::Feature] Part__Feature8075  label="C_1210_3225Metric028"
  shape: bbox 3.2 x 2.5 x 2.5 mm, 28 faces (baked)
FEATURE [App::Part] C_1210_3225Metric017
  Group = -> [Part__Feature8075]
  Origin = -> Origin1222
  Placement = pos=(29.2,109,1.65) rot=(0,0,1;1.5708rad)
FEATURE [Part::Feature] Part__Feature8076  label="LED_0603_1608Metric033"
  shape: bbox 1.6 x 0.8 x 1.1 mm, 50 faces (baked)
FEATURE [App::Part] LED_0603_1608Metric024
  Group = -> [Part__Feature8076]
  Origin = -> Origin1223
  Placement = pos=(62.5,95.75,1.65) rot=(0,0,1;0rad)
FEATURE [Part::Feature] Part__Feature8077  label="LED_0603_1608Metric034"
  shape: bbox 1.6 x 0.8 x 1.1 mm, 50 faces (baked)
FEATURE [App::Part] LED_0603_1608Metric025
  Group = -> [Part__Feature8077]
  Origin = -> Origin1224
  Placement = pos=(29.5,95.75,1.65) rot=(0,0,1;3.14159rad)
FEATURE [Part::Feature] Part__Feature8078  label="Cut111"
  shape: bbox 4.6 x 1.438 x 3.55 mm, 350 faces (baked)
FEATURE [App::Part] KMS223GPLFG013
  Group = -> [Part__Feature8078]
  Origin = -> Origin1225
  Placement = pos=(2.175,142,1.65) rot=(0.57735,-0.57735,-0.57735;2.0944rad)
FEATURE [Part::Feature] Part__Feature8079  label="LQFP_64_10x10mm_P05mm001"
  shape: bbox 12 x 12 x 1.5 mm, 1004 faces (baked)
FEATURE [App::Part] LQFP_64_10x10mm_P0_5mm001  label="LQFP-64_10x10mm_P0.5mm001"
  Group = -> [Part__Feature8079]
  Origin = -> Origin1226
  Placement = pos=(39.2,130.6,1.65) rot=(0,0,-1;0.785398rad)
FEATURE [Part::Feature] Part__Feature8080  label="C_0603_1608Metric324"
  shape: bbox 1.6 x 0.8 x 0.8 mm, 28 faces (baked)
FEATURE [App::Part] C_0603_1608Metric248
  Group = -> [Part__Feature8080]
  Origin = -> Origin1227
  Placement = pos=(35.475,119.85,1.65) rot=(0,0,-1;1.5708rad)
FEATURE [Part::Feature] Part__Feature8081  label="SOT_024"
  shape: bbox 2.5 x 3 x 1.2 mm, 76 faces (baked)
FEATURE [App::Part] SOT_024  label="SOT-024"
  Group = -> [Part__Feature8081]
  Origin = -> Origin1228
  Placement = pos=(54,113.85,1.65) rot=(0,0,1;0rad)
FEATURE [Part::Feature] Part__Feature8082  label="SOT_23_008"
  shape: bbox 2.8 x 2.9 x 1.55 mm, 124 faces (baked)
FEATURE [App::Part] SOT_23_008  label="SOT-23-008"
  Group = -> [Part__Feature8082]
  Origin = -> Origin1229
  Placement = pos=(58,112.75,1.65) rot=(0,0,1;1.5708rad)
FEATURE [Part::Feature] Part__Feature8083  label="R_0603_1608Metric256"
  shape: bbox 1.6 x 0.8 x 0.45 mm, 26 faces (baked)
FEATURE [App::Part] R_0603_1608Metric202
  Group = -> [Part__Feature8083]
  Origin = -> Origin1230
  Placement = pos=(18.5,124.75,1.65) rot=(0,0,1;0rad)
FEATURE [Part::Feature] Part__Feature8084  label="BK-82"
  shape: bbox 10.85 x 16.76 x 9.446 mm, 122 faces (baked)
FEATURE [App::Part] BK_82  label="BK-128"
  Group = -> [Part__Feature8084]
  Origin = -> Origin1231
  Placement = pos=(53.7,120.4,3.95) rot=(0.57735,0.57735,-0.57735;4.18879rad)
FEATURE [Part::Feature] Part__Feature8085  label="BK-129"
  shape: bbox 10.85 x 16.76 x 9.446 mm, 122 faces (baked)
FEATURE [App::Part] BK_104  label="BK-130"
  Group = -> [Part__Feature8085]
  Origin = -> Origin1232
  Placement = pos=(16.8,120.4,3.95) rot=(0.57735,-0.57735,0.57735;4.18879rad)
FEATURE [Part::Feature] Part__Feature8086  label="BK-131"
  shape: bbox 10.85 x 16.76 x 9.446 mm, 122 faces (baked)
FEATURE [App::Part] BK_105  label="BK-132"
  Group = -> [Part__Feature8086]
  Origin = -> Origin1233
  Placement = pos=(53.72,140.6,3.95) rot=(0.57735,0.57735,-0.57735;4.18879rad)
FEATURE [Part::Feature] Part__Feature8087  label="BK-133"
  shape: bbox 10.85 x 16.76 x 9.446 mm, 122 faces (baked)
FEATURE [App::Part] BK_106  label="BK-134"
  Group = -> [Part__Feature8087]
  Origin = -> Origin1234
  Placement = pos=(16.82,140.6,3.95) rot=(0.57735,-0.57735,0.57735;4.18879rad)
FEATURE [Part::Feature] Part__Feature8088  label="DM50_PCB001"
  shape: bbox 70 x 151 x 1.6 mm, 181 faces (baked)
FEATURE [App::Part] DM50_002  label="PCB"
  Group = -> [R_0603_1608Metric179,C_0603_1608Metric223,C_0603_1608Metric224,R_0603_1608Metric180,R_0603_1608Metric181,C_0603_1608Metric225,R_0603_1608Metric182,R_0603_1608Metric183,C_0603_1608Metric226,KMS223GPLFG,CUI_DEVICES_SJ_43516_SMT_TR010,R_0603_1608Metric184,C_0603_1608Metric227,C_0603_1608Metric228,D_SOD_324,C_0603_1608Metric229,C_0603_1608Metric230,SOIC_8_1EP_3_9x4_9mm_P1_27mm_EP2_41x3_81mm,+62 more]
  Origin = -> Origin1235
  Placement = pos=(70,0,9.6) rot=(0,1,0;3.14159rad)
FEATURE [Part::Box] Box144  label="Cube141"
  AttacherType = Attacher::AttachEngine3D
  Height = 10
  Length = 74
  Placement = pos=(-3,-1.03912,-6.7) rot=(-1,0,0;0.033161rad)
  Width = 101
FEATURE [Part::Box] Box145  label="Cube142"
  AttacherType = Attacher::AttachEngine3D
  Height = 8
  Length = 70
  Width = 151
FEATURE [Part::Cut] Cut106  label="case01"
  Base = -> Box145
  Tool = -> Box144
FEATURE [Part::Fillet] Fillet018  label="case002"
  Base = -> Cut106
  EdgeLinks = -> Cut106 [Edge1,Edge3,Edge4,Edge5,Edge6,Edge8,Edge11,Edge12,Edge13,Edge15]
  Edges = 10 edges r=1.5: [Edge1,Edge3,Edge4,Edge5,Edge6,Edge8,Edge11,Edge12,Edge13,Edge15]
FEATURE [Part::Box] Box146  label="Cube143"
  AttacherType = Attacher::AttachEngine3D
  Height = 10
  Length = 64
  Placement = pos=(3,104.3,-5) rot=(0,0,1;0rad)
  Width = 36.65
FEATURE [Part::Fillet] Fillet019  label="SCREEN"
  Base = -> Box146
  EdgeLinks = -> Box146 [Edge1,Edge3,Edge5,Edge7]
  Edges = 4 edges r=1: [Edge1,Edge3,Edge5,Edge7]
FEATURE [Part::MultiFuse] Fusion005
  Refine = true
  Shapes = -> [Extrude001,Extrude002,Extrude003,Box005,Box006,Compound004,Box017,Box018,Box019,Box020,Compound005,Fillet006,Compound006,Box043,Box046,Chamfer009,Fusion044,Chamfer011,Chamfer012,Fusion047,Box106,Box107,Box108,Box109,Fillet019,Extrude025]
FEATURE [Part::Box] Box147  label="Cube144"
  AttacherType = Attacher::AttachEngine3D
  Height = 10
  Length = 65.5
  Placement = pos=(2.2,100.2,-10) rot=(0,0,1;0rad)
  Width = 48.5
FEATURE [Part::Fillet] Fillet020
  Base = -> Box147
  EdgeLinks = -> Box147 [Edge1,Edge3,Edge5,Edge7]
  Edges = 4 edges r=1: [Edge1,Edge3,Edge5,Edge7]
FEATURE [App::DocumentObjectGroup] Group001  label="OBSOLETE"
  Group = -> [Compound002,Extrude016,Box001,Extrude009,Box,Cut009,Cylinder013,Cylinder014,Cut022,Fusion026,Fusion017,Fusion019,Fusion041,Chamfer008,Cut096,Cut098,Fusion091,Fusion096,Fillet020]
FEATURE [Part::MultiFuse] Fusion052
  Placement = pos=(0,19.93,-0.8) rot=(0,0,1;0rad)
  Shapes = -> [Box116,Box117]
FEATURE [Part::MultiFuse] Fusion053
  Placement = pos=(0,29.9,-1.15) rot=(0,0,1;0rad)
  Shapes = -> [Box118,Box119]
FEATURE [Part::MultiFuse] Fusion054
  Placement = pos=(0,42.94,-1.58) rot=(0,0,1;0rad)
  Shapes = -> [Box120,Box121]
FEATURE [Part::MultiFuse] Fusion055
  Placement = pos=(0,52.94,-1.91) rot=(0,0,1;0rad)
  Shapes = -> [Box122,Box123]
FEATURE [Part::MultiFuse] Fusion056
  Placement = pos=(0,62.94,-2.25) rot=(0,0,1;0rad)
  Shapes = -> [Box124,Box125]
FEATURE [Part::MultiFuse] Fusion057
  Placement = pos=(0,72.92,-2.57) rot=(0,0,1;0rad)
  Shapes = -> [Box126,Box127]
FEATURE [Part::MultiFuse] Fusion051
  Placement = pos=(0,9.9,-0.48) rot=(0,0,1;0rad)
  Shapes = -> [Box114,Box115]
FEATURE [Part::MultiFuse] Fusion058
  Refine = true
  Shapes = -> [Fusion050,Fusion051,Fusion052,Fusion053,Fusion054,Fusion055,Fusion056,Fusion057]
FEATURE [Part::Box] Box148  label="Cube145"
  AttacherType = Attacher::AttachEngine3D
  Height = 6
  Length = 70
  Placement = pos=(0,6.3,2.8) rot=(0,0,1;0rad)
  Width = 4
FEATURE [Part::Box] Box149  label="Cube146"
  AttacherType = Attacher::AttachEngine3D
  Height = 5
  Length = 70
  Placement = pos=(0,3.9,4.1) rot=(-1,0,0;0.488692rad)
  Width = 2.8
FEATURE [Part::Box] Box150  label="Cube147"
  AttacherType = Attacher::AttachEngine3D
  Height = 6
  Length = 70
  Placement = pos=(0,6.3,2.8) rot=(0,0,1;0rad)
  Width = 4
FEATURE [Part::Box] Box151  label="Cube148"
  AttacherType = Attacher::AttachEngine3D
  Height = 5
  Length = 70
  Placement = pos=(0,3.9,4.1) rot=(-1,0,0;0.488692rad)
  Width = 2.8
FEATURE [Part::Box] Box152  label="Cube149"
  AttacherType = Attacher::AttachEngine3D
  Height = 6
  Length = 70
  Placement = pos=(0,6.3,2.8) rot=(0,0,1;0rad)
  Width = 4
FEATURE [Part::Box] Box153  label="Cube150"
  AttacherType = Attacher::AttachEngine3D
  Height = 5
  Length = 70
  Placement = pos=(0,3.9,4.1) rot=(-1,0,0;0.488692rad)
  Width = 2.8
FEATURE [Part::Box] Box154  label="Cube151"
  AttacherType = Attacher::AttachEngine3D
  Height = 6
  Length = 70
  Placement = pos=(0,6.3,2.8) rot=(0,0,1;0rad)
  Width = 4
FEATURE [Part::Box] Box155  label="Cube152"
  AttacherType = Attacher::AttachEngine3D
  Height = 5
  Length = 70
  Placement = pos=(0,3.9,4.1) rot=(-1,0,0;0.488692rad)
  Width = 2.8
FEATURE [Part::Box] Box156  label="Cube153"
  AttacherType = Attacher::AttachEngine3D
  Height = 7
  Length = 70
  Placement = pos=(0,6.3,2.8) rot=(0,0,1;0rad)
  Width = 4
FEATURE [Part::Box] Box157  label="Cube154"
  AttacherType = Attacher::AttachEngine3D
  Height = 5
  Length = 70
  Placement = pos=(0,3.9,4.1) rot=(-1,0,0;0.488692rad)
  Width = 2.8
FEATURE [Part::Box] Box158  label="Cube155"
  AttacherType = Attacher::AttachEngine3D
  Height = 7
  Length = 70
  Placement = pos=(0,6.3,2.8) rot=(0,0,1;0rad)
  Width = 4
FEATURE [Part::Box] Box159  label="Cube156"
  AttacherType = Attacher::AttachEngine3D
  Height = 5
  Length = 70
  Placement = pos=(0,3.9,4.1) rot=(-1,0,0;0.488692rad)
  Width = 2.8
FEATURE [Part::Box] Box160  label="Cube157"
  AttacherType = Attacher::AttachEngine3D
  Height = 7
  Length = 70
  Placement = pos=(0,6.3,2.8) rot=(0,0,1;0rad)
  Width = 4
FEATURE [Part::Box] Box161  label="Cube158"
  AttacherType = Attacher::AttachEngine3D
  Height = 5
  Length = 70
  Placement = pos=(0,3.9,4.1) rot=(-1,0,0;0.488692rad)
  Width = 2.8
FEATURE [Part::Box] Box162  label="Cube159"
  AttacherType = Attacher::AttachEngine3D
  Height = 7
  Length = 70
  Placement = pos=(0,6.3,2.8) rot=(0,0,1;0rad)
  Width = 4
FEATURE [Part::Box] Box163  label="Cube160"
  AttacherType = Attacher::AttachEngine3D
  Height = 5
  Length = 70
  Placement = pos=(0,3.9,4.1) rot=(-1,0,0;0.488692rad)
  Width = 3.8
FEATURE [Part::MultiFuse] Fusion099
  Placement = pos=(0,-0.08,-0.15) rot=(0,0,1;0rad)
  Shapes = -> [Box148,Box149]
FEATURE [Part::MultiFuse] Fusion100
  Placement = pos=(0,9.9,-0.48) rot=(0,0,1;0rad)
  Shapes = -> [Box150,Box151]
FEATURE [Part::MultiFuse] Fusion101
  Placement = pos=(0,19.93,-0.8) rot=(0,0,1;0rad)
  Shapes = -> [Box152,Box153]
FEATURE [Part::MultiFuse] Fusion102
  Placement = pos=(0,29.9,-1.15) rot=(0,0,1;0rad)
  Shapes = -> [Box154,Box155]
FEATURE [Part::MultiFuse] Fusion103
  Placement = pos=(0,42.94,-1.58) rot=(0,0,1;0rad)
  Shapes = -> [Box156,Box157]
FEATURE [Part::MultiFuse] Fusion104
  Placement = pos=(0,52.94,-1.91) rot=(0,0,1;0rad)
  Shapes = -> [Box158,Box159]
FEATURE [Part::MultiFuse] Fusion105
  Placement = pos=(0,62.94,-2.25) rot=(0,0,1;0rad)
  Shapes = -> [Box160,Box161]
FEATURE [Part::MultiFuse] Fusion106
  Placement = pos=(0,72.92,-2.57) rot=(0,0,1;0rad)
  Shapes = -> [Box162,Box163]
FEATURE [Part::MultiFuse] Fusion107
  Placement = pos=(0,0,1) rot=(0,0,1;0rad)
  Refine = true
  Shapes = -> [Fusion099,Fusion100,Fusion101,Fusion102,Fusion103,Fusion104,Fusion105,Fusion106]
FEATURE [Part::MultiFuse] Fusion108
  Refine = true
  Shapes = -> [Fusion107,Fusion058]
FEATURE [Part::Feature] path1513  label="path1514"
  shape: bbox 0.6739 x 0.8361 x 2e-07 mm, 2 faces, 0 solids (baked)
FEATURE [Sketcher::SketchObject] Sketch017
  ArcFitTolerance = 1e-06
  FullyConstrained = false
  MakeInternals = false
  Placement = pos=(0,0,0) rot=(0,0,1;3.14159rad)
  sketch-geometry (21):
    g0: BSplineCurve PolesCount=2 KnotsCount=2 Degree=1 IsPeriodic=0
    g1: BSplineCurve PolesCount=4 KnotsCount=2 Degree=3 IsPeriodic=0
    g2: BSplineCurve PolesCount=4 KnotsCount=2 Degree=3 IsPeriodic=0
    g3: BSplineCurve PolesCount=4 KnotsCount=2 Degree=3 IsPeriodic=0
    g4: BSplineCurve PolesCount=4 KnotsCount=2 Degree=3 IsPeriodic=0
    g5: BSplineCurve PolesCount=2 KnotsCount=2 Degree=1 IsPeriodic=0
    g6: BSplineCurve PolesCount=2 KnotsCount=2 Degree=1 IsPeriodic=0
    g7: BSplineCurve PolesCount=4 KnotsCount=2 Degree=3 IsPeriodic=0
    g8: BSplineCurve PolesCount=4 KnotsCount=2 Degree=3 IsPeriodic=0
    g9: BSplineCurve PolesCount=4 KnotsCount=2 Degree=3 IsPeriodic=0
    g10: BSplineCurve PolesCount=4 KnotsCount=2 Degree=3 IsPeriodic=0
    g11: BSplineCurve PolesCount=2 KnotsCount=2 Degree=1 IsPeriodic=0
    g12: BSplineCurve PolesCount=4 KnotsCount=2 Degree=3 IsPeriodic=0
    g13: BSplineCurve PolesCount=4 KnotsCount=2 Degree=3 IsPeriodic=0
    g14: BSplineCurve PolesCount=4 KnotsCount=2 Degree=3 IsPeriodic=0
    g15: BSplineCurve PolesCount=4 KnotsCount=2 Degree=3 IsPeriodic=0
    g16: BSplineCurve PolesCount=2 KnotsCount=2 Degree=1 IsPeriodic=0
    g17: BSplineCurve PolesCount=2 KnotsCount=2 Degree=1 IsPeriodic=0
    g18: BSplineCurve PolesCount=4 KnotsCount=2 Degree=3 IsPeriodic=0
    g19: BSplineCurve PolesCount=4 KnotsCount=2 Degree=3 IsPeriodic=0
    g20: BSplineCurve PolesCount=4 KnotsCount=2 Degree=3 IsPeriodic=0
  constraints (4):
    c: Coincident(g19,g20)
    c: Coincident(g1,g2)
    c: Coincident(g0,g1)
    c: Coincident(g20,g0)
FEATURE [Part::Feature] Sketch018
  shape: bbox 0.6739 x 0.8361 x 2e-07 mm, 0 faces, 0 solids (baked)
FEATURE [Part::Face] Face
  FaceMakerClass = Part::FaceMakerBullseye
  Sources = -> [Sketch018]
FEATURE [Part::MultiFuse] Fusion048
  Shapes = -> [path3,path1336,path1341,path1350,path1352,path1354,path1355,path1356,path1359,path1360,path1362,path1363,path1364,path1365,path1367,path1368,path1369,path1370,path1371,path1373,path1374,path1384,path1385,path1386,path1388,path1389,path1391,path1393,path1394,path1395,path1396,path1397,path1398,path1399,path1400,path1401,path1402,path1403,path1404,path1406,path1408,path1409,path1410,path1411,+111 more]
FEATURE [Part::Extrusion] Extrude024
  Base = -> Fusion048
  Dir = (0,0,1)
  DirMode = 0
  FaceMakerClass = Part::FaceMakerBullseye
  FaceMakerMode = 3
  LengthFwd = 6
  LengthRev = 0
  Placement = pos=(66,82.5,4) rot=(0,1,0;3.14159rad)
  Solid = false
  Symmetric = false
FEATURE [Part::Cut] Cut092  label="Cut094"
  Base = -> Extrude024
  Placement = pos=(0,0,1.8) rot=(-1,0,0;0.034907rad)
  Refine = true
  Tool = -> Fusion049
FEATURE [Part::Cut] Cut
  Base = -> Cut092
  Refine = true
  Tool = -> Fusion108
FEATURE [Part::Cut] Cut107
  Base = -> Fusion059
  Tool = -> Cut
FEATURE [Part::Cut] Cut108
  Base = -> Fillet018
  Tool = -> Fusion005
FEATURE [Part::Box] Box164  label="CUT_KEYS"
  AttacherType = Attacher::AttachEngine3D
  Height = 3
  Length = 1
  Placement = pos=(5,2,5.2) rot=(0,0,1;0rad)
  Width = 3.5
FEATURE [App::DocumentObjectGroup] Group  label="MODELS"
  Group = -> [Fusion003,Fusion,Extrude012,Extrude015,Fusion004,Cut007,Cut008,Compound,Fusion006,Cut011,Fillet008,path1334,Fusion011,Fillet010,Fillet012,Fillet013,Fusion038,Fillet016,Chamfer010,Sketch017,Box164]
FEATURE [PartDesign::FeatureBase] Clone383
  BaseFeature = -> Box164
  Placement = pos=(5,2.1,5.2) rot=(0,0,1;0rad)
  Suppressed = false
FEATURE [PartDesign::Body] Body382
  AllowCompound = false
  Group = -> [Clone383]
  Origin = -> Origin1236
  Tip = -> Clone383
FEATURE [PartDesign::FeatureBase] Clone384
  BaseFeature = -> Box164
  Placement = pos=(5,2.1,5.2) rot=(0,0,1;0rad)
  Suppressed = false
FEATURE [PartDesign::Body] Body383
  AllowCompound = false
  Group = -> [Clone384]
  Origin = -> Origin1237
  Placement = pos=(6,0,0) rot=(0,0,1;0rad)
  Tip = -> Clone384
FEATURE [PartDesign::FeatureBase] Clone385
  BaseFeature = -> Box164
  Placement = pos=(5,2.1,5.2) rot=(0,0,1;0rad)
  Suppressed = false
FEATURE [PartDesign::Body] Body384
  AllowCompound = false
  Group = -> [Clone385]
  Origin = -> Origin1238
  Placement = pos=(13,0,0) rot=(0,0,1;0rad)
  Tip = -> Clone385
FEATURE [PartDesign::FeatureBase] Clone386
  BaseFeature = -> Box164
  Placement = pos=(5,2.1,5.2) rot=(0,0,1;0rad)
  Suppressed = false
FEATURE [PartDesign::Body] Body385
  AllowCompound = false
  Group = -> [Clone386]
  Origin = -> Origin1239
  Placement = pos=(19,0,0) rot=(0,0,1;0rad)
  Tip = -> Clone386
FEATURE [PartDesign::FeatureBase] Clone387
  BaseFeature = -> Box164
  Placement = pos=(5,2.1,5.2) rot=(0,0,1;0rad)
  Suppressed = false
FEATURE [PartDesign::Body] Body386
  AllowCompound = false
  Group = -> [Clone387]
  Origin = -> Origin1240
  Placement = pos=(26,0,0) rot=(0,0,1;0rad)
  Tip = -> Clone387
FEATURE [PartDesign::FeatureBase] Clone388
  BaseFeature = -> Box164
  Placement = pos=(5,2.1,5.2) rot=(0,0,1;0rad)
  Suppressed = false
FEATURE [PartDesign::Body] Body387
  AllowCompound = false
  Group = -> [Clone388]
  Origin = -> Origin1241
  Placement = pos=(32,0,0) rot=(0,0,1;0rad)
  Tip = -> Clone388
FEATURE [PartDesign::FeatureBase] Clone389
  BaseFeature = -> Box164
  Placement = pos=(5,2.1,5.2) rot=(0,0,1;0rad)
  Suppressed = false
FEATURE [PartDesign::Body] Body388
  AllowCompound = false
  Group = -> [Clone389]
  Origin = -> Origin1242
  Placement = pos=(39,0,0) rot=(0,0,1;0rad)
  Tip = -> Clone389
FEATURE [PartDesign::FeatureBase] Clone390
  BaseFeature = -> Box164
  Placement = pos=(5,2.1,5.2) rot=(0,0,1;0rad)
  Suppressed = false
FEATURE [PartDesign::Body] Body389
  AllowCompound = false
  Group = -> [Clone390]
  Origin = -> Origin1243
  Placement = pos=(45,0,0) rot=(0,0,1;0rad)
  Tip = -> Clone390
FEATURE [PartDesign::FeatureBase] Clone391
  BaseFeature = -> Box164
  Placement = pos=(5,2.1,5.2) rot=(0,0,1;0rad)
  Suppressed = false
FEATURE [PartDesign::Body] Body390
  AllowCompound = false
  Group = -> [Clone391]
  Origin = -> Origin1244
  Placement = pos=(55,0,0) rot=(0,0,1;0rad)
  Tip = -> Clone391
FEATURE [PartDesign::FeatureBase] Clone392
  BaseFeature = -> Box164
  Placement = pos=(5,2.1,5.2) rot=(0,0,1;0rad)
  Suppressed = false
FEATURE [PartDesign::Body] Body391
  AllowCompound = false
  Group = -> [Clone392]
  Origin = -> Origin1245
  Placement = pos=(59,0,0) rot=(0,0,1;0rad)
  Tip = -> Clone392
FEATURE [Part::MultiFuse] Fusion110
  Shapes = -> [Body382,Body383,Body384,Body385,Body386,Body387,Body388,Body389,Body390,Body391]
FEATURE [PartDesign::FeatureBase] Clone393
  BaseFeature = -> Fusion110
  Suppressed = false
FEATURE [PartDesign::Body] Body392
  AllowCompound = false
  Group = -> [Clone393]
  Origin = -> Origin1246
  Placement = pos=(0,10,0) rot=(0,0,1;0rad)
  Tip = -> Clone393
FEATURE [PartDesign::FeatureBase] Clone394
  BaseFeature = -> Body392
  Placement = pos=(0,10,0) rot=(0,0,1;0rad)
  Suppressed = false
FEATURE [PartDesign::Body] Body393
  AllowCompound = false
  Group = -> [Clone394]
  Origin = -> Origin1247
  Placement = pos=(0,10,0) rot=(0,0,1;0rad)
  Tip = -> Clone394
FEATURE [PartDesign::FeatureBase] Clone395
  BaseFeature = -> Body393
  Placement = pos=(0,10,0) rot=(0,0,1;0rad)
  Suppressed = false
FEATURE [PartDesign::Body] Body394
  AllowCompound = false
  Group = -> [Clone395]
  Origin = -> Origin1248
  Placement = pos=(0,10,0) rot=(0,0,1;0rad)
  Tip = -> Clone395
FEATURE [PartDesign::FeatureBase] Clone396
  BaseFeature = -> Box164
  Placement = pos=(5,2.1,5.2) rot=(0,0,1;0rad)
  Suppressed = false
FEATURE [PartDesign::Body] Body395
  AllowCompound = false
  Group = -> [Clone396]
  Origin = -> Origin1249
  Placement = pos=(0,43,0) rot=(0,0,1;0rad)
  Tip = -> Clone396
FEATURE [PartDesign::FeatureBase] Clone397
  BaseFeature = -> Body395
  Placement = pos=(0,43,0) rot=(0,0,1;0rad)
  Suppressed = false
FEATURE [PartDesign::Body] Body396
  AllowCompound = false
  Group = -> [Clone397]
  Origin = -> Origin1250
  Placement = pos=(4,0,0) rot=(0,0,1;0rad)
  Tip = -> Clone397
FEATURE [PartDesign::FeatureBase] Clone398
  BaseFeature = -> Body396
  Placement = pos=(4,0,0) rot=(0,0,1;0rad)
  Suppressed = false
FEATURE [PartDesign::Body] Body397
  AllowCompound = false
  Group = -> [Clone398]
  Origin = -> Origin1251
  Placement = pos=(7,0,0) rot=(0,0,1;0rad)
  Tip = -> Clone398
FEATURE [PartDesign::FeatureBase] Clone399
  BaseFeature = -> Body397
  Placement = pos=(7,0,0) rot=(0,0,1;0rad)
  Suppressed = false
FEATURE [PartDesign::Body] Body398
  AllowCompound = false
  Group = -> [Clone399]
  Origin = -> Origin1252
  Placement = pos=(4,0,0) rot=(0,0,1;0rad)
  Tip = -> Clone399
FEATURE [PartDesign::FeatureBase] Clone400
  BaseFeature = -> Body398
  Placement = pos=(4,0,0) rot=(0,0,1;0rad)
  Suppressed = false
FEATURE [PartDesign::Body] Body399
  AllowCompound = false
  Group = -> [Clone400]
  Origin = -> Origin1253
  Placement = pos=(7,0,0) rot=(0,0,1;0rad)
  Tip = -> Clone400
FEATURE [PartDesign::FeatureBase] Clone401
  BaseFeature = -> Body399
  Placement = pos=(7,0,0) rot=(0,0,1;0rad)
  Suppressed = false
FEATURE [PartDesign::Body] Body400
  AllowCompound = false
  Group = -> [Clone401]
  Origin = -> Origin1254
  Placement = pos=(4,0,0) rot=(0,0,1;0rad)
  Tip = -> Clone401
FEATURE [PartDesign::FeatureBase] Clone402
  BaseFeature = -> Body400
  Placement = pos=(4,0,0) rot=(0,0,1;0rad)
  Suppressed = false
FEATURE [PartDesign::Body] Body401
  AllowCompound = false
  Group = -> [Clone402]
  Origin = -> Origin1255
  Placement = pos=(7,0,0) rot=(0,0,1;0rad)
  Tip = -> Clone402
FEATURE [PartDesign::FeatureBase] Clone403
  BaseFeature = -> Body401
  Placement = pos=(7,0,0) rot=(0,0,1;0rad)
  Suppressed = false
FEATURE [PartDesign::Body] Body402
  AllowCompound = false
  Group = -> [Clone403]
  Origin = -> Origin1256
  Placement = pos=(4,0,0) rot=(0,0,1;0rad)
  Tip = -> Clone403
FEATURE [PartDesign::FeatureBase] Clone404
  BaseFeature = -> Body402
  Placement = pos=(4,0,0) rot=(0,0,1;0rad)
  Suppressed = false
FEATURE [PartDesign::Body] Body403
  AllowCompound = false
  Group = -> [Clone404]
  Origin = -> Origin1257
  Placement = pos=(7,0,0) rot=(0,0,1;0rad)
  Tip = -> Clone404
FEATURE [PartDesign::FeatureBase] Clone405
  BaseFeature = -> Body403
  Placement = pos=(7,0,0) rot=(0,0,1;0rad)
  Suppressed = false
FEATURE [PartDesign::Body] Body404
  AllowCompound = false
  Group = -> [Clone405]
  Origin = -> Origin1258
  Placement = pos=(4,0,0) rot=(0,0,1;0rad)
  Tip = -> Clone405
FEATURE [PartDesign::FeatureBase] Clone406
  BaseFeature = -> Body404
  Placement = pos=(4,0,0) rot=(0,0,1;0rad)
  Suppressed = false
FEATURE [PartDesign::Body] Body405
  AllowCompound = false
  Group = -> [Clone406]
  Origin = -> Origin1259
  Placement = pos=(7,0,0) rot=(0,0,1;0rad)
  Tip = -> Clone406
FEATURE [PartDesign::FeatureBase] Clone407
  BaseFeature = -> Body405
  Placement = pos=(7,0,0) rot=(0,0,1;0rad)
  Suppressed = false
FEATURE [PartDesign::Body] Body406
  AllowCompound = false
  Group = -> [Clone407]
  Origin = -> Origin1260
  Placement = pos=(4,0,0) rot=(0,0,1;0rad)
  Tip = -> Clone407
FEATURE [Part::MultiFuse] Fusion111
  Shapes = -> [Body395,Body396,Body397,Body398,Body399,Body400,Body401,Body402,Body403,Body404,Body405,Body406]
FEATURE [PartDesign::FeatureBase] Clone408
  BaseFeature = -> Fusion111
  Suppressed = false
FEATURE [PartDesign::Body] Body407
  AllowCompound = false
  Group = -> [Clone408]
  Origin = -> Origin1261
  Placement = pos=(0,10,0) rot=(0,0,1;0rad)
  Tip = -> Clone408
FEATURE [PartDesign::FeatureBase] Clone409
  BaseFeature = -> Body407
  Placement = pos=(0,10,0) rot=(0,0,1;0rad)
  Suppressed = false
FEATURE [PartDesign::Body] Body408
  AllowCompound = false
  Group = -> [Clone409]
  Origin = -> Origin1262
  Placement = pos=(0,10,0) rot=(0,0,1;0rad)
  Tip = -> Clone409
FEATURE [PartDesign::FeatureBase] Clone410
  BaseFeature = -> Body408
  Placement = pos=(0,10,0) rot=(0,0,1;0rad)
  Suppressed = false
FEATURE [PartDesign::Body] Body409
  AllowCompound = false
  Group = -> [Clone410]
  Origin = -> Origin1263
  Placement = pos=(0,10,0) rot=(0,0,1;0rad)
  Tip = -> Clone410
FEATURE [PartDesign::FeatureBase] Clone411
  BaseFeature = -> Body409
  Placement = pos=(0,10,0) rot=(0,0,1;0rad)
  Suppressed = false
FEATURE [PartDesign::Body] Body410
  AllowCompound = false
  Group = -> [Clone411]
  Origin = -> Origin1264
  Placement = pos=(0,10,0) rot=(0,0,1;0rad)
  Tip = -> Clone411
FEATURE [Part::MultiFuse] Fusion112
  Placement = pos=(0,-0.2,0) rot=(1,0,0;-0.034907rad)
  Shapes = -> [Fusion110,Body392,Body393,Body394,Fusion111,Body407,Body408,Body409,Body410]
FEATURE [Part::MultiFuse] Fusion040
  Refine = true
  Shapes = -> [Cylinder031,Cylinder032,Cylinder030,Cylinder029,Fusion112]
FEATURE [Part::Box] Box165  label="Cube161"
  AttacherType = Attacher::AttachEngine3D
  Height = 1
  Length = 1
  Placement = pos=(12.5,43,5.6) rot=(0,0,1;0rad)
  Width = 55.336
FEATURE [Part::Box] Box166  label="Cube162"
  AttacherType = Attacher::AttachEngine3D
  Height = 1
  Length = 1
  Placement = pos=(27.5,1,5.6) rot=(0,0,1;0rad)
  Width = 41.5
FEATURE [Part::Box] Box167  label="Cube163"
  AttacherType = Attacher::AttachEngine3D
  Height = 1
  Length = 1
  Placement = pos=(40.5,1,5.6) rot=(0,0,1;0rad)
  Width = 41.5
FEATURE [Part::Box] Box168  label="Cube164"
  AttacherType = Attacher::AttachEngine3D
  Height = 1
  Length = 1
  Placement = pos=(54.7,1,5.6) rot=(0,0,1;0rad)
  Width = 41.5
FEATURE [Part::Box] Box169  label="Cube165"
  AttacherType = Attacher::AttachEngine3D
  Height = 1
  Length = 66
  Placement = pos=(2,42.7,5.6) rot=(0,0,1;0rad)
  Width = 1
FEATURE [Part::Box] Box170  label="Cube166"
  AttacherType = Attacher::AttachEngine3D
  Height = 1
  Length = 1
  Placement = pos=(14.5,1,5.6) rot=(0,0,1;0rad)
  Width = 41.5
FEATURE [Part::Box] Box171  label="Cube167"
  AttacherType = Attacher::AttachEngine3D
  Height = 1
  Length = 1
  Placement = pos=(23.5,43,5.6) rot=(0,0,1;0rad)
  Width = 55.336
FEATURE [Part::Box] Box172  label="Cube168"
  AttacherType = Attacher::AttachEngine3D
  Height = 1
  Length = 1
  Placement = pos=(45.5,43,5.6) rot=(0,0,1;0rad)
  Width = 55.336
FEATURE [Part::Box] Box173  label="Cube169"
  AttacherType = Attacher::AttachEngine3D
  Height = 1
  Length = 1
  Placement = pos=(34.5,43,5.6) rot=(0,0,1;0rad)
  Width = 55.336
FEATURE [Part::Box] Box174  label="Cube170"
  AttacherType = Attacher::AttachEngine3D
  Height = 1
  Length = 1
  Placement = pos=(56.5,43,5.6) rot=(0,0,1;0rad)
  Width = 55.336
FEATURE [Part::MultiFuse] Fusion113
  Placement = pos=(0,0,0) rot=(1,0,0;-0.034907rad)
  Shapes = -> [Box165,Box166,Box167,Box168,Box169,Box170,Box171,Box172,Box173,Box174]
FEATURE [Part::MultiFuse] Fusion109
  Shapes = -> [Cut105,Cut026,Cut012,Fusion035,Fusion015,Chamfer006,Chamfer005,Cut107,Cut108,Fusion113]
FEATURE [Part::Cut] Cut109
  Base = -> Fusion109
  Refine = true
  Tool = -> Fusion040
